FCSTD DOCUMENT  (FreeCAD 1.0R39319 (Git))
Label: VectoraCNC
License: All rights reserved
LicenseURL: https://en.wikipedia.org/wiki/All_rights_reserved
objects: Part::FeaturePython×161, Part::Feature×121, Sketcher::SketchObject×120, PartDesign::Body×96, PartDesign::Pad×71, PartDesign::FeatureBase×57, App::Part×42, PartDesign::Pocket×41, PartDesign::Hole×31, PartDesign::LinearPattern×14, PartDesign::ShapeBinder×12, PartDesign::Chamfer×5, PartDesign::PolarPattern×4, PartDesign::Revolution×2, PartDesign::Fillet×2, PartDesign::Thickness×2, PartDesign::SubtractiveHelix×1, Measure::MeasureRadius×1, App::DocumentObjectGroup×1
note: 1245 computed .brp shape members not serialized (recipe doc carries the construction recipe); baked Part::Feature solids carry a one-line shape summary decoded from their .brp

FEATURE [Sketcher::SketchObject] Sketch
  ArcFitTolerance = 1e-06
  AttachmentSupport = -> [Origin]
  FullyConstrained = true
  MakeInternals = false
  MapMode = 5
  Placement = pos=(0,0,0) rot=(1,0,0;1.5708rad)
  sketch-geometry (1):
    g0: Circle CenterX=0 CenterY=0 CenterZ=0 NormalX=0 NormalY=0 NormalZ=1 AngleXU=0 Radius=5
  constraints (2):
    c: Diameter(g0) = 10
    c: Coincident(g0,g-1)
FEATURE [PartDesign::Pad] Pad
  Direction = (0,-1,0)
  Length = 440
  Length2 = 10
  Profile = -> Sketch [Edge1]
  ReferenceAxis = -> Sketch [N_Axis]
  Refine = true
  Suppressed = false
  Type = 0
FEATURE [PartDesign::Body] Body  label="10mmx400mm"
  AllowCompound = false
  Group = -> [Sketch,Pad]
  Origin = -> Origin
  Tip = -> Pad
FEATURE [Sketcher::SketchObject] Sketch001
  ArcFitTolerance = 1e-06
  AttachmentSupport = -> [Origin004]
  FullyConstrained = true
  MakeInternals = false
  MapMode = 5
  Placement = pos=(0,0,0) rot=(1,0,0;1.5708rad)
  sketch-geometry (18):
    g0: LineSegment [constr] StartX=-10 StartY=-10 StartZ=0 EndX=10 EndY=-10 EndZ=0
    g1: LineSegment [constr] StartX=10 StartY=-10 StartZ=0 EndX=10 EndY=10 EndZ=0
    g2: LineSegment StartX=10 StartY=10 StartZ=0 EndX=3.1 EndY=10 EndZ=0
    g3: LineSegment [constr] StartX=-10 StartY=10 StartZ=0 EndX=-10 EndY=-10 EndZ=0
    g4: GeomPoint [constr] X=0 Y=0 Z=0
    g5: LineSegment StartX=-3.1 StartY=10 StartZ=0 EndX=-3.1 EndY=8 EndZ=0
    g6: LineSegment StartX=-3.1 StartY=8 StartZ=0 EndX=-5.5 EndY=8 EndZ=0
    g7: LineSegment StartX=-5.5 StartY=8 StartZ=0 EndX=-5.5 EndY=6.3 EndZ=0
    g8: LineSegment StartX=-5.5 StartY=6.3 StartZ=0 EndX=-3.1 EndY=3.9 EndZ=0
    g9: LineSegment StartX=-3.1 StartY=3.9 StartZ=0 EndX=3.1 EndY=3.9 EndZ=0
    g10: LineSegment StartX=3.1 StartY=3.9 StartZ=0 EndX=5.5 EndY=6.3 EndZ=0
    g11: LineSegment StartX=5.5 StartY=6.3 StartZ=0 EndX=5.5 EndY=8 EndZ=0
    g12: LineSegment StartX=5.5 StartY=8 StartZ=0 EndX=3.1 EndY=8 EndZ=0
    g13: LineSegment StartX=3.1 StartY=8 StartZ=0 EndX=3.1 EndY=10 EndZ=0
    g14: GeomPoint X=0 Y=3.9 Z=0
    g15: LineSegment StartX=-3.1 StartY=10 StartZ=0 EndX=-10 EndY=10 EndZ=0
    g16: LineSegment StartX=10 StartY=10 StartZ=0 EndX=0 EndY=0 EndZ=0
    g17: LineSegment StartX=0 StartY=0 StartZ=0 EndX=-10 EndY=10 EndZ=0
  constraints (47):
    c: Coincident(g0,g1)
    c: Coincident(g1,g2)
    c: Coincident(g15,g3)
    c: Coincident(g3,g0)
    c: Horizontal(g0)
    c: Vertical(g1)
    c: Vertical(g3)
    c: Symmetric(g2,g0,g4)
    c: Distance(g1,g3) = 20
    c: Distance(g0,g15) = 20
    c: Coincident(g4,g-1)
    c: Vertical(g5)
    c: Coincident(g5,g6)
    c: Horizontal(g6)
    c: Coincident(g6,g7)
    c: Vertical(g7)
    c: Coincident(g7,g8)
    c: Coincident(g8,g9)
    c: Horizontal(g9)
    c: Coincident(g9,g10)
    c: Coincident(g10,g11)
    c: Vertical(g11)
    c: Coincident(g11,g12)
    c: Horizontal(g12)
    c: Coincident(g12,g13)
    c: Vertical(g13)
    c: Angle(g9,g8) = 2.35619
    c: Angle(g10,g9) = 2.35619
    c: Equal(g7,g11)
    c: Equal(g12,g6)
    c: Horizontal(g5,g12)
    c: Symmetric(g9,g9,g14)
    c: PointOnObject(g14,g-2)
    c: Horizontal(g2)
    c: Horizontal(g15)
    c: Coincident(g5,g15)
    c: Coincident(g13,g2)
    c: Horizontal(g5,g2)
    c: Distance(g13,g13) = 2
    c: DistanceX(g6,g11) = 11
    c: DistanceX(g5,g2) = 6.2
    c: DistanceY(g9,g11) = 4.1
    c: Vertical(g5,g8)
    c: Coincident(g16,g1)
    c: Coincident(g16,g4)
    c: Coincident(g17,g4)
    c: Coincident(g17,g3)
FEATURE [PartDesign::Pad] Pad001
  Direction = (0,-1,2e-16)
  Length = 10
  Length2 = 10
  Profile = -> Sketch001
  ReferenceAxis = -> Sketch001 [N_Axis]
  Refine = true
  Suppressed = false
  Type = 0
FEATURE [PartDesign::PolarPattern] PolarPattern
  Angle = 360
  Axis = -> Sketch001 [N_Axis]
  BaseFeature = -> Pad001
  Mode = 0
  Occurrences = 4
  Offset = 120
  Originals = -> [Pad001]
  Refine = true
  Suppressed = false
  TransformMode = 0
FEATURE [Sketcher::SketchObject] Sketch002
  ArcFitTolerance = 1e-06
  AttachmentSupport = -> [PolarPattern]
  FullyConstrained = true
  MakeInternals = false
  MapMode = 5
  Placement = pos=(0,-10,0) rot=(1,0,0;1.5708rad)
  sketch-geometry (3):
    g0: GeomPoint X=0 Y=0 Z=0
    g1: GeomPoint X=0 Y=0 Z=0
    g2: Circle CenterX=0 CenterY=0 CenterZ=0 NormalX=0 NormalY=0 NormalZ=1 AngleXU=0 Radius=3.52328
  constraints (4):
    c: Coincident(g1,g0)
    c: Coincident(g0,g-1)
    c: Coincident(g2,g0)
    c: Diameter(g2) = 7.04656
FEATURE [PartDesign::Hole] Hole
  BaseFeature = -> PolarPattern
  CustomThreadClearance = 0
  Depth = 25
  DepthType = 0
  Diameter = 5
  DrillForDepth = false
  DrillPoint = 1
  DrillPointAngle = 118
  HoleCutCountersinkAngle = 90
  HoleCutCustomValues = false
  HoleCutDepth = 0
  HoleCutDiameter = 0
  HoleCutType = 0
  ModelThread = false
  Profile = -> Sketch002
  Refine = true
  Suppressed = false
  Tapered = false
  TaperedAngle = 90
  ThreadClass = 0
  ThreadDepth = 25
  ThreadDepthType = 0
  ThreadDirection = 0
  ThreadFit = 0
  ThreadSize = 0
  ThreadType = 0
  Threaded = false
  UseCustomThreadClearance = false
FEATURE [PartDesign::Body] Body001  label="2020"
  AllowCompound = false
  Group = -> [Sketch001,Pad001,PolarPattern,Sketch002,Hole]
  Origin = -> Origin004
  Tip = -> Hole
FEATURE [Sketcher::SketchObject] Sketch003
  ArcFitTolerance = 1e-06
  AttachmentSupport = -> [Origin012]
  FullyConstrained = true
  MakeInternals = false
  MapMode = 5
  sketch-geometry (1):
    g0: Circle CenterX=0 CenterY=0 CenterZ=0 NormalX=0 NormalY=0 NormalZ=1 AngleXU=0 Radius=4
  constraints (2):
    c: Diameter(g0) = 8
    c: Coincident(g0,g-1)
FEATURE [PartDesign::Pad] Pad003
  Direction = (0,0,1)
  Length = 10
  Length2 = 10
  Profile = -> Sketch003
  ReferenceAxis = -> Sketch003 [N_Axis]
  Refine = true
  Suppressed = false
  Type = 0
FEATURE [Sketcher::SketchObject] Sketch004
  ArcFitTolerance = 1e-06
  AttachmentSupport = -> [Origin012]
  ExternalGeometry = -> [Pad003]
  FullyConstrained = true
  MakeInternals = false
  MapMode = 5
  Placement = pos=(0,0,0) rot=(0.57735,0.57735,0.57735;2.0944rad)
  sketch-geometry (4):
    g0: LineSegment StartX=4 StartY=0 StartZ=0 EndX=4 EndY=1 EndZ=0
    g1: LineSegment StartX=4 StartY=1 StartZ=0 EndX=3 EndY=1 EndZ=0
    g2: LineSegment StartX=3 StartY=1 StartZ=0 EndX=3 EndY=0 EndZ=0
    g3: LineSegment StartX=3 StartY=0 StartZ=0 EndX=4 EndY=0 EndZ=0
  constraints (11):
    c: Coincident(g0,g1)
    c: Coincident(g1,g2)
    c: Coincident(g2,g3)
    c: Coincident(g3,g0)
    c: Vertical(g0)
    c: Vertical(g2)
    c: Horizontal(g1)
    c: Horizontal(g3)
    c: Distance(g0,g2) = 1
    c: Distance(g1,g3) = 1
    c: Coincident(g0,g-9)
FEATURE [PartDesign::SubtractiveHelix] SubtractiveHelix
  Angle = 0
  Axis = (0,0,1)
  Base = (0,0,0)
  BaseFeature = -> Pad003
  Growth = 0
  HasBeenEdited = true
  Height = 100
  LeftHanded = false
  Mode = 0
  Outside = false
  Pitch = 2
  Profile = -> Sketch004
  ReferenceAxis = -> Sketch004 [V_Axis]
  Refine = true
  Suppressed = false
  Tolerance = 0.1
  Turns = 50
FEATURE [PartDesign::Body] Body004  label="T8 Lead Screw"
  AllowCompound = false
  Group = -> [Sketch003,Pad003,Sketch004,SubtractiveHelix]
  Origin = -> Origin012
  Tip = -> SubtractiveHelix
FEATURE [Sketcher::SketchObject] Sketch005
  ArcFitTolerance = 1e-06
  AttachmentSupport = -> [Origin014]
  FullyConstrained = true
  MakeInternals = false
  MapMode = 5
  sketch-geometry (2):
    g0: Circle CenterX=0 CenterY=0 CenterZ=0 NormalX=0 NormalY=0 NormalZ=1 AngleXU=0 Radius=9.5
    g1: Circle CenterX=0 CenterY=0 CenterZ=0 NormalX=0 NormalY=0 NormalZ=1 AngleXU=0 Radius=5
  constraints (4):
    c: Diameter(g0) = 19
    c: Coincident(g0,g-1)
    c: Diameter(g1) = 10
    c: Coincident(g1,g0)
FEATURE [PartDesign::Pad] Pad004
  Direction = (0,0,1)
  Length = 55
  Length2 = 10
  Profile = -> Sketch005
  ReferenceAxis = -> Sketch005 [N_Axis]
  Refine = true
  Suppressed = false
  Type = 0
FEATURE [PartDesign::Body] Body005  label="LM10UU"
  AllowCompound = false
  Group = -> [Sketch005,Pad004]
  Origin = -> Origin014
  Tip = -> Pad004
FEATURE [Sketcher::SketchObject] Sketch006
  ArcFitTolerance = 1e-06
  AttachmentSupport = -> [Origin016]
  FullyConstrained = true
  MakeInternals = false
  MapMode = 5
  sketch-geometry (2):
    g0: Circle CenterX=0 CenterY=0 CenterZ=0 NormalX=0 NormalY=0 NormalZ=1 AngleXU=0 Radius=11
    g1: Circle CenterX=0 CenterY=0 CenterZ=0 NormalX=0 NormalY=0 NormalZ=1 AngleXU=0 Radius=4
  constraints (4):
    c: Diameter(g0) = 22
    c: Coincident(g0,g-1)
    c: Diameter(g1) = 8
    c: Coincident(g1,g0)
FEATURE [PartDesign::Pad] Pad005
  Direction = (0,0,1)
  Length = 7
  Length2 = 10
  Profile = -> Sketch006
  ReferenceAxis = -> Sketch006 [N_Axis]
  Refine = true
  Suppressed = false
  Type = 0
FEATURE [PartDesign::Body] Body006  label="608ZZ"
  AllowCompound = false
  Group = -> [Sketch006,Pad005]
  Origin = -> Origin016
  Tip = -> Pad005
FEATURE [PartDesign::FeatureBase] Clone005
  BaseFeature = -> Body005
  Suppressed = false
FEATURE [PartDesign::Body] Body010  label="LM10UU001"
  AllowCompound = false
  Group = -> [Clone005]
  Origin = -> Origin024
  Tip = -> Clone005
FEATURE [PartDesign::ShapeBinder] CopyClone005
  TraceSupport = false
FEATURE [Sketcher::SketchObject] Sketch007
  ArcFitTolerance = 1e-06
  AttachmentSupport = -> [CopyClone005]
  ExternalGeometry = -> [CopyClone005]
  FullyConstrained = true
  MakeInternals = false
  MapMode = 5
  Placement = pos=(0,0,0) rot=(1,0,0;3.14159rad)
  sketch-geometry (8):
    g0: ArcOfCircle CenterX=0 CenterY=0 CenterZ=0 NormalX=0 NormalY=0 NormalZ=1 AngleXU=0 Radius=16 StartAngle=0 EndAngle=3.14159
    g1: LineSegment StartX=-16 StartY=2e-15 StartZ=0 EndX=-28 EndY=2.2e-15 EndZ=0
    g2: LineSegment StartX=-28 StartY=2.2e-15 StartZ=0 EndX=-28 EndY=-13 EndZ=0
    g3: LineSegment StartX=-28 StartY=-13 StartZ=0 EndX=28 EndY=-13 EndZ=0
    g4: LineSegment StartX=28 StartY=-13 StartZ=0 EndX=28 EndY=0 EndZ=0
    g5: LineSegment StartX=28 StartY=0 StartZ=0 EndX=16 EndY=0 EndZ=0
    g6: GeomPoint X=0 Y=-13 Z=0
    g7: Circle CenterX=0 CenterY=0 CenterZ=0 NormalX=0 NormalY=0 NormalZ=1 AngleXU=0 Radius=9.6
  constraints (20):
    c: Radius(g0) = 16
    c: Coincident(g0,g-3)
    c: PointOnObject(g0,g-1)
    c: PointOnObject(g0,g-1)
    c: Perpendicular(g0,g1) = 4.71239
    c: Coincident(g1,g2)
    c: Coincident(g2,g3)
    c: Horizontal(g3)
    c: Coincident(g3,g4)
    c: PointOnObject(g4,g-1)
    c: Vertical(g4)
    c: Coincident(g4,g5)
    c: Coincident(g5,g0)
    c: Vertical(g2)
    c: Symmetric(g3,g3,g6)
    c: PointOnObject(g6,g-2)
    c: Distance(g-3,g3) = 3.5
    c: DistanceX(g3,g3) = 56
    c: Coincident(g7,g0)
    c: Distance(g7,g-3) = 0.1
FEATURE [PartDesign::Pad] Pad006
  Direction = (0,0,-1)
  Length = 10
  Length2 = 10
  Profile = -> Sketch007
  ReferenceAxis = -> Sketch007 [N_Axis]
  Refine = true
  Suppressed = false
  Type = 3
  UpToFace = -> Clone005 [Face4]
FEATURE [PartDesign::FeatureBase] Clone007
  BaseFeature = -> Body005
  Suppressed = false
FEATURE [PartDesign::Body] Body013  label="LM10UU002"
  AllowCompound = false
  Group = -> [Clone007]
  Origin = -> Origin056
  Tip = -> Clone007
FEATURE [PartDesign::FeatureBase] Clone008
  BaseFeature = -> Body005
  Suppressed = false
FEATURE [PartDesign::Body] Body014  label="LM10UU003"
  AllowCompound = false
  Group = -> [Clone008]
  Origin = -> Origin058
  Tip = -> Clone008
FEATURE [PartDesign::FeatureBase] Clone009
  BaseFeature = -> Body005
  Suppressed = false
FEATURE [PartDesign::Body] Body015  label="LM10UU004"
  AllowCompound = false
  Group = -> [Clone009]
  Origin = -> Origin060
  Tip = -> Clone009
FEATURE [Sketcher::SketchObject] Sketch008
  ArcFitTolerance = 1e-06
  AttachmentSupport = -> [Pad006]
  ExternalGeometry = -> [Pad006]
  FullyConstrained = true
  MakeInternals = false
  MapMode = 5
  Placement = pos=(0,-1.6e-15,0) rot=(1,0,0;1.5708rad)
  sketch-geometry (7):
    g0: GeomPoint X=-22 Y=47.5 Z=0
    g1: GeomPoint X=-22 Y=7.5 Z=0
    g2: GeomPoint X=22 Y=7.5 Z=0
    g3: GeomPoint X=22 Y=47.5 Z=0
    g4: GeomPoint [constr] X=22 Y=27.5 Z=0
    g5: GeomPoint [constr] X=-22 Y=27.5 Z=0
    g6: LineSegment [constr] StartX=-22 StartY=47.5 StartZ=0 EndX=-22 EndY=7.5 EndZ=0
  constraints (11):
    c: Symmetric(g-5,g-6,g5)
    c: Symmetric(g-9,g-10,g4)
    c: Vertical(g2,g3)
    c: Vertical(g3,g4)
    c: Horizontal(g0,g3)
    c: Horizontal(g1,g2)
    c: Coincident(g6,g0)
    c: Coincident(g6,g1)
    c: Symmetric(g6,g6,g5)
    c: DistanceY(g6,g6) = 40
    c: Vertical(g6)
FEATURE [PartDesign::Hole] Hole001
  BaseFeature = -> Pad006
  CustomThreadClearance = 0
  Depth = 25
  DepthType = 0
  Diameter = 1.2
  DrillForDepth = false
  DrillPoint = 1
  DrillPointAngle = 118
  HoleCutCountersinkAngle = 90
  HoleCutCustomValues = true
  HoleCutDepth = 0.1
  HoleCutDiameter = 1.3
  HoleCutType = 4
  ModelThread = false
  Profile = -> Sketch008
  Refine = true
  Suppressed = false
  Tapered = false
  TaperedAngle = 90
  ThreadClass = 0
  ThreadDepth = 25
  ThreadDepthType = 0
  ThreadDirection = 0
  ThreadFit = 0
  ThreadSize = 0
  ThreadType = 1
  Threaded = false
  UseCustomThreadClearance = false
FEATURE [PartDesign::Body] Body011  label="BearingHolder"
  AllowCompound = false
  Group = -> [CopyClone005,Sketch007,Pad006,Sketch008,Hole001]
  Origin = -> Origin028
  Tip = -> Hole001
FEATURE [PartDesign::FeatureBase] Clone006
  BaseFeature = -> Body011
  Suppressed = false
FEATURE [PartDesign::Body] Body012  label="BearingHolder002"
  AllowCompound = false
  Group = -> [Clone006]
  Origin = -> Origin054
  Tip = -> Clone006
FEATURE [PartDesign::FeatureBase] Clone010
  BaseFeature = -> Body011
  Suppressed = false
FEATURE [PartDesign::Body] Body016  label="BearingHolder003"
  AllowCompound = false
  Group = -> [Clone010]
  Origin = -> Origin062
  Tip = -> Clone010
FEATURE [PartDesign::FeatureBase] Clone011
  BaseFeature = -> Body011
  Suppressed = false
FEATURE [PartDesign::Body] Body017  label="BearingHolder004"
  AllowCompound = false
  Group = -> [Clone011]
  Origin = -> Origin064
  Tip = -> Clone011
FEATURE [PartDesign::FeatureBase] Clone012
  BaseFeature = -> Body011
  Suppressed = false
FEATURE [PartDesign::Body] Body018  label="BearingHolder001"
  AllowCompound = false
  Group = -> [Clone012]
  Origin = -> Origin066
  Tip = -> Clone012
FEATURE [App::Part] Part002  label="Bearing001"
  Group = -> [Body010,Body018]
  Origin = -> Origin026
  Placement = pos=(0,0,100) rot=(0,0,1;0rad)
FEATURE [App::Part] Part009  label="Bearing002"
  Group = -> [Body012,Body013]
  Origin = -> Origin068
FEATURE [App::Part] Part010  label="Bearing003"
  Group = -> [Body016,Body014]
  Origin = -> Origin070
  Placement = pos=(200,0,100) rot=(0,0,1;0rad)
FEATURE [App::Part] Part011  label="Bearing004"
  Group = -> [Body017,Body015]
  Origin = -> Origin072
  Placement = pos=(200,0,0) rot=(0,0,1;0rad)
FEATURE [App::Part] Part008  label="Bearings"
  Group = -> [Part002,Part009,Part010,Part011]
  Origin = -> Origin052
  Placement = pos=(12.5,40,-23) rot=(0.57735,0.57735,0.57735;2.0944rad)
FEATURE [Sketcher::SketchObject] Sketch145
  ArcFitTolerance = 1e-06
  AttachmentSupport = -> [XY_Plane957]
  FullyConstrained = true
  MakeInternals = false
  MapMode = 5
  sketch-geometry (2):
    g0: Circle CenterX=0 CenterY=0 CenterZ=0 NormalX=0 NormalY=0 NormalZ=1 AngleXU=0 Radius=9.5
    g1: Circle CenterX=0 CenterY=0 CenterZ=0 NormalX=0 NormalY=0 NormalZ=1 AngleXU=0 Radius=2.5
  constraints (4):
    c: Diameter(g0) = 19
    c: Coincident(g0,g-1)
    c: Diameter(g1) = 5
    c: Coincident(g1,g0)
FEATURE [PartDesign::Pad] Pad067
  Direction = (0,0,1)
  Length = 25
  Length2 = 10
  Profile = -> Sketch145
  ReferenceAxis = -> Sketch145 [N_Axis]
  Suppressed = false
  Type = 0
FEATURE [PartDesign::Hole] Hole015
  BaseFeature = -> Pad067
  CustomThreadClearance = 0
  Depth = 12.5
  DepthType = 0
  Diameter = 8
  DrillForDepth = false
  DrillPoint = 1
  DrillPointAngle = 118
  HoleCutCountersinkAngle = 90
  HoleCutCustomValues = false
  HoleCutDepth = 0
  HoleCutDiameter = 6.1
  HoleCutType = 0
  ModelThread = false
  Profile = -> Pad067 [Edge6]
  Suppressed = false
  Tapered = false
  TaperedAngle = 90
  ThreadClass = 0
  ThreadDepth = 12.5
  ThreadDepthType = 0
  ThreadDirection = 0
  ThreadFit = 0
  ThreadSize = 0
  ThreadType = 0
  Threaded = false
  UseCustomThreadClearance = false
FEATURE [Sketcher::SketchObject] Sketch146
  ArcFitTolerance = 1e-06
  AttachmentSupport = -> [YZ_Plane957]
  ExternalGeometry = -> [Hole015]
  FullyConstrained = true
  MakeInternals = false
  MapMode = 5
  Placement = pos=(0,0,0) rot=(0.57735,0.57735,0.57735;2.0944rad)
  sketch-geometry (4):
    g0: Circle CenterX=0 CenterY=18.75 CenterZ=0 NormalX=0 NormalY=0 NormalZ=1 AngleXU=0 Radius=1.5
    g1: Circle CenterX=0 CenterY=6.25 CenterZ=0 NormalX=0 NormalY=0 NormalZ=1 AngleXU=0 Radius=1.5
    g2: GeomPoint X=0 Y=25 Z=0
    g3: GeomPoint X=0 Y=12.5 Z=0
  constraints (6):
    c: Symmetric(g-5,g-5,g2)
    c: Symmetric(g-4,g-4,g3)
    c: Symmetric(g3,g-1,g1)
    c: Symmetric(g2,g3,g0)
    c: Equal(g0,g1)
    c: Diameter(g0) = 3
FEATURE [PartDesign::Pocket] Pocket056
  BaseFeature = -> Hole015
  Direction = (-1,0,0)
  Length = 5
  Length2 = 5
  Profile = -> Sketch146
  ReferenceAxis = -> Sketch146 [N_Axis]
  Suppressed = false
  Type = 1
FEATURE [PartDesign::Body] Body055  label="Coupling 5x8"
  AllowCompound = false
  Group = -> [Sketch145,Pad067,Hole015,Sketch146,Pocket056]
  Origin = -> Origin957
  Tip = -> Pocket056
FEATURE [Sketcher::SketchObject] Sketch150
  ArcFitTolerance = 1e-06
  AttachmentSupport = -> [YZ_Plane960]
  FullyConstrained = true
  MakeInternals = false
  MapMode = 5
  Placement = pos=(0,0,0) rot=(0.57735,0.57735,0.57735;2.0944rad)
  sketch-geometry (8):
    g0: LineSegment StartX=0 StartY=0 StartZ=0 EndX=0 EndY=15 EndZ=0
    g1: LineSegment StartX=0 StartY=15 StartZ=0 EndX=5.1 EndY=15 EndZ=0
    g2: LineSegment StartX=5.1 StartY=15 StartZ=0 EndX=5.1 EndY=13.5 EndZ=0
    g3: LineSegment StartX=5.1 StartY=13.5 StartZ=0 EndX=11 EndY=13.5 EndZ=0
    g4: LineSegment StartX=11 StartY=13.5 StartZ=0 EndX=11 EndY=10 EndZ=0
    g5: LineSegment StartX=11 StartY=10 StartZ=0 EndX=5.1 EndY=10 EndZ=0
    g6: LineSegment StartX=5.1 StartY=10 StartZ=0 EndX=5.1 EndY=0 EndZ=0
    g7: LineSegment StartX=5.1 StartY=0 StartZ=0 EndX=0 EndY=0 EndZ=0
  constraints (23):
    c: Vertical(g0)
    c: Coincident(g0,g1)
    c: Horizontal(g1)
    c: Coincident(g1,g2)
    c: Vertical(g2)
    c: Coincident(g2,g3)
    c: Horizontal(g3)
    c: Coincident(g3,g4)
    c: Vertical(g4)
    c: Coincident(g4,g5)
    c: Horizontal(g5)
    c: Coincident(g5,g6)
    c: PointOnObject(g6,g-1)
    c: Vertical(g6)
    c: Coincident(g6,g7)
    c: Coincident(g7,g0)
    c: Coincident(g0,g-1)
    c: Vertical(g5,g2)
    c: Distance(g2,g2) = 1.5
    c: Distance(g4,g4) = 3.5
    c: DistanceY(g6,g6) = 10
    c: DistanceX(g-1,g3) = 11
    c: DistanceX(g1,g1) = 5.1
FEATURE [PartDesign::Revolution] Revolution007
  Angle = 360
  Angle2 = 60
  Axis = (0,0,1)
  Base = (0,0,0)
  Placement = pos=(0,0,0) rot=(1,1,1;2.0944rad)
  Profile = -> Sketch150
  ReferenceAxis = -> Sketch150 [V_Axis]
  Refine = true
  Reversed = true
  Suppressed = false
  Type = 0
FEATURE [Sketcher::SketchObject] Sketch151
  ArcFitTolerance = 1e-06
  AttachmentSupport = -> [Revolution007]
  FullyConstrained = true
  MakeInternals = false
  MapMode = 5
  Placement = pos=(-3.3e-15,0,15) rot=(0,0,-1;1.5708rad)
  sketch-geometry (2):
    g0: Circle CenterX=0 CenterY=0 CenterZ=0 NormalX=0 NormalY=0 NormalZ=1 AngleXU=0 Radius=4
    g1: Circle CenterX=8 CenterY=0 CenterZ=0 NormalX=0 NormalY=0 NormalZ=1 AngleXU=0 Radius=1.75
  constraints (5):
    c: Coincident(g0,g-1)
    c: PointOnObject(g1,g-1)
    c: DistanceX(g-1,g1) = 8
    c: Diameter(g0) = 8
    c: Diameter(g1) = 3.5
FEATURE [PartDesign::Pocket] Pocket057
  BaseFeature = -> Revolution007
  Direction = (0,0,-1)
  Length = 5
  Length2 = 5
  Placement = pos=(0,0,0) rot=(1,1,1;2.0944rad)
  Profile = -> Sketch151
  ReferenceAxis = -> Sketch151 [N_Axis]
  Refine = true
  Suppressed = false
  Type = 1
FEATURE [PartDesign::PolarPattern] PolarPattern010
  Angle = 360
  Axis = -> Sketch151 [N_Axis]
  BaseFeature = -> Pocket057
  Mode = 0
  Occurrences = 4
  Offset = 120
  Originals = -> [Pocket057]
  Placement = pos=(0,0,0) rot=(1,1,1;2.0944rad)
  Refine = true
  Suppressed = false
  TransformMode = 0
FEATURE [PartDesign::Body] Body058  label="T8 Nut"
  AllowCompound = false
  Group = -> [Sketch150,Revolution007,Sketch151,Pocket057,PolarPattern010]
  Origin = -> Origin960
  Tip = -> PolarPattern010
FEATURE [PartDesign::FeatureBase] Clone013
  BaseFeature = -> Body058
  Suppressed = false
FEATURE [PartDesign::Body] Body059  label="T8 Nut001"
  AllowCompound = false
  Group = -> [Clone013]
  Origin = -> Origin1200
  Tip = -> Clone013
FEATURE [PartDesign::FeatureBase] Clone014
  BaseFeature = -> Body004
  Suppressed = false
FEATURE [PartDesign::LinearPattern] LinearPattern001
  BaseFeature = -> Clone014
  Direction = -> Z_Axis963
  Length = 290
  Mode = 1
  Occurrences = 30
  Offset = 10
  Refine = true
  Suppressed = false
  TransformMode = 1
FEATURE [PartDesign::Body] Body060  label="T8 Lead Screw001"
  AllowCompound = false
  Group = -> [Clone014,LinearPattern001]
  Origin = -> Origin1204
  Placement = pos=(-100,140,-23) rot=(0,1,0;1.5708rad)
  Tip = -> LinearPattern001
FEATURE [PartDesign::FeatureBase] Clone015
  BaseFeature = -> Body001
  Suppressed = false
FEATURE [PartDesign::ShapeBinder] CopyClone013
  TraceSupport = false
FEATURE [Sketcher::SketchObject] Sketch152
  ArcFitTolerance = 1e-06
  AttachmentSupport = -> [CopyClone013]
  ExternalGeometry = -> [CopyClone013]
  FullyConstrained = true
  MakeInternals = false
  MapMode = 5
  Placement = pos=(-6.7e-15,-1.1e-15,10) rot=(1,0,0;3.14159rad)
  sketch-geometry (7):
    g0: Circle CenterX=0 CenterY=0 CenterZ=0 NormalX=0 NormalY=0 NormalZ=1 AngleXU=0 Radius=5.25
    g1: LineSegment StartX=-13 StartY=28 StartZ=0 EndX=0 EndY=28 EndZ=0
    g2: LineSegment StartX=0 StartY=28 StartZ=0 EndX=4.9e-15 EndY=16 EndZ=0
    g3: ArcOfCircle CenterX=0 CenterY=0 CenterZ=0 NormalX=0 NormalY=0 NormalZ=1 AngleXU=0 Radius=16 StartAngle=4.71239 EndAngle=7.85398
    g4: LineSegment StartX=-2.9e-15 StartY=-16 StartZ=0 EndX=-2.2e-15 EndY=-28 EndZ=0
    g5: LineSegment StartX=-2.2e-15 StartY=-28 StartZ=0 EndX=-13 EndY=-28 EndZ=0
    g6: LineSegment StartX=-13 StartY=-28 StartZ=0 EndX=-13 EndY=28 EndZ=0
  constraints (18):
    c: Coincident(g0,g-4)
    c: Distance(g-4,g0) = 0.15
    c: PointOnObject(g1,g-2)
    c: Horizontal(g1)
    c: Coincident(g1,g2)
    c: Perpendicular(g2,g3) = 4.71239
    c: PointOnObject(g3,g-2)
    c: Perpendicular(g3,g4) = 4.71239
    c: Coincident(g4,g5)
    c: Horizontal(g5)
    c: Coincident(g5,g6)
    c: Coincident(g6,g1)
    c: Vertical(g6)
    c: DistanceX(g1,g1) = 13
    c: Coincident(g3,g0)
    c: Radius(g3) = 16
    c: DistanceY(g2,g2) = 12
    c: Equal(g4,g2)
FEATURE [PartDesign::Pad] Pad068
  Direction = (0,0,-1)
  Length = 60
  Length2 = 10
  Profile = -> Sketch152
  ReferenceAxis = -> Sketch152 [N_Axis]
  Refine = true
  Suppressed = false
  Type = 0
FEATURE [Sketcher::SketchObject] Sketch153
  ArcFitTolerance = 1e-06
  AttachmentSupport = -> [Pad068]
  ExternalGeometry = -> [Pad068]
  FullyConstrained = true
  MakeInternals = false
  MapMode = 5
  Placement = pos=(4.8e-15,0,0) rot=(0.57735,0.57735,0.57735;2.0944rad)
  sketch-geometry (7):
    g0: GeomPoint X=-22 Y=2.5 Z=0
    g1: GeomPoint X=-22 Y=-42.5 Z=0
    g2: GeomPoint [constr] X=22 Y=10 Z=0
    g3: GeomPoint X=22 Y=2.5 Z=0
    g4: GeomPoint X=22 Y=-42.5 Z=0
    g5: GeomPoint [constr] X=-22 Y=10 Z=0
    g6: GeomPoint [constr] X=-22 Y=-20 Z=0
  constraints (10):
    c: Symmetric(g-7,g-7,g2)
    c: Vertical(g2,g3)
    c: Vertical(g3,g4)
    c: Vertical(g0,g1)
    c: Horizontal(g0,g3)
    c: Horizontal(g1,g4)
    c: DistanceY(g4,g3) = 45
    c: Symmetric(g-13,g-13,g5)
    c: Symmetric(g-13,g-12,g6)
    c: Symmetric(g0,g1,g6)
FEATURE [PartDesign::Hole] Hole016
  BaseFeature = -> Pad068
  CustomThreadClearance = 0
  Depth = 25
  DepthType = 0
  Diameter = 1.2
  DrillForDepth = false
  DrillPoint = 1
  DrillPointAngle = 118
  HoleCutCountersinkAngle = 90
  HoleCutCustomValues = true
  HoleCutDepth = 0.1
  HoleCutDiameter = 1.3
  HoleCutType = 4
  ModelThread = false
  Profile = -> Sketch153
  Refine = true
  Suppressed = false
  Tapered = false
  TaperedAngle = 90
  ThreadClass = 0
  ThreadDepth = 25
  ThreadDepthType = 0
  ThreadDirection = 0
  ThreadFit = 0
  ThreadSize = 0
  ThreadType = 1
  Threaded = false
  UseCustomThreadClearance = false
FEATURE [PartDesign::Hole] Hole017
  BaseFeature = -> Hole016
  CustomThreadClearance = 0
  Depth = 25
  DepthType = 0
  Diameter = 4.7
  DrillForDepth = false
  DrillPoint = 1
  DrillPointAngle = 118
  HoleCutCountersinkAngle = 90
  HoleCutCustomValues = false
  HoleCutDepth = 0
  HoleCutDiameter = 0
  HoleCutType = 0
  ModelThread = false
  Profile = -> Hole016 [Face4]
  Refine = true
  Suppressed = false
  Tapered = false
  TaperedAngle = 90
  ThreadClass = 0
  ThreadDepth = 25
  ThreadDepthType = 0
  ThreadDirection = 0
  ThreadFit = 0
  ThreadSize = 0
  ThreadType = 0
  Threaded = false
  UseCustomThreadClearance = false
FEATURE [PartDesign::Body] Body062  label="T8 Nut Holder"
  AllowCompound = false
  Group = -> [CopyClone013,Sketch152,Pad068,Sketch153,Hole016,Hole017]
  Origin = -> Origin1210
  Tip = -> Hole017
FEATURE [App::Part] Part012  label="LeadScrew"
  Group = -> [Body059,Body062]
  Origin = -> Origin1202
  Placement = pos=(35.6,220.5,-10) rot=(0.57735,0.57735,-0.57735;2.0944rad)
FEATURE [PartDesign::Pad] Pad069
  BaseFeature = -> Clone015
  Direction = (0,1,-2e-16)
  Length = 290
  Length2 = 10
  Profile = -> Clone015 [Face4]
  Refine = true
  Suppressed = false
  Type = 0
FEATURE [PartDesign::Body] Body061  label="2020x300"
  AllowCompound = false
  Group = -> [Clone015,Pad069]
  Origin = -> Origin1208
  Tip = -> Pad069
FEATURE [PartDesign::FeatureBase] Clone016 .. Clone019  x4 (patterned run collapsed; names and placements below)
  BaseFeature = -> Body061
  Suppressed = false
FEATURE [Sketcher::SketchObject] Sketch038
  ArcFitTolerance = 1e-06
  AttachmentSupport = -> [XY_Plane918]
  FullyConstrained = true
  MakeInternals = false
  MapMode = 5
  sketch-geometry (5):
    g0: LineSegment StartX=-21.15 StartY=-21.15 StartZ=0 EndX=21.15 EndY=-21.15 EndZ=0
    g1: LineSegment StartX=21.15 StartY=-21.15 StartZ=0 EndX=21.15 EndY=21.15 EndZ=0
    g2: LineSegment StartX=21.15 StartY=21.15 StartZ=0 EndX=-21.15 EndY=21.15 EndZ=0
    g3: LineSegment StartX=-21.15 StartY=21.15 StartZ=0 EndX=-21.15 EndY=-21.15 EndZ=0
    g4: GeomPoint [constr] X=0 Y=0 Z=0
  constraints (12):
    c: Coincident(g0,g1)
    c: Coincident(g1,g2)
    c: Coincident(g2,g3)
    c: Coincident(g3,g0)
    c: Horizontal(g0)
    c: Horizontal(g2)
    c: Vertical(g1)
    c: Vertical(g3)
    c: Symmetric(g2,g0,g4)
    c: Distance(g1,g3) = 42.3
    c: Distance(g0,g2) = 42.3
    c: Coincident(g4,g-1)
FEATURE [PartDesign::Pad] Pad021
  Direction = (0,0,1)
  Length = 40
  Length2 = 10
  Profile = -> Sketch038
  ReferenceAxis = -> Sketch038 [N_Axis]
  Refine = true
  Suppressed = false
  Type = 0
FEATURE [Sketcher::SketchObject] Sketch039
  ArcFitTolerance = 1e-06
  AttachmentSupport = -> [Pad021]
  ExternalGeometry = -> [Pad021]
  FullyConstrained = true
  MakeInternals = false
  MapMode = 5
  Placement = pos=(0,0,40) rot=(0,0,1;0rad)
  sketch-geometry (1):
    g0: Circle CenterX=-15.5 CenterY=15.5 CenterZ=0 NormalX=0 NormalY=0 NormalZ=1 AngleXU=0 Radius=1.5
  constraints (3):
    c: Diameter(g0) = 3
    c: DistanceX(g0,g-1) = 15.5
    c: DistanceY(g-1,g0) = 15.5
FEATURE [PartDesign::Pocket] Pocket007
  BaseFeature = -> Pad021
  Direction = (0,0,-1)
  Length = 5
  Length2 = 5
  Profile = -> Sketch039
  ReferenceAxis = -> Sketch039 [N_Axis]
  Refine = true
  Suppressed = false
  Type = 1
FEATURE [PartDesign::PolarPattern] PolarPattern007
  Angle = 360
  Axis = -> Sketch039 [N_Axis]
  BaseFeature = -> Pocket007
  Mode = 0
  Occurrences = 4
  Offset = 120
  Originals = -> [Pocket007]
  Refine = true
  Suppressed = false
  TransformMode = 0
FEATURE [Sketcher::SketchObject] Sketch040
  ArcFitTolerance = 1e-06
  AttachmentSupport = -> [PolarPattern007]
  FullyConstrained = true
  MakeInternals = false
  MapMode = 5
  Placement = pos=(0,0,40) rot=(0,0,1;0rad)
  sketch-geometry (2):
    g0: Circle CenterX=0 CenterY=0 CenterZ=0 NormalX=0 NormalY=0 NormalZ=1 AngleXU=0 Radius=11
    g1: Circle CenterX=0 CenterY=0 CenterZ=0 NormalX=0 NormalY=0 NormalZ=1 AngleXU=0 Radius=2.5
  constraints (4):
    c: Diameter(g0) = 22
    c: Coincident(g0,g-1)
    c: Diameter(g1) = 5
    c: Coincident(g1,g0)
FEATURE [PartDesign::Pad] Pad022
  BaseFeature = -> PolarPattern007
  Direction = (0,0,1)
  Length = 2
  Length2 = 10
  Profile = -> Sketch040
  ReferenceAxis = -> Sketch040 [N_Axis]
  Refine = true
  Suppressed = false
  Type = 0
FEATURE [PartDesign::Pad] Pad023
  BaseFeature = -> Pad022
  Direction = (0,0,1)
  Length = 23.5
  Length2 = 10
  Profile = -> Pad022 [Face14]
  Refine = true
  Suppressed = false
  Type = 0
FEATURE [Sketcher::SketchObject] Sketch041
  ArcFitTolerance = 1e-06
  AttachmentSupport = -> [Pad023]
  ExternalGeometry = -> [Pad023]
  FullyConstrained = true
  MakeInternals = false
  MapMode = 5
  Placement = pos=(0,0,63.5) rot=(0,0,1;0rad)
  sketch-geometry (2):
    g0: LineSegment StartX=-1.78536 StartY=1.75 StartZ=0 EndX=1.78536 EndY=1.75 EndZ=0
    g1: ArcOfCircle CenterX=0 CenterY=0 CenterZ=0 NormalX=0 NormalY=0 NormalZ=1 AngleXU=0 Radius=2.5 StartAngle=0.775397 EndAngle=2.3662
  constraints (6):
    c: PointOnObject(g0,g-3)
    c: Horizontal(g0)
    c: Coincident(g1,g-1)
    c: Coincident(g1,g0)
    c: Coincident(g1,g0)
    c: DistanceY(g-1,g0) = 1.75
FEATURE [PartDesign::Pocket] Pocket008
  BaseFeature = -> Pad023
  Direction = (0,0,-1)
  Length = 12
  Length2 = 5
  Profile = -> Sketch041
  ReferenceAxis = -> Sketch041 [N_Axis]
  Refine = true
  Suppressed = false
  Type = 0
FEATURE [PartDesign::Chamfer] Chamfer
  Angle = 45
  Base = -> Pocket008 [Edge5,Edge8,Edge1,Edge2]
  BaseFeature = -> Pocket008
  ChamferType = 0
  FlipDirection = false
  Refine = true
  Size = 5
  Size2 = 1
  SupportTransform = false
  Suppressed = false
  UseAllEdges = false
FEATURE [Sketcher::SketchObject] Sketch042
  ArcFitTolerance = 1e-06
  AttachmentSupport = -> [Chamfer]
  ExternalGeometry = -> [Chamfer]
  FullyConstrained = true
  MakeInternals = false
  MapMode = 5
  Placement = pos=(0,21.15,0) rot=(0,0.707107,0.707107;3.14159rad)
  sketch-geometry (4):
    g0: LineSegment StartX=-8.1 StartY=0 StartZ=0 EndX=8.1 EndY=0 EndZ=0
    g1: LineSegment StartX=8.1 StartY=0 StartZ=0 EndX=8.1 EndY=9.4 EndZ=0
    g2: LineSegment StartX=8.1 StartY=9.4 StartZ=0 EndX=-8.1 EndY=9.4 EndZ=0
    g3: LineSegment StartX=-8.1 StartY=9.4 StartZ=0 EndX=-8.1 EndY=0 EndZ=0
  constraints (11):
    c: Coincident(g0,g1)
    c: Coincident(g1,g2)
    c: Coincident(g2,g3)
    c: Coincident(g3,g0)
    c: Horizontal(g0)
    c: Horizontal(g2)
    c: Vertical(g1)
    c: Vertical(g3)
    c: Distance(g1,g3) = 16.2
    c: Distance(g0,g2) = 9.4
    c: Symmetric(g0,g0,g-1)
FEATURE [PartDesign::Pad] Pad024
  BaseFeature = -> Chamfer
  Direction = (0,1,-2e-16)
  Length = 10
  Length2 = 10
  Profile = -> Sketch042
  ReferenceAxis = -> Sketch042 [N_Axis]
  Refine = true
  Suppressed = false
  Type = 0
FEATURE [PartDesign::FeatureBase] Clone021
  BaseFeature = -> Body055
  Suppressed = false
FEATURE [PartDesign::Body] Body068  label="Coupling 5x8001"
  AllowCompound = false
  Group = -> [Clone021]
  Origin = -> Origin1222
  Placement = pos=(-115,139.5,-23) rot=(0,1,0;1.5708rad)
  Tip = -> Clone021
FEATURE [PartDesign::Pad] Pad070
  BaseFeature = -> Clone017
  Direction = (0,1,-2e-16)
  Length = 50
  Length2 = 10
  Profile = -> Clone017 [Face1]
  Refine = true
  Suppressed = false
  Type = 0
FEATURE [PartDesign::Pad] Pad071
  BaseFeature = -> Clone018
  Direction = (0,1,-2e-16)
  Length = 50
  Length2 = 10
  Profile = -> Clone018 [Face1]
  Refine = true
  Suppressed = false
  Type = 0
FEATURE [PartDesign::Pad] Pad072
  BaseFeature = -> Clone016
  Direction = (0,-1,0)
  Length = 50
  Length2 = 10
  Profile = -> Clone016 [Face3]
  Refine = true
  Suppressed = false
  Type = 0
FEATURE [PartDesign::Pad] Pad073
  BaseFeature = -> Clone019
  Direction = (0,-1,0)
  Length = 50
  Length2 = 10
  Profile = -> Clone019 [Face3]
  Refine = true
  Suppressed = false
  Type = 0
FEATURE [Sketcher::SketchObject] Sketch154
  ArcFitTolerance = 1e-06
  AttachmentSupport = -> [Origin006]
  FullyConstrained = true
  MakeInternals = false
  MapMode = 5
  Placement = pos=(0,0,0) rot=(1,0,0;1.5708rad)
  sketch-geometry (25):
    g0: LineSegment StartX=0 StartY=0 StartZ=0 EndX=-8 EndY=0 EndZ=0
    g1: LineSegment StartX=-8 StartY=0 StartZ=0 EndX=-15 EndY=7 EndZ=0
    g2: LineSegment StartX=-15 StartY=7 StartZ=0 EndX=-8 EndY=7 EndZ=0
    g3: LineSegment StartX=-8 StartY=7 StartZ=0 EndX=-8 EndY=5.4 EndZ=0
    g4: LineSegment StartX=7 StartY=7 StartZ=0 EndX=0 EndY=0 EndZ=0
    g5: LineSegment StartX=-1.5e-15 StartY=5.4 StartZ=0 EndX=-1.5e-15 EndY=7 EndZ=0
    g6: LineSegment StartX=-1.5e-15 StartY=7 StartZ=0 EndX=7 EndY=7 EndZ=0
    g7: GeomPoint [constr] X=-4 Y=0 Z=0
    g8: GeomPoint [constr] X=-4 Y=5.4 Z=0
    g9: LineSegment StartX=-26.5 StartY=5.4 StartZ=0 EndX=-22.5 EndY=5.4 EndZ=0
    g10: LineSegment StartX=-22.5 StartY=5.4 StartZ=0 EndX=-15.5 EndY=-1.6 EndZ=0
    g11: LineSegment StartX=-15.5 StartY=-1.6 StartZ=0 EndX=-22.5 EndY=-1.6 EndZ=0
    g12: LineSegment StartX=7.5 StartY=-1.6 StartZ=0 EndX=14.5 EndY=5.4 EndZ=0
    g13: LineSegment StartX=14.5 StartY=-1.6 StartZ=0 EndX=7.5 EndY=-1.6 EndZ=0
    g14: GeomPoint [constr] X=18.5 Y=5.4 Z=0
    g15: LineSegment StartX=18.5 StartY=5.4 StartZ=0 EndX=14.5 EndY=5.4 EndZ=0
    g16: LineSegment StartX=-26.5 StartY=5.4 StartZ=0 EndX=-26.5 EndY=9.4 EndZ=0
    g17: LineSegment StartX=-26.5 StartY=9.4 StartZ=0 EndX=-8 EndY=9.4 EndZ=0
    g18: LineSegment StartX=-8 StartY=9.4 StartZ=0 EndX=-8 EndY=5.4 EndZ=0
    g19: LineSegment StartX=-1.5e-15 StartY=5.4 StartZ=0 EndX=0 EndY=9.4 EndZ=0
    g20: LineSegment StartX=0 StartY=9.4 StartZ=0 EndX=18.5 EndY=9.4 EndZ=0
    g21: LineSegment StartX=18.5 StartY=9.4 StartZ=0 EndX=18.5 EndY=5.4 EndZ=0
    g22: LineSegment StartX=14.5 StartY=-1.6 StartZ=0 EndX=14.5 EndY=-5.6 EndZ=0
    g23: LineSegment StartX=14.5 StartY=-5.6 StartZ=0 EndX=-22.5 EndY=-5.6 EndZ=0
    g24: LineSegment StartX=-22.5 StartY=-5.6 StartZ=0 EndX=-22.5 EndY=-1.6 EndZ=0
  constraints (68):
    c: Coincident(g-1,g0)
    c: PointOnObject(g0,g-1)
    c: Coincident(g0,g1)
    c: Coincident(g1,g2)
    c: Horizontal(g2)
    c: Coincident(g2,g3)
    c: Vertical(g3)
    c: Coincident(g4,g0)
    c: Horizontal(g3,g5)
    c: Equal(g4,g1)
    c: Coincident(g5,g6)
    c: Coincident(g6,g4)
    c: Vertical(g5)
    c: Horizontal(g6)
    c: Horizontal(g5,g2)
    c: Symmetric(g0,g0,g7)
    c: Symmetric(g3,g5,g8)
    c: Coincident(g9,g10)
    c: Coincident(g10,g11)
    c: Coincident(g13,g12)
    c: Horizontal(g11)
    c: Horizontal(g13)
    c: Horizontal(g9)
    c: Coincident(g15,g14)
    c: Coincident(g15,g12)
    c: Horizontal(g15)
    c: Equal(g12,g4)
    c: Equal(g4,g10)
    c: Horizontal(g12,g5)
    c: Horizontal(g5,g9)
    c: Equal(g9,g15)
    c: DistanceX(g3,g5) = 8
    c: DistanceX(g1,g4) = 22
    c: Equal(g11,g2)
    c: Equal(g2,g6)
    c: Equal(g6,g13)
    c: DistanceX(g9,g14) = 45
    c: DistanceX(g8,g14) = 22.5
    c: Parallel(g4,g12)
    c: Parallel(g1,g10)
    c: Vertical(g0,g2)
    c: Coincident(g9,g16)
    c: Vertical(g16)
    c: Coincident(g16,g17)
    c: Horizontal(g17)
    c: Coincident(g17,g18)
    c: Coincident(g18,g3)
    c: Coincident(g5,g19)
    c: PointOnObject(g19,g-2)
    c: Coincident(g19,g20)
    c: Horizontal(g20)
    c: Coincident(g20,g21)
    c: Coincident(g21,g14)
    c: Vertical(g22)
    c: Coincident(g22,g23)
    c: Horizontal(g23)
    c: Coincident(g23,g24)
    c: Vertical(g24)
    c: DistanceY(g23,g16) = 15
    c: Equal(g16,g24)
    c: Vertical(g18)
    c: Vertical(g21)
    c: Horizontal(g19,g17)
    c: Distance(g18,g18) = 4
    c: Distance(g17,g2) = 2.4
    c: Coincident(g13,g22)
    c: Coincident(g24,g11)
    c: Distance(g15,g15) = 4
FEATURE [PartDesign::Pad] Pad074
  Direction = (0,-1,0)
  Length = 300
  Length2 = 10
  Profile = -> Sketch154
  ReferenceAxis = -> Sketch154 [N_Axis]
  Refine = true
  Suppressed = false
  Type = 0
FEATURE [PartDesign::LinearPattern] LinearPattern
  BaseFeature = -> Pad074
  Direction = -> Sketch154 [H_Axis]
  Length = 135
  Mode = 1
  Occurrences = 4
  Offset = 45
  Originals = -> [Pad074]
  Refine = true
  Suppressed = false
  TransformMode = 0
FEATURE [Sketcher::SketchObject] Sketch155
  ArcFitTolerance = 1e-06
  AttachmentSupport = -> [Origin1232]
  FullyConstrained = true
  MakeInternals = false
  MapMode = 5
  Placement = pos=(0,0,0) rot=(1,0,0;1.5708rad)
  sketch-geometry (5):
    g0: LineSegment StartX=-7.5 StartY=-5 StartZ=0 EndX=7.5 EndY=-5 EndZ=0
    g1: LineSegment StartX=7.5 StartY=-5 StartZ=0 EndX=7.5 EndY=5 EndZ=0
    g2: LineSegment StartX=7.5 StartY=5 StartZ=0 EndX=-7.5 EndY=5 EndZ=0
    g3: LineSegment StartX=-7.5 StartY=5 StartZ=0 EndX=-7.5 EndY=-5 EndZ=0
    g4: GeomPoint [constr] X=0 Y=0 Z=0
  constraints (12):
    c: Coincident(g0,g1)
    c: Coincident(g1,g2)
    c: Coincident(g2,g3)
    c: Coincident(g3,g0)
    c: Horizontal(g0)
    c: Horizontal(g2)
    c: Vertical(g1)
    c: Vertical(g3)
    c: Symmetric(g2,g0,g4)
    c: Distance(g1,g3) = 15
    c: Distance(g0,g2) = 10
    c: Coincident(g4,g-1)
FEATURE [PartDesign::Pad] Pad075
  Direction = (0,-1,2e-16)
  Length = 40
  Length2 = 10
  Profile = -> Sketch155
  ReferenceAxis = -> Sketch155 [N_Axis]
  Refine = true
  Suppressed = false
  Type = 0
FEATURE [Sketcher::SketchObject] Sketch156
  ArcFitTolerance = 1e-06
  AttachmentSupport = -> [Pad075]
  ExternalGeometry = -> [Pad075]
  FullyConstrained = true
  MakeInternals = false
  MapMode = 5
  Placement = pos=(0,1.1e-15,5) rot=(0,0,1;0rad)
  sketch-geometry (2):
    g0: GeomPoint [constr] X=-7.5 Y=-20 Z=0
    g1: GeomPoint X=0 Y=-20 Z=0
  constraints (3):
    c: Symmetric(g-4,g-4,g0)
    c: PointOnObject(g1,g-2)
    c: Horizontal(g0,g1)
FEATURE [PartDesign::Hole] Hole018
  BaseFeature = -> Pad075
  CustomThreadClearance = 0
  Depth = 25
  DepthType = 0
  Diameter = 1.2
  DrillForDepth = false
  DrillPoint = 1
  DrillPointAngle = 118
  HoleCutCountersinkAngle = 90
  HoleCutCustomValues = true
  HoleCutDepth = 0.1
  HoleCutDiameter = 1.3
  HoleCutType = 4
  ModelThread = false
  Profile = -> Sketch156
  Refine = true
  Suppressed = false
  Tapered = false
  TaperedAngle = 90
  ThreadClass = 0
  ThreadDepth = 25
  ThreadDepthType = 0
  ThreadDirection = 0
  ThreadFit = 0
  ThreadSize = 0
  ThreadType = 1
  Threaded = false
  UseCustomThreadClearance = false
FEATURE [PartDesign::ShapeBinder] CopyHole018
  Placement = pos=(0,-40,8.9e-15) rot=(0,0,1;0rad)
  TraceSupport = false
FEATURE [Sketcher::SketchObject] Sketch157
  ArcFitTolerance = 1e-06
  AttachmentSupport = -> [CopyHole018]
  ExternalGeometry = -> [CopyHole018]
  FullyConstrained = true
  MakeInternals = false
  MapMode = 5
  Placement = pos=(0,-40,8.9e-15) rot=(1,0,0;1.5708rad)
  sketch-geometry (9):
    g0: LineSegment StartX=-7.5 StartY=-1 StartZ=0 EndX=-16 EndY=-1 EndZ=0
    g1: LineSegment StartX=-16 StartY=-1 StartZ=0 EndX=-16 EndY=11 EndZ=0
    g2: LineSegment StartX=-16 StartY=11 StartZ=0 EndX=16 EndY=11 EndZ=0
    g3: LineSegment StartX=16 StartY=11 StartZ=0 EndX=16 EndY=-1 EndZ=0
    g4: LineSegment StartX=16 StartY=-1 StartZ=0 EndX=7.5 EndY=-1 EndZ=0
    g5: LineSegment StartX=7.5 StartY=-1 StartZ=0 EndX=7.5 EndY=5 EndZ=0
    g6: LineSegment StartX=7.5 StartY=5 StartZ=0 EndX=-7.5 EndY=5 EndZ=0
    g7: LineSegment StartX=-7.5 StartY=5 StartZ=0 EndX=-7.5 EndY=-1 EndZ=0
    g8: GeomPoint X=-16 Y=-5 Z=0
  constraints (25):
    c: PointOnObject(g0,g-6)
    c: Horizontal(g0)
    c: Coincident(g0,g1)
    c: Vertical(g1)
    c: Coincident(g1,g2)
    c: Horizontal(g2)
    c: Coincident(g2,g3)
    c: Vertical(g3)
    c: Coincident(g3,g4)
    c: PointOnObject(g4,g-4)
    c: Horizontal(g4)
    c: Coincident(g5,g-5)
    c: Coincident(g5,g6)
    c: Coincident(g6,g-6)
    c: Coincident(g6,g7)
    c: Coincident(g7,g0)
    c: DistanceY(g1,g1) = 12
    c: Horizontal(g0,g4)
    c: Horizontal(g4,g5)
    c: DistanceY(g8,g0) = 4
    c: Horizontal(g8,g-6)
    c: DistanceX(g2,g2) = 32
    c: Equal(g0,g4)
    c: Vertical(g8,g0)
    c: Vertical(g5)
FEATURE [PartDesign::Pad] Pad076
  Direction = (0,-1,2e-16)
  Length = 58.8
  Length2 = 10
  Placement = pos=(0,-40,8.9e-15) rot=(0,0,1;0rad)
  Profile = -> Sketch157
  ReferenceAxis = -> Sketch157 [N_Axis]
  Refine = true
  Reversed = true
  Suppressed = false
  Type = 0
FEATURE [Sketcher::SketchObject] Sketch158
  ArcFitTolerance = 1e-06
  AttachmentSupport = -> [Pad076]
  ExternalGeometry = -> [Pad076]
  FullyConstrained = true
  MakeInternals = false
  MapMode = 5
  Placement = pos=(0,-40,11) rot=(0,0,1;0rad)
  sketch-geometry (5):
    g0: GeomPoint X=-12.5 Y=41.9 Z=0
    g1: GeomPoint X=12.5 Y=41.9 Z=0
    g2: GeomPoint X=12.5 Y=16.9 Z=0
    g3: GeomPoint X=-12.5 Y=16.9 Z=0
    g4: GeomPoint [constr] X=4e-16 Y=29.4 Z=0
  constraints (8):
    c: Vertical(g0,g3)
    c: Vertical(g1,g2)
    c: Horizontal(g0,g1)
    c: Horizontal(g2,g3)
    c: DistanceY(g2,g1) = 25
    c: DistanceX(g3,g2) = 25
    c: Symmetric(g-6,g-5,g4)
    c: Symmetric(g0,g2,g4)
FEATURE [PartDesign::Hole] Hole019
  BaseFeature = -> Pad076
  CustomThreadClearance = 0
  Depth = 4
  DepthType = 0
  Diameter = 1.2
  DrillForDepth = false
  DrillPoint = 1
  DrillPointAngle = 118
  HoleCutCountersinkAngle = 90
  HoleCutCustomValues = false
  HoleCutDepth = 0
  HoleCutDiameter = 0
  HoleCutType = 0
  ModelThread = false
  Placement = pos=(0,-40,8.9e-15) rot=(0,0,1;0rad)
  Profile = -> Sketch158
  Refine = true
  Suppressed = false
  Tapered = false
  TaperedAngle = 90
  ThreadClass = 0
  ThreadDepth = 4
  ThreadDepthType = 0
  ThreadDirection = 0
  ThreadFit = 0
  ThreadSize = 0
  ThreadType = 1
  Threaded = false
  UseCustomThreadClearance = false
FEATURE [PartDesign::Body] Body073  label="MGN15H block"
  AllowCompound = false
  Group = -> [CopyHole018,Sketch157,Pad076,Sketch158,Hole019]
  Origin = -> Origin1234
  Tip = -> Hole019
FEATURE [PartDesign::LinearPattern] LinearPattern002
  BaseFeature = -> Hole018
  Direction = -> Y_Axis977
  Length = 320
  Mode = 1
  Occurrences = 9
  Offset = 40
  Refine = true
  Suppressed = false
  TransformMode = 1
FEATURE [PartDesign::Pocket] Pocket
  BaseFeature = -> LinearPattern002
  Direction = (0,-1,0)
  Length = 10
  Length2 = 5
  Profile = -> LinearPattern002 [Face1]
  Refine = true
  Suppressed = false
  Type = 0
FEATURE [PartDesign::Body] Body072  label="MGN15H rail"
  AllowCompound = false
  Group = -> [Sketch155,Pad075,Sketch156,Hole018,LinearPattern002,Pocket]
  Origin = -> Origin1232
  Tip = -> Pocket
FEATURE [PartDesign::FeatureBase] Clone
  BaseFeature = -> Body072
  Suppressed = false
FEATURE [PartDesign::Body] Body074  label="MGN15H rail002"
  AllowCompound = false
  Group = -> [Clone]
  Origin = -> Origin1236
  Placement = pos=(-117,54.5,-6) rot=(0,0,1;4.71239rad)
  Tip = -> Clone
FEATURE [PartDesign::FeatureBase] Clone025
  BaseFeature = -> Body072
  Suppressed = false
FEATURE [PartDesign::Body] Body075  label="MGN15H rail001"
  AllowCompound = false
  Group = -> [Clone025]
  Origin = -> Origin1238
  Placement = pos=(-117,224.5,-6) rot=(0,0,1;4.71239rad)
  Tip = -> Clone025
FEATURE [PartDesign::FeatureBase] Clone026
  BaseFeature = -> Body073
  Suppressed = false
FEATURE [PartDesign::Body] Body076  label="MGN15H block002"
  AllowCompound = false
  Group = -> [Clone026]
  Origin = -> Origin1240
  Placement = pos=(-50,296,-8) rot=(0,0,1;0rad)
  Tip = -> Clone026
FEATURE [PartDesign::FeatureBase] Clone027
  BaseFeature = -> Body073
  Suppressed = false
FEATURE [PartDesign::Body] Body077  label="MGN15H block001"
  AllowCompound = false
  Group = -> [Clone027]
  Origin = -> Origin1242
  Placement = pos=(120,296,-8) rot=(0,0,1;0rad)
  Tip = -> Clone027
FEATURE [PartDesign::LinearPattern] LinearPattern003
  BaseFeature = -> Pad071
  Direction = -> X_Axis969
  Length = 20
  Mode = 0
  Occurrences = 2
  Offset = 20
  Refine = true
  Reversed = true
  Suppressed = false
  TransformMode = 1
FEATURE [PartDesign::Body] Body065  label="2020x30003"
  AllowCompound = false
  Group = -> [Clone018,Pad071,LinearPattern003]
  Origin = -> Origin1216
  Placement = pos=(200,300,-43) rot=(0,0,1;1.5708rad)
  Tip = -> LinearPattern003
FEATURE [PartDesign::LinearPattern] LinearPattern004
  BaseFeature = -> Pad070
  Direction = -> X_Axis968
  Length = 20
  Mode = 0
  Occurrences = 2
  Offset = 20
  Refine = true
  Suppressed = false
  TransformMode = 1
FEATURE [PartDesign::Body] Body064  label="2020x30002"
  AllowCompound = false
  Group = -> [Clone017,Pad070,LinearPattern004]
  Origin = -> Origin1214
  Placement = pos=(200,-30,-43) rot=(0,0,1;1.5708rad)
  Tip = -> LinearPattern004
FEATURE [PartDesign::FeatureBase] Clone028
  BaseFeature = -> Body001
  Suppressed = false
FEATURE [PartDesign::FeatureBase] Clone029
  BaseFeature = -> Body001
  Suppressed = false
FEATURE [PartDesign::Pad] Pad077
  BaseFeature = -> Clone029
  Direction = (0,-1,0)
  Length = 350
  Length2 = 10
  Profile = -> Clone029 [Face5]
  Refine = true
  Reversed = true
  Suppressed = false
  Type = 0
FEATURE [PartDesign::Body] Body079
  AllowCompound = false
  Group = -> [Clone029,Pad077]
  Origin = -> Origin1246
  Placement = pos=(-50,-30,-23) rot=(0,0,1;0rad)
  Tip = -> Pad077
FEATURE [PartDesign::Pad] Pad078
  BaseFeature = -> Clone028
  Direction = (0,-1,0)
  Length = 350
  Length2 = 10
  Profile = -> Clone028 [Face5]
  Refine = true
  Reversed = true
  Suppressed = false
  Type = 0
FEATURE [PartDesign::Body] Body078
  AllowCompound = false
  Group = -> [Clone028,Pad078]
  Origin = -> Origin1244
  Placement = pos=(120,-30,-23) rot=(0,0,1;0rad)
  Tip = -> Pad078
FEATURE [PartDesign::FeatureBase] Clone030
  BaseFeature = -> Body073
  Suppressed = false
FEATURE [PartDesign::Body] Body080  label="MGN15H block003"
  AllowCompound = false
  Group = -> [Clone030]
  Origin = -> Origin1248
  Placement = pos=(-50,206,-8) rot=(0,0,1;0rad)
  Tip = -> Clone030
FEATURE [PartDesign::FeatureBase] Clone031
  BaseFeature = -> Body073
  Suppressed = false
FEATURE [PartDesign::Body] Body081  label="MGN15H block004"
  AllowCompound = false
  Group = -> [Clone031]
  Origin = -> Origin1250
  Placement = pos=(120,206,-8) rot=(0,0,1;0rad)
  Tip = -> Clone031
FEATURE [Sketcher::SketchObject] Sketch159
  ArcFitTolerance = 1e-06
  AttachmentSupport = -> [Origin1252]
  FullyConstrained = true
  MakeInternals = false
  MapMode = 5
  Placement = pos=(0,0,0) rot=(0.57735,0.57735,0.57735;2.0944rad)
  sketch-geometry (8):
    g0: LineSegment StartX=-3 StartY=0.5 StartZ=0 EndX=3 EndY=0.5 EndZ=0
    g1: LineSegment StartX=3 StartY=0.5 StartZ=0 EndX=3 EndY=7.1156e-12 EndZ=0
    g2: LineSegment StartX=3 StartY=7.1156e-12 StartZ=0 EndX=4.3 EndY=7.1156e-12 EndZ=0
    g3: LineSegment StartX=4.3 StartY=7.1156e-12 StartZ=0 EndX=1.8 EndY=-2.5 EndZ=0
    g4: LineSegment StartX=1.8 StartY=-2.5 StartZ=0 EndX=-1.8 EndY=-2.5 EndZ=0
    g5: LineSegment StartX=-1.8 StartY=-2.5 StartZ=0 EndX=-4.3 EndY=0 EndZ=0
    g6: LineSegment StartX=-4.3 StartY=0 StartZ=0 EndX=-3 EndY=0 EndZ=0
    g7: LineSegment StartX=-3 StartY=0 StartZ=0 EndX=-3 EndY=0.5 EndZ=0
  constraints (22):
    c: Coincident(g0,g1)
    c: Vertical(g1)
    c: Coincident(g1,g2)
    c: Horizontal(g2)
    c: Coincident(g2,g3)
    c: Coincident(g3,g4)
    c: Coincident(g4,g5)
    c: Coincident(g5,g6)
    c: Horizontal(g6)
    c: Coincident(g6,g7)
    c: Vertical(g7)
    c: Coincident(g0,g7)
    c: Symmetric(g0,g0,g-2)
    c: Symmetric(g3,g4,g-2)
    c: Equal(g5,g3)
    c: Equal(g6,g2)
    c: Distance(g7,g7) = 0.5
    c: DistanceX(g5,g2) = 8.6
    c: Distance(g0,g0) = 6
    c: DistanceY(g4,g0) = 3
    c: Angle(g6,g5) = 2.35619
    c: PointOnObject(g6,g-1)
FEATURE [PartDesign::Pad] Pad079
  Direction = (1,0,0)
  Length = 6
  Length2 = 10
  Profile = -> Sketch159
  ReferenceAxis = -> Sketch159 [N_Axis]
  Refine = true
  Suppressed = false
  Type = 0
FEATURE [PartDesign::Body] Body082  label="1515 tnut"
  AllowCompound = false
  Group = -> [Sketch159,Pad079]
  Origin = -> Origin1252
  Tip = -> Pad079
FEATURE [PartDesign::ShapeBinder] ShapeBinder
  Support = -> [LinearPattern003]
  TraceSupport = false
FEATURE [Sketcher::SketchObject] Sketch160
  ArcFitTolerance = 1e-06
  AttachmentSupport = -> [Origin1256]
  FullyConstrained = true
  MakeInternals = false
  MapMode = 5
  Placement = pos=(0,0,0) rot=(0.57735,0.57735,0.57735;2.0944rad)
  sketch-geometry (8):
    g0: LineSegment StartX=324 StartY=12 StartZ=0 EndX=324 EndY=-33 EndZ=0
    g1: LineSegment StartX=324 StartY=-33 StartZ=0 EndX=310 EndY=-33 EndZ=0
    g2: LineSegment StartX=310 StartY=-33 StartZ=0 EndX=310 EndY=-53 EndZ=0
    g3: LineSegment StartX=310 StartY=-53 StartZ=0 EndX=370 EndY=-53 EndZ=0
    g4: LineSegment StartX=370 StartY=-53 StartZ=0 EndX=370 EndY=-31.25 EndZ=0
    g5: LineSegment StartX=370 StartY=-31.25 StartZ=0 EndX=328 EndY=-31.25 EndZ=0
    g6: LineSegment StartX=328 StartY=-31.25 StartZ=0 EndX=328 EndY=12 EndZ=0
    g7: LineSegment StartX=328 StartY=12 StartZ=0 EndX=324 EndY=12 EndZ=0
  constraints (24):
    c: Vertical(g0)
    c: Coincident(g0,g1)
    c: Horizontal(g1)
    c: Coincident(g1,g2)
    c: Vertical(g2)
    c: Coincident(g2,g3)
    c: Horizontal(g3)
    c: Coincident(g3,g4)
    c: Vertical(g4)
    c: Coincident(g4,g5)
    c: Horizontal(g5)
    c: Coincident(g5,g6)
    c: Vertical(g6)
    c: Coincident(g6,g7)
    c: Coincident(g7,g0)
    c: Horizontal(g7)
    c: DistanceY(g2,g2) = 20
    c: Distance(g1,g6) = 18
    c: DistanceX(g7,g7) = 4
    c: DistanceY(g4,g4) = 21.75
    c: DistanceY(g0,g0) = 45
    c: Distance(g-1,g1) = 33
    c: DistanceX(g-1,g1) = 310
    c: DistanceX(g3,g3) = 60
FEATURE [PartDesign::Pad] Pad080
  Direction = (1,0,0)
  Length = 42.3
  Length2 = 10
  Profile = -> Sketch160
  ReferenceAxis = -> Sketch160 [N_Axis]
  Refine = true
  Reversed = true
  Suppressed = false
  Type = 0
FEATURE [Sketcher::SketchObject] Sketch162
  ArcFitTolerance = 1e-06
  AttachmentSupport = -> [Pad080]
  ExternalGeometry = -> [Pad080]
  FullyConstrained = true
  MakeInternals = false
  MapMode = 5
  Placement = pos=(0,324,0) rot=(1,0,0;1.5708rad)
  sketch-geometry (23):
    g0: GeomPoint [constr] X=-21.15 Y=-10.1 Z=0
    g1: ArcOfCircle CenterX=-36.65 CenterY=6.65 CenterZ=0 NormalX=0 NormalY=0 NormalZ=1 AngleXU=0 Radius=2 StartAngle=1.7e-15 EndAngle=3.14159
    g2: ArcOfCircle CenterX=-36.65 CenterY=4.15 CenterZ=0 NormalX=0 NormalY=0 NormalZ=1 AngleXU=0 Radius=2 StartAngle=3.14159 EndAngle=6.28319
    g3: LineSegment StartX=-34.65 StartY=6.65 StartZ=0 EndX=-34.65 EndY=4.15 EndZ=0
    g4: LineSegment StartX=-38.65 StartY=6.65 StartZ=0 EndX=-38.65 EndY=4.15 EndZ=0
    g5: ArcOfCircle CenterX=-36.65 CenterY=-24.35 CenterZ=0 NormalX=0 NormalY=0 NormalZ=1 AngleXU=0 Radius=2 StartAngle=-2.7e-15 EndAngle=3.14159
    g6: ArcOfCircle CenterX=-36.65 CenterY=-26.85 CenterZ=0 NormalX=0 NormalY=0 NormalZ=1 AngleXU=0 Radius=2 StartAngle=3.14159 EndAngle=6.28319
    g7: LineSegment StartX=-34.65 StartY=-24.35 StartZ=0 EndX=-34.65 EndY=-26.85 EndZ=0
    g8: LineSegment StartX=-38.65 StartY=-24.35 StartZ=0 EndX=-38.65 EndY=-26.85 EndZ=0
    g9: ArcOfCircle CenterX=-5.65 CenterY=-24.35 CenterZ=0 NormalX=0 NormalY=0 NormalZ=1 AngleXU=0 Radius=2 StartAngle=6e-16 EndAngle=3.14159
    g10: ArcOfCircle CenterX=-5.65 CenterY=-26.85 CenterZ=0 NormalX=0 NormalY=0 NormalZ=1 AngleXU=0 Radius=2 StartAngle=3.14159 EndAngle=6.28319
    g11: LineSegment StartX=-3.65 StartY=-24.35 StartZ=0 EndX=-3.65 EndY=-26.85 EndZ=0
    g12: LineSegment StartX=-7.65 StartY=-24.35 StartZ=0 EndX=-7.65 EndY=-26.85 EndZ=0
    g13: ArcOfCircle CenterX=-5.65 CenterY=6.65 CenterZ=0 NormalX=0 NormalY=0 NormalZ=1 AngleXU=0 Radius=2 StartAngle=1e-16 EndAngle=3.14159
    g14: ArcOfCircle CenterX=-5.65 CenterY=4.15 CenterZ=0 NormalX=0 NormalY=0 NormalZ=1 AngleXU=0 Radius=2 StartAngle=3.14159 EndAngle=6.28319
    g15: LineSegment StartX=-3.65 StartY=6.65 StartZ=0 EndX=-3.65 EndY=4.15 EndZ=0
    g16: LineSegment StartX=-7.65 StartY=6.65 StartZ=0 EndX=-7.65 EndY=4.15 EndZ=0
    g17: LineSegment [constr] StartX=0 StartY=-33 StartZ=0 EndX=0 EndY=11.05 EndZ=0
    g18: LineSegment [constr] StartX=0 StartY=11.05 StartZ=0 EndX=-42.3 EndY=11.05 EndZ=0
    g19: LineSegment [constr] StartX=-42.3 StartY=11.05 StartZ=0 EndX=-42.3 EndY=-31.25 EndZ=0
    g20: GeomPoint [constr] X=-21.15 Y=11.05 Z=0
    g21: GeomPoint [constr] X=-42.3 Y=-10.1 Z=0
    g22: Circle CenterX=-21.15 CenterY=-10.1 CenterZ=0 NormalX=0 NormalY=0 NormalZ=1 AngleXU=0 Radius=15
  constraints (53):
    c: Tangent(g1,g3) = 1.5708
    c: Tangent(g1,g4) = -1.5708
    c: Tangent(g2,g3) = 1.5708
    c: Tangent(g2,g4) = -1.5708
    c: Equal(g1,g2)
    c: Vertical(g3)
    c: Tangent(g5,g7) = 1.5708
    c: Tangent(g5,g8) = -1.5708
    c: Tangent(g6,g7) = 1.5708
    c: Tangent(g6,g8) = -1.5708
    c: Equal(g5,g6)
    c: Vertical(g7)
    c: Tangent(g9,g11) = 1.5708
    c: Tangent(g9,g12) = -1.5708
    c: Tangent(g10,g11) = 1.5708
    c: Tangent(g10,g12) = -1.5708
    c: Equal(g9,g10)
    c: Tangent(g13,g15) = 1.5708
    c: Tangent(g13,g16) = -1.5708
    c: Tangent(g14,g15) = 1.5708
    c: Tangent(g14,g16) = -1.5708
    c: Equal(g13,g14)
    c: Vertical(g15)
    c: Equal(g2,g14)
    c: Equal(g14,g10)
    c: Equal(g10,g6)
    c: Radius(g2) = 2
    c: Vertical(g12)
    c: Equal(g12,g7)
    c: Equal(g7,g3)
    c: Equal(g3,g16)
    c: DistanceY(g16,g16) = 2.5
    c: Vertical(g14,g9)
    c: Horizontal(g5,g9)
    c: DistanceX(g2,g14) = 31
    c: Horizontal(g14,g2)
    c: Vertical(g2,g5)
    c: Coincident(g17,g18)
    c: Coincident(g18,g19)
    c: Vertical(g17)
    c: Vertical(g19)
    c: Horizontal(g18)
    c: Coincident(g17,g-5)
    c: Equal(g18,g19)
    c: Symmetric(g18,g18,g20)
    c: Symmetric(g19,g19,g21)
    c: Horizontal(g21,g0)
    c: Vertical(g0,g20)
    c: DistanceY(g6,g2) = 31
    c: Diameter(g22) = 30
    c: Coincident(g22,g0)
    c: Coincident(g19,g-10)
    c: Symmetric(g13,g6,g0)
FEATURE [PartDesign::Pocket] Pocket058
  BaseFeature = -> Pad080
  Direction = (0,1,-2e-16)
  Length = 5
  Length2 = 5
  Profile = -> Sketch162
  ReferenceAxis = -> Sketch162 [N_Axis]
  Refine = true
  Suppressed = false
  Type = 0
FEATURE [Sketcher::SketchObject] Sketch163
  ArcFitTolerance = 1e-06
  AttachmentSupport = -> [Pocket058]
  ExternalGeometry = -> [Pocket058]
  FullyConstrained = true
  MakeInternals = false
  MapMode = 5
  Placement = pos=(0,0,-53) rot=(1,0,0;3.14159rad)
  sketch-geometry (6):
    g0: LineSegment StartX=-58.3 StartY=-310 StartZ=0 EndX=-58.3 EndY=-324 EndZ=0
    g1: LineSegment StartX=-58.3 StartY=-324 StartZ=0 EndX=16 EndY=-324 EndZ=0
    g2: LineSegment StartX=16 StartY=-324 StartZ=0 EndX=16 EndY=-310 EndZ=0
    g3: LineSegment StartX=16 StartY=-310 StartZ=0 EndX=-58.3 EndY=-310 EndZ=0
    g4: LineSegment [constr] StartX=-58.3 StartY=-310 StartZ=0 EndX=-42.3 EndY=-310 EndZ=0
    g5: LineSegment [constr] StartX=0 StartY=-310 StartZ=0 EndX=16 EndY=-310 EndZ=0
  constraints (16):
    c: Coincident(g0,g1)
    c: Coincident(g1,g2)
    c: Coincident(g2,g3)
    c: Coincident(g3,g0)
    c: Vertical(g0)
    c: Vertical(g2)
    c: Horizontal(g1)
    c: Horizontal(g3)
    c: PointOnObject(g-6,g3)
    c: Coincident(g4,g0)
    c: Coincident(g4,g-6)
    c: Coincident(g5,g-5)
    c: Coincident(g5,g2)
    c: Equal(g4,g5)
    c: DistanceX(g4,g4) = 16
    c: DistanceY(g0,g0) = 14
FEATURE [PartDesign::Pad] Pad081
  BaseFeature = -> Pocket058
  Direction = (0,0,-1)
  Length = 10
  Length2 = 10
  Profile = -> Sketch163
  ReferenceAxis = -> Sketch163 [N_Axis]
  Refine = true
  Suppressed = false
  Type = 3
  UpToFace = -> Pocket058 [Face5]
FEATURE [Sketcher::SketchObject] Sketch164
  ArcFitTolerance = 1e-06
  AttachmentSupport = -> [Pad081]
  ExternalGeometry = -> [Pad081]
  FullyConstrained = true
  MakeInternals = false
  MapMode = 5
  Placement = pos=(0,324,0) rot=(0,0.707107,0.707107;3.14159rad)
  sketch-geometry (2):
    g0: GeomPoint X=-8 Y=-43 Z=0
    g1: GeomPoint X=50.3 Y=-43 Z=0
  constraints (2):
    c: Symmetric(g-5,g-6,g1)
    c: Symmetric(g-9,g-10,g0)
FEATURE [PartDesign::Hole] Hole020
  BaseFeature = -> Pad081
  CustomThreadClearance = 0
  Depth = 16
  DepthType = 0
  Diameter = 1.2
  DrillForDepth = false
  DrillPoint = 1
  DrillPointAngle = 118
  HoleCutCountersinkAngle = 90
  HoleCutCustomValues = true
  HoleCutDepth = 0.1
  HoleCutDiameter = 1.3
  HoleCutType = 4
  ModelThread = false
  Profile = -> Sketch164
  Refine = true
  Suppressed = false
  Tapered = false
  TaperedAngle = 90
  ThreadClass = 0
  ThreadDepth = 16
  ThreadDepthType = 0
  ThreadDirection = 0
  ThreadFit = 0
  ThreadSize = 0
  ThreadType = 1
  Threaded = false
  UseCustomThreadClearance = false
FEATURE [PartDesign::Chamfer] Chamfer001
  Angle = 45
  Base = -> Hole020 [Edge34,Edge29]
  BaseFeature = -> Hole020
  ChamferType = 0
  FlipDirection = false
  Refine = true
  Size = 2.5
  Size2 = 1
  SupportTransform = false
  Suppressed = false
  UseAllEdges = false
FEATURE [PartDesign::Chamfer] Chamfer002
  Angle = 45
  Base = -> Chamfer001 [Edge27]
  BaseFeature = -> Chamfer001
  ChamferType = 0
  FlipDirection = false
  Refine = true
  Size = 2.5
  Size2 = 1
  SupportTransform = false
  Suppressed = false
  UseAllEdges = false
FEATURE [PartDesign::FeatureBase] Clone032
  BaseFeature = -> Body001
  Suppressed = false
FEATURE [PartDesign::FeatureBase] Clone034
  BaseFeature = -> Body001
  Suppressed = false
FEATURE [Sketcher::SketchObject] Sketch165
  ArcFitTolerance = 1e-06
  AttachmentSupport = -> [Origin1264]
  FullyConstrained = true
  MakeInternals = false
  MapMode = 5
  Placement = pos=(0,0,0) rot=(1,0,0;1.5708rad)
  sketch-geometry (5):
    g0: LineSegment StartX=-6 StartY=-4 StartZ=0 EndX=6 EndY=-4 EndZ=0
    g1: LineSegment StartX=6 StartY=-4 StartZ=0 EndX=6 EndY=4 EndZ=0
    g2: LineSegment StartX=6 StartY=4 StartZ=0 EndX=-6 EndY=4 EndZ=0
    g3: LineSegment StartX=-6 StartY=4 StartZ=0 EndX=-6 EndY=-4 EndZ=0
    g4: GeomPoint [constr] X=0 Y=0 Z=0
  constraints (12):
    c: Coincident(g0,g1)
    c: Coincident(g1,g2)
    c: Coincident(g2,g3)
    c: Coincident(g3,g0)
    c: Horizontal(g0)
    c: Horizontal(g2)
    c: Vertical(g1)
    c: Vertical(g3)
    c: Symmetric(g2,g0,g4)
    c: Distance(g1,g3) = 12
    c: Distance(g0,g2) = 8
    c: Coincident(g4,g-1)
FEATURE [PartDesign::Pad] Pad082
  Direction = (0,-1,0)
  Length = 25
  Length2 = 10
  Profile = -> Sketch165
  ReferenceAxis = -> Sketch165 [N_Axis]
  Refine = true
  Suppressed = false
  Type = 0
FEATURE [Sketcher::SketchObject] Sketch166
  ArcFitTolerance = 1e-06
  AttachmentSupport = -> [Pad082]
  ExternalGeometry = -> [Pad082]
  FullyConstrained = true
  MakeInternals = false
  MapMode = 5
  Placement = pos=(0,9e-16,4) rot=(0,0,1;0rad)
  sketch-geometry (2):
    g0: GeomPoint [constr] X=-6 Y=-12.5 Z=0
    g1: GeomPoint X=0 Y=-12.5 Z=0
  constraints (3):
    c: Symmetric(g-4,g-4,g0)
    c: PointOnObject(g1,g-2)
    c: Horizontal(g0,g1)
FEATURE [PartDesign::Hole] Hole021
  BaseFeature = -> Pad082
  CustomThreadClearance = 0
  Depth = 25
  DepthType = 0
  Diameter = 1.2
  DrillForDepth = false
  DrillPoint = 1
  DrillPointAngle = 118
  HoleCutCountersinkAngle = 90
  HoleCutCustomValues = true
  HoleCutDepth = 0.1
  HoleCutDiameter = 1.3
  HoleCutType = 4
  ModelThread = false
  Profile = -> Sketch166
  Refine = true
  Suppressed = false
  Tapered = false
  TaperedAngle = 90
  ThreadClass = 0
  ThreadDepth = 25
  ThreadDepthType = 0
  ThreadDirection = 0
  ThreadFit = 0
  ThreadSize = 0
  ThreadType = 1
  Threaded = false
  UseCustomThreadClearance = false
FEATURE [PartDesign::LinearPattern] LinearPattern005
  BaseFeature = -> Hole021
  Direction = -> Y_Axis993
  Length = 200
  Mode = 1
  Occurrences = 9
  Offset = 25
  Refine = true
  Suppressed = false
  TransformMode = 1
FEATURE [PartDesign::Pocket] Pocket059
  BaseFeature = -> LinearPattern005
  Direction = (0,-1,0)
  Length = 10
  Length2 = 5
  Profile = -> LinearPattern005 [Face1]
  Refine = true
  Suppressed = false
  Type = 0
FEATURE [PartDesign::Body] Body087  label="MGN12H rail"
  AllowCompound = false
  Group = -> [Sketch165,Pad082,Sketch166,Hole021,LinearPattern005,Pocket059]
  Origin = -> Origin1264
  Tip = -> Pocket059
FEATURE [PartDesign::ShapeBinder] CopyHole019
  Placement = pos=(0,-25,5.6e-15) rot=(0,0,1;0rad)
  Support = -> [Pocket059]
  TraceSupport = false
FEATURE [PartDesign::Pad] Pad084
  BaseFeature = -> Clone032
  Direction = (0,-1,0)
  Length = 250
  Length2 = 10
  Profile = -> Clone032 [Face5]
  Refine = true
  Reversed = true
  Suppressed = false
  Type = 0
FEATURE [PartDesign::LinearPattern] LinearPattern006
  BaseFeature = -> Pad084
  Direction = -> X_Axis990
  Length = 20
  Mode = 1
  Occurrences = 2
  Offset = 20
  Refine = true
  Suppressed = false
  TransformMode = 1
FEATURE [PartDesign::Pad] Pad085
  BaseFeature = -> Clone034
  Direction = (0,1,-2e-16)
  Length = 350
  Length2 = 10
  Profile = -> Clone034 [Face4]
  Refine = true
  Reversed = true
  Suppressed = false
  Type = 0
FEATURE [PartDesign::LinearPattern] LinearPattern007
  BaseFeature = -> Pad085
  Direction = -> Z_Axis992
  Length = 60
  Mode = 1
  Occurrences = 4
  Offset = 20
  Refine = true
  Suppressed = false
  TransformMode = 1
FEATURE [PartDesign::Body] Body086  label="2080x350"
  AllowCompound = false
  Group = -> [Clone034,Pad085,LinearPattern007]
  Origin = -> Origin1262
  Placement = pos=(210,260,147) rot=(0,0,1;4.71239rad)
  Tip = -> LinearPattern007
FEATURE [Sketcher::SketchObject] Sketch167
  ArcFitTolerance = 1e-06
  AttachmentSupport = -> [Origin1266]
  ExternalGeometry = -> [CopyHole019]
  FullyConstrained = true
  MakeInternals = false
  MapMode = 5
  Placement = pos=(0,0,0) rot=(1,0,0;1.5708rad)
  sketch-geometry (8):
    g0: LineSegment StartX=-13.5 StartY=9 StartZ=0 EndX=-13.5 EndY=-1 EndZ=0
    g1: LineSegment StartX=-13.5 StartY=-1 StartZ=0 EndX=-6 EndY=-1 EndZ=0
    g2: LineSegment StartX=-6 StartY=-1 StartZ=0 EndX=-6 EndY=4 EndZ=0
    g3: LineSegment StartX=-6 StartY=4 StartZ=0 EndX=6 EndY=4 EndZ=0
    g4: LineSegment StartX=6 StartY=4 StartZ=0 EndX=6 EndY=-1 EndZ=0
    g5: LineSegment StartX=6 StartY=-1 StartZ=0 EndX=13.5 EndY=-1 EndZ=0
    g6: LineSegment StartX=13.5 StartY=-1 StartZ=0 EndX=13.5 EndY=9 EndZ=0
    g7: LineSegment StartX=13.5 StartY=9 StartZ=0 EndX=-13.5 EndY=9 EndZ=0
  constraints (22):
    c: Coincident(g0,g1)
    c: PointOnObject(g1,g-6)
    c: Horizontal(g1)
    c: Coincident(g1,g2)
    c: Coincident(g2,g-6)
    c: Coincident(g2,g3)
    c: Coincident(g3,g-5)
    c: Coincident(g3,g4)
    c: Vertical(g4)
    c: Coincident(g4,g5)
    c: Horizontal(g5)
    c: Coincident(g5,g6)
    c: Vertical(g6)
    c: Coincident(g6,g7)
    c: Coincident(g7,g0)
    c: Horizontal(g7)
    c: Vertical(g0)
    c: Equal(g1,g5)
    c: Equal(g4,g2)
    c: DistanceY(g-6,g0) = 13
    c: DistanceX(g7,g7) = 27
    c: DistanceY(g-6,g0) = 3
FEATURE [PartDesign::Pad] Pad086
  Direction = (0,-1,2e-16)
  Length = 45.4
  Length2 = 10
  Profile = -> Sketch167
  ReferenceAxis = -> Sketch167 [N_Axis]
  Refine = true
  Suppressed = false
  Type = 0
FEATURE [Sketcher::SketchObject] Sketch168
  ArcFitTolerance = 1e-06
  AttachmentSupport = -> [Pad086]
  ExternalGeometry = -> [Pad086]
  FullyConstrained = true
  MakeInternals = false
  MapMode = 5
  Placement = pos=(0,2e-15,9) rot=(0,0,1;0rad)
  sketch-geometry (10):
    g0: GeomPoint [constr] X=-1.88037e-11 Y=-22.7 Z=0
    g1: LineSegment [constr] StartX=-10 StartY=-32.7 StartZ=0 EndX=10 EndY=-32.7 EndZ=0
    g2: LineSegment [constr] StartX=10 StartY=-32.7 StartZ=0 EndX=10 EndY=-12.7 EndZ=0
    g3: LineSegment [constr] StartX=10 StartY=-12.7 StartZ=0 EndX=-10 EndY=-12.7 EndZ=0
    g4: LineSegment [constr] StartX=-10 StartY=-12.7 StartZ=0 EndX=-10 EndY=-32.7 EndZ=0
    g5: GeomPoint [constr] X=-1.88037e-11 Y=-22.7 Z=0
    g6: GeomPoint X=-10 Y=-12.7 Z=0
    g7: GeomPoint X=10 Y=-12.7 Z=0
    g8: GeomPoint X=10 Y=-32.7 Z=0
    g9: GeomPoint X=-10 Y=-32.7 Z=0
  constraints (17):
    c: Symmetric(g-5,g-6,g0)
    c: Coincident(g1,g2)
    c: Coincident(g2,g3)
    c: Coincident(g3,g4)
    c: Coincident(g4,g1)
    c: Horizontal(g1)
    c: Horizontal(g3)
    c: Vertical(g2)
    c: Vertical(g4)
    c: Symmetric(g3,g1,g5)
    c: Coincident(g5,g0)
    c: Equal(g3,g4)
    c: DistanceX(g3,g3) = 20
    c: Coincident(g6,g3)
    c: Coincident(g7,g2)
    c: Coincident(g8,g1)
    c: Coincident(g9,g1)
FEATURE [PartDesign::Hole] Hole022
  BaseFeature = -> Pad086
  CustomThreadClearance = 0
  Depth = 4
  DepthType = 0
  Diameter = 1.2
  DrillForDepth = false
  DrillPoint = 1
  DrillPointAngle = 118
  HoleCutCountersinkAngle = 90
  HoleCutCustomValues = false
  HoleCutDepth = 0
  HoleCutDiameter = 0
  HoleCutType = 0
  ModelThread = false
  Profile = -> Sketch168
  Refine = true
  Suppressed = false
  Tapered = false
  TaperedAngle = 90
  ThreadClass = 0
  ThreadDepth = 4
  ThreadDepthType = 0
  ThreadDirection = 0
  ThreadFit = 0
  ThreadSize = 0
  ThreadType = 1
  Threaded = false
  UseCustomThreadClearance = false
FEATURE [PartDesign::Body] Body088  label="MGN12H block"
  AllowCompound = false
  Group = -> [CopyHole019,Sketch167,Pad086,Sketch168,Hole022]
  Origin = -> Origin1266
  Tip = -> Hole022
FEATURE [PartDesign::FeatureBase] Clone036
  BaseFeature = -> Body072
  Suppressed = false
FEATURE [PartDesign::Body] Body090  label="MGN15H rail003"
  AllowCompound = false
  Group = -> [Clone036]
  Origin = -> Origin1272
  Placement = pos=(-100,245.5,207) rot=(0.58,0.58,-0.58;2.0944rad)
  Tip = -> Clone036
FEATURE [PartDesign::FeatureBase] Clone037
  BaseFeature = -> Body072
  Suppressed = false
FEATURE [PartDesign::Body] Body091  label="MGN15H rail004"
  AllowCompound = false
  Group = -> [Clone037]
  Origin = -> Origin1274
  Placement = pos=(-100,245.5,147) rot=(0.58,0.58,-0.58;2.0944rad)
  Tip = -> Clone037
FEATURE [PartDesign::FeatureBase] Clone040
  BaseFeature = -> Body001
  Suppressed = false
FEATURE [PartDesign::Pad] Pad087
  BaseFeature = -> Clone040
  Direction = (0,1,-2e-16)
  Length = 150
  Length2 = 10
  Profile = -> Clone040 [Face4]
  Refine = true
  Reversed = true
  Suppressed = false
  Type = 0
FEATURE [PartDesign::LinearPattern] LinearPattern008
  BaseFeature = -> Pad087
  Direction = -> X_Axis1002
  Length = 60
  Mode = 1
  Occurrences = 4
  Offset = 20
  Suppressed = false
  TransformMode = 1
FEATURE [Sketcher::SketchObject] Sketch169
  ArcFitTolerance = 1e-06
  AttachmentSupport = -> [Origin1345]
  FullyConstrained = true
  MakeInternals = false
  MapMode = 5
  Placement = pos=(0,0,0) rot=(1,0,0;1.5708rad)
  sketch-geometry (15):
    g0: LineSegment StartX=0 StartY=0 StartZ=0 EndX=0 EndY=53 EndZ=0
    g1: LineSegment StartX=0 StartY=53 StartZ=0 EndX=17.5 EndY=53 EndZ=0
    g2: LineSegment StartX=17.5 StartY=53 StartZ=0 EndX=31.5 EndY=67 EndZ=0
    g3: LineSegment StartX=31.5 StartY=67 StartZ=0 EndX=58.5 EndY=67 EndZ=0
    g4: LineSegment StartX=58.5 StartY=67 StartZ=0 EndX=72.5 EndY=53 EndZ=0
    g5: LineSegment StartX=72.5 StartY=53 StartZ=0 EndX=90 EndY=53 EndZ=0
    g6: LineSegment StartX=90 StartY=53 StartZ=0 EndX=90 EndY=35.5 EndZ=0
    g7: LineSegment StartX=90 StartY=0 StartZ=0 EndX=0 EndY=0 EndZ=0
    g8: LineSegment [constr] StartX=17.5 StartY=53 StartZ=0 EndX=31.5 EndY=53 EndZ=0
    g9: LineSegment [constr] StartX=72.5 StartY=53 StartZ=0 EndX=58.5 EndY=53 EndZ=0
    g10: ArcOfCircle CenterX=45 CenterY=34 CenterZ=0 NormalX=0 NormalY=0 NormalZ=1 AngleXU=0 Radius=26 StartAngle=0.0577244 EndAngle=6.22546
    g11: GeomPoint X=45 Y=67 Z=0
    g12: LineSegment StartX=70.9567 StartY=35.5 StartZ=0 EndX=90 EndY=35.5 EndZ=0
    g13: LineSegment StartX=90 StartY=32.5 StartZ=0 EndX=70.9567 EndY=32.5 EndZ=0
    g14: LineSegment StartX=90 StartY=32.5 StartZ=0 EndX=90 EndY=0 EndZ=0
  constraints (43):
    c: Coincident(g-1,g0)
    c: PointOnObject(g0,g-2)
    c: Coincident(g0,g1)
    c: Horizontal(g1)
    c: Coincident(g1,g2)
    c: Coincident(g2,g3)
    c: Horizontal(g3)
    c: Coincident(g3,g4)
    c: Coincident(g4,g5)
    c: Horizontal(g5)
    c: Coincident(g5,g6)
    c: PointOnObject(g14,g-1)
    c: Coincident(g14,g7)
    c: Coincident(g7,g0)
    c: Equal(g2,g4)
    c: Equal(g1,g5)
    c: DistanceY(g0,g0) = 53
    c: DistanceY(g-1,g2) = 67
    c: DistanceX(g3,g3) = 27
    c: DistanceX(g1,g4) = 55
    c: Coincident(g8,g1)
    c: Horizontal(g8)
    c: Coincident(g9,g4)
    c: Horizontal(g9)
    c: Equal(g9,g8)
    c: Vertical(g8,g2)
    c: Vertical(g3,g9)
    c: DistanceX(g7,g7) = 90
    c: Symmetric(g3,g3,g11)
    c: Vertical(g11,g10)
    c: Horizontal(g12)
    c: Horizontal(g13)
    c: Diameter(g10) = 52
    c: Coincident(g12,g10)
    c: Coincident(g13,g10)
    c: Vertical(g6)
    c: Vertical(g14)
    c: Coincident(g12,g6)
    c: Coincident(g13,g14)
    c: Vertical(g6,g13)
    c: DistanceY(g13,g6) = 3
    c: Vertical(g10,g10)
    c: Distance(g10,g3) = 7
FEATURE [PartDesign::Pad] Pad088
  Direction = (0,-1,2e-16)
  Length = 40
  Length2 = 10
  Profile = -> Sketch169
  ReferenceAxis = -> Sketch169 [N_Axis]
  Suppressed = false
  Type = 0
FEATURE [Sketcher::SketchObject] Sketch170
  ArcFitTolerance = 1e-06
  AttachmentSupport = -> [Pad088]
  ExternalGeometry = -> [Pad088]
  FullyConstrained = true
  MakeInternals = false
  MapMode = 5
  Placement = pos=(0,1.17e-14,53) rot=(0,0,1;0rad)
  sketch-geometry (8):
    g0: GeomPoint X=10 Y=-10 Z=0
    g1: GeomPoint X=10 Y=-30 Z=0
    g2: GeomPoint X=80 Y=-10 Z=0
    g3: GeomPoint X=80 Y=-30 Z=0
    g4: GeomPoint [constr] X=0 Y=-20 Z=0
    g5: GeomPoint [constr] X=10 Y=-20 Z=0
    g6: LineSegment [constr] StartX=10 StartY=-20 StartZ=0 EndX=17.5 EndY=-20 EndZ=0
    g7: LineSegment [constr] StartX=72.5 StartY=-20 StartZ=0 EndX=80 EndY=-20 EndZ=0
  constraints (15):
    c: Vertical(g2,g3)
    c: Vertical(g0,g1)
    c: DistanceY(g1,g0) = 20
    c: Horizontal(g0,g2)
    c: Horizontal(g1,g3)
    c: DistanceX(g0,g2) = 70
    c: Symmetric(g-7,g-7,g4)
    c: Symmetric(g0,g1,g5)
    c: Horizontal(g5,g4)
    c: Coincident(g6,g5)
    c: Symmetric(g-8,g-8,g6)
    c: Symmetric(g-3,g-3,g7)
    c: Horizontal(g7)
    c: Vertical(g7,g2)
    c: Equal(g7,g6)
FEATURE [PartDesign::Hole] Hole023
  BaseFeature = -> Pad088
  CustomThreadClearance = 0
  Depth = 240.618
  DepthType = 1
  Diameter = 1.2
  DrillForDepth = false
  DrillPoint = 1
  DrillPointAngle = 118
  HoleCutCountersinkAngle = 90
  HoleCutCustomValues = false
  HoleCutDepth = 0
  HoleCutDiameter = 0
  HoleCutType = 0
  ModelThread = false
  Profile = -> Sketch170
  Suppressed = false
  Tapered = false
  TaperedAngle = 90
  ThreadClass = 0
  ThreadDepth = 240.618
  ThreadDepthType = 0
  ThreadDirection = 0
  ThreadFit = 0
  ThreadSize = 0
  ThreadType = 1
  Threaded = false
  UseCustomThreadClearance = false
FEATURE [PartDesign::Body] Body095  label="Spindle clamp"
  AllowCompound = false
  Group = -> [Sketch169,Pad088,Sketch170,Hole023]
  Origin = -> Origin1345
  Placement = pos=(-15,0,0) rot=(0,0,1;0rad)
  Tip = -> Hole023
FEATURE [Sketcher::SketchObject] Sketch171
  ArcFitTolerance = 1e-06
  AttachmentSupport = -> [Origin1349]
  FullyConstrained = true
  MakeInternals = false
  MapMode = 5
  sketch-geometry (14):
    g0: LineSegment StartX=0 StartY=199 StartZ=0 EndX=28 EndY=199 EndZ=0
    g1: LineSegment StartX=28 StartY=199 StartZ=0 EndX=28 EndY=174 EndZ=0
    g2: LineSegment StartX=28 StartY=174 StartZ=0 EndX=13 EndY=174 EndZ=0
    g3: LineSegment StartX=13 StartY=174 StartZ=0 EndX=13 EndY=166 EndZ=0
    g4: LineSegment StartX=13 StartY=166 StartZ=0 EndX=26 EndY=166 EndZ=0
    g5: LineSegment StartX=26 StartY=166 StartZ=0 EndX=26 EndY=46 EndZ=0
    g6: LineSegment StartX=26 StartY=46 StartZ=0 EndX=13 EndY=46 EndZ=0
    g7: LineSegment StartX=13 StartY=46 StartZ=0 EndX=13 EndY=42 EndZ=0
    g8: LineSegment StartX=13 StartY=42 StartZ=0 EndX=8 EndY=42 EndZ=0
    g9: LineSegment StartX=8 StartY=42 StartZ=0 EndX=8 EndY=14 EndZ=0
    g10: LineSegment StartX=8 StartY=14 StartZ=0 EndX=9.5 EndY=14 EndZ=0
    g11: LineSegment StartX=9.5 StartY=14 StartZ=0 EndX=9.5 EndY=0 EndZ=0
    g12: LineSegment StartX=9.5 StartY=0 StartZ=0 EndX=0 EndY=0 EndZ=0
    g13: LineSegment StartX=0 StartY=0 StartZ=0 EndX=0 EndY=199 EndZ=0
  constraints (41):
    c: PointOnObject(g0,g-2)
    c: Horizontal(g0)
    c: Coincident(g0,g1)
    c: Vertical(g1)
    c: Coincident(g1,g2)
    c: Horizontal(g2)
    c: Coincident(g2,g3)
    c: Vertical(g3)
    c: Coincident(g3,g4)
    c: Horizontal(g4)
    c: Coincident(g4,g5)
    c: Vertical(g5)
    c: Coincident(g5,g6)
    c: Horizontal(g6)
    c: Coincident(g6,g7)
    c: Vertical(g7)
    c: Coincident(g7,g8)
    c: Horizontal(g8)
    c: Coincident(g8,g9)
    c: Vertical(g9)
    c: Coincident(g9,g10)
    c: Horizontal(g10)
    c: Coincident(g10,g11)
    c: Vertical(g11)
    c: Coincident(g11,g12)
    c: Horizontal(g12)
    c: Coincident(g12,g13)
    c: Coincident(g13,g0)
    c: DistanceY(g5,g5) = 120
    c: Distance(g0,g4) = 33
    c: DistanceY(g11,g0) = 199
    c: DistanceY(g11,g7) = 42
    c: DistanceY(g1,g1) = 25
    c: DistanceY(g9,g9) = 28
    c: DistanceX(g-1,g7) = 13
    c: DistanceX(g-1,g5) = 26
    c: DistanceX(g12,g12) = 9.5
    c: DistanceX(g-1,g9) = 8
    c: Coincident(g12,g-1)
    c: DistanceX(g0,g0) = 28
    c: Vertical(g7,g3)
FEATURE [PartDesign::Revolution] Revolution
  Angle = 360
  Angle2 = 0
  Axis = (0,1,0)
  Base = (0,0,0)
  Profile = -> Sketch171
  ReferenceAxis = -> Sketch171 [V_Axis]
  Refine = true
  Reversed = true
  Suppressed = false
  Type = 0
FEATURE [Sketcher::SketchObject] Sketch172
  ArcFitTolerance = 1e-06
  AttachmentSupport = -> [Revolution]
  ExternalGeometry = -> [Revolution]
  FullyConstrained = true
  MakeInternals = false
  MapMode = 5
  Placement = pos=(0,0,0) rot=(1,0,0;1.5708rad)
  sketch-geometry (8):
    g0: LineSegment StartX=0 StartY=9.5 StartZ=0 EndX=-8.22724 EndY=4.75 EndZ=0
    g1: LineSegment StartX=-8.22724 StartY=4.75 StartZ=0 EndX=-8.22724 EndY=-4.75 EndZ=0
    g2: LineSegment StartX=-8.22724 StartY=-4.75 StartZ=0 EndX=0 EndY=-9.5 EndZ=0
    g3: LineSegment StartX=0 StartY=-9.5 StartZ=0 EndX=8.22724 EndY=-4.75 EndZ=0
    g4: LineSegment StartX=8.22724 StartY=-4.75 StartZ=0 EndX=8.22724 EndY=4.75 EndZ=0
    g5: LineSegment StartX=8.22724 StartY=4.75 StartZ=0 EndX=0 EndY=9.5 EndZ=0
    g6: Circle [constr] CenterX=0 CenterY=0 CenterZ=0 NormalX=0 NormalY=0 NormalZ=1 AngleXU=0 Radius=9.5
    g7: Circle CenterX=0 CenterY=0 CenterZ=0 NormalX=0 NormalY=0 NormalZ=1 AngleXU=0 Radius=11.5
  constraints (18):
    c: Coincident(g0,g1)
    c: Coincident(g1,g2)
    c: Coincident(g2,g3)
    c: Coincident(g3,g4)
    c: Coincident(g4,g5)
    c: Coincident(g5,g0)
    c: Equal(g0, g1-g5) x5
    c: PointOnObject(g0,g6)
    c: PointOnObject(g1,g6)
    c: PointOnObject(g2,g6)
    c: PointOnObject(g3,g6)
    c: PointOnObject(g4,g6)
    c: PointOnObject(g5,g6)
    c: Coincident(g6,g-3)
    c: PointOnObject(g5,g-3)
    c: PointOnObject(g0,g-2)
    c: Coincident(g7,g6)
    c: Distance(g6,g7) = 2
FEATURE [PartDesign::Pocket] Pocket060
  BaseFeature = -> Revolution
  Direction = (0,1,-2e-16)
  Length = 7
  Length2 = 5
  Profile = -> Sketch172
  ReferenceAxis = -> Sketch172 [N_Axis]
  Refine = true
  Suppressed = false
  Type = 0
FEATURE [PartDesign::Body] Body096  label="Spindle"
  AllowCompound = false
  Group = -> [Sketch171,Revolution,Sketch172,Pocket060]
  Origin = -> Origin1349
  Placement = pos=(30,-126.5,34) rot=(0,0,1;0rad)
  Tip = -> Pocket060
FEATURE [App::Part] Part018  label="SpindleAssembly"
  Group = -> [Body095,Body096]
  Origin = -> Origin1347
  Placement = pos=(0,9.4,21) rot=(0,0,1;0rad)
FEATURE [PartDesign::FeatureBase] Clone041
  BaseFeature = -> Body072
  Suppressed = false
FEATURE [PartDesign::FeatureBase] Clone043
  BaseFeature = -> Body073
  Suppressed = false
FEATURE [PartDesign::Body] Body099  label="MGN15H block008"
  AllowCompound = false
  Group = -> [Clone043]
  Origin = -> Origin1355
  Tip = -> Clone043
FEATURE [PartDesign::FeatureBase] Clone044
  BaseFeature = -> Body073
  Suppressed = false
FEATURE [PartDesign::Body] Body100  label="MGN15H block007"
  AllowCompound = false
  Group = -> [Clone044]
  Origin = -> Origin1357
  Placement = pos=(60,0,0) rot=(0,0,1;0rad)
  Tip = -> Clone044
FEATURE [PartDesign::Pocket] Pocket061
  BaseFeature = -> Clone041
  Direction = (0,1,0)
  Length = 170
  Length2 = 5
  Profile = -> Clone041 [Face3]
  Refine = true
  Suppressed = false
  Type = 0
FEATURE [Sketcher::SketchObject] Sketch173
  ArcFitTolerance = 1e-06
  AttachmentSupport = -> [Origin1363]
  FullyConstrained = true
  MakeInternals = false
  MapMode = 5
  sketch-geometry (4):
    g0: LineSegment StartX=0 StartY=0 StartZ=0 EndX=100 EndY=0 EndZ=0
    g1: LineSegment StartX=100 StartY=0 StartZ=0 EndX=100 EndY=50 EndZ=0
    g2: LineSegment StartX=100 StartY=50 StartZ=0 EndX=0 EndY=50 EndZ=0
    g3: LineSegment StartX=0 StartY=50 StartZ=0 EndX=0 EndY=0 EndZ=0
  constraints (11):
    c: Coincident(g0,g1)
    c: Coincident(g1,g2)
    c: Coincident(g2,g3)
    c: Coincident(g3,g0)
    c: Horizontal(g0)
    c: Horizontal(g2)
    c: Vertical(g1)
    c: Vertical(g3)
    c: Distance(g1,g3) = 100
    c: Distance(g0,g2) = 50
    c: Coincident(g0,g-1)
FEATURE [PartDesign::Pad] Pad089
  Direction = (0,0,1)
  Length = 10
  Length2 = 10
  Profile = -> Sketch173
  ReferenceAxis = -> Sketch173 [N_Axis]
  Refine = true
  Suppressed = false
  Type = 0
FEATURE [Sketcher::SketchObject] Sketch174
  ArcFitTolerance = 1e-06
  AttachmentSupport = -> [Pad089]
  ExternalGeometry = -> [Pad089]
  FullyConstrained = true
  MakeInternals = false
  MapMode = 5
  Placement = pos=(0,0,10) rot=(0,0,1;0rad)
  sketch-geometry (20):
    g0: LineSegment [constr] StartX=4 StartY=37.5 StartZ=0 EndX=4 EndY=12.5 EndZ=0
    g1: LineSegment [constr] StartX=4 StartY=12.5 StartZ=0 EndX=36 EndY=12.5 EndZ=0
    g2: LineSegment [constr] StartX=36 StartY=12.5 StartZ=0 EndX=36 EndY=37.5 EndZ=0
    g3: LineSegment [constr] StartX=36 StartY=37.5 StartZ=0 EndX=4 EndY=37.5 EndZ=0
    g4: LineSegment [constr] StartX=64 StartY=37.5 StartZ=0 EndX=64 EndY=12.5 EndZ=0
    g5: LineSegment [constr] StartX=64 StartY=12.5 StartZ=0 EndX=96 EndY=12.5 EndZ=0
    g6: LineSegment [constr] StartX=96 StartY=12.5 StartZ=0 EndX=96 EndY=37.5 EndZ=0
    g7: LineSegment [constr] StartX=96 StartY=37.5 StartZ=0 EndX=64 EndY=37.5 EndZ=0
    g8: GeomPoint [constr] X=0 Y=25 Z=0
    g9: GeomPoint [constr] X=4 Y=25 Z=0
    g10: GeomPoint X=7.5 Y=37.5 Z=0
    g11: GeomPoint X=32.5 Y=37.5 Z=0
    g12: GeomPoint X=32.5 Y=12.5 Z=0
    g13: GeomPoint X=7.5 Y=12.5 Z=0
    g14: GeomPoint X=67.5 Y=12.5 Z=0
    g15: GeomPoint X=67.5 Y=37.5 Z=0
    g16: GeomPoint X=92.5 Y=37.5 Z=0
    g17: GeomPoint X=92.5 Y=12.5 Z=0
    g18: GeomPoint [constr] X=20 Y=37.5 Z=0
    g19: GeomPoint [constr] X=80 Y=37.5 Z=0
  constraints (42):
    c: Coincident(g0,g1)
    c: Coincident(g1,g2)
    c: Coincident(g2,g3)
    c: Coincident(g3,g0)
    c: Vertical(g0)
    c: Vertical(g2)
    c: Horizontal(g1)
    c: Horizontal(g3)
    c: Coincident(g4,g5)
    c: Coincident(g5,g6)
    c: Coincident(g6,g7)
    c: Coincident(g7,g4)
    c: Vertical(g4)
    c: Vertical(g6)
    c: Horizontal(g5)
    c: Horizontal(g7)
    c: Distance(g-6,g0) = 4
    c: Distance(g-4,g6) = 4
    c: Equal(g7,g3)
    c: DistanceX(g3,g3) = 32
    c: DistanceY(g2,g2) = 25
    c: Equal(g2,g4)
    c: Horizontal(g3,g4)
    c: Symmetric(g-6,g-6,g8)
    c: Symmetric(g0,g0,g9)
    c: Horizontal(g8,g9)
    c: PointOnObject(g10,g3)
    c: PointOnObject(g12,g1)
    c: PointOnObject(g13,g1)
    c: PointOnObject(g14,g5)
    c: PointOnObject(g15,g7)
    c: PointOnObject(g17,g5)
    c: Vertical(g14,g15)
    c: Vertical(g16,g17)
    c: Vertical(g10,g13)
    c: Vertical(g11,g12)
    c: DistanceX(g10,g11) = 25
    c: DistanceX(g15,g16) = 25
    c: Symmetric(g3,g3,g18)
    c: Symmetric(g7,g7,g19)
    c: Symmetric(g15,g16,g19)
    c: Symmetric(g10,g11,g18)
FEATURE [PartDesign::Hole] Hole024
  BaseFeature = -> Pad089
  CustomThreadClearance = 0
  Depth = 25
  DepthType = 0
  Diameter = 1.2
  DrillForDepth = false
  DrillPoint = 1
  DrillPointAngle = 118
  HoleCutCountersinkAngle = 90
  HoleCutCustomValues = true
  HoleCutDepth = 3.35
  HoleCutDiameter = 1.3
  HoleCutType = 6
  ModelThread = false
  Profile = -> Sketch174
  Refine = true
  Suppressed = false
  Tapered = false
  TaperedAngle = 90
  ThreadClass = 0
  ThreadDepth = 25
  ThreadDepthType = 0
  ThreadDirection = 0
  ThreadFit = 0
  ThreadSize = 0
  ThreadType = 1
  Threaded = false
  UseCustomThreadClearance = false
FEATURE [Sketcher::SketchObject] Sketch175
  ArcFitTolerance = 1e-06
  AttachmentSupport = -> [Hole024]
  ExternalGeometry = -> [Hole024]
  FullyConstrained = true
  MakeInternals = false
  MapMode = 5
  Placement = pos=(0,0,10) rot=(0,0,1;0rad)
  sketch-geometry (12):
    g0: GeomPoint X=15 Y=35 Z=0
    g1: GeomPoint X=15 Y=15 Z=0
    g2: GeomPoint X=85 Y=35 Z=0
    g3: GeomPoint X=85 Y=15 Z=0
    g4: GeomPoint [constr] X=85 Y=25 Z=0
    g5: GeomPoint [constr] X=15 Y=25 Z=0
    g6: GeomPoint [constr] X=50 Y=50 Z=0
    g7: GeomPoint [constr] X=50 Y=25 Z=0
    g8: Circle [constr] CenterX=15 CenterY=35 CenterZ=0 NormalX=0 NormalY=0 NormalZ=1 AngleXU=0 Radius=3
    g9: Circle [constr] CenterX=15 CenterY=15 CenterZ=0 NormalX=0 NormalY=0 NormalZ=1 AngleXU=0 Radius=3
    g10: Circle [constr] CenterX=85 CenterY=35 CenterZ=0 NormalX=0 NormalY=0 NormalZ=1 AngleXU=0 Radius=3
    g11: GeomPoint [constr] X=0 Y=25 Z=0
  constraints (19):
    c: Vertical(g0,g1)
    c: Vertical(g2,g3)
    c: Horizontal(g0,g2)
    c: Horizontal(g1,g3)
    c: Symmetric(g0,g1,g5)
    c: Symmetric(g2,g3,g4)
    c: DistanceY(g3,g2) = 20
    c: DistanceX(g0,g2) = 70
    c: Symmetric(g-6,g-6,g6)
    c: Vertical(g6,g7)
    c: Symmetric(g4,g5,g7)
    c: Diameter(g8) = 6
    c: Coincident(g8,g0)
    c: Diameter(g9) = 6
    c: Coincident(g9,g1)
    c: Diameter(g10) = 6
    c: Coincident(g10,g2)
    c: Symmetric(g-4,g-4,g11)
    c: Horizontal(g5,g11)
FEATURE [PartDesign::Hole] Hole025
  BaseFeature = -> Hole024
  CustomThreadClearance = 0
  Depth = 25
  DepthType = 0
  Diameter = 0.768
  DrillForDepth = false
  DrillPoint = 1
  DrillPointAngle = 118
  HoleCutCountersinkAngle = 90
  HoleCutCustomValues = false
  HoleCutDepth = 0
  HoleCutDiameter = 0
  HoleCutType = 0
  ModelThread = true
  Profile = -> Sketch175
  Refine = true
  Suppressed = false
  Tapered = false
  TaperedAngle = 90
  ThreadClass = 0
  ThreadDepth = 25
  ThreadDepthType = 0
  ThreadDirection = 0
  ThreadFit = 0
  ThreadSize = 0
  ThreadType = 1
  Threaded = true
  UseCustomThreadClearance = false
FEATURE [PartDesign::FeatureBase] Clone046
  BaseFeature = -> Body004
  Suppressed = false
FEATURE [PartDesign::FeatureBase] Clone047
  BaseFeature = -> Body058
  Suppressed = false
FEATURE [Sketcher::SketchObject] Sketch176
  ArcFitTolerance = 1e-06
  AttachmentSupport = -> [Clone047]
  ExternalGeometry = -> [Clone047]
  FullyConstrained = false
  MakeInternals = false
  MapMode = 5
  Placement = pos=(-6.7e-15,-1.1e-15,10) rot=(1,0,0;3.14159rad)
  sketch-geometry (4):
    g0: LineSegment StartX=-10.8407 StartY=-8 StartZ=0 EndX=-10.8407 EndY=-19.04 EndZ=0
    g1: LineSegment StartX=-10.8407 StartY=-19.04 StartZ=0 EndX=10.0082 EndY=-19.04 EndZ=0
    g2: LineSegment StartX=10.0082 StartY=-19.04 StartZ=0 EndX=10.0082 EndY=-8 EndZ=0
    g3: LineSegment StartX=10.0082 StartY=-8 StartZ=0 EndX=-10.8407 EndY=-8 EndZ=0
  constraints (9):
    c: Coincident(g0,g1)
    c: Coincident(g1,g2)
    c: Coincident(g2,g3)
    c: Coincident(g3,g0)
    c: Vertical(g0)
    c: Vertical(g2)
    c: Horizontal(g1)
    c: Horizontal(g3)
    c: PointOnObject(g-3,g3)
FEATURE [PartDesign::Pocket] Pocket062
  BaseFeature = -> Clone047
  Direction = (0,0,1)
  Length = 5
  Length2 = 5
  Profile = -> Sketch176
  ReferenceAxis = -> Sketch176 [N_Axis]
  Refine = true
  Suppressed = false
  Type = 1
FEATURE [PartDesign::Body] Body104  label="T8 Nut002"
  AllowCompound = false
  Group = -> [Clone047,Sketch176,Pocket062]
  Origin = -> Origin1367
  Placement = pos=(30.052,4.5,5.76041) rot=(1,0,0;4.71239rad)
  Tip = -> Pocket062
FEATURE [Sketcher::SketchObject] Sketch177
  ArcFitTolerance = 1e-06
  AttachmentSupport = -> [Pocket061]
  FullyConstrained = true
  MakeInternals = false
  MapMode = 5
  Placement = pos=(0,130,0) rot=(1,0,0;1.5708rad)
FEATURE [PartDesign::Pocket] Pocket063
  BaseFeature = -> Pocket061
  Direction = (0,1,0)
  Length = 30
  Length2 = 5
  Profile = -> Pocket061 [Face3]
  Refine = true
  Suppressed = false
  Type = 0
FEATURE [PartDesign::Body] Body097  label="MGN15H rail005"
  AllowCompound = false
  Group = -> [Clone041,Pocket061,Sketch177,Pocket063]
  Origin = -> Origin1351
  Placement = pos=(-101,209.5,-53) rot=(1,0,0;1.5708rad)
  Tip = -> Pocket063
FEATURE [PartDesign::FeatureBase] Clone045
  BaseFeature = -> Body097
  Suppressed = false
FEATURE [PartDesign::Body] Body101  label="MGN15H rail006"
  AllowCompound = false
  Group = -> [Clone045]
  Origin = -> Origin1359
  Placement = pos=(-41,209.5,-53) rot=(1,0,0;1.5708rad)
  Tip = -> Clone045
FEATURE [PartDesign::FeatureBase] Clone049
  BaseFeature = -> Body055
  Suppressed = false
FEATURE [PartDesign::Body] Body106  label="Coupling 5x8002"
  AllowCompound = false
  Group = -> [Clone049]
  Origin = -> Origin1371
  Placement = pos=(-71,203.75,284) rot=(0,1,0;3.14159rad)
  Tip = -> Clone049
FEATURE [PartDesign::LinearPattern] LinearPattern009
  BaseFeature = -> Clone046
  Direction = -> Z_Axis1013
  Length = 140
  Mode = 1
  Occurrences = 15
  Offset = 10
  Refine = true
  Suppressed = false
  TransformMode = 1
FEATURE [PartDesign::Body] Body103  label="T8 Lead Screw002"
  AllowCompound = false
  Group = -> [Clone046,LinearPattern009]
  Origin = -> Origin1365
  Placement = pos=(-71,203.75,267) rot=(0,1,0;3.14159rad)
  Tip = -> LinearPattern009
FEATURE [Sketcher::SketchObject] Sketch178
  ArcFitTolerance = 1e-06
  AttachmentSupport = -> [Origin1373]
  FullyConstrained = true
  MakeInternals = false
  MapMode = 5
  sketch-geometry (8):
    g0: LineSegment StartX=-80 StartY=40 StartZ=0 EndX=-80 EndY=0 EndZ=0
    g1: LineSegment StartX=-80 StartY=0 StartZ=0 EndX=-60 EndY=0 EndZ=0
    g2: LineSegment StartX=-60 StartY=0 StartZ=0 EndX=-60 EndY=20 EndZ=0
    g3: LineSegment StartX=-60 StartY=20 StartZ=0 EndX=-20 EndY=20 EndZ=0
    g4: LineSegment StartX=-20 StartY=20 StartZ=0 EndX=-20 EndY=0 EndZ=0
    g5: LineSegment StartX=-20 StartY=0 StartZ=0 EndX=0 EndY=0 EndZ=0
    g6: LineSegment StartX=0 StartY=0 StartZ=0 EndX=0 EndY=40 EndZ=0
    g7: LineSegment StartX=0 StartY=40 StartZ=0 EndX=-80 EndY=40 EndZ=0
  constraints (23):
    c: Vertical(g0)
    c: Coincident(g0,g1)
    c: Horizontal(g1)
    c: Coincident(g1,g2)
    c: Vertical(g2)
    c: Coincident(g2,g3)
    c: Horizontal(g3)
    c: Coincident(g3,g4)
    c: Vertical(g4)
    c: Coincident(g4,g5)
    c: Coincident(g5,g6)
    c: Vertical(g6)
    c: Coincident(g6,g7)
    c: Coincident(g7,g0)
    c: Horizontal(g7)
    c: Horizontal(g5)
    c: DistanceX(g3,g3) = 40
    c: DistanceX(g7,g7) = 80
    c: DistanceY(g0,g0) = 40
    c: Horizontal(g2,g4)
    c: Equal(g1,g5)
    c: DistanceY(g4,g4) = 20
    c: Coincident(g5,g-1)
FEATURE [PartDesign::Pad] Pad090
  Direction = (0,0,1)
  Length = 15
  Length2 = 10
  Profile = -> Sketch178
  ReferenceAxis = -> Sketch178 [N_Axis]
  Refine = true
  Suppressed = false
  Type = 0
FEATURE [Sketcher::SketchObject] Sketch179
  ArcFitTolerance = 1e-06
  AttachmentSupport = -> [Pad090]
  ExternalGeometry = -> [Pad090]
  FullyConstrained = true
  MakeInternals = false
  MapMode = 5
  Placement = pos=(0,0,15) rot=(0,0,1;0rad)
  sketch-geometry (4):
    g0: GeomPoint X=-70 Y=30 Z=0
    g1: GeomPoint [constr] X=-50 Y=30 Z=0
    g2: GeomPoint [constr] X=-30 Y=30 Z=0
    g3: GeomPoint X=-10 Y=30 Z=0
  constraints (8):
    c: Horizontal(g0,g1)
    c: Horizontal(g1,g2)
    c: Horizontal(g2,g3)
    c: DistanceX(g0,g1) = 20
    c: DistanceX(g1,g2) = 20
    c: DistanceX(g2,g3) = 20
    c: Distance(g3,g-9) = 10
    c: Distance(g3,g-10) = 10
FEATURE [PartDesign::Hole] Hole026
  BaseFeature = -> Pad090
  CustomThreadClearance = 0
  Depth = 25
  DepthType = 0
  Diameter = 1.2
  DrillForDepth = false
  DrillPoint = 1
  DrillPointAngle = 118
  HoleCutCountersinkAngle = 90
  HoleCutCustomValues = true
  HoleCutDepth = 0.1
  HoleCutDiameter = 1.3
  HoleCutType = 4
  ModelThread = false
  Profile = -> Sketch179
  Refine = true
  Suppressed = false
  Tapered = false
  TaperedAngle = 90
  ThreadClass = 0
  ThreadDepth = 25
  ThreadDepthType = 0
  ThreadDirection = 0
  ThreadFit = 0
  ThreadSize = 0
  ThreadType = 1
  Threaded = false
  UseCustomThreadClearance = false
FEATURE [PartDesign::Pad] Pad091
  BaseFeature = -> Hole026
  Direction = (0,0,1)
  Length = 28
  Length2 = 10
  Profile = -> Hole026 [Face5]
  Refine = true
  Suppressed = false
  Type = 0
FEATURE [Sketcher::SketchObject] Sketch180
  ArcFitTolerance = 1e-06
  AttachmentSupport = -> [Pad091]
  ExternalGeometry = -> [Pad091]
  FullyConstrained = false
  MakeInternals = false
  MapMode = 5
  Placement = pos=(0,0,0) rot=(1,0,0;3.14159rad)
  sketch-geometry (15):
    g0: LineSegment [constr] StartX=-55.4941 StartY=6.2 StartZ=0 EndX=-55.4941 EndY=-24.8 EndZ=0
    g1: LineSegment [constr] StartX=-55.4941 StartY=-24.8 StartZ=0 EndX=-24.4941 EndY=-24.8 EndZ=0
    g2: LineSegment [constr] StartX=-24.4941 StartY=-24.8 StartZ=0 EndX=-24.4941 EndY=6.2 EndZ=0
    g3: LineSegment [constr] StartX=-24.4941 StartY=6.2 StartZ=0 EndX=-55.4941 EndY=6.2 EndZ=0
    g4: LineSegment [constr] StartX=-61.1441 StartY=11.85 StartZ=0 EndX=-61.1441 EndY=-30.45 EndZ=0
    g5: LineSegment [constr] StartX=-61.1441 StartY=-30.45 StartZ=0 EndX=-18.8441 EndY=-30.45 EndZ=0
    g6: LineSegment [constr] StartX=-18.8441 StartY=-30.45 StartZ=0 EndX=-18.8441 EndY=11.85 EndZ=0
    g7: LineSegment [constr] StartX=-18.8441 StartY=11.85 StartZ=0 EndX=-61.1441 EndY=11.85 EndZ=0
    g8: LineSegment [constr] StartX=-55.4941 StartY=6.2 StartZ=0 EndX=-55.4941 EndY=11.85 EndZ=0
    g9: LineSegment [constr] StartX=-55.4941 StartY=6.2 StartZ=0 EndX=-61.1441 EndY=6.2 EndZ=0
    g10: LineSegment [constr] StartX=-24.4941 StartY=6.2 StartZ=0 EndX=-18.8441 EndY=6.2 EndZ=0
    g11: LineSegment StartX=0 StartY=0 StartZ=0 EndX=0 EndY=11.5 EndZ=0
    g12: LineSegment StartX=0 StartY=11.5 StartZ=0 EndX=-80 EndY=11.5 EndZ=0
    g13: LineSegment StartX=-80 StartY=11.5 StartZ=0 EndX=-80 EndY=0 EndZ=0
    g14: LineSegment StartX=-80 StartY=0 StartZ=0 EndX=0 EndY=0 EndZ=0
  constraints (42):
    c: Coincident(g0,g1)
    c: Coincident(g1,g2)
    c: Coincident(g2,g3)
    c: Coincident(g3,g0)
    c: Vertical(g0)
    c: Vertical(g2)
    c: Horizontal(g1)
    c: Horizontal(g3)
    c: Equal(g0,g3)
    c: Coincident(g4,g5)
    c: Coincident(g5,g6)
    c: Coincident(g6,g7)
    c: Coincident(g7,g4)
    c: Vertical(g4)
    c: Vertical(g6)
    c: Horizontal(g5)
    c: Horizontal(g7)
    c: Equal(g7,g4)
    c: DistanceX(g7,g7) = 42.3
    c: DistanceX(g3,g3) = 31
    c: Coincident(g8,g0)
    c: PointOnObject(g8,g7)
    c: Vertical(g8)
    c: Coincident(g9,g0)
    c: PointOnObject(g9,g4)
    c: Horizontal(g9)
    c: Coincident(g10,g2)
    c: PointOnObject(g10,g6)
    c: Horizontal(g10)
    c: Equal(g10,g8)
    c: Equal(g8,g9)
    c: DistanceY(g5,g-1) = 30.45
    c: Coincident(g11,g12)
    c: Coincident(g12,g13)
    c: Coincident(g13,g14)
    c: Coincident(g14,g11)
    c: Vertical(g11)
    c: Vertical(g13)
    c: Horizontal(g12)
    c: Coincident(g11,g-1)
    c: DistanceY(g13,g13) = 11.5
    c: Coincident(g13,g-3)
FEATURE [PartDesign::Pad] Pad092
  BaseFeature = -> Pad091
  Direction = (0,0,-1)
  Length = 10
  Length2 = 10
  Profile = -> Sketch180
  ReferenceAxis = -> Sketch180 [N_Axis]
  Refine = true
  Suppressed = false
  Type = 3
  UpToFace = -> Pad091 [Face7]
FEATURE [Sketcher::SketchObject] Sketch181
  ArcFitTolerance = 1e-06
  AttachmentSupport = -> [Pad092]
  ExternalGeometry = -> [Pad092]
  FullyConstrained = true
  MakeInternals = false
  MapMode = 5
  Placement = pos=(0,0,0) rot=(1,0,0;3.14159rad)
  sketch-geometry (4):
    g0: LineSegment StartX=-80 StartY=11.5 StartZ=0 EndX=-80 EndY=0 EndZ=0
    g1: LineSegment StartX=-80 StartY=0 StartZ=0 EndX=0 EndY=0 EndZ=0
    g2: LineSegment StartX=0 StartY=0 StartZ=0 EndX=0 EndY=11.5 EndZ=0
    g3: LineSegment StartX=0 StartY=11.5 StartZ=0 EndX=-80 EndY=11.5 EndZ=0
  constraints (10):
    c: Coincident(g0,g1)
    c: Coincident(g1,g2)
    c: Coincident(g2,g3)
    c: Coincident(g3,g0)
    c: Vertical(g0)
    c: Vertical(g2)
    c: Horizontal(g1)
    c: Horizontal(g3)
    c: Coincident(g0,g-6)
    c: Coincident(g1,g-1)
FEATURE [PartDesign::Pocket] Pocket064
  BaseFeature = -> Pad092
  Direction = (0,0,1)
  Length = 32
  Length2 = 5
  Profile = -> Sketch181
  ReferenceAxis = -> Sketch181 [N_Axis]
  Refine = true
  Suppressed = false
  Type = 0
FEATURE [Sketcher::SketchObject] Sketch182
  ArcFitTolerance = 1e-06
  AttachmentSupport = -> [Pocket064]
  ExternalGeometry = -> [Pocket064]
  FullyConstrained = true
  MakeInternals = false
  MapMode = 5
  Placement = pos=(0,0,0) rot=(1,0,0;3.14159rad)
  sketch-geometry (13):
    g0: Circle CenterX=-40 CenterY=-9.25 CenterZ=0 NormalX=0 NormalY=0 NormalZ=1 AngleXU=0 Radius=11
    g1: GeomPoint X=-60 Y=-10 Z=0
    g2: GeomPoint X=-20 Y=-9.25 Z=0
    g3: GeomPoint X=-60 Y=-9.25 Z=0
    g4: LineSegment [constr] StartX=-55.5 StartY=-24.75 StartZ=0 EndX=-24.5 EndY=-24.75 EndZ=0
    g5: LineSegment [constr] StartX=-24.5 StartY=-24.75 StartZ=0 EndX=-24.5 EndY=6.25 EndZ=0
    g6: LineSegment [constr] StartX=-24.5 StartY=6.25 StartZ=0 EndX=-55.5 EndY=6.25 EndZ=0
    g7: LineSegment [constr] StartX=-55.5 StartY=6.25 StartZ=0 EndX=-55.5 EndY=-24.75 EndZ=0
    g8: GeomPoint [constr] X=-40 Y=-9.25 Z=0
    g9: Circle CenterX=-55.5 CenterY=6.25 CenterZ=0 NormalX=0 NormalY=0 NormalZ=1 AngleXU=0 Radius=1.5
    g10: Circle CenterX=-24.5 CenterY=6.25 CenterZ=0 NormalX=0 NormalY=0 NormalZ=1 AngleXU=0 Radius=1.5
    g11: Circle CenterX=-24.5 CenterY=-24.75 CenterZ=0 NormalX=0 NormalY=0 NormalZ=1 AngleXU=0 Radius=1.5
    g12: Circle CenterX=-55.5 CenterY=-24.75 CenterZ=0 NormalX=0 NormalY=0 NormalZ=1 AngleXU=0 Radius=1.5
  constraints (27):
    c: Diameter(g0) = 22
    c: Symmetric(g-3,g-3,g1)
    c: PointOnObject(g2,g-4)
    c: PointOnObject(g3,g-3)
    c: Horizontal(g3,g2)
    c: Symmetric(g3,g2,g0)
    c: DistanceY(g2,g-4) = 9.25
    c: Coincident(g4,g5)
    c: Coincident(g5,g6)
    c: Coincident(g6,g7)
    c: Coincident(g7,g4)
    c: Horizontal(g4)
    c: Horizontal(g6)
    c: Vertical(g5)
    c: Vertical(g7)
    c: Symmetric(g6,g4,g8)
    c: Distance(g5,g7) = 31
    c: Distance(g4,g6) = 31
    c: Coincident(g8,g0)
    c: Coincident(g9,g6)
    c: Coincident(g10,g5)
    c: Coincident(g11,g4)
    c: Coincident(g12,g4)
    c: Equal(g10,g9)
    c: Equal(g9,g12)
    c: Equal(g12,g11)
    c: Diameter(g11) = 3
FEATURE [PartDesign::Pocket] Pocket065
  BaseFeature = -> Pocket064
  Direction = (0,0,1)
  Length = 5
  Length2 = 5
  Profile = -> Sketch182
  ReferenceAxis = -> Sketch182 [N_Axis]
  Refine = true
  Suppressed = false
  Type = 1
FEATURE [Sketcher::SketchObject] Sketch183
  ArcFitTolerance = 1e-06
  AttachmentSupport = -> [Pocket065]
  ExternalGeometry = -> [Pocket065]
  FullyConstrained = true
  MakeInternals = false
  MapMode = 5
  Placement = pos=(0,0,0) rot=(1,0,0;3.14159rad)
  sketch-geometry (4):
    g0: GeomPoint X=-55.5 Y=-24.75 Z=0
    g1: GeomPoint X=-24.5 Y=-24.75 Z=0
    g2: GeomPoint X=-55.5 Y=6.25 Z=0
    g3: GeomPoint X=-24.5 Y=6.25 Z=0
  constraints (4):
    c: Coincident(g0,g-14)
    c: Coincident(g1,g-13)
    c: Coincident(g2,g-17)
    c: Coincident(g3,g-18)
FEATURE [PartDesign::Hole] Hole027
  BaseFeature = -> Pocket065
  CustomThreadClearance = 0
  Depth = 210.906
  DepthType = 1
  Diameter = 1.2
  DrillForDepth = false
  DrillPoint = 1
  DrillPointAngle = 118
  HoleCutCountersinkAngle = 90
  HoleCutCustomValues = true
  HoleCutDepth = 0.1
  HoleCutDiameter = 1.3
  HoleCutType = 4
  ModelThread = false
  Profile = -> Sketch183
  Refine = true
  Suppressed = false
  Tapered = false
  TaperedAngle = 90
  ThreadClass = 0
  ThreadDepth = 210.906
  ThreadDepthType = 0
  ThreadDirection = 0
  ThreadFit = 0
  ThreadSize = 0
  ThreadType = 1
  Threaded = false
  UseCustomThreadClearance = false
FEATURE [Sketcher::SketchObject] Sketch184
  ArcFitTolerance = 1e-06
  AttachmentSupport = -> [Hole025]
  ExternalGeometry = -> [Hole025]
  FullyConstrained = true
  MakeInternals = false
  MapMode = 5
  Placement = pos=(0,50,0) rot=(0,0.707107,0.707107;3.14159rad)
  sketch-geometry (2):
    g0: Circle CenterX=-50 CenterY=2.75 CenterZ=0 NormalX=0 NormalY=0 NormalZ=1 AngleXU=0 Radius=1.5
    g1: GeomPoint X=-50 Y=10 Z=0
  constraints (4):
    c: Symmetric(g-6,g-6,g1)
    c: Vertical(g1,g0)
    c: Distance(g0,g-5) = 2.75
    c: Diameter(g0) = 3
FEATURE [PartDesign::Hole] Hole028
  BaseFeature = -> Hole025
  CustomThreadClearance = 0
  Depth = 12
  DepthType = 0
  Diameter = 0.768
  DrillForDepth = false
  DrillPoint = 1
  DrillPointAngle = 118
  HoleCutCountersinkAngle = 90
  HoleCutCustomValues = false
  HoleCutDepth = 0
  HoleCutDiameter = 0
  HoleCutType = 0
  ModelThread = true
  Profile = -> Sketch184
  Refine = true
  Suppressed = false
  Tapered = false
  TaperedAngle = 90
  ThreadClass = 0
  ThreadDepth = 12
  ThreadDepthType = 0
  ThreadDirection = 0
  ThreadFit = 0
  ThreadSize = 0
  ThreadType = 1
  Threaded = true
  UseCustomThreadClearance = false
FEATURE [PartDesign::FeatureBase] Clone050
  BaseFeature = -> Body055
  Suppressed = false
FEATURE [PartDesign::Body] Body108  label="Coupling 5x8003"
  AllowCompound = false
  Group = -> [Clone050]
  Origin = -> Origin1375
  Placement = pos=(-146,224.5,177.5) rot=(0,1,0;1.5708rad)
  Tip = -> Clone050
FEATURE [Sketcher::SketchObject] Sketch185
  ArcFitTolerance = 1e-06
  AttachmentSupport = -> [LinearPattern006]
  ExternalGeometry = -> [LinearPattern006]
  FullyConstrained = true
  MakeInternals = false
  MapMode = 5
  Placement = pos=(-2.5e-15,0,-10) rot=(1,0,0;3.14159rad)
  sketch-geometry (4):
    g0: Circle CenterX=35.5 CenterY=-200 CenterZ=0 NormalX=0 NormalY=0 NormalZ=1 AngleXU=0 Radius=12
    g1: LineSegment [constr] StartX=30 StartY=-200 StartZ=0 EndX=35.5 EndY=-200 EndZ=0
    g2: LineSegment [constr] StartX=35.5 StartY=-200 StartZ=0 EndX=47.5 EndY=-200 EndZ=0
    g3: Circle [constr] CenterX=35.5 CenterY=-200 CenterZ=0 NormalX=0 NormalY=0 NormalZ=1 AngleXU=0 Radius=2.5
  constraints (11):
    c: Diameter(g0) = 24
    c: PointOnObject(g1,g-3)
    c: Coincident(g1,g0)
    c: Horizontal(g1)
    c: Coincident(g1,g2)
    c: PointOnObject(g2,g0)
    c: Horizontal(g2)
    c: DistanceY(g-3,g0) = 40
    c: DistanceX(g1,g1) = 5.5
    c: Diameter(g3) = 5
    c: Coincident(g0,g3)
FEATURE [PartDesign::Pocket] Pocket066
  BaseFeature = -> LinearPattern006
  Direction = (0,0,1)
  Length = 9.6
  Length2 = 5
  Profile = -> Sketch185
  ReferenceAxis = -> Sketch185 [N_Axis]
  Refine = true
  Suppressed = false
  Type = 1
FEATURE [Sketcher::SketchObject] Sketch186
  ArcFitTolerance = 1e-06
  AttachmentSupport = -> [LinearPattern008]
  FullyConstrained = false
  MakeInternals = false
  MapMode = 5
  Placement = pos=(-10,0,0) rot=(0.57735,-0.57735,-0.57735;2.0944rad)
  sketch-geometry (2):
    g0: Circle CenterX=80 CenterY=0 CenterZ=0 NormalX=0 NormalY=0 NormalZ=1 AngleXU=0 Radius=5.5
    g1: GeomPoint X=40 Y=-5.43466 Z=0
  constraints (4):
    c: PointOnObject(g0,g-1)
    c: Diameter(g0) = 11
    c: DistanceX(g-1,g1) = 40
    c: DistanceX(g1,g0) = 40
FEATURE [PartDesign::Pocket] Pocket067
  BaseFeature = -> LinearPattern008
  Direction = (1,0,0)
  Length = 5
  Length2 = 5
  Profile = -> Sketch186
  ReferenceAxis = -> Sketch186 [N_Axis]
  Refine = true
  Suppressed = false
  Type = 1
FEATURE [PartDesign::FeatureBase] Clone052
  BaseFeature = -> Body058
  Suppressed = false
FEATURE [PartDesign::Body] Body110  label="T8 Nut003"
  AllowCompound = false
  Group = -> [Clone052]
  Origin = -> Origin1379
  Placement = pos=(-41,224.5,177) rot=(0,1,0;1.5708rad)
  Tip = -> Clone052
FEATURE [Sketcher::SketchObject] Sketch187
  ArcFitTolerance = 1e-06
  AttachmentSupport = -> [Pocket067]
  ExternalGeometry = -> [Pocket067]
  FullyConstrained = true
  MakeInternals = false
  MapMode = 5
  Placement = pos=(70,0,-1.75e-14) rot=(0.57735,0.57735,0.57735;2.0944rad)
  sketch-geometry (9):
    g0: LineSegment [constr] StartX=-72 StartY=1.78e-14 StartZ=0 EndX=-80 EndY=8 EndZ=0
    g1: LineSegment [constr] StartX=-80 StartY=8 StartZ=0 EndX=-88 EndY=1.78e-14 EndZ=0
    g2: LineSegment [constr] StartX=-88 StartY=1.78e-14 StartZ=0 EndX=-80 EndY=-8 EndZ=0
    g3: LineSegment [constr] StartX=-80 StartY=-8 StartZ=0 EndX=-72 EndY=1.78e-14 EndZ=0
    g4: GeomPoint [constr] X=-80 Y=1.68e-14 Z=0
    g5: GeomPoint X=-80 Y=8 Z=0
    g6: GeomPoint X=-88 Y=1.78e-14 Z=0
    g7: GeomPoint X=-72 Y=1.78e-14 Z=0
    g8: GeomPoint X=-80 Y=-8 Z=0
  constraints (16):
    c: Coincident(g0,g1)
    c: Coincident(g1,g2)
    c: Coincident(g2,g3)
    c: Coincident(g3,g0)
    c: Symmetric(g2,g0,g4)
    c: Coincident(g4,g-8)
    c: Equal(g3,g1)
    c: Equal(g1,g0)
    c: Equal(g0,g2)
    c: Perpendicular(g1,g2)
    c: Vertical(g0,g2)
    c: DistanceX(g1,g0) = 16
    c: Coincident(g5,g0)
    c: Coincident(g6,g1)
    c: Coincident(g7,g0)
    c: Coincident(g8,g2)
FEATURE [PartDesign::Hole] Hole029
  BaseFeature = -> Pocket067
  CustomThreadClearance = 0
  Depth = 25
  DepthType = 0
  Diameter = 0.75
  DrillForDepth = false
  DrillPoint = 1
  DrillPointAngle = 118
  HoleCutCountersinkAngle = 90
  HoleCutCustomValues = false
  HoleCutDepth = 0
  HoleCutDiameter = 0
  HoleCutType = 0
  ModelThread = false
  Profile = -> Sketch187
  Refine = true
  Suppressed = false
  Tapered = false
  TaperedAngle = 90
  ThreadClass = 0
  ThreadDepth = 25
  ThreadDepthType = 0
  ThreadDirection = 0
  ThreadFit = 0
  ThreadSize = 0
  ThreadType = 1
  Threaded = true
  UseCustomThreadClearance = false
FEATURE [PartDesign::FeatureBase] Clone053
  BaseFeature = -> Body004
  Suppressed = false
FEATURE [PartDesign::LinearPattern] LinearPattern010
  BaseFeature = -> Clone053
  Direction = -> Z_Axis1021
  Length = 340
  Mode = 1
  Occurrences = 35
  Offset = 10
  Refine = true
  Suppressed = false
  TransformMode = 1
FEATURE [PartDesign::Body] Body111  label="T8 Lead Screw003"
  AllowCompound = false
  Group = -> [Clone053,LinearPattern010]
  Origin = -> Origin1381
  Placement = pos=(-132.5,224.5,177) rot=(0,1,0;1.5708rad)
  Tip = -> LinearPattern010
FEATURE [Sketcher::SketchObject] Sketch189
  ArcFitTolerance = 1e-06
  AttachmentSupport = -> [Origin1383]
  FullyConstrained = true
  MakeInternals = false
  MapMode = 5
  Placement = pos=(0,0,0) rot=(1,0,0;1.5708rad)
  sketch-geometry (4):
    g0: LineSegment StartX=0 StartY=0 StartZ=0 EndX=20 EndY=0 EndZ=0
    g1: LineSegment StartX=20 StartY=0 StartZ=0 EndX=20 EndY=24 EndZ=0
    g2: LineSegment StartX=20 StartY=24 StartZ=0 EndX=0 EndY=24 EndZ=0
    g3: LineSegment StartX=0 StartY=24 StartZ=0 EndX=0 EndY=0 EndZ=0
  constraints (11):
    c: Coincident(g0,g1)
    c: Coincident(g1,g2)
    c: Coincident(g2,g3)
    c: Coincident(g3,g0)
    c: Horizontal(g0)
    c: Horizontal(g2)
    c: Vertical(g1)
    c: Vertical(g3)
    c: Distance(g1,g3) = 20
    c: Distance(g0,g2) = 24
    c: Coincident(g0,g-1)
FEATURE [PartDesign::Pad] Pad095
  Direction = (0,-1,0)
  Length = 16.5
  Length2 = 10
  Profile = -> Sketch189
  ReferenceAxis = -> Sketch189 [N_Axis]
  Refine = true
  Suppressed = false
  Type = 0
FEATURE [Sketcher::SketchObject] Sketch190
  ArcFitTolerance = 1e-06
  AttachmentSupport = -> [Pad095]
  ExternalGeometry = -> [Pad095]
  FullyConstrained = true
  MakeInternals = false
  MapMode = 5
  Placement = pos=(0,0,0) rot=(0.57735,-0.57735,-0.57735;2.0944rad)
  sketch-geometry (3):
    g0: Circle CenterX=5.55 CenterY=12 CenterZ=0 NormalX=0 NormalY=0 NormalZ=1 AngleXU=0 Radius=5
    g1: GeomPoint X=-2.7e-15 Y=12 Z=0
    g2: GeomPoint [constr] X=-4.45 Y=12 Z=0
  constraints (6):
    c: Diameter(g0) = 10
    c: Symmetric(g-5,g-5,g1)
    c: Horizontal(g0,g1)
    c: Distance(g2,g-2) = 4.45
    c: DistanceX(g2,g0) = 10
    c: Horizontal(g1,g2)
FEATURE [PartDesign::Pocket] Pocket069
  BaseFeature = -> Pad095
  Direction = (1,0,0)
  Length = 5
  Length2 = 5
  Profile = -> Sketch190
  ReferenceAxis = -> Sketch190 [N_Axis]
  Refine = true
  Suppressed = false
  Type = 1
FEATURE [PartDesign::Fillet] Fillet
  Base = -> Pocket069 [Edge14,Edge4]
  BaseFeature = -> Pocket069
  Radius = 10
  Refine = true
  SupportTransform = false
  Suppressed = false
  UseAllEdges = false
FEATURE [Sketcher::SketchObject] Sketch191
  ArcFitTolerance = 1e-06
  AttachmentSupport = -> [Fillet]
  ExternalGeometry = -> [Fillet]
  FullyConstrained = true
  MakeInternals = false
  MapMode = 5
  Placement = pos=(0,2.7e-15,0) rot=(0,0.707107,0.707107;3.14159rad)
  sketch-geometry (5):
    g0: GeomPoint X=-10 Y=20 Z=0
    g1: GeomPoint X=-10 Y=4 Z=0
    g2: GeomPoint [constr] X=-10 Y=24 Z=0
    g3: LineSegment [constr] StartX=-10 StartY=20 StartZ=0 EndX=-10 EndY=24 EndZ=0
    g4: LineSegment [constr] StartX=-10 StartY=4 StartZ=0 EndX=-10 EndY=0 EndZ=0
  constraints (9):
    c: Symmetric(g-5,g-5,g2)
    c: Vertical(g0,g1)
    c: Vertical(g1,g2)
    c: Coincident(g3,g0)
    c: Coincident(g3,g2)
    c: Coincident(g4,g1)
    c: Symmetric(g-3,g-3,g4)
    c: Equal(g4,g3)
    c: DistanceY(g3,g3) = 4
FEATURE [PartDesign::Hole] Hole030
  BaseFeature = -> Fillet
  CustomThreadClearance = 0
  Depth = 25
  DepthType = 0
  Diameter = 1.2
  DrillForDepth = false
  DrillPoint = 1
  DrillPointAngle = 118
  HoleCutCountersinkAngle = 90
  HoleCutCustomValues = false
  HoleCutDepth = 0
  HoleCutDiameter = 0
  HoleCutType = 0
  ModelThread = false
  Profile = -> Sketch191
  Refine = true
  Suppressed = false
  Tapered = false
  TaperedAngle = 90
  ThreadClass = 0
  ThreadDepth = 25
  ThreadDepthType = 0
  ThreadDirection = 0
  ThreadFit = 0
  ThreadSize = 0
  ThreadType = 1
  Threaded = false
  UseCustomThreadClearance = false
FEATURE [Sketcher::SketchObject] Sketch192
  ArcFitTolerance = 1e-06
  AttachmentSupport = -> [Hole030]
  ExternalGeometry = -> [Hole030]
  FullyConstrained = true
  MakeInternals = false
  MapMode = 5
  Placement = pos=(0,-16.5,0) rot=(1,0,0;1.5708rad)
  sketch-geometry (2):
    g0: Circle CenterX=10 CenterY=4 CenterZ=0 NormalX=0 NormalY=0 NormalZ=1 AngleXU=0 Radius=3.1
    g1: Circle CenterX=10 CenterY=20 CenterZ=0 NormalX=0 NormalY=0 NormalZ=1 AngleXU=0 Radius=3.1
  constraints (6):
    c: Horizontal(g0,g-4)
    c: Horizontal(g1,g-3)
    c: Vertical(g1,g0)
    c: DistanceX(g0,g-4) = 1.7
    c: Equal(g0,g1)
    c: Diameter(g1) = 6.2
FEATURE [PartDesign::Pocket] Pocket070
  BaseFeature = -> Hole030
  Direction = (0,1,0)
  Length = 8
  Length2 = 5
  Profile = -> Sketch192
  ReferenceAxis = -> Sketch192 [N_Axis]
  Refine = true
  Suppressed = false
  Type = 0
FEATURE [PartDesign::Body] Body112  label="LeadScrewHolder"
  AllowCompound = false
  Group = -> [Sketch189,Pad095,Sketch190,Pocket069,Fillet,Sketch191,Hole030,Sketch192,Pocket070]
  Origin = -> Origin1383
  Placement = pos=(210,230,165) rot=(0,0,1;0rad)
  Tip = -> Pocket070
FEATURE [PartDesign::Fillet] Fillet001
  Base = -> Chamfer002 [Edge34,Edge3]
  BaseFeature = -> Chamfer002
  Radius = 5
  Refine = true
  SupportTransform = false
  Suppressed = false
  UseAllEdges = false
FEATURE [Sketcher::SketchObject] Sketch193
  ArcFitTolerance = 1e-06
  AttachmentSupport = -> [Origin1385]
  FullyConstrained = true
  MakeInternals = false
  MapMode = 5
  Placement = pos=(0,0,0) rot=(1,0,0;1.5708rad)
  sketch-geometry (4):
    g0: LineSegment StartX=0 StartY=0 StartZ=0 EndX=20 EndY=0 EndZ=0
    g1: LineSegment StartX=20 StartY=0 StartZ=0 EndX=20 EndY=42 EndZ=0
    g2: LineSegment StartX=20 StartY=42 StartZ=0 EndX=0 EndY=42 EndZ=0
    g3: LineSegment StartX=0 StartY=42 StartZ=0 EndX=0 EndY=0 EndZ=0
  constraints (11):
    c: Coincident(g0,g1)
    c: Coincident(g1,g2)
    c: Coincident(g2,g3)
    c: Coincident(g3,g0)
    c: Horizontal(g0)
    c: Horizontal(g2)
    c: Vertical(g1)
    c: Vertical(g3)
    c: Distance(g1,g3) = 20
    c: Distance(g0,g2) = 42
    c: Coincident(g0,g-1)
FEATURE [PartDesign::Pad] Pad096
  Direction = (0,-1,0)
  Length = 26.5
  Length2 = 10
  Profile = -> Sketch193
  ReferenceAxis = -> Sketch193 [N_Axis]
  Refine = true
  Suppressed = false
  Type = 0
FEATURE [Sketcher::SketchObject] Sketch194
  ArcFitTolerance = 1e-06
  AttachmentSupport = -> [Pad096]
  ExternalGeometry = -> [Pad096]
  FullyConstrained = true
  MakeInternals = false
  MapMode = 5
  Placement = pos=(0,0,0) rot=(0.57735,-0.57735,-0.57735;2.0944rad)
  sketch-geometry (5):
    g0: LineSegment [constr] StartX=26.5 StartY=42 StartZ=0 EndX=-15.5 EndY=42 EndZ=0
    g1: LineSegment [constr] StartX=-15.5 StartY=42 StartZ=0 EndX=-15.5 EndY=0 EndZ=0
    g2: LineSegment [constr] StartX=-15.5 StartY=0 StartZ=0 EndX=26.5 EndY=0 EndZ=0
    g3: LineSegment [constr] StartX=26.5 StartY=0 StartZ=0 EndX=26.5 EndY=42 EndZ=0
    g4: Circle CenterX=5.5 CenterY=21 CenterZ=0 NormalX=0 NormalY=0 NormalZ=1 AngleXU=0 Radius=13
  constraints (13):
    c: Coincident(g0,g1)
    c: Coincident(g1,g2)
    c: Coincident(g2,g3)
    c: Coincident(g3,g0)
    c: Horizontal(g0)
    c: Horizontal(g2)
    c: Vertical(g1)
    c: Vertical(g3)
    c: Coincident(g0,g-6)
    c: PointOnObject(g1,g-1)
    c: Equal(g1,g2)
    c: Diameter(g4) = 26
    c: Symmetric(g0,g2,g4)
FEATURE [PartDesign::Pocket] Pocket071
  BaseFeature = -> Pad096
  Direction = (1,0,0)
  Length = 5
  Length2 = 5
  Profile = -> Sketch194 [Edge1]
  ReferenceAxis = -> Sketch194 [N_Axis]
  Refine = true
  Suppressed = false
  Type = 1
FEATURE [Sketcher::SketchObject] Sketch195
  ArcFitTolerance = 1e-06
  AttachmentSupport = -> [Pocket071]
  ExternalGeometry = -> [Pocket071]
  FullyConstrained = true
  MakeInternals = false
  MapMode = 5
  Placement = pos=(0,0,0) rot=(0.57735,-0.57735,-0.57735;2.0944rad)
  sketch-geometry (4):
    g0: LineSegment StartX=5.5 StartY=34 StartZ=0 EndX=-8e-15 EndY=34 EndZ=0
    g1: LineSegment StartX=-8e-15 StartY=34 StartZ=0 EndX=-8e-15 EndY=8 EndZ=0
    g2: LineSegment StartX=-8e-15 StartY=8 StartZ=0 EndX=5.5 EndY=8 EndZ=0
    g3: LineSegment StartX=5.5 StartY=8 StartZ=0 EndX=5.5 EndY=34 EndZ=0
  constraints (12):
    c: PointOnObject(g0,g-7)
    c: PointOnObject(g0,g-6)
    c: Horizontal(g0)
    c: Coincident(g0,g1)
    c: Coincident(g1,g2)
    c: PointOnObject(g2,g-8)
    c: Coincident(g2,g3)
    c: Coincident(g3,g0)
    c: Vertical(g1)
    c: Horizontal(g2)
    c: Vertical(g3)
    c: PointOnObject(g-8,g3)
FEATURE [PartDesign::Pocket] Pocket072
  BaseFeature = -> Pocket071
  Direction = (1,0,0)
  Length = 5
  Length2 = 5
  Profile = -> Sketch195
  ReferenceAxis = -> Sketch195 [N_Axis]
  Refine = true
  Suppressed = false
  Type = 1
FEATURE [Sketcher::SketchObject] Sketch196
  ArcFitTolerance = 1e-06
  AttachmentSupport = -> [Pocket072]
  ExternalGeometry = -> [Pocket072]
  FullyConstrained = true
  MakeInternals = false
  MapMode = 5
  Placement = pos=(0,-26.5,0) rot=(1,0,0;1.5708rad)
  sketch-geometry (2):
    g0: GeomPoint X=10 Y=38 Z=0
    g1: GeomPoint X=10 Y=4 Z=0
  constraints (2):
    c: Symmetric(g-5,g-6,g0)
    c: Symmetric(g-8,g-10,g1)
FEATURE [PartDesign::Hole] Hole031
  BaseFeature = -> Pocket072
  CustomThreadClearance = 0
  Depth = 31
  DepthType = 0
  Diameter = 1.2
  DrillForDepth = false
  DrillPoint = 1
  DrillPointAngle = 118
  HoleCutCountersinkAngle = 90
  HoleCutCustomValues = true
  HoleCutDepth = 0.1
  HoleCutDiameter = 1.3
  HoleCutType = 4
  ModelThread = false
  Profile = -> Sketch196
  Refine = true
  Suppressed = false
  Tapered = false
  TaperedAngle = 90
  ThreadClass = 0
  ThreadDepth = 31
  ThreadDepthType = 0
  ThreadDirection = 0
  ThreadFit = 0
  ThreadSize = 0
  ThreadType = 1
  Threaded = false
  UseCustomThreadClearance = false
FEATURE [Sketcher::SketchObject] Sketch197
  ArcFitTolerance = 1e-06
  AttachmentSupport = -> [Hole031]
  ExternalGeometry = -> [Hole031]
  FullyConstrained = true
  MakeInternals = false
  MapMode = 5
  Placement = pos=(0,0,0) rot=(0.57735,-0.57735,-0.57735;2.0944rad)
  sketch-geometry (4):
    g0: Circle CenterX=21 CenterY=36.5 CenterZ=0 NormalX=0 NormalY=0 NormalZ=1 AngleXU=0 Radius=2.35
    g1: Circle CenterX=21 CenterY=5.5 CenterZ=0 NormalX=0 NormalY=0 NormalZ=1 AngleXU=0 Radius=2.35
    g2: GeomPoint X=21 Y=21 Z=0
    g3: GeomPoint X=26.5 Y=21 Z=0
  constraints (8):
    c: Vertical(g1,g0)
    c: DistanceY(g1,g0) = 31
    c: Diameter(g0) = 4.7
    c: Equal(g0,g1)
    c: Symmetric(g0,g1,g2)
    c: Symmetric(g-10,g-10,g3)
    c: Horizontal(g2,g3)
    c: DistanceX(g-5,g0) = 15.5
FEATURE [PartDesign::Pocket] Pocket073
  BaseFeature = -> Hole031
  Direction = (1,0,0)
  Length = 6
  Length2 = 5
  Profile = -> Sketch197
  ReferenceAxis = -> Sketch197 [N_Axis]
  Refine = true
  Suppressed = false
  Type = 0
FEATURE [PartDesign::Body] Body113  label="MotorSupport"
  AllowCompound = false
  Group = -> [Sketch193,Pad096,Sketch194,Pocket071,Sketch195,Pocket072,Sketch196,Hole031,Sketch197,Pocket073]
  Origin = -> Origin1385
  Placement = pos=(-160,230,156) rot=(0,0,1;0rad)
  Tip = -> Pocket073
FEATURE [Sketcher::SketchObject] Sketch198
  ArcFitTolerance = 1e-06
  AttachmentSupport = -> [Pocket066]
  ExternalGeometry = -> [Pocket066]
  FullyConstrained = true
  MakeInternals = false
  MapMode = 5
  Placement = pos=(1.94e-14,0,10) rot=(0,0,1;0rad)
  sketch-geometry (1):
    g0: GeomPoint X=0 Y=230 Z=0
  constraints (2):
    c: PointOnObject(g0,g-2)
    c: Distance(g0,g-5) = 10
FEATURE [PartDesign::Hole] Hole032
  BaseFeature = -> Pocket066
  CustomThreadClearance = 0
  Depth = 25
  DepthType = 0
  Diameter = 1.2
  DrillForDepth = false
  DrillPoint = 1
  DrillPointAngle = 118
  HoleCutCountersinkAngle = 90
  HoleCutCustomValues = true
  HoleCutDepth = 0.1
  HoleCutDiameter = 1.3
  HoleCutType = 4
  ModelThread = false
  Profile = -> Sketch198
  Refine = true
  Suppressed = false
  Tapered = false
  TaperedAngle = 90
  ThreadClass = 0
  ThreadDepth = 25
  ThreadDepthType = 0
  ThreadDirection = 0
  ThreadFit = 0
  ThreadSize = 0
  ThreadType = 1
  Threaded = false
  UseCustomThreadClearance = false
FEATURE [PartDesign::LinearPattern] LinearPattern011
  BaseFeature = -> Hole032
  Direction = -> Sketch198 [V_Axis]
  Length = 60
  Mode = 1
  Occurrences = 4
  Offset = 20
  Originals = -> [Hole032]
  Refine = true
  Reversed = true
  Suppressed = false
  TransformMode = 0
FEATURE [PartDesign::Body] Body084  label="2040x250"
  AllowCompound = false
  Group = -> [Clone032,Pad084,LinearPattern006,Sketch185,Pocket066,Sketch198,Hole032,LinearPattern011]
  Origin = -> Origin1258
  Placement = pos=(-150,260,-23) rot=(-0.58,0.58,0.58;4.18879rad)
  Tip = -> LinearPattern011
FEATURE [PartDesign::FeatureBase] Clone035
  BaseFeature = -> Body084
  Suppressed = false
FEATURE [Sketcher::SketchObject] Sketch188
  ArcFitTolerance = 1e-06
  AttachmentSupport = -> [Clone035]
  ExternalGeometry = -> [Clone035]
  FullyConstrained = true
  MakeInternals = false
  MapMode = 5
  Placement = pos=(-2.5e-15,0,-10) rot=(1,0,0;3.14159rad)
  sketch-geometry (4):
    g0: LineSegment StartX=30 StartY=-189.335 StartZ=0 EndX=23.1 EndY=-189.335 EndZ=0
    g1: LineSegment StartX=23.1 StartY=-189.335 StartZ=0 EndX=23.1 EndY=-210.665 EndZ=0
    g2: LineSegment StartX=23.1 StartY=-210.665 StartZ=0 EndX=30 EndY=-210.665 EndZ=0
    g3: LineSegment StartX=30 StartY=-210.665 StartZ=0 EndX=30 EndY=-189.335 EndZ=0
  constraints (10):
    c: Coincident(g0,g1)
    c: Coincident(g1,g2)
    c: Coincident(g2,g3)
    c: Coincident(g3,g0)
    c: Horizontal(g0)
    c: Horizontal(g2)
    c: Vertical(g1)
    c: Coincident(g0,g-3)
    c: Coincident(g-4,g2)
    c: PointOnObject(g1,g-5)
FEATURE [PartDesign::Pad] Pad093
  BaseFeature = -> Clone035
  Direction = (0,0,-1)
  Length = 10
  Length2 = 10
  Profile = -> Sketch188
  ReferenceAxis = -> Sketch188 [N_Axis]
  Refine = true
  Suppressed = false
  Type = 3
  UpToFace = -> Clone035 [Face11]
FEATURE [PartDesign::Pocket] Pocket068
  BaseFeature = -> Pad093
  Direction = (0,-1,0)
  Length = 5
  Length2 = 5
  Profile = -> Pad093 [Face107]
  Refine = true
  Suppressed = false
  Type = 1
FEATURE [PartDesign::Pad] Pad094
  BaseFeature = -> Pocket068
  Direction = (0,1,0)
  Length = 125
  Length2 = 10
  Profile = -> Pocket068 [Face7]
  Refine = true
  Reversed = true
  Suppressed = false
  Type = 0
FEATURE [Sketcher::SketchObject] Sketch199
  ArcFitTolerance = 1e-06
  AttachmentSupport = -> [Pad094]
  ExternalGeometry = -> [Pad094]
  FullyConstrained = true
  MakeInternals = false
  MapMode = 5
  Placement = pos=(-1.86e-14,0,-10) rot=(1,0,0;3.14159rad)
  sketch-geometry (1):
    g0: GeomPoint X=0 Y=-230 Z=0
  constraints (2):
    c: PointOnObject(g0,g-2)
    c: Distance(g0,g-3) = 10
FEATURE [PartDesign::Hole] Hole033
  BaseFeature = -> Pad094
  CustomThreadClearance = 0
  Depth = 25
  DepthType = 0
  Diameter = 1.2
  DrillForDepth = false
  DrillPoint = 1
  DrillPointAngle = 118
  HoleCutCountersinkAngle = 90
  HoleCutCustomValues = true
  HoleCutDepth = 0.1
  HoleCutDiameter = 1.3
  HoleCutType = 4
  ModelThread = false
  Profile = -> Sketch199
  Refine = true
  Suppressed = false
  Tapered = false
  TaperedAngle = 90
  ThreadClass = 0
  ThreadDepth = 25
  ThreadDepthType = 0
  ThreadDirection = 0
  ThreadFit = 0
  ThreadSize = 0
  ThreadType = 1
  Threaded = false
  UseCustomThreadClearance = false
FEATURE [PartDesign::LinearPattern] LinearPattern012
  BaseFeature = -> Hole033
  Direction = -> Sketch199 [V_Axis]
  Length = 60
  Mode = 1
  Occurrences = 4
  Offset = 20
  Originals = -> [Hole033]
  Refine = true
  Suppressed = false
  TransformMode = 0
FEATURE [PartDesign::Body] Body089  label="2040x25001"
  AllowCompound = false
  Group = -> [Clone035,Sketch188,Pad093,Pocket068,Pad094,Sketch199,Hole033,LinearPattern012]
  Origin = -> Origin1268
  Placement = pos=(220,260,-23) rot=(-0.58,0.58,0.58;4.18879rad)
  Tip = -> LinearPattern012
FEATURE [Sketcher::SketchObject] Sketch200
  ArcFitTolerance = 1e-06
  AttachmentSupport = -> [Pad072]
  ExternalGeometry = -> [Pad072]
  FullyConstrained = true
  MakeInternals = false
  MapMode = 5
  Placement = pos=(-2.6e-15,0,-10) rot=(1,0,0;3.14159rad)
  sketch-geometry (2):
    g0: GeomPoint X=0 Y=-240 Z=0
    g1: GeomPoint X=0 Y=-220 Z=0
  constraints (4):
    c: PointOnObject(g0,g-2)
    c: PointOnObject(g1,g-2)
    c: DistanceY(g0,g1) = 20
    c: DistanceY(g-6,g0) = 50
FEATURE [PartDesign::Hole] Hole034
  BaseFeature = -> Pad072
  CustomThreadClearance = 0
  Depth = 25
  DepthType = 0
  Diameter = 1.2
  DrillForDepth = false
  DrillPoint = 1
  DrillPointAngle = 118
  HoleCutCountersinkAngle = 90
  HoleCutCustomValues = true
  HoleCutDepth = 0.1
  HoleCutDiameter = 1.3
  HoleCutType = 4
  ModelThread = false
  Profile = -> Sketch200
  Refine = true
  Suppressed = false
  Tapered = false
  TaperedAngle = 90
  ThreadClass = 0
  ThreadDepth = 25
  ThreadDepthType = 0
  ThreadDirection = 0
  ThreadFit = 0
  ThreadSize = 0
  ThreadType = 1
  Threaded = false
  UseCustomThreadClearance = false
FEATURE [Sketcher::SketchObject] Sketch201
  ArcFitTolerance = 1e-06
  AttachmentSupport = -> [Hole034]
  ExternalGeometry = -> [Hole034]
  FullyConstrained = true
  MakeInternals = false
  MapMode = 5
  Placement = pos=(10,0,0) rot=(0.57735,0.57735,0.57735;2.0944rad)
  sketch-geometry (4):
    g0: GeomPoint X=280 Y=0 Z=0
    g1: GeomPoint X=260 Y=0 Z=0
    g2: GeomPoint X=-50 Y=0 Z=0
    g3: GeomPoint X=-30 Y=0 Z=0
  constraints (8):
    c: PointOnObject(g0,g-1)
    c: PointOnObject(g1,g-1)
    c: PointOnObject(g2,g-1)
    c: PointOnObject(g3,g-1)
    c: DistanceX(g2,g3) = 20
    c: Distance(g2,g-4) = 10
    c: DistanceX(g1,g0) = 20
    c: Distance(g0,g-6) = 10
FEATURE [PartDesign::Hole] Hole035
  BaseFeature = -> Hole034
  CustomThreadClearance = 0
  Depth = 25
  DepthType = 0
  Diameter = 1.2
  DrillForDepth = false
  DrillPoint = 1
  DrillPointAngle = 118
  HoleCutCountersinkAngle = 90
  HoleCutCustomValues = true
  HoleCutDepth = 0.1
  HoleCutDiameter = 1.3
  HoleCutType = 4
  ModelThread = false
  Profile = -> Sketch201
  Refine = true
  Suppressed = false
  Tapered = false
  TaperedAngle = 90
  ThreadClass = 0
  ThreadDepth = 25
  ThreadDepthType = 0
  ThreadDirection = 0
  ThreadFit = 0
  ThreadSize = 0
  ThreadType = 1
  Threaded = false
  UseCustomThreadClearance = false
FEATURE [PartDesign::Body] Body063  label="2020x30001"
  AllowCompound = false
  Group = -> [Clone016,Pad072,Sketch200,Hole034,Sketch201,Hole035]
  Origin = -> Origin1212
  Placement = pos=(220,20,-43) rot=(0,0,1;0rad)
  Tip = -> Hole035
FEATURE [Sketcher::SketchObject] Sketch202
  ArcFitTolerance = 1e-06
  AttachmentSupport = -> [Pad073]
  ExternalGeometry = -> [Pad073]
  FullyConstrained = true
  MakeInternals = false
  MapMode = 5
  Placement = pos=(-10,0,0) rot=(0.57735,-0.57735,-0.57735;2.0944rad)
  sketch-geometry (4):
    g0: GeomPoint X=-280 Y=0 Z=0
    g1: GeomPoint X=-260 Y=0 Z=0
    g2: GeomPoint X=50 Y=0 Z=0
    g3: GeomPoint X=30 Y=0 Z=0
  constraints (8):
    c: PointOnObject(g0,g-1)
    c: PointOnObject(g1,g-1)
    c: PointOnObject(g2,g-1)
    c: PointOnObject(g3,g-1)
    c: DistanceX(g3,g2) = 20
    c: DistanceX(g2,g-4) = 10
    c: DistanceX(g-6,g0) = 10
    c: Distance(g0,g1) = 20
FEATURE [PartDesign::Hole] Hole036
  BaseFeature = -> Pad073
  CustomThreadClearance = 0
  Depth = 25
  DepthType = 0
  Diameter = 1.2
  DrillForDepth = false
  DrillPoint = 1
  DrillPointAngle = 118
  HoleCutCountersinkAngle = 90
  HoleCutCustomValues = true
  HoleCutDepth = 0.1
  HoleCutDiameter = 1.3
  HoleCutType = 4
  ModelThread = false
  Profile = -> Sketch202
  Refine = true
  Suppressed = false
  Tapered = false
  TaperedAngle = 90
  ThreadClass = 0
  ThreadDepth = 25
  ThreadDepthType = 0
  ThreadDirection = 0
  ThreadFit = 0
  ThreadSize = 0
  ThreadType = 1
  Threaded = false
  UseCustomThreadClearance = false
FEATURE [Sketcher::SketchObject] Sketch203
  ArcFitTolerance = 1e-06
  AttachmentSupport = -> [Hole036]
  ExternalGeometry = -> [Hole036]
  FullyConstrained = true
  MakeInternals = false
  MapMode = 5
  Placement = pos=(-2.6e-15,0,-10) rot=(1,0,0;3.14159rad)
  sketch-geometry (2):
    g0: GeomPoint X=0 Y=-220 Z=0
    g1: GeomPoint X=0 Y=-240 Z=0
  constraints (4):
    c: PointOnObject(g0,g-2)
    c: PointOnObject(g1,g-2)
    c: DistanceY(g1,g0) = 20
    c: Distance(g1,g-6) = 50
FEATURE [PartDesign::Hole] Hole037
  BaseFeature = -> Hole036
  CustomThreadClearance = 0
  Depth = 25
  DepthType = 0
  Diameter = 1.2
  DrillForDepth = false
  DrillPoint = 1
  DrillPointAngle = 118
  HoleCutCountersinkAngle = 90
  HoleCutCustomValues = true
  HoleCutDepth = 0.1
  HoleCutDiameter = 1.3
  HoleCutType = 4
  ModelThread = false
  Profile = -> Sketch203
  Refine = true
  Suppressed = false
  Tapered = false
  TaperedAngle = 90
  ThreadClass = 0
  ThreadDepth = 25
  ThreadDepthType = 0
  ThreadDirection = 0
  ThreadFit = 0
  ThreadSize = 0
  ThreadType = 1
  Threaded = false
  UseCustomThreadClearance = false
FEATURE [PartDesign::Body] Body066  label="2020x30004"
  AllowCompound = false
  Group = -> [Clone019,Pad073,Sketch202,Hole036,Sketch203,Hole037]
  Origin = -> Origin1218
  Placement = pos=(-150,20,-43) rot=(0,0,1;0rad)
  Tip = -> Hole037
FEATURE [Sketcher::SketchObject] Sketch204
  ArcFitTolerance = 1e-06
  AttachmentSupport = -> [Origin1387]
  FullyConstrained = true
  MakeInternals = false
  MapMode = 5
  Placement = pos=(0,0,0) rot=(1,0,0;1.5708rad)
  sketch-geometry (6):
    g0: LineSegment StartX=0 StartY=0 StartZ=0 EndX=0 EndY=20 EndZ=0
    g1: LineSegment [constr] StartX=0 StartY=20 StartZ=0 EndX=20 EndY=0 EndZ=0
    g2: LineSegment StartX=20 StartY=0 StartZ=0 EndX=0 EndY=0 EndZ=0
    g3: LineSegment StartX=0 StartY=20 StartZ=0 EndX=4 EndY=20 EndZ=0
    g4: LineSegment StartX=4 StartY=20 StartZ=0 EndX=20 EndY=4 EndZ=0
    g5: LineSegment StartX=20 StartY=4 StartZ=0 EndX=20 EndY=0 EndZ=0
  constraints (16):
    c: Coincident(g-1,g0)
    c: PointOnObject(g0,g-2)
    c: Coincident(g0,g1)
    c: PointOnObject(g1,g-1)
    c: Coincident(g1,g2)
    c: Coincident(g2,g0)
    c: Equal(g2,g0)
    c: DistanceX(g2,g2) = 20
    c: Coincident(g0,g3)
    c: Horizontal(g3)
    c: Coincident(g3,g4)
    c: Coincident(g4,g5)
    c: Coincident(g5,g1)
    c: Vertical(g5)
    c: DistanceY(g5,g5) = 4
    c: Equal(g3,g5)
FEATURE [PartDesign::Pad] Pad097
  Direction = (0,-1,0)
  Length = 40
  Length2 = 10
  Profile = -> Sketch204
  ReferenceAxis = -> Sketch204 [N_Axis]
  Refine = true
  Suppressed = false
  Type = 0
FEATURE [PartDesign::Thickness] Thickness
  Base = -> Pad097 [Face2,Face3,Face4]
  BaseFeature = -> Pad097
  Intersection = false
  Join = 0
  Mode = 0
  Refine = true
  Reversed = true
  SupportTransform = false
  Suppressed = false
  Value = 3
FEATURE [Sketcher::SketchObject] Sketch205
  ArcFitTolerance = 1e-06
  AttachmentSupport = -> [Thickness]
  ExternalGeometry = -> [Thickness]
  FullyConstrained = true
  MakeInternals = false
  MapMode = 5
  Placement = pos=(0,7e-16,3) rot=(0,0,1;0rad)
  sketch-geometry (15):
    g0: GeomPoint X=11.5 Y=-10 Z=0
    g1: GeomPoint X=11.5 Y=-30 Z=0
    g2: GeomPoint [constr] X=20 Y=-20 Z=0
    g3: GeomPoint [constr] X=11.5 Y=-20 Z=0
    g4: ArcOfCircle CenterX=10 CenterY=-10 CenterZ=0 NormalX=0 NormalY=0 NormalZ=1 AngleXU=0 Radius=3 StartAngle=1.5708 EndAngle=4.71239
    g5: ArcOfCircle CenterX=13 CenterY=-10 CenterZ=0 NormalX=0 NormalY=0 NormalZ=1 AngleXU=0 Radius=3 StartAngle=4.71239 EndAngle=7.85398
    g6: LineSegment StartX=10 StartY=-7 StartZ=0 EndX=13 EndY=-7 EndZ=0
    g7: LineSegment StartX=10 StartY=-13 StartZ=0 EndX=13 EndY=-13 EndZ=0
    g8: ArcOfCircle CenterX=10 CenterY=-30 CenterZ=0 NormalX=0 NormalY=0 NormalZ=1 AngleXU=0 Radius=3 StartAngle=1.5708 EndAngle=4.71239
    g9: ArcOfCircle CenterX=13 CenterY=-30 CenterZ=0 NormalX=0 NormalY=0 NormalZ=1 AngleXU=0 Radius=3 StartAngle=4.71239 EndAngle=7.85398
    g10: LineSegment StartX=10 StartY=-27 StartZ=0 EndX=13 EndY=-27 EndZ=0
    g11: LineSegment StartX=10 StartY=-33 StartZ=0 EndX=13 EndY=-33 EndZ=0
    g12: GeomPoint X=7 Y=-30 Z=0
    g13: GeomPoint X=16 Y=-30 Z=0
    g14: GeomPoint X=11.5 Y=-3 Z=0
  constraints (29):
    c: DistanceY(g1,g0) = 20
    c: Symmetric(g-3,g-3,g2)
    c: Vertical(g0,g1)
    c: Horizontal(g2,g3)
    c: Symmetric(g0,g1,g3)
    c: Tangent(g4,g6) = 1.5708
    c: Tangent(g4,g7) = -1.5708
    c: Tangent(g5,g6) = 1.5708
    c: Tangent(g5,g7) = -1.5708
    c: Equal(g4,g5)
    c: Radius(g4) = 3
    c: Horizontal(g6)
    c: Tangent(g8,g10) = 1.5708
    c: Tangent(g8,g11) = -1.5708
    c: Tangent(g9,g10) = 1.5708
    c: Tangent(g9,g11) = -1.5708
    c: Equal(g8,g9)
    c: Horizontal(g10)
    c: Equal(g10,g7)
    c: Equal(g8,g4)
    c: Symmetric(g4,g5,g0)
    c: Symmetric(g8,g9,g1)
    c: PointOnObject(g12,g8)
    c: PointOnObject(g13,g9)
    c: Horizontal(g13,g12)
    c: Horizontal(g12,g8)
    c: DistanceX(g12,g13) = 9
    c: Symmetric(g-6,g-6,g14)
    c: Vertical(g14,g0)
FEATURE [PartDesign::Pocket] Pocket074
  BaseFeature = -> Thickness
  Direction = (0,0,-1)
  Length = 5
  Length2 = 5
  Profile = -> Sketch205
  ReferenceAxis = -> Sketch205 [N_Axis]
  Refine = true
  Suppressed = false
  Type = 0
FEATURE [PartDesign::PolarPattern] PolarPattern011
  Angle = 90
  Axis = -> Y_Axis1024
  BaseFeature = -> Pocket074
  Mode = 1
  Occurrences = 2
  Offset = 90
  Originals = -> [Pocket074]
  Refine = true
  Reversed = true
  Suppressed = false
  TransformMode = 0
FEATURE [PartDesign::Pocket] Pocket075
  BaseFeature = -> PolarPattern011
  Direction = (1,0,0)
  Length = 5
  Length2 = 5
  Profile = -> PolarPattern011 [Face29,Face28]
  Refine = true
  Suppressed = false
  Type = 0
FEATURE [Sketcher::SketchObject] Sketch206
  ArcFitTolerance = 1e-06
  AttachmentSupport = -> [Pocket075]
  ExternalGeometry = -> [Pocket075]
  FullyConstrained = true
  MakeInternals = false
  MapMode = 5
  Placement = pos=(3,0,0) rot=(0.57735,0.57735,0.57735;2.0944rad)
  sketch-geometry (6):
    g0: LineSegment StartX=-21.5 StartY=20 StartZ=0 EndX=-21.5 EndY=3 EndZ=0
    g1: LineSegment StartX=-21.5 StartY=3 StartZ=0 EndX=-18.5 EndY=3 EndZ=0
    g2: LineSegment StartX=-18.5 StartY=3 StartZ=0 EndX=-18.5 EndY=20 EndZ=0
    g3: LineSegment StartX=-18.5 StartY=20 StartZ=0 EndX=-21.5 EndY=20 EndZ=0
    g4: GeomPoint X=-20 Y=20 Z=0
    g5: GeomPoint X=-20 Y=20 Z=0
  constraints (13):
    c: Coincident(g0,g1)
    c: Coincident(g1,g2)
    c: Coincident(g2,g3)
    c: Coincident(g3,g0)
    c: Vertical(g0)
    c: Vertical(g2)
    c: Horizontal(g1)
    c: Horizontal(g3)
    c: PointOnObject(g1,g-6)
    c: DistanceX(g3,g3) = 3
    c: Symmetric(g3,g3,g4)
    c: Symmetric(g-3,g-3,g5)
    c: Coincident(g5,g4)
FEATURE [PartDesign::Pad] Pad098
  BaseFeature = -> Pocket075
  Direction = (1,0,0)
  Length = 1
  Length2 = 10
  Profile = -> Sketch206
  ReferenceAxis = -> Sketch206 [N_Axis]
  Refine = true
  Suppressed = false
  Type = 0
FEATURE [PartDesign::Pad] Pad099
  BaseFeature = -> Pad098
  Direction = (0,1,0)
  Length = 10
  Length2 = 10
  Profile = -> Pad098 [Face24]
  Refine = true
  Suppressed = false
  Type = 3
  UpToFace = -> Pad098 [Face29]
FEATURE [Sketcher::SketchObject] Sketch207
  ArcFitTolerance = 1e-06
  AttachmentSupport = -> [Pad099]
  ExternalGeometry = -> [Pad099]
  FullyConstrained = true
  MakeInternals = false
  MapMode = 5
  Placement = pos=(-5.8e-15,0,20) rot=(0,0,1;0rad)
  sketch-geometry (4):
    g0: LineSegment StartX=20 StartY=-21.5 StartZ=0 EndX=3 EndY=-21.5 EndZ=0
    g1: LineSegment StartX=3 StartY=-21.5 StartZ=0 EndX=3 EndY=-37 EndZ=0
    g2: LineSegment StartX=3 StartY=-37 StartZ=0 EndX=20 EndY=-37 EndZ=0
    g3: LineSegment StartX=20 StartY=-37 StartZ=0 EndX=20 EndY=-21.5 EndZ=0
  constraints (12):
    c: Coincident(g0,g1)
    c: Coincident(g1,g2)
    c: Coincident(g2,g3)
    c: Coincident(g3,g0)
    c: Horizontal(g0)
    c: Horizontal(g2)
    c: Vertical(g1)
    c: Vertical(g3)
    c: PointOnObject(g0,g-19)
    c: DistanceY(g0,g-20) = 3
    c: Equal(g3,g-5)
    c: Vertical(g0,g-16)
FEATURE [PartDesign::Pocket] Pocket076
  BaseFeature = -> Pad099
  Direction = (0,0,-1)
  Length = 5
  Length2 = 5
  Profile = -> Sketch207
  ReferenceAxis = -> Sketch207 [N_Axis]
  Refine = true
  Suppressed = false
  Type = 3
  UpToFace = -> Pad099 [Face25]
FEATURE [Sketcher::SketchObject] Sketch208
  ArcFitTolerance = 1e-06
  AttachmentSupport = -> [Pocket076]
  ExternalGeometry = -> [Pocket076]
  FullyConstrained = true
  MakeInternals = false
  MapMode = 5
  Placement = pos=(0,0,0) rot=(0.57735,-0.57735,-0.57735;2.0944rad)
  sketch-geometry (24):
    g0: LineSegment StartX=7.5 StartY=18.5 StartZ=0 EndX=7.5 EndY=16.5 EndZ=0
    g1: LineSegment StartX=7.5 StartY=16.5 StartZ=0 EndX=12.5 EndY=16.5 EndZ=0
    g2: LineSegment StartX=12.5 StartY=16.5 StartZ=0 EndX=12.5 EndY=18.5 EndZ=0
    g3: LineSegment StartX=12.5 StartY=18.5 StartZ=0 EndX=7.5 EndY=18.5 EndZ=0
    g4: LineSegment StartX=27.5 StartY=18.5 StartZ=0 EndX=27.5 EndY=16.5 EndZ=0
    g5: LineSegment StartX=27.5 StartY=16.5 StartZ=0 EndX=32.5 EndY=16.5 EndZ=0
    g6: LineSegment StartX=32.5 StartY=16.5 StartZ=0 EndX=32.5 EndY=18.5 EndZ=0
    g7: LineSegment StartX=32.5 StartY=18.5 StartZ=0 EndX=27.5 EndY=18.5 EndZ=0
    g8: LineSegment StartX=27.5 StartY=3.5 StartZ=0 EndX=27.5 EndY=1.5 EndZ=0
    g9: LineSegment StartX=27.5 StartY=1.5 StartZ=0 EndX=32.5 EndY=1.5 EndZ=0
    g10: LineSegment StartX=32.5 StartY=1.5 StartZ=0 EndX=32.5 EndY=3.5 EndZ=0
    g11: LineSegment StartX=32.5 StartY=3.5 StartZ=0 EndX=27.5 EndY=3.5 EndZ=0
    g12: LineSegment StartX=7.5 StartY=3.5 StartZ=0 EndX=7.5 EndY=1.5 EndZ=0
    g13: LineSegment StartX=7.5 StartY=1.5 StartZ=0 EndX=12.5 EndY=1.5 EndZ=0
    g14: LineSegment StartX=12.5 StartY=1.5 StartZ=0 EndX=12.5 EndY=3.5 EndZ=0
    g15: LineSegment StartX=12.5 StartY=3.5 StartZ=0 EndX=7.5 EndY=3.5 EndZ=0
    g16: GeomPoint X=10 Y=3.5 Z=0
    g17: GeomPoint X=30 Y=3.5 Z=0
    g18: GeomPoint X=30 Y=16.5 Z=0
    g19: GeomPoint X=27.5 Y=17.5 Z=0
    g20: GeomPoint X=12.5 Y=17.5 Z=0
    g21: GeomPoint X=10 Y=16.5 Z=0
    g22: LineSegment [constr] StartX=10 StartY=18.5 StartZ=0 EndX=10 EndY=20 EndZ=0
    g23: LineSegment [constr] StartX=10 StartY=1.5 StartZ=0 EndX=10 EndY=2.2e-15 EndZ=0
  constraints (60):
    c: Coincident(g0,g1)
    c: Coincident(g1,g2)
    c: Coincident(g2,g3)
    c: Coincident(g3,g0)
    c: Vertical(g0)
    c: Vertical(g2)
    c: Horizontal(g1)
    c: Horizontal(g3)
    c: Coincident(g4,g5)
    c: Coincident(g5,g6)
    c: Coincident(g6,g7)
    c: Coincident(g7,g4)
    c: Vertical(g4)
    c: Vertical(g6)
    c: Horizontal(g5)
    c: Horizontal(g7)
    c: Coincident(g8,g9)
    c: Coincident(g9,g10)
    c: Coincident(g10,g11)
    c: Coincident(g11,g8)
    c: Vertical(g8)
    c: Vertical(g10)
    c: Horizontal(g9)
    c: Horizontal(g11)
    c: Coincident(g12,g13)
    c: Coincident(g13,g14)
    c: Coincident(g14,g15)
    c: Coincident(g15,g12)
    c: Vertical(g12)
    c: Vertical(g14)
    c: Horizontal(g13)
    c: Horizontal(g15)
    c: Symmetric(g15,g15,g16)
    c: Symmetric(g11,g11,g17)
    c: Symmetric(g5,g5,g18)
    c: Symmetric(g4,g4,g19)
    c: Symmetric(g2,g2,g20)
    c: Symmetric(g1,g1,g21)
    c: Vertical(g21,g-15)
    c: Vertical(g-15,g16)
    c: Vertical(g17,g18)
    c: Vertical(g18,g-11)
    c: Equal(g11,g5)
    c: Equal(g5,g1)
    c: Equal(g1,g15)
    c: Equal(g14,g2)
    c: Equal(g2,g4)
    c: Equal(g4,g8)
    c: Horizontal(g11,g14)
    c: Horizontal(g3,g4)
    c: DistanceY(g0,g0) = 2
    c: Symmetric(g3,g3,g22)
    c: PointOnObject(g22,g-8)
    c: Vertical(g22)
    c: Symmetric(g13,g13,g23)
    c: PointOnObject(g23,g-5)
    c: Vertical(g23)
    c: Equal(g23,g22)
    c: DistanceY(g23,g23) = 1.5
    c: DistanceX(g3,g3) = 5
FEATURE [PartDesign::Pad] Pad100
  BaseFeature = -> Pocket076
  Direction = (-1,0,0)
  Length = 1.25
  Length2 = 10
  Profile = -> Sketch208
  ReferenceAxis = -> Sketch208 [N_Axis]
  Refine = true
  Suppressed = false
  Type = 0
FEATURE [Sketcher::SketchObject] Sketch209
  ArcFitTolerance = 1e-06
  AttachmentSupport = -> [Pad100]
  ExternalGeometry = -> [Pad100]
  FullyConstrained = true
  MakeInternals = false
  MapMode = 5
  Placement = pos=(0,0,0) rot=(1,0,0;3.14159rad)
  sketch-geometry (35):
    g0: LineSegment [constr] StartX=1.5 StartY=12.5 StartZ=0 EndX=1.5 EndY=7.5 EndZ=0
    g1: LineSegment [constr] StartX=1.5 StartY=7.5 StartZ=0 EndX=3.5 EndY=7.5 EndZ=0
    g2: LineSegment [constr] StartX=3.5 StartY=7.5 StartZ=0 EndX=3.5 EndY=12.5 EndZ=0
    g3: LineSegment [constr] StartX=3.5 StartY=12.5 StartZ=0 EndX=1.5 EndY=12.5 EndZ=0
    g4: LineSegment [constr] StartX=16.5 StartY=12.5 StartZ=0 EndX=16.5 EndY=7.5 EndZ=0
    g5: LineSegment [constr] StartX=16.5 StartY=7.5 StartZ=0 EndX=18.5 EndY=7.5 EndZ=0
    g6: LineSegment [constr] StartX=18.5 StartY=7.5 StartZ=0 EndX=18.5 EndY=12.5 EndZ=0
    g7: LineSegment [constr] StartX=18.5 StartY=12.5 StartZ=0 EndX=16.5 EndY=12.5 EndZ=0
    g8: LineSegment [constr] StartX=16.5 StartY=32.5 StartZ=0 EndX=16.5 EndY=27.5 EndZ=0
    g9: LineSegment [constr] StartX=16.5 StartY=27.5 StartZ=0 EndX=18.5 EndY=27.5 EndZ=0
    g10: LineSegment [constr] StartX=18.5 StartY=27.5 StartZ=0 EndX=18.5 EndY=32.5 EndZ=0
    g11: LineSegment [constr] StartX=18.5 StartY=32.5 StartZ=0 EndX=16.5 EndY=32.5 EndZ=0
    g12: LineSegment [constr] StartX=1.5 StartY=32.5 StartZ=0 EndX=1.5 EndY=27.5 EndZ=0
    g13: LineSegment [constr] StartX=1.5 StartY=27.5 StartZ=0 EndX=3.5 EndY=27.5 EndZ=0
    g14: LineSegment [constr] StartX=3.5 StartY=27.5 StartZ=0 EndX=3.5 EndY=32.5 EndZ=0
    g15: LineSegment [constr] StartX=3.5 StartY=32.5 StartZ=0 EndX=1.5 EndY=32.5 EndZ=0
    g16: LineSegment StartX=7.5 StartY=38 StartZ=0 EndX=7.5 EndY=35 EndZ=0
    g17: LineSegment StartX=7.5 StartY=35 StartZ=0 EndX=12.5 EndY=35 EndZ=0
    g18: LineSegment StartX=12.5 StartY=35 StartZ=0 EndX=12.5 EndY=38 EndZ=0
    g19: LineSegment StartX=12.5 StartY=38 StartZ=0 EndX=7.5 EndY=38 EndZ=0
    g20: LineSegment StartX=7.5 StartY=21.5 StartZ=0 EndX=7.5 EndY=18.5 EndZ=0
    g21: LineSegment StartX=7.5 StartY=18.5 StartZ=0 EndX=12.5 EndY=18.5 EndZ=0
    g22: LineSegment StartX=12.5 StartY=18.5 StartZ=0 EndX=12.5 EndY=21.5 EndZ=0
    g23: LineSegment StartX=12.5 StartY=21.5 StartZ=0 EndX=7.5 EndY=21.5 EndZ=0
    g24: LineSegment StartX=7.5 StartY=5 StartZ=0 EndX=7.5 EndY=2 EndZ=0
    g25: LineSegment StartX=7.5 StartY=2 StartZ=0 EndX=12.5 EndY=2 EndZ=0
    g26: LineSegment StartX=12.5 StartY=2 StartZ=0 EndX=12.5 EndY=5 EndZ=0
    g27: LineSegment StartX=12.5 StartY=5 StartZ=0 EndX=7.5 EndY=5 EndZ=0
    g28: GeomPoint X=10 Y=0 Z=0
    g29: GeomPoint X=10 Y=2 Z=0
    g30: GeomPoint X=12.5 Y=20 Z=0
    g31: GeomPoint X=10 Y=20 Z=0
    g32: GeomPoint X=12.5 Y=36.5 Z=0
    g33: GeomPoint X=10 Y=40 Z=0
    g34: GeomPoint X=10 Y=36.5 Z=0
  constraints (91):
    c: Coincident(g0,g1)
    c: Coincident(g1,g2)
    c: Coincident(g2,g3)
    c: Coincident(g3,g0)
    c: Vertical(g0)
    c: Vertical(g2)
    c: Horizontal(g1)
    c: Horizontal(g3)
    c: Coincident(g4,g5)
    c: Coincident(g5,g6)
    c: Coincident(g6,g7)
    c: Coincident(g7,g4)
    c: Vertical(g4)
    c: Vertical(g6)
    c: Horizontal(g5)
    c: Horizontal(g7)
    c: Coincident(g8,g9)
    c: Coincident(g9,g10)
    c: Coincident(g10,g11)
    c: Coincident(g11,g8)
    c: Vertical(g8)
    c: Vertical(g10)
    c: Horizontal(g9)
    c: Horizontal(g11)
    c: Coincident(g12,g13)
    c: Coincident(g13,g14)
    c: Coincident(g14,g15)
    c: Coincident(g15,g12)
    c: Vertical(g12)
    c: Vertical(g14)
    c: Horizontal(g13)
    c: Horizontal(g15)
    c: Equal(g15,g11)
    c: Equal(g11,g7)
    c: Equal(g7,g3)
    c: Equal(g2,g4)
    c: Equal(g4,g8)
    c: Equal(g8,g14)
    c: Vertical(g12,g0)
    c: Vertical(g4,g8)
    c: Horizontal(g3,g4)
    c: Horizontal(g9,g13)
    c: Horizontal(g-5,g12)
    c: Equal(g-5,g12)
    c: Horizontal(g-9,g0)
    c: Distance(g-9,g0) = 1.5
    c: DistanceX(g1,g1) = 2
    c: Distance(g-12,g6) = 1.5
    c: Coincident(g16,g17)
    c: Coincident(g17,g18)
    c: Coincident(g18,g19)
    c: Coincident(g19,g16)
    c: Vertical(g16)
    c: Vertical(g18)
    c: Horizontal(g17)
    c: Horizontal(g19)
    c: Coincident(g20,g21)
    c: Coincident(g21,g22)
    c: Coincident(g22,g23)
    c: Coincident(g23,g20)
    c: Vertical(g20)
    c: Vertical(g22)
    c: Horizontal(g21)
    c: Horizontal(g23)
    c: Coincident(g24,g25)
    c: Coincident(g25,g26)
    c: Coincident(g26,g27)
    c: Coincident(g27,g24)
    c: Vertical(g24)
    c: Vertical(g26)
    c: Horizontal(g25)
    c: Horizontal(g27)
    c: Vertical(g20,g16)
    c: Vertical(g16,g24)
    c: Equal(g24,g20)
    c: Equal(g20,g16)
    c: Equal(g19,g23)
    c: Equal(g23,g27)
    c: Symmetric(g-13,g-13,g28)
    c: Symmetric(g25,g25,g29)
    c: Vertical(g28,g29)
    c: Distance(g-13,g25) = 2
    c: Distance(g-20,g27) = 2
    c: Symmetric(g22,g22,g30)
    c: Symmetric(g-14,g-14,g33)
    c: Horizontal(g32,g34)
    c: Symmetric(g18,g17,g32)
    c: Symmetric(g33,g-19,g34)
    c: Symmetric(g-19,g-23,g31)
    c: Horizontal(g30,g31)
    c: Equal(g14,g17)
FEATURE [PartDesign::Pad] Pad101
  BaseFeature = -> Pad100
  Direction = (0,0,-1)
  Length = 1.25
  Length2 = 10
  Profile = -> Sketch209
  ReferenceAxis = -> Sketch209 [N_Axis]
  Refine = true
  Suppressed = false
  Type = 0
FEATURE [PartDesign::Body] Body114  label="2040 corner bracket"
  AllowCompound = false
  Group = -> [Sketch204,Pad097,Thickness,Sketch205,Pocket074,PolarPattern011,Pocket075,Sketch206,Pad098,Pad099,Sketch207,Pocket076,Sketch208,Pad100,Sketch209,Pad101]
  Origin = -> Origin1387
  Placement = pos=(1000,0,0) rot=(0,0,1;0rad)
  Tip = -> Pad101
FEATURE [PartDesign::FeatureBase] Clone054
  BaseFeature = -> Body114
  Suppressed = false
FEATURE [PartDesign::Body] Body115  label="2040 corner"
  AllowCompound = false
  Group = -> [Clone054]
  Origin = -> Origin1389
  Placement = pos=(-40,0,-33) rot=(0,0,1;0rad)
  Tip = -> Clone054
FEATURE [PartDesign::FeatureBase] Clone055
  BaseFeature = -> Body114
  Suppressed = false
FEATURE [PartDesign::Body] Body116  label="2040 corner001"
  AllowCompound = false
  Group = -> [Clone055]
  Origin = -> Origin1391
  Placement = pos=(130,0,-33) rot=(0,0,1;0rad)
  Tip = -> Clone055
FEATURE [PartDesign::FeatureBase] Clone056
  BaseFeature = -> Body114
  Suppressed = false
FEATURE [PartDesign::Body] Body117  label="2040 corner003"
  AllowCompound = false
  Group = -> [Clone056]
  Origin = -> Origin1393
  Placement = pos=(-40,310,-33) rot=(0,0,1;0rad)
  Tip = -> Clone056
FEATURE [PartDesign::FeatureBase] Clone057
  BaseFeature = -> Body114
  Suppressed = false
FEATURE [PartDesign::Body] Body118  label="2040 corner004"
  AllowCompound = false
  Group = -> [Clone057]
  Origin = -> Origin1395
  Placement = pos=(130,310,-33) rot=(0,0,1;0rad)
  Tip = -> Clone057
FEATURE [PartDesign::FeatureBase] Clone058
  BaseFeature = -> Body114
  Suppressed = false
FEATURE [PartDesign::Body] Body119  label="2040 corner002"
  AllowCompound = false
  Group = -> [Clone058]
  Origin = -> Origin1397
  Placement = pos=(-60,0,-33) rot=(0,1,0;4.71239rad)
  Tip = -> Clone058
FEATURE [PartDesign::FeatureBase] Clone059
  BaseFeature = -> Body114
  Suppressed = false
FEATURE [PartDesign::Body] Body120  label="2040 corner005"
  AllowCompound = false
  Group = -> [Clone059]
  Origin = -> Origin1399
  Placement = pos=(-60,310,-33) rot=(0,1,0;4.71239rad)
  Tip = -> Clone059
FEATURE [PartDesign::FeatureBase] Clone060
  BaseFeature = -> Body114
  Suppressed = false
FEATURE [PartDesign::Body] Body121  label="2040 corner006"
  AllowCompound = false
  Group = -> [Clone060]
  Origin = -> Origin1401
  Placement = pos=(110,0,-33) rot=(0,1,0;4.71239rad)
  Tip = -> Clone060
FEATURE [PartDesign::FeatureBase] Clone061
  BaseFeature = -> Body114
  Suppressed = false
FEATURE [PartDesign::Body] Body122  label="2040 corner007"
  AllowCompound = false
  Group = -> [Clone061]
  Origin = -> Origin1403
  Placement = pos=(110,310,-33) rot=(0,1,0;4.71239rad)
  Tip = -> Clone061
FEATURE [Sketcher::SketchObject] Sketch210
  ArcFitTolerance = 1e-06
  AttachmentSupport = -> [LinearPattern]
  ExternalGeometry = -> [LinearPattern]
  FullyConstrained = true
  MakeInternals = false
  MapMode = 5
  Placement = pos=(0,-1.2e-15,-5.6) rot=(1,0,0;3.14159rad)
  sketch-geometry (41):
    g0: LineSegment [constr] StartX=6 StartY=222.5 StartZ=0 EndX=31 EndY=222.5 EndZ=0
    g1: LineSegment [constr] StartX=31 StartY=222.5 StartZ=0 EndX=31 EndY=247.5 EndZ=0
    g2: LineSegment [constr] StartX=31 StartY=247.5 StartZ=0 EndX=6 EndY=247.5 EndZ=0
    g3: LineSegment [constr] StartX=6 StartY=247.5 StartZ=0 EndX=6 EndY=222.5 EndZ=0
    g4: GeomPoint [constr] X=18.5 Y=235 Z=0
    g5: LineSegment [constr] StartX=96 StartY=222.5 StartZ=0 EndX=121 EndY=222.5 EndZ=0
    g6: LineSegment [constr] StartX=121 StartY=222.5 StartZ=0 EndX=121 EndY=247.5 EndZ=0
    g7: LineSegment [constr] StartX=121 StartY=247.5 StartZ=0 EndX=96 EndY=247.5 EndZ=0
    g8: LineSegment [constr] StartX=96 StartY=247.5 StartZ=0 EndX=96 EndY=222.5 EndZ=0
    g9: GeomPoint [constr] X=108.5 Y=235 Z=0
    g10: LineSegment [constr] StartX=96 StartY=52.5 StartZ=0 EndX=121 EndY=52.5 EndZ=0
    g11: LineSegment [constr] StartX=121 StartY=52.5 StartZ=0 EndX=121 EndY=77.5 EndZ=0
    g12: LineSegment [constr] StartX=121 StartY=77.5 StartZ=0 EndX=96 EndY=77.5 EndZ=0
    g13: LineSegment [constr] StartX=96 StartY=77.5 StartZ=0 EndX=96 EndY=52.5 EndZ=0
    g14: GeomPoint [constr] X=108.5 Y=65 Z=0
    g15: LineSegment [constr] StartX=6 StartY=52.5 StartZ=0 EndX=31 EndY=52.5 EndZ=0
    g16: LineSegment [constr] StartX=31 StartY=52.5 StartZ=0 EndX=31 EndY=77.5 EndZ=0
    g17: LineSegment [constr] StartX=31 StartY=77.5 StartZ=0 EndX=6 EndY=77.5 EndZ=0
    g18: LineSegment [constr] StartX=6 StartY=77.5 StartZ=0 EndX=6 EndY=52.5 EndZ=0
    g19: GeomPoint [constr] X=18.5 Y=65 Z=0
    g20: GeomPoint [constr] X=14.5 Y=150 Z=0
    g21: LineSegment [constr] StartX=14.5 StartY=150 StartZ=0 EndX=6 EndY=77.5 EndZ=0
    g22: LineSegment [constr] StartX=14.5 StartY=150 StartZ=0 EndX=6 EndY=222.5 EndZ=0
    g23: GeomPoint [constr] X=18.5 Y=300 Z=0
    g24: GeomPoint [constr] X=108.5 Y=300 Z=0
    g25: GeomPoint X=6 Y=247.5 Z=0
    g26: GeomPoint X=31 Y=247.5 Z=0
    g27: GeomPoint X=31 Y=222.5 Z=0
    g28: GeomPoint X=6 Y=222.5 Z=0
    g29: GeomPoint X=6 Y=77.5 Z=0
    g30: GeomPoint X=6 Y=52.5 Z=0
    g31: GeomPoint X=31 Y=52.5 Z=0
    g32: GeomPoint X=31 Y=77.5 Z=0
    g33: GeomPoint X=96 Y=77.5 Z=0
    g34: GeomPoint X=96 Y=52.5 Z=0
    g35: GeomPoint X=121 Y=52.5 Z=0
    g36: GeomPoint X=121 Y=77.5 Z=0
    g37: GeomPoint X=121 Y=247.5 Z=0
    g38: GeomPoint X=121 Y=222.5 Z=0
    g39: GeomPoint X=96 Y=222.5 Z=0
    g40: GeomPoint X=96 Y=247.5 Z=0
  constraints (75):
    c: Coincident(g0,g1)
    c: Coincident(g1,g2)
    c: Coincident(g2,g3)
    c: Coincident(g3,g0)
    c: Horizontal(g0)
    c: Horizontal(g2)
    c: Vertical(g1)
    c: Vertical(g3)
    c: Symmetric(g2,g0,g4)
    c: Distance(g1,g3) = 25
    c: Distance(g0,g2) = 25
    c: Coincident(g5,g6)
    c: Coincident(g6,g7)
    c: Coincident(g7,g8)
    c: Coincident(g8,g5)
    c: Horizontal(g5)
    c: Horizontal(g7)
    c: Vertical(g6)
    c: Vertical(g8)
    c: Symmetric(g7,g5,g9)
    c: Distance(g6,g8) = 25
    c: Distance(g5,g7) = 25
    c: Coincident(g10,g11)
    c: Coincident(g11,g12)
    c: Coincident(g12,g13)
    c: Coincident(g13,g10)
    c: Horizontal(g10)
    c: Horizontal(g12)
    c: Vertical(g11)
    c: Vertical(g13)
    c: Symmetric(g12,g10,g14)
    c: Distance(g11,g13) = 25
    c: Distance(g10,g12) = 25
    c: Coincident(g15,g16)
    c: Coincident(g16,g17)
    c: Coincident(g17,g18)
    c: Coincident(g18,g15)
    c: Horizontal(g15)
    c: Horizontal(g17)
    c: Vertical(g16)
    c: Vertical(g18)
    c: Symmetric(g17,g15,g19)
    c: Distance(g16,g18) = 25
    c: Distance(g15,g17) = 25
    c: Horizontal(g12,g16)
    c: Vertical(g16,g0)
    c: Horizontal(g0,g5)
    c: Vertical(g5,g12)
    c: Distance(g15,g0) = 170
    c: Symmetric(g-3,g-3,g20)
    c: Coincident(g21,g20)
    c: Coincident(g21,g17)
    c: Coincident(g22,g20)
    c: Coincident(g22,g0)
    c: Equal(g22,g21)
    c: Symmetric(g-6,g-6,g23)
    c: Symmetric(g-10,g-10,g24)
    c: Vertical(g23,g4)
    c: Vertical(g9,g24)
    c: Coincident(g25,g2)
    c: Coincident(g26,g1)
    c: Coincident(g27,g0)
    c: Coincident(g28,g0)
    c: Coincident(g29,g17)
    c: Coincident(g30,g15)
    c: Coincident(g31,g15)
    c: Coincident(g32,g16)
    c: Coincident(g33,g12)
    c: Coincident(g34,g10)
    c: Coincident(g35,g10)
    c: Coincident(g36,g11)
    c: Coincident(g37,g6)
    c: Coincident(g38,g5)
    c: Coincident(g39,g5)
    c: Coincident(g40,g7)
FEATURE [PartDesign::Hole] Hole038
  BaseFeature = -> LinearPattern
  CustomThreadClearance = 0
  Depth = 25
  DepthType = 0
  Diameter = 1.2
  DrillForDepth = false
  DrillPoint = 1
  DrillPointAngle = 118
  HoleCutCountersinkAngle = 90
  HoleCutCustomValues = true
  HoleCutDepth = 3.55
  HoleCutDiameter = 1.3
  HoleCutType = 6
  ModelThread = false
  Profile = -> Sketch210
  Refine = true
  Suppressed = false
  Tapered = false
  TaperedAngle = 90
  ThreadClass = 0
  ThreadDepth = 25
  ThreadDepthType = 0
  ThreadDirection = 0
  ThreadFit = 0
  ThreadSize = 0
  ThreadType = 1
  Threaded = false
  UseCustomThreadClearance = false
FEATURE [PartDesign::Body] Body002  label="15180"
  AllowCompound = false
  Group = -> [Sketch154,Pad074,LinearPattern,Sketch210,Hole038]
  Origin = -> Origin006
  Placement = pos=(185,176.9,12.6) rot=(-0.71,-0.71,0;3.14159rad)
  Tip = -> Hole038
FEATURE [Sketcher::SketchObject] Sketch211
  ArcFitTolerance = 1e-06
  AttachmentSupport = -> [Origin1405]
  FullyConstrained = true
  MakeInternals = false
  MapMode = 5
  Placement = pos=(0,0,0) rot=(1,0,0;1.5708rad)
  sketch-geometry (5):
    g0: LineSegment StartX=0 StartY=0 StartZ=0 EndX=0 EndY=20 EndZ=0
    g1: LineSegment StartX=0 StartY=20 StartZ=0 EndX=4 EndY=20 EndZ=0
    g2: LineSegment StartX=4 StartY=20 StartZ=0 EndX=20 EndY=4 EndZ=0
    g3: LineSegment StartX=20 StartY=4 StartZ=0 EndX=20 EndY=0 EndZ=0
    g4: LineSegment StartX=20 StartY=0 StartZ=0 EndX=0 EndY=0 EndZ=0
  constraints (14):
    c: Coincident(g-1,g0)
    c: PointOnObject(g0,g-2)
    c: Coincident(g0,g1)
    c: Horizontal(g1)
    c: Coincident(g1,g2)
    c: Coincident(g2,g3)
    c: Vertical(g3)
    c: Coincident(g3,g4)
    c: Coincident(g4,g0)
    c: Horizontal(g4)
    c: Equal(g3,g1)
    c: Equal(g0,g4)
    c: DistanceY(g0,g0) = 20
    c: DistanceX(g1,g1) = 4
FEATURE [PartDesign::Pad] Pad102
  Direction = (0,-1,2e-16)
  Length = 20
  Length2 = 10
  Profile = -> Sketch211
  ReferenceAxis = -> Sketch211 [N_Axis]
  Refine = true
  Suppressed = false
  Type = 0
FEATURE [PartDesign::Thickness] Thickness001
  Base = -> Pad102 [Face2,Face3,Face4]
  BaseFeature = -> Pad102
  Intersection = false
  Join = 0
  Mode = 0
  Refine = true
  Reversed = true
  SupportTransform = false
  Suppressed = false
  Value = 3
FEATURE [Sketcher::SketchObject] Sketch212
  ArcFitTolerance = 1e-06
  AttachmentSupport = -> [Thickness001]
  ExternalGeometry = -> [Thickness001]
  FullyConstrained = true
  MakeInternals = false
  MapMode = 5
  Placement = pos=(3,0,0) rot=(0.57735,0.57735,0.57735;2.0944rad)
  sketch-geometry (7):
    g0: ArcOfCircle CenterX=-10 CenterY=13 CenterZ=0 NormalX=0 NormalY=0 NormalZ=1 AngleXU=0 Radius=3 StartAngle=3e-16 EndAngle=3.14159
    g1: ArcOfCircle CenterX=-10 CenterY=10 CenterZ=0 NormalX=0 NormalY=0 NormalZ=1 AngleXU=0 Radius=3 StartAngle=3.14159 EndAngle=6.28319
    g2: LineSegment StartX=-7 StartY=13 StartZ=0 EndX=-7 EndY=10 EndZ=0
    g3: LineSegment StartX=-13 StartY=13 StartZ=0 EndX=-13 EndY=10 EndZ=0
    g4: GeomPoint X=-10 Y=20 Z=0
    g5: GeomPoint X=-3 Y=11.5 Z=0
    g6: GeomPoint X=-7 Y=11.5 Z=0
  constraints (13):
    c: Tangent(g0,g2) = 1.5708
    c: Tangent(g0,g3) = -1.5708
    c: Tangent(g1,g2) = 1.5708
    c: Tangent(g1,g3) = -1.5708
    c: Equal(g0,g1)
    c: Vertical(g2)
    c: Symmetric(g-3,g-3,g4)
    c: Vertical(g0,g4)
    c: Distance(g2,g3) = 6
    c: DistanceY(g1,g0) = 3
    c: Symmetric(g-4,g-4,g5)
    c: Symmetric(g2,g2,g6)
    c: Horizontal(g6,g5)
FEATURE [PartDesign::Pocket] Pocket077
  BaseFeature = -> Thickness001
  Direction = (-1,0,0)
  Length = 5
  Length2 = 5
  Profile = -> Sketch212
  ReferenceAxis = -> Sketch212 [N_Axis]
  Refine = true
  Suppressed = false
  Type = 0
FEATURE [Sketcher::SketchObject] Sketch213
  ArcFitTolerance = 1e-06
  AttachmentSupport = -> [Pocket077]
  ExternalGeometry = -> [Pocket077]
  FullyConstrained = true
  MakeInternals = false
  MapMode = 5
  Placement = pos=(0,7e-16,3) rot=(0,0,1;0rad)
  sketch-geometry (7):
    g0: ArcOfCircle CenterX=10 CenterY=-10 CenterZ=0 NormalX=0 NormalY=0 NormalZ=1 AngleXU=0 Radius=3 StartAngle=1.5708 EndAngle=4.71239
    g1: ArcOfCircle CenterX=13 CenterY=-10 CenterZ=0 NormalX=0 NormalY=0 NormalZ=1 AngleXU=0 Radius=3 StartAngle=4.71239 EndAngle=7.85398
    g2: LineSegment StartX=10 StartY=-7 StartZ=0 EndX=13 EndY=-7 EndZ=0
    g3: LineSegment StartX=10 StartY=-13 StartZ=0 EndX=13 EndY=-13 EndZ=0
    g4: GeomPoint X=11.5 Y=-13 Z=0
    g5: GeomPoint X=20 Y=-10 Z=0
    g6: GeomPoint X=11.5 Y=-17 Z=0
  constraints (13):
    c: Tangent(g0,g2) = 1.5708
    c: Tangent(g0,g3) = -1.5708
    c: Tangent(g1,g2) = 1.5708
    c: Tangent(g1,g3) = -1.5708
    c: Equal(g0,g1)
    c: Horizontal(g2)
    c: DistanceX(g2,g2) = 3
    c: Radius(g1) = 3
    c: Symmetric(g3,g3,g4)
    c: Symmetric(g-3,g-3,g5)
    c: Horizontal(g5,g1)
    c: Symmetric(g-4,g-4,g6)
    c: Vertical(g6,g4)
FEATURE [PartDesign::Pocket] Pocket078
  BaseFeature = -> Pocket077
  Direction = (0,0,-1)
  Length = 5
  Length2 = 5
  Profile = -> Sketch213
  ReferenceAxis = -> Sketch213 [N_Axis]
  Refine = true
  Suppressed = false
  Type = 0
FEATURE [PartDesign::Body] Body123  label="2020 corner bracket"
  AllowCompound = false
  Group = -> [Sketch211,Pad102,Thickness001,Sketch212,Pocket077,Sketch213,Pocket078]
  Origin = -> Origin1405
  Tip = -> Pocket078
FEATURE [PartDesign::FeatureBase] Clone062
  BaseFeature = -> Body123
  Suppressed = false
FEATURE [PartDesign::Body] Body124  label="2020 corner"
  AllowCompound = false
  Group = -> [Clone062]
  Origin = -> Origin1407
  Placement = pos=(230,230,-33) rot=(0,0,1;4.71239rad)
  Tip = -> Clone062
FEATURE [PartDesign::FeatureBase] Clone063
  BaseFeature = -> Body123
  Suppressed = false
FEATURE [PartDesign::Body] Body125  label="2020 corner001"
  AllowCompound = false
  Group = -> [Clone063]
  Origin = -> Origin1409
  Placement = pos=(-140,230,-33) rot=(0,0,1;4.71239rad)
  Tip = -> Clone063
FEATURE [PartDesign::FeatureBase] Clone064
  BaseFeature = -> Body123
  Suppressed = false
FEATURE [PartDesign::Body] Body126  label="2020 corner002"
  AllowCompound = false
  Group = -> [Clone064]
  Origin = -> Origin1411
  Placement = pos=(210,270,-33) rot=(0,0,1;1.5708rad)
  Tip = -> Clone064
FEATURE [PartDesign::FeatureBase] Clone065
  BaseFeature = -> Body123
  Suppressed = false
FEATURE [PartDesign::Body] Body127  label="2020 corner003"
  AllowCompound = false
  Group = -> [Clone065]
  Origin = -> Origin1413
  Placement = pos=(-160,270,-33) rot=(0,0,1;1.5708rad)
  Tip = -> Clone065
FEATURE [Sketcher::SketchObject] Sketch214
  ArcFitTolerance = 1e-06
  AttachmentSupport = -> [Hole029]
  ExternalGeometry = -> [Hole029]
  FullyConstrained = true
  MakeInternals = false
  MapMode = 5
  Placement = pos=(0,2.3e-15,10) rot=(0,0,1;0rad)
  sketch-geometry (23):
    g0: LineSegment [constr] StartX=20 StartY=-62.5 StartZ=0 EndX=40 EndY=-62.5 EndZ=0
    g1: LineSegment [constr] StartX=40 StartY=-62.5 StartZ=0 EndX=40 EndY=-37.5 EndZ=0
    g2: LineSegment [constr] StartX=40 StartY=-37.5 StartZ=0 EndX=20 EndY=-37.5 EndZ=0
    g3: LineSegment [constr] StartX=20 StartY=-37.5 StartZ=0 EndX=20 EndY=-62.5 EndZ=0
    g4: GeomPoint [constr] X=30 Y=-50 Z=0
    g5: LineSegment [constr] StartX=20 StartY=-122.5 StartZ=0 EndX=40 EndY=-122.5 EndZ=0
    g6: LineSegment [constr] StartX=40 StartY=-122.5 StartZ=0 EndX=40 EndY=-97.5 EndZ=0
    g7: LineSegment [constr] StartX=40 StartY=-97.5 StartZ=0 EndX=20 EndY=-97.5 EndZ=0
    g8: LineSegment [constr] StartX=20 StartY=-97.5 StartZ=0 EndX=20 EndY=-122.5 EndZ=0
    g9: GeomPoint [constr] X=30 Y=-110 Z=0
    g10: GeomPoint [constr] X=36.9 Y=-75 Z=0
    g11: GeomPoint [constr] X=36.9 Y=-80 Z=0
    g12: GeomPoint [constr] X=30 Y=-80 Z=0
    g13: GeomPoint [constr] X=23.1 Y=-75 Z=0
    g14: GeomPoint [constr] X=30 Y=-75 Z=0
    g15: GeomPoint X=20 Y=-37.5 Z=0
    g16: GeomPoint X=40 Y=-37.5 Z=0
    g17: GeomPoint X=40 Y=-62.5 Z=0
    g18: GeomPoint X=20 Y=-62.5 Z=0
    g19: GeomPoint X=20 Y=-97.5 Z=0
    g20: GeomPoint X=20 Y=-122.5 Z=0
    g21: GeomPoint X=40 Y=-122.5 Z=0
    g22: GeomPoint X=40 Y=-97.5 Z=0
  constraints (39):
    c: Coincident(g0,g1)
    c: Coincident(g1,g2)
    c: Coincident(g2,g3)
    c: Coincident(g3,g0)
    c: Horizontal(g0)
    c: Horizontal(g2)
    c: Vertical(g1)
    c: Vertical(g3)
    c: Symmetric(g2,g0,g4)
    c: Distance(g1,g3) = 20
    c: Distance(g0,g2) = 25
    c: Coincident(g5,g6)
    c: Coincident(g6,g7)
    c: Coincident(g7,g8)
    c: Coincident(g8,g5)
    c: Horizontal(g5)
    c: Horizontal(g7)
    c: Vertical(g6)
    c: Vertical(g8)
    c: Symmetric(g7,g5,g9)
    c: Distance(g6,g8) = 20
    c: Distance(g5,g7) = 25
    c: DistanceY(g9,g4) = 60
    c: Symmetric(g-14,g-14,g10)
    c: Symmetric(g-6,g-10,g11)
    c: Symmetric(g4,g9,g12)
    c: Horizontal(g11,g12)
    c: Vertical(g12,g4)
    c: Symmetric(g-12,g-12,g13)
    c: Symmetric(g13,g10,g14)
    c: Vertical(g12,g14)
    c: Coincident(g15,g2)
    c: Coincident(g16,g1)
    c: Coincident(g17,g0)
    c: Coincident(g18,g0)
    c: Coincident(g19,g7)
    c: Coincident(g20,g5)
    c: Coincident(g21,g5)
    c: Coincident(g22,g6)
FEATURE [PartDesign::Hole] Hole039
  BaseFeature = -> Hole029
  CustomThreadClearance = 0
  Depth = 25
  DepthType = 0
  Diameter = 1.2
  DrillForDepth = false
  DrillPoint = 1
  DrillPointAngle = 118
  HoleCutCountersinkAngle = 90
  HoleCutCustomValues = true
  HoleCutDepth = 0.1
  HoleCutDiameter = 1.3
  HoleCutType = 4
  ModelThread = false
  Profile = -> Sketch214
  Refine = true
  Suppressed = false
  Tapered = false
  TaperedAngle = 90
  ThreadClass = 0
  ThreadDepth = 25
  ThreadDepthType = 0
  ThreadDirection = 0
  ThreadFit = 0
  ThreadSize = 0
  ThreadType = 1
  Threaded = false
  UseCustomThreadClearance = false
FEATURE [PartDesign::Body] Body094  label="Linear RailSupport"
  AllowCompound = false
  Group = -> [Clone040,Pad087,LinearPattern008,Sketch186,Pocket067,Sketch187,Hole029,Sketch214,Hole039]
  Origin = -> Origin1280
  Placement = pos=(-101,224.5,257) rot=(1,0,0;1.5708rad)
  Tip = -> Hole039
FEATURE [Part::FeaturePython] Screw  label="M3x16-Screw"  # WARN: FeaturePython — macro-defined, semantics opaque (R4)
  Diameter = 4
  Invert = false
  LeftHanded = false
  Length = 6
  LengthCustom = 16
  MatchOuter = false
  OffsetAngle = 0
  Thread = false
  Type = 75
FEATURE [Part::FeaturePython] Screw001  label="M3x16-Screw016"  # WARN: FeaturePython — macro-defined, semantics opaque (R4)
  Diameter = 4
  Invert = false
  LeftHanded = false
  Length = 6
  LengthCustom = 16
  MatchOuter = false
  OffsetAngle = 0
  Placement = pos=(20,0,0) rot=(0,0,1;0rad)
  Thread = false
  Type = 75
FEATURE [Part::FeaturePython] Screw002  label="M3x16-Screw017"  # WARN: FeaturePython — macro-defined, semantics opaque (R4)
  Diameter = 4
  Invert = false
  LeftHanded = false
  Length = 6
  LengthCustom = 16
  MatchOuter = false
  OffsetAngle = 0
  Placement = pos=(0,-25,0) rot=(0,0,1;0rad)
  Thread = false
  Type = 75
FEATURE [Part::FeaturePython] Screw003  label="M3x16-Screw018"  # WARN: FeaturePython — macro-defined, semantics opaque (R4)
  Diameter = 4
  Invert = false
  LeftHanded = false
  Length = 6
  LengthCustom = 16
  MatchOuter = false
  OffsetAngle = 0
  Placement = pos=(0,-60,0) rot=(0,0,1;0rad)
  Thread = false
  Type = 75
FEATURE [Part::FeaturePython] Screw004  label="M3x16-Screw019"  # WARN: FeaturePython — macro-defined, semantics opaque (R4)
  Diameter = 4
  Invert = false
  LeftHanded = false
  Length = 6
  LengthCustom = 16
  MatchOuter = false
  OffsetAngle = 0
  Placement = pos=(0,-85,0) rot=(0,0,1;0rad)
  Thread = false
  Type = 75
FEATURE [Part::FeaturePython] Screw005  label="M3x16-Screw020"  # WARN: FeaturePython — macro-defined, semantics opaque (R4)
  Diameter = 4
  Invert = false
  LeftHanded = false
  Length = 6
  LengthCustom = 16
  MatchOuter = false
  OffsetAngle = 0
  Placement = pos=(20,-25,0) rot=(0,0,1;0rad)
  Thread = false
  Type = 75
FEATURE [Part::FeaturePython] Screw006  label="M3x16-Screw021"  # WARN: FeaturePython — macro-defined, semantics opaque (R4)
  Diameter = 4
  Invert = false
  LeftHanded = false
  Length = 6
  LengthCustom = 16
  MatchOuter = false
  OffsetAngle = 0
  Placement = pos=(20,-60,0) rot=(0,0,1;0rad)
  Thread = false
  Type = 75
FEATURE [Part::FeaturePython] Screw007  label="M3x16-Screw022"  # WARN: FeaturePython — macro-defined, semantics opaque (R4)
  Diameter = 4
  Invert = false
  LeftHanded = false
  Length = 6
  LengthCustom = 16
  MatchOuter = false
  OffsetAngle = 0
  Placement = pos=(20,-85,0) rot=(0,0,1;0rad)
  Thread = false
  Type = 75
FEATURE [Part::FeaturePython] Screw008  label="M3x10-Screw"  # WARN: FeaturePython — macro-defined, semantics opaque (R4)
  Diameter = 4
  Invert = false
  LeftHanded = false
  Length = 3
  LengthCustom = 10
  MatchOuter = false
  OffsetAngle = 0
  Thread = false
  Type = 75
FEATURE [Part::FeaturePython] Screw009  label="M3x10-Screw118"  # WARN: FeaturePython — macro-defined, semantics opaque (R4)
  Diameter = 4
  Invert = false
  LeftHanded = false
  Length = 3
  LengthCustom = 10
  MatchOuter = false
  OffsetAngle = 0
  Placement = pos=(-40,0,0) rot=(0,0,1;0rad)
  Thread = false
  Type = 75
FEATURE [Part::FeaturePython] Screw010  label="M3x10-Screw119"  # WARN: FeaturePython — macro-defined, semantics opaque (R4)
  Diameter = 4
  Invert = false
  LeftHanded = false
  Length = 3
  LengthCustom = 10
  MatchOuter = false
  OffsetAngle = 0
  Placement = pos=(-80,0,0) rot=(0,0,1;0rad)
  Thread = false
  Type = 75
FEATURE [Part::FeaturePython] Screw011  label="M3x10-Screw120"  # WARN: FeaturePython — macro-defined, semantics opaque (R4)
  Diameter = 4
  Invert = false
  LeftHanded = false
  Length = 3
  LengthCustom = 10
  MatchOuter = false
  OffsetAngle = 0
  Placement = pos=(-120,0,0) rot=(0,0,1;0rad)
  Thread = false
  Type = 75
FEATURE [Part::FeaturePython] Screw012  label="M3x10-Screw121"  # WARN: FeaturePython — macro-defined, semantics opaque (R4)
  Diameter = 4
  Invert = false
  LeftHanded = false
  Length = 3
  LengthCustom = 10
  MatchOuter = false
  OffsetAngle = 0
  Placement = pos=(-160,0,0) rot=(0,0,1;0rad)
  Thread = false
  Type = 75
FEATURE [Part::FeaturePython] Screw013  label="M3x10-Screw122"  # WARN: FeaturePython — macro-defined, semantics opaque (R4)
  Diameter = 4
  Invert = false
  LeftHanded = false
  Length = 3
  LengthCustom = 10
  MatchOuter = false
  OffsetAngle = 0
  Placement = pos=(-200,0,0) rot=(0,0,1;0rad)
  Thread = false
  Type = 75
FEATURE [Part::FeaturePython] Screw014  label="M3x10-Screw123"  # WARN: FeaturePython — macro-defined, semantics opaque (R4)
  Diameter = 4
  Invert = false
  LeftHanded = false
  Length = 3
  LengthCustom = 10
  MatchOuter = false
  OffsetAngle = 0
  Placement = pos=(-240,0,0) rot=(0,0,1;0rad)
  Thread = false
  Type = 75
FEATURE [Part::FeaturePython] Screw015  label="M3x10-Screw124"  # WARN: FeaturePython — macro-defined, semantics opaque (R4)
  Diameter = 4
  Invert = false
  LeftHanded = false
  Length = 3
  LengthCustom = 10
  MatchOuter = false
  OffsetAngle = 0
  Placement = pos=(-280,0,0) rot=(0,0,1;0rad)
  Thread = false
  Type = 75
FEATURE [Part::FeaturePython] Screw016  label="M3x10-Screw125"  # WARN: FeaturePython — macro-defined, semantics opaque (R4)
  Diameter = 4
  Invert = false
  LeftHanded = false
  Length = 3
  LengthCustom = 10
  MatchOuter = false
  OffsetAngle = 0
  Placement = pos=(-320,0,0) rot=(0,0,1;0rad)
  Thread = false
  Type = 75
FEATURE [Part::FeaturePython] Screw017  label="M3x10-Screw126"  # WARN: FeaturePython — macro-defined, semantics opaque (R4)
  Diameter = 4
  Invert = false
  LeftHanded = false
  Length = 3
  LengthCustom = 10
  MatchOuter = false
  OffsetAngle = 0
  Placement = pos=(0,170,0) rot=(0,0,1;0rad)
  Thread = false
  Type = 75
FEATURE [Part::FeaturePython] Screw018  label="M3x10-Screw127"  # WARN: FeaturePython — macro-defined, semantics opaque (R4)
  Diameter = 4
  Invert = false
  LeftHanded = false
  Length = 3
  LengthCustom = 10
  MatchOuter = false
  OffsetAngle = 0
  Placement = pos=(-40,170,0) rot=(0,0,1;0rad)
  Thread = false
  Type = 75
FEATURE [Part::FeaturePython] Screw019  label="M3x10-Screw128"  # WARN: FeaturePython — macro-defined, semantics opaque (R4)
  Diameter = 4
  Invert = false
  LeftHanded = false
  Length = 3
  LengthCustom = 10
  MatchOuter = false
  OffsetAngle = 0
  Placement = pos=(-80,170,0) rot=(0,0,1;0rad)
  Thread = false
  Type = 75
FEATURE [Part::FeaturePython] Screw020  label="M3x10-Screw129"  # WARN: FeaturePython — macro-defined, semantics opaque (R4)
  Diameter = 4
  Invert = false
  LeftHanded = false
  Length = 3
  LengthCustom = 10
  MatchOuter = false
  OffsetAngle = 0
  Placement = pos=(-120,170,0) rot=(0,0,1;0rad)
  Thread = false
  Type = 75
FEATURE [Part::FeaturePython] Screw021  label="M3x10-Screw130"  # WARN: FeaturePython — macro-defined, semantics opaque (R4)
  Diameter = 4
  Invert = false
  LeftHanded = false
  Length = 3
  LengthCustom = 10
  MatchOuter = false
  OffsetAngle = 0
  Placement = pos=(-160,170,0) rot=(0,0,1;0rad)
  Thread = false
  Type = 75
FEATURE [Part::FeaturePython] Screw022  label="M3x10-Screw131"  # WARN: FeaturePython — macro-defined, semantics opaque (R4)
  Diameter = 4
  Invert = false
  LeftHanded = false
  Length = 3
  LengthCustom = 10
  MatchOuter = false
  OffsetAngle = 0
  Placement = pos=(-200,170,0) rot=(0,0,1;0rad)
  Thread = false
  Type = 75
FEATURE [Part::FeaturePython] Screw023  label="M3x10-Screw132"  # WARN: FeaturePython — macro-defined, semantics opaque (R4)
  Diameter = 4
  Invert = false
  LeftHanded = false
  Length = 3
  LengthCustom = 10
  MatchOuter = false
  OffsetAngle = 0
  Placement = pos=(-240,170,0) rot=(0,0,1;0rad)
  Thread = false
  Type = 75
FEATURE [Part::FeaturePython] Screw024  label="M3x10-Screw133"  # WARN: FeaturePython — macro-defined, semantics opaque (R4)
  Diameter = 4
  Invert = false
  LeftHanded = false
  Length = 3
  LengthCustom = 10
  MatchOuter = false
  OffsetAngle = 0
  Placement = pos=(-280,170,0) rot=(0,0,1;0rad)
  Thread = false
  Type = 75
FEATURE [Part::FeaturePython] Screw025  label="M3x10-Screw134"  # WARN: FeaturePython — macro-defined, semantics opaque (R4)
  Diameter = 4
  Invert = false
  LeftHanded = false
  Length = 3
  LengthCustom = 10
  MatchOuter = false
  OffsetAngle = 0
  Placement = pos=(-320,170,0) rot=(0,0,1;0rad)
  Thread = false
  Type = 75
FEATURE [Part::FeaturePython] Screw026  label="M3x10-Screw100"  # WARN: FeaturePython — macro-defined, semantics opaque (R4)
  Diameter = 4
  Invert = false
  LeftHanded = false
  Length = 3
  LengthCustom = 10
  MatchOuter = false
  OffsetAngle = 0
  Thread = false
  Type = 75
FEATURE [Part::FeaturePython] Screw027  label="M3x10-Screw135"  # WARN: FeaturePython — macro-defined, semantics opaque (R4)
  Diameter = 4
  Invert = false
  LeftHanded = false
  Length = 3
  LengthCustom = 10
  MatchOuter = false
  OffsetAngle = 0
  Placement = pos=(40,0,0) rot=(0,0,1;0rad)
  Thread = false
  Type = 75
FEATURE [Part::FeaturePython] Screw028  label="M3x10-Screw136"  # WARN: FeaturePython — macro-defined, semantics opaque (R4)
  Diameter = 4
  Invert = false
  LeftHanded = false
  Length = 3
  LengthCustom = 10
  MatchOuter = false
  OffsetAngle = 0
  Placement = pos=(80,0,0) rot=(0,0,1;0rad)
  Thread = false
  Type = 75
FEATURE [Part::FeaturePython] Screw029  label="M3x10-Screw137"  # WARN: FeaturePython — macro-defined, semantics opaque (R4)
  Diameter = 4
  Invert = false
  LeftHanded = false
  Length = 3
  LengthCustom = 10
  MatchOuter = false
  OffsetAngle = 0
  Placement = pos=(120,0,0) rot=(0,0,1;0rad)
  Thread = false
  Type = 75
FEATURE [Part::FeaturePython] Screw030  label="M3x10-Screw138"  # WARN: FeaturePython — macro-defined, semantics opaque (R4)
  Diameter = 4
  Invert = false
  LeftHanded = false
  Length = 3
  LengthCustom = 10
  MatchOuter = false
  OffsetAngle = 0
  Placement = pos=(160,0,0) rot=(0,0,1;0rad)
  Thread = false
  Type = 75
FEATURE [Part::FeaturePython] Screw031  label="M3x10-Screw139"  # WARN: FeaturePython — macro-defined, semantics opaque (R4)
  Diameter = 4
  Invert = false
  LeftHanded = false
  Length = 3
  LengthCustom = 10
  MatchOuter = false
  OffsetAngle = 0
  Placement = pos=(200,0,0) rot=(0,0,1;0rad)
  Thread = false
  Type = 75
FEATURE [Part::FeaturePython] Screw032  label="M3x10-Screw140"  # WARN: FeaturePython — macro-defined, semantics opaque (R4)
  Diameter = 4
  Invert = false
  LeftHanded = false
  Length = 3
  LengthCustom = 10
  MatchOuter = false
  OffsetAngle = 0
  Placement = pos=(240,0,0) rot=(0,0,1;0rad)
  Thread = false
  Type = 75
FEATURE [Part::FeaturePython] Screw033  label="M3x10-Screw141"  # WARN: FeaturePython — macro-defined, semantics opaque (R4)
  Diameter = 4
  Invert = false
  LeftHanded = false
  Length = 3
  LengthCustom = 10
  MatchOuter = false
  OffsetAngle = 0
  Placement = pos=(280,0,0) rot=(0,0,1;0rad)
  Thread = false
  Type = 75
FEATURE [Part::FeaturePython] Screw034  label="M3x10-Screw142"  # WARN: FeaturePython — macro-defined, semantics opaque (R4)
  Diameter = 4
  Invert = false
  LeftHanded = false
  Length = 3
  LengthCustom = 10
  MatchOuter = false
  OffsetAngle = 0
  Placement = pos=(320,0,0) rot=(0,0,1;0rad)
  Thread = false
  Type = 75
FEATURE [Part::FeaturePython] Screw035  label="M3x10-Screw143"  # WARN: FeaturePython — macro-defined, semantics opaque (R4)
  Diameter = 4
  Invert = false
  LeftHanded = false
  Length = 3
  LengthCustom = 10
  MatchOuter = false
  OffsetAngle = 0
  Placement = pos=(0,-60,0) rot=(0,0,1;0rad)
  Thread = false
  Type = 75
FEATURE [Part::FeaturePython] Screw036  label="M3x10-Screw144"  # WARN: FeaturePython — macro-defined, semantics opaque (R4)
  Diameter = 4
  Invert = false
  LeftHanded = false
  Length = 3
  LengthCustom = 10
  MatchOuter = false
  OffsetAngle = 0
  Placement = pos=(40,-60,0) rot=(0,0,1;0rad)
  Thread = false
  Type = 75
FEATURE [Part::FeaturePython] Screw037  label="M3x10-Screw145"  # WARN: FeaturePython — macro-defined, semantics opaque (R4)
  Diameter = 4
  Invert = false
  LeftHanded = false
  Length = 3
  LengthCustom = 10
  MatchOuter = false
  OffsetAngle = 0
  Placement = pos=(80,-60,0) rot=(0,0,1;0rad)
  Thread = false
  Type = 75
FEATURE [Part::FeaturePython] Screw038  label="M3x10-Screw146"  # WARN: FeaturePython — macro-defined, semantics opaque (R4)
  Diameter = 4
  Invert = false
  LeftHanded = false
  Length = 3
  LengthCustom = 10
  MatchOuter = false
  OffsetAngle = 0
  Placement = pos=(120,-60,0) rot=(0,0,1;0rad)
  Thread = false
  Type = 75
FEATURE [Part::FeaturePython] Screw039  label="M3x10-Screw147"  # WARN: FeaturePython — macro-defined, semantics opaque (R4)
  Diameter = 4
  Invert = false
  LeftHanded = false
  Length = 3
  LengthCustom = 10
  MatchOuter = false
  OffsetAngle = 0
  Placement = pos=(160,-60,0) rot=(0,0,1;0rad)
  Thread = false
  Type = 75
FEATURE [Part::FeaturePython] Screw040  label="M3x10-Screw148"  # WARN: FeaturePython — macro-defined, semantics opaque (R4)
  Diameter = 4
  Invert = false
  LeftHanded = false
  Length = 3
  LengthCustom = 10
  MatchOuter = false
  OffsetAngle = 0
  Placement = pos=(200,-60,0) rot=(0,0,1;0rad)
  Thread = false
  Type = 75
FEATURE [Part::FeaturePython] Screw041  label="M3x10-Screw149"  # WARN: FeaturePython — macro-defined, semantics opaque (R4)
  Diameter = 4
  Invert = false
  LeftHanded = false
  Length = 3
  LengthCustom = 10
  MatchOuter = false
  OffsetAngle = 0
  Placement = pos=(240,-60,0) rot=(0,0,1;0rad)
  Thread = false
  Type = 75
FEATURE [Part::FeaturePython] Screw042  label="M3x10-Screw150"  # WARN: FeaturePython — macro-defined, semantics opaque (R4)
  Diameter = 4
  Invert = false
  LeftHanded = false
  Length = 3
  LengthCustom = 10
  MatchOuter = false
  OffsetAngle = 0
  Placement = pos=(280,-60,0) rot=(0,0,1;0rad)
  Thread = false
  Type = 75
FEATURE [Part::FeaturePython] Screw043  label="M3x10-Screw151"  # WARN: FeaturePython — macro-defined, semantics opaque (R4)
  Diameter = 4
  Invert = false
  LeftHanded = false
  Length = 3
  LengthCustom = 10
  MatchOuter = false
  OffsetAngle = 0
  Placement = pos=(320,-60,0) rot=(0,0,1;0rad)
  Thread = false
  Type = 75
FEATURE [PartDesign::ShapeBinder] CopyHole020
  Placement = pos=(0,-40,8.9e-15) rot=(0,0,1;0rad)
  TraceSupport = false
FEATURE [Sketcher::SketchObject] Sketch215
  ArcFitTolerance = 1e-06
  AttachmentSupport = -> [CopyHole020]
  ExternalGeometry = -> [CopyHole020]
  FullyConstrained = true
  MakeInternals = false
  MapMode = 5
  Placement = pos=(0,-40,8.9e-15) rot=(1,0,0;1.5708rad)
  sketch-geometry (9):
    g0: LineSegment StartX=-7.5 StartY=-1 StartZ=0 EndX=-16 EndY=-1 EndZ=0
    g1: LineSegment StartX=-16 StartY=-1 StartZ=0 EndX=-16 EndY=11 EndZ=0
    g2: LineSegment StartX=-16 StartY=11 StartZ=0 EndX=16 EndY=11 EndZ=0
    g3: LineSegment StartX=16 StartY=11 StartZ=0 EndX=16 EndY=-1 EndZ=0
    g4: LineSegment StartX=16 StartY=-1 StartZ=0 EndX=7.5 EndY=-1 EndZ=0
    g5: LineSegment StartX=7.5 StartY=-1 StartZ=0 EndX=7.5 EndY=5 EndZ=0
    g6: LineSegment StartX=7.5 StartY=5 StartZ=0 EndX=-7.5 EndY=5 EndZ=0
    g7: LineSegment StartX=-7.5 StartY=5 StartZ=0 EndX=-7.5 EndY=-1 EndZ=0
    g8: GeomPoint X=-16 Y=-5 Z=0
  constraints (25):
    c: PointOnObject(g0,g-6)
    c: Horizontal(g0)
    c: Coincident(g0,g1)
    c: Vertical(g1)
    c: Coincident(g1,g2)
    c: Horizontal(g2)
    c: Coincident(g2,g3)
    c: Vertical(g3)
    c: Coincident(g3,g4)
    c: PointOnObject(g4,g-4)
    c: Horizontal(g4)
    c: Coincident(g5,g-5)
    c: Coincident(g5,g6)
    c: Coincident(g6,g-6)
    c: Coincident(g6,g7)
    c: Coincident(g7,g0)
    c: DistanceY(g1,g1) = 12
    c: Horizontal(g0,g4)
    c: Horizontal(g4,g5)
    c: DistanceY(g8,g0) = 4
    c: Horizontal(g8,g-6)
    c: DistanceX(g2,g2) = 32
    c: Equal(g0,g4)
    c: Vertical(g8,g0)
    c: Vertical(g5)
FEATURE [PartDesign::Pad] Pad103
  Direction = (0,-1,0)
  Length = 42.1
  Length2 = 10
  Placement = pos=(0,-40,8.9e-15) rot=(0,0,1;0rad)
  Profile = -> Sketch215
  ReferenceAxis = -> Sketch215 [N_Axis]
  Refine = true
  Reversed = true
  Suppressed = false
  Type = 0
FEATURE [Sketcher::SketchObject] Sketch216
  ArcFitTolerance = 1e-06
  AttachmentSupport = -> [Pad103]
  ExternalGeometry = -> [Pad103]
  FullyConstrained = true
  MakeInternals = false
  MapMode = 5
  Placement = pos=(0,-40,11) rot=(0,0,1;0rad)
  sketch-geometry (5):
    g0: GeomPoint X=-12.5 Y=31.05 Z=0
    g1: GeomPoint X=12.5 Y=31.05 Z=0
    g2: GeomPoint X=12.5 Y=11.05 Z=0
    g3: GeomPoint X=-12.5 Y=11.05 Z=0
    g4: GeomPoint [constr] X=-2e-16 Y=21.05 Z=0
  constraints (8):
    c: Vertical(g0,g3)
    c: Vertical(g1,g2)
    c: Horizontal(g0,g1)
    c: Horizontal(g2,g3)
    c: DistanceY(g2,g1) = 20
    c: DistanceX(g3,g2) = 25
    c: Symmetric(g-6,g-5,g4)
    c: Symmetric(g0,g2,g4)
FEATURE [PartDesign::Hole] Hole040
  BaseFeature = -> Pad103
  CustomThreadClearance = 0
  Depth = 4
  DepthType = 0
  Diameter = 1.2
  DrillForDepth = false
  DrillPoint = 1
  DrillPointAngle = 118
  HoleCutCountersinkAngle = 90
  HoleCutCustomValues = false
  HoleCutDepth = 0
  HoleCutDiameter = 0
  HoleCutType = 0
  ModelThread = false
  Placement = pos=(0,-40,8.9e-15) rot=(0,0,1;0rad)
  Profile = -> Sketch216
  Refine = true
  Suppressed = false
  Tapered = false
  TaperedAngle = 90
  ThreadClass = 0
  ThreadDepth = 4
  ThreadDepthType = 0
  ThreadDirection = 0
  ThreadFit = 0
  ThreadSize = 0
  ThreadType = 1
  Threaded = false
  UseCustomThreadClearance = false
FEATURE [PartDesign::Body] Body128  label="MGN15C block"
  AllowCompound = false
  Group = -> [CopyHole020,Sketch215,Pad103,Sketch216,Hole040]
  Origin = -> Origin1417
  Tip = -> Hole040
FEATURE [PartDesign::FeatureBase] Clone066
  BaseFeature = -> Body128
  Suppressed = false
FEATURE [PartDesign::Body] Body129  label="MGN15C block001"
  AllowCompound = false
  Group = -> [Clone066]
  Origin = -> Origin1419
  Placement = pos=(-52,246,207) rot=(0.58,0.58,-0.58;2.0944rad)
  Tip = -> Clone066
FEATURE [PartDesign::FeatureBase] Clone067
  BaseFeature = -> Body128
  Suppressed = false
FEATURE [PartDesign::Body] Body130  label="MGN15C block002"
  AllowCompound = false
  Group = -> [Clone067]
  Origin = -> Origin1421
  Placement = pos=(-52,246,147) rot=(0.58,0.58,-0.58;2.0944rad)
  Tip = -> Clone067
FEATURE [App::Part] Part021  label="Screws001"
  Group = -> [Screw008,Screw009,Screw010,Screw011,Screw012,Screw013,Screw014,Screw015,Screw016,Screw017,Screw018,Screw019,Screw020,Screw021,Screw022,Screw023,Screw024,Screw025]
  Origin = -> Origin1423
  Placement = pos=(183,54.5,-4.5) rot=(0,0,1;0rad)
FEATURE [Part::FeaturePython] Screw044  label="M3x10-Screw176"  # WARN: FeaturePython — macro-defined, semantics opaque (R4)
  Diameter = 4
  Invert = false
  LeftHanded = false
  Length = 3
  LengthCustom = 10
  MatchOuter = false
  OffsetAngle = 0
  Placement = pos=(-20,27.5,12) rot=(0,0,1;0rad)
  Thread = false
  Type = 75
FEATURE [Part::FeaturePython] Screw045  label="M3x10-Screw184"  # WARN: FeaturePython — macro-defined, semantics opaque (R4)
  Diameter = 4
  Invert = false
  LeftHanded = false
  Length = 3
  LengthCustom = 10
  MatchOuter = false
  OffsetAngle = 0
  Placement = pos=(-20,-12.5,12) rot=(0,0,1;0rad)
  Thread = false
  Type = 75
FEATURE [Part::FeaturePython] Screw046  label="M3x10-Screw185"  # WARN: FeaturePython — macro-defined, semantics opaque (R4)
  Diameter = 4
  Invert = false
  LeftHanded = false
  Length = 3
  LengthCustom = 10
  MatchOuter = false
  OffsetAngle = 0
  Placement = pos=(-20,-52.5,12) rot=(0,0,1;0rad)
  Thread = false
  Type = 75
FEATURE [Part::FeaturePython] Screw047  label="M3x10-Screw186"  # WARN: FeaturePython — macro-defined, semantics opaque (R4)
  Diameter = 4
  Invert = false
  LeftHanded = false
  Length = 3
  LengthCustom = 10
  MatchOuter = false
  OffsetAngle = 0
  Placement = pos=(-20,-92.5,12) rot=(0,0,1;0rad)
  Thread = false
  Type = 75
FEATURE [Part::FeaturePython] Screw048  label="M3x10-Screw187"  # WARN: FeaturePython — macro-defined, semantics opaque (R4)
  Diameter = 4
  Invert = false
  LeftHanded = false
  Length = 3
  LengthCustom = 10
  MatchOuter = false
  OffsetAngle = 0
  Placement = pos=(40,27.5,12) rot=(0,0,1;0rad)
  Thread = false
  Type = 75
FEATURE [Part::FeaturePython] Screw049  label="M3x10-Screw188"  # WARN: FeaturePython — macro-defined, semantics opaque (R4)
  Diameter = 4
  Invert = false
  LeftHanded = false
  Length = 3
  LengthCustom = 10
  MatchOuter = false
  OffsetAngle = 0
  Placement = pos=(40,-12.5,12) rot=(0,0,1;0rad)
  Thread = false
  Type = 75
FEATURE [Part::FeaturePython] Screw050  label="M3x10-Screw189"  # WARN: FeaturePython — macro-defined, semantics opaque (R4)
  Diameter = 4
  Invert = false
  LeftHanded = false
  Length = 3
  LengthCustom = 10
  MatchOuter = false
  OffsetAngle = 0
  Placement = pos=(40,-52.5,12) rot=(0,0,1;0rad)
  Thread = false
  Type = 75
FEATURE [Part::FeaturePython] Screw051  label="M3x10-Screw190"  # WARN: FeaturePython — macro-defined, semantics opaque (R4)
  Diameter = 4
  Invert = false
  LeftHanded = false
  Length = 3
  LengthCustom = 10
  MatchOuter = false
  OffsetAngle = 0
  Placement = pos=(40,-92.5,12) rot=(0,0,1;0rad)
  Thread = false
  Type = 75
FEATURE [PartDesign::Hole] Hole041
  BaseFeature = -> Pad024
  CustomThreadClearance = 0
  Depth = 3
  DepthType = 0
  Diameter = 6
  DrillForDepth = false
  DrillPoint = 1
  DrillPointAngle = 118
  HoleCutCountersinkAngle = 90
  HoleCutCustomValues = false
  HoleCutDepth = 0
  HoleCutDiameter = 0
  HoleCutType = 0
  ModelThread = false
  Profile = -> Pad024 [Face24]
  Refine = true
  Suppressed = false
  Tapered = false
  TaperedAngle = 90
  ThreadClass = 0
  ThreadDepth = 3
  ThreadDepthType = 0
  ThreadDirection = 0
  ThreadFit = 0
  ThreadSize = 0
  ThreadType = 0
  Threaded = false
  UseCustomThreadClearance = false
FEATURE [PartDesign::Body] Body021  label="17HS4401"
  AllowCompound = false
  Group = -> [Sketch038,Pad021,Sketch039,Pocket007,PolarPattern007,Sketch040,Pad022,Pad023,Sketch041,Pocket008,Chamfer,Sketch042,Pad024,Hole041]
  Origin = -> Origin918
  Placement = pos=(54,44,1.2e-14) rot=(0,1,0;4.71239rad)
  Tip = -> Hole041
FEATURE [App::Part] Part  label="Storage"
  Group = -> [Body,Body001,Body004,Body005,Body006,Body011,Body058,Body055,Body061,Body021,Body073,Body072,Body082,Body087,Body088,Body114,Body123,Body128]
  Origin = -> Origin002
  Placement = pos=(0,0,73) rot=(0,0,1;0rad)
FEATURE [PartDesign::FeatureBase] Clone020
  BaseFeature = -> Body021
  Placement = pos=(54,44,1.2e-14) rot=(0,1,0;4.71239rad)
  Suppressed = false
FEATURE [PartDesign::Body] Body067  label="17HS4401002"
  AllowCompound = false
  Group = -> [Clone020]
  Origin = -> Origin1220
  Placement = pos=(-110,183.5,-23) rot=(0,0,1;3.14159rad)
  Tip = -> Clone020
FEATURE [App::Part] Part015  label="Motor"
  Group = -> [Body067,Body068,Body060]
  Origin = -> Origin1254
  Placement = pos=(-51,0,15) rot=(0,0,1;0rad)
FEATURE [App::Part] Part014  label="Linear"
  Group = -> [Body074,Body075,Part015,Part021]
  Origin = -> Origin1224
  Placement = pos=(-104.5,158,-2) rot=(0,0,1;4.71239rad)
FEATURE [PartDesign::ShapeBinder] ShapeBinder001
  Placement = pos=(54,44,1.2e-14) rot=(0,-1,0;1.5708rad)
  Support = -> [Clone020]
  TraceSupport = false
FEATURE [PartDesign::FeatureBase] Clone048
  BaseFeature = -> Body021
  Placement = pos=(54,44,1.2e-14) rot=(0,1,0;4.71239rad)
  Suppressed = false
FEATURE [PartDesign::Body] Body105  label="17HS4401003"
  AllowCompound = false
  Group = -> [Clone048]
  Origin = -> Origin1369
  Placement = pos=(-71,159.75,286) rot=(0,1,0;4.71239rad)
  Tip = -> Clone048
FEATURE [PartDesign::FeatureBase] Clone051
  BaseFeature = -> Body021
  Placement = pos=(54,44,1.2e-14) rot=(0,1,0;4.71239rad)
  Suppressed = false
FEATURE [PartDesign::Body] Body109  label="17HS4401004"
  AllowCompound = false
  Group = -> [Clone051]
  Origin = -> Origin1377
  Placement = pos=(-146,180.5,177) rot=(0,1,0;3.14159rad)
  Tip = -> Clone051
FEATURE [Part::FeaturePython] Screw052  label="M3x38-Screw"  # WARN: FeaturePython — macro-defined, semantics opaque (R4)
  Diameter = 4
  Invert = false
  LeftHanded = false
  Length = 10
  LengthCustom = 38
  MatchOuter = false
  OffsetAngle = 0
  Placement = pos=(-77,-14.5,4) rot=(0,1,0;-1.5708rad)
  Thread = false
  Type = 75
FEATURE [Part::FeaturePython] Screw053  label="M3x38-Screw008"  # WARN: FeaturePython — macro-defined, semantics opaque (R4)
  Diameter = 4
  Invert = false
  LeftHanded = false
  Length = 10
  LengthCustom = 38
  MatchOuter = false
  OffsetAngle = 0
  Placement = pos=(-77,-14.5,35) rot=(0,1,0;4.71239rad)
  Thread = false
  Type = 75
FEATURE [Part::FeaturePython] Screw054  label="M3x38-Screw009"  # WARN: FeaturePython — macro-defined, semantics opaque (R4)
  Diameter = 4
  Invert = false
  LeftHanded = false
  Length = 10
  LengthCustom = 38
  MatchOuter = false
  OffsetAngle = 0
  Placement = pos=(-77,-45.5,35) rot=(0,1,0;4.71239rad)
  Thread = false
  Type = 75
FEATURE [Part::FeaturePython] Screw055  label="M3x38-Screw010"  # WARN: FeaturePython — macro-defined, semantics opaque (R4)
  Diameter = 4
  Invert = false
  LeftHanded = false
  Length = 10
  LengthCustom = 38
  MatchOuter = false
  OffsetAngle = 0
  Placement = pos=(-77,-45.5,4) rot=(0,1,0;4.71239rad)
  Thread = false
  Type = 75
FEATURE [Part::FeaturePython] Screw056  label="M3x28-Screw"  # WARN: FeaturePython — macro-defined, semantics opaque (R4)
  Diameter = 4
  Invert = false
  LeftHanded = false
  Length = 10
  LengthCustom = 28
  MatchOuter = false
  OffsetAngle = 0
  Placement = pos=(-30,-47,37) rot=(0,0,1;0rad)
  Thread = false
  Type = 75
FEATURE [Part::FeaturePython] Screw057  label="M3x28-Screw001"  # WARN: FeaturePython — macro-defined, semantics opaque (R4)
  Diameter = 4
  Invert = false
  LeftHanded = false
  Length = 10
  LengthCustom = 28
  MatchOuter = false
  OffsetAngle = 0
  Placement = pos=(-30,-13,37) rot=(0,0,1;0rad)
  Thread = false
  Type = 75
FEATURE [Part::FeaturePython] Screw058  label="M3x12-Screw"  # WARN: FeaturePython — macro-defined, semantics opaque (R4)
  Diameter = 4
  Invert = false
  LeftHanded = false
  Length = 4
  LengthCustom = 12
  MatchOuter = false
  OffsetAngle = 0
  Placement = pos=(340,-38,23) rot=(0,0,1;0rad)
  Thread = false
  Type = 75
FEATURE [Part::FeaturePython] Screw059  label="M3x12-Screw001"  # WARN: FeaturePython — macro-defined, semantics opaque (R4)
  Diameter = 4
  Invert = false
  LeftHanded = false
  Length = 4
  LengthCustom = 12
  MatchOuter = false
  OffsetAngle = 0
  Placement = pos=(340,-22,23) rot=(0,0,1;0rad)
  Thread = false
  Type = 75
FEATURE [Part::FeaturePython] Screw060  label="M6x25-Screw"  # WARN: FeaturePython — macro-defined, semantics opaque (R4)
  Diameter = 7
  Invert = false
  LeftHanded = false
  Length = 6
  LengthCustom = 25
  MatchOuter = false
  OffsetAngle = 0
  Placement = pos=(-34,-40,-16) rot=(0,1,0;4.71239rad)
  Thread = false
  Type = 75
FEATURE [Part::FeaturePython] Screw061  label="M6x25-Screw022"  # WARN: FeaturePython — macro-defined, semantics opaque (R4)
  Diameter = 7
  Invert = false
  LeftHanded = false
  Length = 6
  LengthCustom = 25
  MatchOuter = false
  OffsetAngle = 0
  Placement = pos=(-34,-60,-16) rot=(0,1,0;4.71239rad)
  Thread = false
  Type = 75
FEATURE [Part::FeaturePython] Screw062  label="M6x25-Screw032"  # WARN: FeaturePython — macro-defined, semantics opaque (R4)
  Diameter = 7
  Invert = false
  LeftHanded = false
  Length = 6
  LengthCustom = 25
  MatchOuter = false
  OffsetAngle = 0
  Placement = pos=(344,0,-16) rot=(0,-1,0;4.71239rad)
  Thread = false
  Type = 75
FEATURE [Part::FeaturePython] Screw063  label="M6x25-Screw030"  # WARN: FeaturePython — macro-defined, semantics opaque (R4)
  Diameter = 7
  Invert = false
  LeftHanded = false
  Length = 6
  LengthCustom = 25
  MatchOuter = false
  OffsetAngle = 0
  Placement = pos=(344,-40,-16) rot=(0,-1,0;4.71239rad)
  Thread = false
  Type = 75
FEATURE [Part::FeaturePython] Screw064  label="M6x25-Screw029"  # WARN: FeaturePython — macro-defined, semantics opaque (R4)
  Diameter = 7
  Invert = false
  LeftHanded = false
  Length = 6
  LengthCustom = 25
  MatchOuter = false
  OffsetAngle = 0
  Placement = pos=(344,-60,-16) rot=(0,-1,0;4.71239rad)
  Thread = false
  Type = 75
FEATURE [Part::FeaturePython] Screw065  label="M6x25-Screw014"  # WARN: FeaturePython — macro-defined, semantics opaque (R4)
  Diameter = 7
  Invert = false
  LeftHanded = false
  Length = 6
  LengthCustom = 25
  MatchOuter = false
  OffsetAngle = 0
  Placement = pos=(-34,0,-16) rot=(0,1,0;-1.5708rad)
  Thread = false
  Type = 75
FEATURE [Part::FeaturePython] Screw066  label="M6x25-Screw031"  # WARN: FeaturePython — macro-defined, semantics opaque (R4)
  Diameter = 7
  Invert = false
  LeftHanded = false
  Length = 6
  LengthCustom = 25
  MatchOuter = false
  OffsetAngle = 0
  Placement = pos=(344,-20,-16) rot=(0,-1,0;4.71239rad)
  Thread = false
  Type = 75
FEATURE [Part::FeaturePython] Screw067  label="M6x25-Screw021"  # WARN: FeaturePython — macro-defined, semantics opaque (R4)
  Diameter = 7
  Invert = false
  LeftHanded = false
  Length = 6
  LengthCustom = 25
  MatchOuter = false
  OffsetAngle = 0
  Placement = pos=(-34,-20,-16) rot=(0,1,0;4.71239rad)
  Thread = false
  Type = 75
FEATURE [App::Part] Part022  label="Screws002"
  Group = -> [Screw026,Screw027,Screw028,Screw029,Screw030,Screw031,Screw032,Screw033,Screw034,Screw035,Screw036,Screw037,Screw038,Screw039,Screw040,Screw041,Screw042,Screw043,Screw067,Screw066,Screw065,Screw062,Screw061,Screw060,Screw059,Screw057,Screw056,Screw055,Screw054,Screw052,Screw058,Screw064,Screw063,Screw053]
  Origin = -> Origin1425
  Placement = pos=(-120,244,207) rot=(1,0,0;1.5708rad)
FEATURE [Part::FeaturePython] Screw068  label="M5x8-Screw"  # WARN: FeaturePython — macro-defined, semantics opaque (R4)
  Diameter = 3
  Invert = false
  LeftHanded = false
  Length = 0
  LengthCustom = 8
  MatchOuter = false
  OffsetAngle = 0
  Placement = pos=(-37,280,-23) rot=(0,1,0;1.5708rad)
  Thread = false
  Type = 85
FEATURE [Part::FeaturePython] Screw069  label="M5x8-Screw144"  # WARN: FeaturePython — macro-defined, semantics opaque (R4)
  Diameter = 3
  Invert = false
  LeftHanded = false
  Length = 0
  LengthCustom = 8
  MatchOuter = false
  OffsetAngle = 0
  Placement = pos=(-150,281,-30) rot=(0,0,1;0rad)
  Thread = false
  Type = 85
FEATURE [Part::FeaturePython] Screw070  label="M5x8-Screw143"  # WARN: FeaturePython — macro-defined, semantics opaque (R4)
  Diameter = 3
  Invert = false
  LeftHanded = false
  Length = 0
  LengthCustom = 8
  MatchOuter = false
  OffsetAngle = 0
  Placement = pos=(220,281,-30) rot=(0,0,1;0rad)
  Thread = false
  Type = 85
FEATURE [Part::FeaturePython] Screw071  label="M5x8-Screw132"  # WARN: FeaturePython — macro-defined, semantics opaque (R4)
  Diameter = 3
  Invert = false
  LeftHanded = false
  Length = 0
  LengthCustom = 8
  MatchOuter = false
  OffsetAngle = 0
  Placement = pos=(97.5,280,-30) rot=(0,0,1;0rad)
  Thread = false
  Type = 85
FEATURE [Part::FeaturePython] Screw072  label="M5x8-Screw131"  # WARN: FeaturePython — macro-defined, semantics opaque (R4)
  Diameter = 3
  Invert = false
  LeftHanded = false
  Length = 0
  LengthCustom = 8
  MatchOuter = false
  OffsetAngle = 0
  Placement = pos=(98.5,-10,-30) rot=(0,0,1;0rad)
  Thread = false
  Type = 85
FEATURE [Part::FeaturePython] Screw073  label="M5x8-Screw135"  # WARN: FeaturePython — macro-defined, semantics opaque (R4)
  Diameter = 3
  Invert = false
  LeftHanded = false
  Length = 0
  LengthCustom = 8
  MatchOuter = false
  OffsetAngle = 0
  Placement = pos=(-28.5,-10,-30) rot=(0,0,1;0rad)
  Thread = false
  Type = 85
FEATURE [Part::FeaturePython] Screw074  label="M5x8-Screw127"  # WARN: FeaturePython — macro-defined, semantics opaque (R4)
  Diameter = 3
  Invert = false
  LeftHanded = false
  Length = 0
  LengthCustom = 8
  MatchOuter = false
  OffsetAngle = 0
  Placement = pos=(142,-10,-30) rot=(0,0,1;0rad)
  Thread = false
  Type = 85
FEATURE [Part::FeaturePython] Screw075  label="M5x8-Screw128"  # WARN: FeaturePython — macro-defined, semantics opaque (R4)
  Diameter = 3
  Invert = false
  LeftHanded = false
  Length = 0
  LengthCustom = 8
  MatchOuter = false
  OffsetAngle = 0
  Placement = pos=(142,280,-30) rot=(0,0,1;0rad)
  Thread = false
  Type = 85
FEATURE [Part::FeaturePython] Screw076  label="M5x8-Screw149"  # WARN: FeaturePython — macro-defined, semantics opaque (R4)
  Diameter = 3
  Invert = false
  LeftHanded = false
  Length = 0
  LengthCustom = 8
  MatchOuter = false
  OffsetAngle = 0
  Placement = pos=(133,300,-23) rot=(0,1,0;1.5708rad)
  Thread = false
  Type = 85
FEATURE [Part::FeaturePython] Screw077  label="M5x8-Screw129"  # WARN: FeaturePython — macro-defined, semantics opaque (R4)
  Diameter = 3
  Invert = false
  LeftHanded = false
  Length = 0
  LengthCustom = 8
  MatchOuter = false
  OffsetAngle = 0
  Placement = pos=(142,300,-30) rot=(0,0,1;0rad)
  Thread = false
  Type = 85
FEATURE [Part::FeaturePython] Screw078  label="M5x8-Screw141"  # WARN: FeaturePython — macro-defined, semantics opaque (R4)
  Diameter = 3
  Invert = false
  LeftHanded = false
  Length = 0
  LengthCustom = 8
  MatchOuter = false
  OffsetAngle = 0
  Placement = pos=(-73,300,-30) rot=(0,0,1;0rad)
  Thread = false
  Type = 85
FEATURE [Part::FeaturePython] Screw079  label="M5x8-Screw130"  # WARN: FeaturePython — macro-defined, semantics opaque (R4)
  Diameter = 3
  Invert = false
  LeftHanded = false
  Length = 0
  LengthCustom = 8
  MatchOuter = false
  OffsetAngle = 0
  Placement = pos=(98,-30,-30) rot=(0,0,1;0rad)
  Thread = false
  Type = 85
FEATURE [Part::FeaturePython] Screw081  label="M5x8-Screw142"  # WARN: FeaturePython — macro-defined, semantics opaque (R4)
  Diameter = 3
  Invert = false
  LeftHanded = false
  Length = 0
  LengthCustom = 8
  MatchOuter = false
  OffsetAngle = 0
  Placement = pos=(220,218,-30) rot=(0,0,1;0rad)
  Thread = false
  Type = 85
FEATURE [Part::FeaturePython] Screw082  label="M5x8-Screw139"  # WARN: FeaturePython — macro-defined, semantics opaque (R4)
  Diameter = 3
  Invert = false
  LeftHanded = false
  Length = 0
  LengthCustom = 8
  MatchOuter = false
  OffsetAngle = 0
  Placement = pos=(-29,300,-30) rot=(0,0,1;0rad)
  Thread = false
  Type = 85
FEATURE [Part::FeaturePython] Screw084  label="M5x8-Screw137"  # WARN: FeaturePython — macro-defined, semantics opaque (R4)
  Diameter = 3
  Invert = false
  LeftHanded = false
  Length = 0
  LengthCustom = 8
  MatchOuter = false
  OffsetAngle = 0
  Placement = pos=(-71,-10,-30) rot=(0,0,1;0rad)
  Thread = false
  Type = 85
FEATURE [Part::FeaturePython] Screw085  label="M5x8-Screw154"  # WARN: FeaturePython — macro-defined, semantics opaque (R4)
  Diameter = 3
  Invert = false
  LeftHanded = false
  Length = 0
  LengthCustom = 8
  MatchOuter = false
  OffsetAngle = 0
  Placement = pos=(-63,-30,-23) rot=(0.707107,0,-0.707107;3.14159rad)
  Thread = false
  Type = 85
FEATURE [Part::FeaturePython] Screw086  label="M5x8-Screw148"  # WARN: FeaturePython — macro-defined, semantics opaque (R4)
  Diameter = 3
  Invert = false
  LeftHanded = false
  Length = 0
  LengthCustom = 8
  MatchOuter = false
  OffsetAngle = 0
  Placement = pos=(133,-10,-22) rot=(0,1,0;1.5708rad)
  Thread = false
  Type = 85
FEATURE [Part::FeaturePython] Screw087  label="M5x8-Screw136"  # WARN: FeaturePython — macro-defined, semantics opaque (R4)
  Diameter = 3
  Invert = false
  LeftHanded = false
  Length = 0
  LengthCustom = 8
  MatchOuter = false
  OffsetAngle = 0
  Placement = pos=(-72,-30,-30) rot=(0,0,1;0rad)
  Thread = false
  Type = 85
FEATURE [Part::FeaturePython] Screw088  label="M5x8-Screw145"  # WARN: FeaturePython — macro-defined, semantics opaque (R4)
  Diameter = 3
  Invert = false
  LeftHanded = false
  Length = 0
  LengthCustom = 8
  MatchOuter = false
  OffsetAngle = 0
  Placement = pos=(-150,219,-30) rot=(0,0,1;0rad)
  Thread = false
  Type = 85
FEATURE [Part::FeaturePython] Screw089  label="M5x8-Screw140"  # WARN: FeaturePython — macro-defined, semantics opaque (R4)
  Diameter = 3
  Invert = false
  LeftHanded = false
  Length = 0
  LengthCustom = 8
  MatchOuter = false
  OffsetAngle = 0
  Placement = pos=(-72,280,-30) rot=(0,0,1;0rad)
  Thread = false
  Type = 85
FEATURE [Part::FeaturePython] Screw090  label="M5x8-Screw158"  # WARN: FeaturePython — macro-defined, semantics opaque (R4)
  Diameter = 3
  Invert = false
  LeftHanded = false
  Length = 0
  LengthCustom = 8
  MatchOuter = false
  OffsetAngle = 0
  Placement = pos=(142,-30,-30) rot=(0,0,1;0rad)
  Thread = false
  Type = 85
FEATURE [Part::FeaturePython] Screw091  label="M5x8-Screw156"  # WARN: FeaturePython — macro-defined, semantics opaque (R4)
  Diameter = 3
  Invert = false
  LeftHanded = false
  Length = 0
  LengthCustom = 8
  MatchOuter = false
  OffsetAngle = 0
  Placement = pos=(107,-30,-23) rot=(0,1,0;4.71239rad)
  Thread = false
  Type = 85
FEATURE [Part::FeaturePython] Screw092  label="M5x8-Screw153"  # WARN: FeaturePython — macro-defined, semantics opaque (R4)
  Diameter = 3
  Invert = false
  LeftHanded = false
  Length = 0
  LengthCustom = 8
  MatchOuter = false
  OffsetAngle = 0
  Placement = pos=(-37,300,-23) rot=(0,1,0;1.5708rad)
  Thread = false
  Type = 85
FEATURE [Part::FeaturePython] Screw093  label="M5x8-Screw138"  # WARN: FeaturePython — macro-defined, semantics opaque (R4)
  Diameter = 3
  Invert = false
  LeftHanded = false
  Length = 0
  LengthCustom = 8
  MatchOuter = false
  OffsetAngle = 0
  Placement = pos=(-29,280,-30) rot=(0,0,1;0rad)
  Thread = false
  Type = 85
FEATURE [Part::FeaturePython] Screw094  label="M5x8-Screw155"  # WARN: FeaturePython — macro-defined, semantics opaque (R4)
  Diameter = 3
  Invert = false
  LeftHanded = false
  Length = 0
  LengthCustom = 8
  MatchOuter = false
  OffsetAngle = 0
  Placement = pos=(-63,-10,-23) rot=(0,1,0;4.71239rad)
  Thread = false
  Type = 85
FEATURE [Part::FeaturePython] Screw095  label="M5x8-Screw133"  # WARN: FeaturePython — macro-defined, semantics opaque (R4)
  Diameter = 3
  Invert = false
  LeftHanded = false
  Length = 0
  LengthCustom = 8
  MatchOuter = false
  OffsetAngle = 0
  Placement = pos=(97.5,300,-30) rot=(0,0,1;0rad)
  Thread = false
  Type = 85
FEATURE [Part::FeaturePython] Screw096  label="M5x8-Screw152"  # WARN: FeaturePython — macro-defined, semantics opaque (R4)
  Diameter = 3
  Invert = false
  LeftHanded = false
  Length = 0
  LengthCustom = 8
  MatchOuter = false
  OffsetAngle = 0
  Placement = pos=(133,280,-23) rot=(0,1,0;1.5708rad)
  Thread = false
  Type = 85
FEATURE [Part::FeaturePython] Screw097  label="M5x8-Screw151"  # WARN: FeaturePython — macro-defined, semantics opaque (R4)
  Diameter = 3
  Invert = false
  LeftHanded = false
  Length = 0
  LengthCustom = 8
  MatchOuter = false
  OffsetAngle = 0
  Placement = pos=(-37,-10,-21) rot=(0,1,0;1.5708rad)
  Thread = false
  Type = 85
FEATURE [Part::FeaturePython] Screw098  label="M5x8-Screw150"  # WARN: FeaturePython — macro-defined, semantics opaque (R4)
  Diameter = 3
  Invert = false
  LeftHanded = false
  Length = 0
  LengthCustom = 8
  MatchOuter = false
  OffsetAngle = 0
  Placement = pos=(-37,-30,-21) rot=(0,1,0;1.5708rad)
  Thread = false
  Type = 85
FEATURE [Part::FeaturePython] Screw099  label="M5x8-Screw134"  # WARN: FeaturePython — macro-defined, semantics opaque (R4)
  Diameter = 3
  Invert = false
  LeftHanded = false
  Length = 0
  LengthCustom = 8
  MatchOuter = false
  OffsetAngle = 0
  Placement = pos=(-28,-30,-30) rot=(0,0,1;0rad)
  Thread = false
  Type = 85
FEATURE [Part::FeaturePython] Screw100  label="M6x25-Screw090"  # WARN: FeaturePython — macro-defined, semantics opaque (R4)
  Diameter = 7
  Invert = false
  LeftHanded = false
  Length = 6
  LengthCustom = 25
  MatchOuter = false
  OffsetAngle = 0
  Placement = pos=(-150,260,-47) rot=(0,-1,0;3.14159rad)
  Thread = false
  Type = 75
FEATURE [Part::FeaturePython] Screw101  label="M6x25-Screw080"  # WARN: FeaturePython — macro-defined, semantics opaque (R4)
  Diameter = 7
  Invert = false
  LeftHanded = false
  Length = 6
  LengthCustom = 25
  MatchOuter = false
  OffsetAngle = 0
  Placement = pos=(224,-10,-43) rot=(0,1,0;1.5708rad)
  Thread = false
  Type = 75
FEATURE [Part::FeaturePython] Screw102  label="M6x25-Screw081"  # WARN: FeaturePython — macro-defined, semantics opaque (R4)
  Diameter = 7
  Invert = false
  LeftHanded = false
  Length = 6
  LengthCustom = 25
  MatchOuter = false
  OffsetAngle = 0
  Placement = pos=(224,280,-43) rot=(0,1,0;1.5708rad)
  Thread = false
  Type = 75
FEATURE [Part::FeaturePython] Screw103  label="M6x25-Screw085"  # WARN: FeaturePython — macro-defined, semantics opaque (R4)
  Diameter = 7
  Invert = false
  LeftHanded = false
  Length = 6
  LengthCustom = 25
  MatchOuter = false
  OffsetAngle = 0
  Placement = pos=(-154,-30,-43) rot=(-0.707107,0,0.707107;3.14159rad)
  Thread = false
  Type = 75
FEATURE [Part::FeaturePython] Screw104  label="M6x25-Screw083"  # WARN: FeaturePython — macro-defined, semantics opaque (R4)
  Diameter = 7
  Invert = false
  LeftHanded = false
  Length = 6
  LengthCustom = 25
  MatchOuter = false
  OffsetAngle = 0
  Placement = pos=(220,240,-47) rot=(0,1,0;3.14159rad)
  Thread = false
  Type = 75
FEATURE [Part::FeaturePython] Screw105  label="M6x25-Screw082"  # WARN: FeaturePython — macro-defined, semantics opaque (R4)
  Diameter = 7
  Invert = false
  LeftHanded = false
  Length = 6
  LengthCustom = 25
  MatchOuter = false
  OffsetAngle = 0
  Placement = pos=(224,300,-43) rot=(0,1,0;1.5708rad)
  Thread = false
  Type = 75
FEATURE [Part::FeaturePython] Screw106  label="M6x25-Screw086"  # WARN: FeaturePython — macro-defined, semantics opaque (R4)
  Diameter = 7
  Invert = false
  LeftHanded = false
  Length = 6
  LengthCustom = 25
  MatchOuter = false
  OffsetAngle = 0
  Placement = pos=(-154,-10,-43) rot=(0.707107,0,-0.707107;3.14159rad)
  Thread = false
  Type = 75
FEATURE [Part::FeaturePython] Screw107  label="M6x25-Screw084"  # WARN: FeaturePython — macro-defined, semantics opaque (R4)
  Diameter = 7
  Invert = false
  LeftHanded = false
  Length = 6
  LengthCustom = 25
  MatchOuter = false
  OffsetAngle = 0
  Placement = pos=(220,260,-47) rot=(0,1,0;3.14159rad)
  Thread = false
  Type = 75
FEATURE [Part::FeaturePython] Screw108  label="M6x25-Screw088"  # WARN: FeaturePython — macro-defined, semantics opaque (R4)
  Diameter = 7
  Invert = false
  LeftHanded = false
  Length = 6
  LengthCustom = 25
  MatchOuter = false
  OffsetAngle = 0
  Placement = pos=(-155,300,-43) rot=(0,1,0;4.71239rad)
  Thread = false
  Type = 75
FEATURE [Part::FeaturePython] Screw109  label="M6x25-Screw087"  # WARN: FeaturePython — macro-defined, semantics opaque (R4)
  Diameter = 7
  Invert = false
  LeftHanded = false
  Length = 6
  LengthCustom = 25
  MatchOuter = false
  OffsetAngle = 0
  Placement = pos=(-154,280,-43) rot=(0.707107,0,-0.707107;3.14159rad)
  Thread = false
  Type = 75
FEATURE [Part::FeaturePython] Screw110  label="M6x25-Screw089"  # WARN: FeaturePython — macro-defined, semantics opaque (R4)
  Diameter = 7
  Invert = false
  LeftHanded = false
  Length = 6
  LengthCustom = 25
  MatchOuter = false
  OffsetAngle = 0
  Placement = pos=(-150,240,-47) rot=(0,1,0;3.14159rad)
  Thread = false
  Type = 75
FEATURE [Part::FeaturePython] Screw111  label="M6x25-Screw078"  # WARN: FeaturePython — macro-defined, semantics opaque (R4)
  Diameter = 7
  Invert = false
  LeftHanded = false
  Length = 6
  LengthCustom = 25
  MatchOuter = false
  OffsetAngle = 0
  Placement = pos=(224,-30,-43) rot=(0,1,0;1.5708rad)
  Thread = false
  Type = 75
FEATURE [Part::FeaturePython] Screw083  label="M5x8-Screw147"  # WARN: FeaturePython — macro-defined, semantics opaque (R4)
  Diameter = 3
  Invert = false
  LeftHanded = false
  Length = 0
  LengthCustom = 8
  MatchOuter = false
  OffsetAngle = 0
  Placement = pos=(133,-30,-21) rot=(0,1,0;1.5708rad)
  Thread = false
  Type = 85
FEATURE [Part::FeaturePython] Screw080  label="M5x8-Screw157"  # WARN: FeaturePython — macro-defined, semantics opaque (R4)
  Diameter = 3
  Invert = false
  LeftHanded = false
  Length = 0
  LengthCustom = 8
  MatchOuter = false
  OffsetAngle = 0
  Placement = pos=(107,-10,-23) rot=(0,1,0;4.71239rad)
  Thread = false
  Type = 85
FEATURE [Part::FeaturePython] Screw112  label="M5x8-Screw183"  # WARN: FeaturePython — macro-defined, semantics opaque (R4)
  Diameter = 3
  Invert = false
  LeftHanded = false
  Length = 0
  LengthCustom = 8
  MatchOuter = false
  OffsetAngle = 0
  Placement = pos=(-63,300,-23) rot=(0,1,0;4.71239rad)
  Thread = false
  Type = 85
FEATURE [Part::FeaturePython] Screw113  label="M5x8-Screw184"  # WARN: FeaturePython — macro-defined, semantics opaque (R4)
  Diameter = 3
  Invert = false
  LeftHanded = false
  Length = 0
  LengthCustom = 8
  MatchOuter = false
  OffsetAngle = 0
  Placement = pos=(107,280,-23) rot=(0,1,0;4.71239rad)
  Thread = false
  Type = 85
FEATURE [Part::FeaturePython] Screw114  label="M5x8-Screw181"  # WARN: FeaturePython — macro-defined, semantics opaque (R4)
  Diameter = 3
  Invert = false
  LeftHanded = false
  Length = 0
  LengthCustom = 8
  MatchOuter = false
  OffsetAngle = 0
  Placement = pos=(-63,280,-23) rot=(0,1,0;4.71239rad)
  Thread = false
  Type = 85
FEATURE [Part::FeaturePython] Screw115  label="M5x8-Screw185"  # WARN: FeaturePython — macro-defined, semantics opaque (R4)
  Diameter = 3
  Invert = false
  LeftHanded = false
  Length = 0
  LengthCustom = 8
  MatchOuter = false
  OffsetAngle = 0
  Placement = pos=(107,300,-23) rot=(0,1,0;4.71239rad)
  Thread = false
  Type = 85
FEATURE [Part::FeaturePython] Screw116  label="M5x8-Screw194"  # WARN: FeaturePython — macro-defined, semantics opaque (R4)
  Diameter = 3
  Invert = false
  LeftHanded = false
  Length = 0
  LengthCustom = 8
  MatchOuter = false
  OffsetAngle = 0
  Placement = pos=(-150,273,-21) rot=(1,0,0;4.71239rad)
  Thread = false
  Type = 85
FEATURE [Part::FeaturePython] Screw117  label="M5x8-Screw200"  # WARN: FeaturePython — macro-defined, semantics opaque (R4)
  Diameter = 3
  Invert = false
  LeftHanded = false
  Length = 0
  LengthCustom = 8
  MatchOuter = false
  OffsetAngle = 0
  Placement = pos=(220,227,-21) rot=(0,-0.707107,0.707107;3.14159rad)
  Thread = false
  Type = 85
FEATURE [Part::FeaturePython] Screw118  label="M5x8-Screw198"  # WARN: FeaturePython — macro-defined, semantics opaque (R4)
  Diameter = 3
  Invert = false
  LeftHanded = false
  Length = 0
  LengthCustom = 8
  MatchOuter = false
  OffsetAngle = 0
  Placement = pos=(-150,227,-21) rot=(0,-0.707107,0.707107;3.14159rad)
  Thread = false
  Type = 85
FEATURE [Part::FeaturePython] Screw119  label="M5x8-Screw199"  # WARN: FeaturePython — macro-defined, semantics opaque (R4)
  Diameter = 3
  Invert = false
  LeftHanded = false
  Length = 0
  LengthCustom = 8
  MatchOuter = false
  OffsetAngle = 0
  Placement = pos=(220,273,-21) rot=(1,0,0;4.71239rad)
  Thread = false
  Type = 85
FEATURE [Part::FeaturePython] Screw120  label="M5x12-Screw"  # WARN: FeaturePython — macro-defined, semantics opaque (R4)
  Diameter = 6
  Invert = false
  LeftHanded = false
  Length = 2
  LengthCustom = 12
  MatchOuter = false
  OffsetAngle = 0
  Placement = pos=(64.25,319,-43) rot=(1,0,0;-1.5708rad)
  Thread = false
  Type = 75
FEATURE [Part::FeaturePython] Screw121  label="M5x12-Screw001"  # WARN: FeaturePython — macro-defined, semantics opaque (R4)
  Diameter = 6
  Invert = false
  LeftHanded = false
  Length = 2
  LengthCustom = 12
  MatchOuter = false
  OffsetAngle = 0
  Placement = pos=(6,319,-43) rot=(1,0,0;-1.5708rad)
  Thread = false
  Type = 75
FEATURE [Part::FeaturePython] Screw122  label="M3x8-Screw"  # WARN: FeaturePython — macro-defined, semantics opaque (R4)
  Diameter = 4
  Invert = false
  LeftHanded = false
  Length = 2
  LengthCustom = 8
  MatchOuter = false
  OffsetAngle = 0
  Placement = pos=(50.5,324,-25) rot=(1,0,0;1.5708rad)
  Thread = false
  Type = 75
FEATURE [Part::FeaturePython] Screw123  label="M3x8-Screw014"  # WARN: FeaturePython — macro-defined, semantics opaque (R4)
  Diameter = 4
  Invert = false
  LeftHanded = false
  Length = 2
  LengthCustom = 8
  MatchOuter = false
  OffsetAngle = 0
  Placement = pos=(19.5,324,6) rot=(1,0,0;1.5708rad)
  Thread = false
  Type = 75
FEATURE [Part::FeaturePython] Screw124  label="M3x8-Screw015"  # WARN: FeaturePython — macro-defined, semantics opaque (R4)
  Diameter = 4
  Invert = false
  LeftHanded = false
  Length = 2
  LengthCustom = 8
  MatchOuter = false
  OffsetAngle = 0
  Placement = pos=(50.5,324,6) rot=(1,0,0;1.5708rad)
  Thread = false
  Type = 75
FEATURE [Part::FeaturePython] Screw125  label="M3x8-Screw016"  # WARN: FeaturePython — macro-defined, semantics opaque (R4)
  Diameter = 4
  Invert = false
  LeftHanded = false
  Length = 2
  LengthCustom = 8
  MatchOuter = false
  OffsetAngle = 0
  Placement = pos=(19.5,324,-25) rot=(1,0,0;1.5708rad)
  Thread = false
  Type = 75
FEATURE [App::Part] Part023  label="Screws003"
  Group = -> [Screw099,Screw068,Screw069,Screw070,Screw071,Screw072,Screw073,Screw074,Screw075,Screw076,Screw077,Screw078,Screw079,Screw080,Screw081,Screw082,Screw083,Screw084,Screw085,Screw086,Screw087,Screw088,Screw089,Screw090,Screw091,Screw092,Screw093,Screw094,Screw095,Screw096,Screw097,Screw101,Screw102,Screw103,Screw104,Screw105,Screw106,Screw107,Screw108,Screw109,Screw110,Screw111,Screw100,Screw098,+14 more]
  Origin = -> Origin1427
FEATURE [Part::FeaturePython] Screw126  label="M3x14-Screw"  # WARN: FeaturePython — macro-defined, semantics opaque (R4)
  Diameter = 3
  Invert = false
  LeftHanded = false
  Length = 7
  LengthCustom = 14
  MatchOuter = false
  OffsetAngle = 0
  Placement = pos=(-7.5,-40.5,32) rot=(0,0,1;0rad)
  Thread = false
  Type = 51
FEATURE [Part::FeaturePython] Screw127  label="M3x14-Screw021"  # WARN: FeaturePython — macro-defined, semantics opaque (R4)
  Diameter = 3
  Invert = false
  LeftHanded = false
  Length = 7
  LengthCustom = 14
  MatchOuter = false
  OffsetAngle = 0
  Placement = pos=(52.5,-40.5,32) rot=(0,0,1;0rad)
  Thread = false
  Type = 51
FEATURE [Part::FeaturePython] Screw128  label="M3x14-Screw019"  # WARN: FeaturePython — macro-defined, semantics opaque (R4)
  Diameter = 3
  Invert = false
  LeftHanded = false
  Length = 7
  LengthCustom = 14
  MatchOuter = false
  OffsetAngle = 0
  Placement = pos=(-32.5,-40.5,32) rot=(0,0,1;0rad)
  Thread = false
  Type = 51
FEATURE [Part::FeaturePython] Screw129  label="M3x14-Screw022"  # WARN: FeaturePython — macro-defined, semantics opaque (R4)
  Diameter = 3
  Invert = false
  LeftHanded = false
  Length = 7
  LengthCustom = 14
  MatchOuter = false
  OffsetAngle = 0
  Placement = pos=(-32.5,-15.5,32) rot=(0,0,1;0rad)
  Thread = false
  Type = 51
FEATURE [Part::FeaturePython] Screw130  label="M3x14-Screw017"  # WARN: FeaturePython — macro-defined, semantics opaque (R4)
  Diameter = 3
  Invert = false
  LeftHanded = false
  Length = 7
  LengthCustom = 14
  MatchOuter = false
  OffsetAngle = 0
  Placement = pos=(27.5,-15.5,32) rot=(0,0,1;0rad)
  Thread = false
  Type = 51
FEATURE [Part::FeaturePython] Screw131  label="M3x14-Screw016"  # WARN: FeaturePython — macro-defined, semantics opaque (R4)
  Diameter = 3
  Invert = false
  LeftHanded = false
  Length = 7
  LengthCustom = 14
  MatchOuter = false
  OffsetAngle = 0
  Placement = pos=(-7.5,-15.5,32) rot=(0,0,1;0rad)
  Thread = false
  Type = 51
FEATURE [Part::FeaturePython] Screw132  label="M3x14-Screw020"  # WARN: FeaturePython — macro-defined, semantics opaque (R4)
  Diameter = 3
  Invert = false
  LeftHanded = false
  Length = 7
  LengthCustom = 14
  MatchOuter = false
  OffsetAngle = 0
  Placement = pos=(27.5,-40.5,32) rot=(0,0,1;0rad)
  Thread = false
  Type = 51
FEATURE [Part::FeaturePython] Screw133  label="M3x14-Screw018"  # WARN: FeaturePython — macro-defined, semantics opaque (R4)
  Diameter = 3
  Invert = false
  LeftHanded = false
  Length = 7
  LengthCustom = 14
  MatchOuter = false
  OffsetAngle = 0
  Placement = pos=(52.5,-15.5,32) rot=(0,0,1;0rad)
  Thread = false
  Type = 51
FEATURE [Part::FeaturePython] Screw134  label="M6x60-Screw"  # WARN: FeaturePython — macro-defined, semantics opaque (R4)
  Diameter = 7
  Invert = false
  LeftHanded = false
  Length = 13
  LengthCustom = 60
  MatchOuter = false
  OffsetAngle = 0
  Placement = pos=(-25,-38.25,85) rot=(0,0,1;0rad)
  Thread = false
  Type = 75
FEATURE [Part::FeaturePython] Screw135  label="M6x60-Screw013"  # WARN: FeaturePython — macro-defined, semantics opaque (R4)
  Diameter = 7
  Invert = false
  LeftHanded = false
  Length = 13
  LengthCustom = 60
  MatchOuter = false
  OffsetAngle = 0
  Placement = pos=(45,-18.25,85) rot=(0,0,1;0rad)
  Thread = false
  Type = 75
FEATURE [Part::FeaturePython] Screw136  label="M6x60-Screw014"  # WARN: FeaturePython — macro-defined, semantics opaque (R4)
  Diameter = 7
  Invert = false
  LeftHanded = false
  Length = 13
  LengthCustom = 60
  MatchOuter = false
  OffsetAngle = 0
  Placement = pos=(45,-38.25,85) rot=(0,0,1;0rad)
  Thread = false
  Type = 75
FEATURE [Part::FeaturePython] Screw137  label="M6x60-Screw012"  # WARN: FeaturePython — macro-defined, semantics opaque (R4)
  Diameter = 7
  Invert = false
  LeftHanded = false
  Length = 13
  LengthCustom = 60
  MatchOuter = false
  OffsetAngle = 0
  Placement = pos=(-25,-18.25,85) rot=(0,0,1;0rad)
  Thread = false
  Type = 75
FEATURE [App::Part] Part020  label="Screws"
  Group = -> [Screw,Screw001,Screw002,Screw003,Screw004,Screw005,Screw006,Screw007,Screw044,Screw045,Screw046,Screw047,Screw048,Screw049,Screw050,Screw051,Screw137,Screw136,Screw135,Screw134,Screw132,Screw131,Screw130,Screw128,Screw127,Screw126,Screw129,Screw133]
  Origin = -> Origin1415
  Placement = pos=(-81,220.5,219.5) rot=(1,0,0;1.5708rad)
FEATURE [Part::FeaturePython] Screw138  label="M3x18-Screw"  # WARN: FeaturePython — macro-defined, semantics opaque (R4)
  Diameter = 3
  Invert = false
  LeftHanded = false
  Length = 7
  LengthCustom = 18
  MatchOuter = false
  OffsetAngle = 0
  Placement = pos=(25,25,0) rot=(0,0,1;0rad)
  Thread = false
  Type = 51
FEATURE [Part::FeaturePython] Screw139  label="M3x18-Screw029"  # WARN: FeaturePython — macro-defined, semantics opaque (R4)
  Diameter = 3
  Invert = false
  LeftHanded = false
  Length = 7
  LengthCustom = 18
  MatchOuter = false
  OffsetAngle = 0
  Placement = pos=(0,115,0) rot=(0,0,1;0rad)
  Thread = false
  Type = 51
FEATURE [Part::FeaturePython] Screw140  label="M3x18-Screw020"  # WARN: FeaturePython — macro-defined, semantics opaque (R4)
  Diameter = 3
  Invert = false
  LeftHanded = false
  Length = 7
  LengthCustom = 18
  MatchOuter = false
  OffsetAngle = 0
  Placement = pos=(170,25,0) rot=(0,0,1;0rad)
  Thread = false
  Type = 51
FEATURE [Part::FeaturePython] Screw141  label="M3x18-Screw021"  # WARN: FeaturePython — macro-defined, semantics opaque (R4)
  Diameter = 3
  Invert = false
  LeftHanded = false
  Length = 7
  LengthCustom = 18
  MatchOuter = false
  OffsetAngle = 0
  Placement = pos=(195,25,0) rot=(0,0,1;0rad)
  Thread = false
  Type = 51
FEATURE [Part::FeaturePython] Screw142  label="M3x18-Screw023"  # WARN: FeaturePython — macro-defined, semantics opaque (R4)
  Diameter = 3
  Invert = false
  LeftHanded = false
  Length = 7
  LengthCustom = 18
  MatchOuter = false
  OffsetAngle = 0
  Placement = pos=(195,90,0) rot=(0,0,1;0rad)
  Thread = false
  Type = 51
FEATURE [Part::FeaturePython] Screw143  label="M3x18-Screw027"  # WARN: FeaturePython — macro-defined, semantics opaque (R4)
  Diameter = 3
  Invert = false
  LeftHanded = false
  Length = 7
  LengthCustom = 18
  MatchOuter = false
  OffsetAngle = 0
  Placement = pos=(25,90,0) rot=(0,0,1;0rad)
  Thread = false
  Type = 51
FEATURE [Part::FeaturePython] Screw144  label="M3x18-Screw028"  # WARN: FeaturePython — macro-defined, semantics opaque (R4)
  Diameter = 3
  Invert = false
  LeftHanded = false
  Length = 7
  LengthCustom = 18
  MatchOuter = false
  OffsetAngle = 0
  Placement = pos=(25,115,0) rot=(0,0,1;0rad)
  Thread = false
  Type = 51
FEATURE [Part::FeaturePython] Screw145  label="M3x18-Screw030"  # WARN: FeaturePython — macro-defined, semantics opaque (R4)
  Diameter = 3
  Invert = false
  LeftHanded = false
  Length = 7
  LengthCustom = 18
  MatchOuter = false
  OffsetAngle = 0
  Thread = false
  Type = 51
FEATURE [Part::FeaturePython] Screw146  label="M3x18-Screw025"  # WARN: FeaturePython — macro-defined, semantics opaque (R4)
  Diameter = 3
  Invert = false
  LeftHanded = false
  Length = 7
  LengthCustom = 18
  MatchOuter = false
  OffsetAngle = 0
  Placement = pos=(195,115,0) rot=(0,0,1;0rad)
  Thread = false
  Type = 51
FEATURE [Part::FeaturePython] Screw147  label="M3x18-Screw017"  # WARN: FeaturePython — macro-defined, semantics opaque (R4)
  Diameter = 3
  Invert = false
  LeftHanded = false
  Length = 7
  LengthCustom = 18
  MatchOuter = false
  OffsetAngle = 0
  Placement = pos=(0,25,0) rot=(0,0,1;0rad)
  Thread = false
  Type = 51
FEATURE [Part::FeaturePython] Screw148  label="M3x18-Screw016"  # WARN: FeaturePython — macro-defined, semantics opaque (R4)
  Diameter = 3
  Invert = false
  LeftHanded = false
  Length = 7
  LengthCustom = 18
  MatchOuter = false
  OffsetAngle = 0
  Placement = pos=(25,0,0) rot=(0,0,1;0rad)
  Thread = false
  Type = 51
FEATURE [Part::FeaturePython] Screw149  label="M3x18-Screw024"  # WARN: FeaturePython — macro-defined, semantics opaque (R4)
  Diameter = 3
  Invert = false
  LeftHanded = false
  Length = 7
  LengthCustom = 18
  MatchOuter = false
  OffsetAngle = 0
  Placement = pos=(170,115,0) rot=(0,0,1;0rad)
  Thread = false
  Type = 51
FEATURE [Part::FeaturePython] Screw150  label="M3x18-Screw019"  # WARN: FeaturePython — macro-defined, semantics opaque (R4)
  Diameter = 3
  Invert = false
  LeftHanded = false
  Length = 7
  LengthCustom = 18
  MatchOuter = false
  OffsetAngle = 0
  Placement = pos=(195,0,0) rot=(0,0,1;0rad)
  Thread = false
  Type = 51
FEATURE [Part::FeaturePython] Screw151  label="M3x18-Screw018"  # WARN: FeaturePython — macro-defined, semantics opaque (R4)
  Diameter = 3
  Invert = false
  LeftHanded = false
  Length = 7
  LengthCustom = 18
  MatchOuter = false
  OffsetAngle = 0
  Placement = pos=(170,0,0) rot=(0,0,1;0rad)
  Thread = false
  Type = 51
FEATURE [Part::FeaturePython] Screw152  label="M3x18-Screw022"  # WARN: FeaturePython — macro-defined, semantics opaque (R4)
  Diameter = 3
  Invert = false
  LeftHanded = false
  Length = 7
  LengthCustom = 18
  MatchOuter = false
  OffsetAngle = 0
  Placement = pos=(170,90,0) rot=(0,0,1;0rad)
  Thread = false
  Type = 51
FEATURE [Part::FeaturePython] Screw153  label="M3x18-Screw026"  # WARN: FeaturePython — macro-defined, semantics opaque (R4)
  Diameter = 3
  Invert = false
  LeftHanded = false
  Length = 7
  LengthCustom = 18
  MatchOuter = false
  OffsetAngle = 0
  Placement = pos=(0,90,0) rot=(0,0,1;0rad)
  Thread = false
  Type = 51
FEATURE [App::Part] Part024  label="Screws004"
  Group = -> [Screw138,Screw139,Screw140,Screw141,Screw142,Screw143,Screw144,Screw145,Screw146,Screw147,Screw148,Screw149,Screw150,Screw151,Screw152,Screw153]
  Origin = -> Origin1429
  Placement = pos=(-62.5,183,18.25) rot=(0,0,1;0rad)
FEATURE [App::Part] Part007  label="Bed"
  Group = -> [Body002,Body076,Body077,Body081,Body080,Part012,Part024]
  Origin = -> Origin050
  Placement = pos=(0,-112.35,0) rot=(0,0,1;0rad)
FEATURE [App::Part] Part001  label="yAxis"
  Group = -> [Part007,Part008,Part014]
  Origin = -> Origin008
  Placement = pos=(0,-5,0) rot=(0,0,1;0rad)
FEATURE [Part::Feature] Part__Feature  label="Main board"
  shape: bbox 109.7 x 84.3 x 1.6 mm, 10 faces (baked)
FEATURE [Part::Feature] Part__Feature001  label="Main CPU"
  Placement = pos=(-4.44489,1.05831,0) rot=(0,0,1;0rad)
  shape: bbox 13.8 x 13.4 x 1.4 mm, 10 faces (baked)
FEATURE [Part::Feature] Part__Feature002  label="10 pin male socket v2"
  Placement = pos=(73.3778,17.059,1.70938) rot=(0.57735,0.57735,0.57735;2.0944rad)
  shape: bbox 9 x 20.25 x 12.5 mm, 122 faces (baked)
FEATURE [Part::Feature] Part__Feature003  label="JST XH 2 v3"
  Placement = pos=(-43.4664,38.7533,1.66076) rot=(0,0.707107,0.707107;3.14159rad)
  shape: bbox 7.4 x 5.75 x 10.45 mm, 58 faces (baked)
FEATURE [Part::Feature] Part__Feature004  label="JST XH 4 v3"
  Placement = pos=(-32.8365,38.7526,1.63184) rot=(0,0.707107,0.707107;3.14159rad)
  shape: bbox 12.4 x 5.75 x 10.45 mm, 100 faces (baked)
FEATURE [Part::Feature] Part__Feature005  label="JST XH 3 v3"
  Placement = pos=(40.776,7.8268,1.72291) rot=(0.57735,-0.57735,-0.57735;2.0944rad)
  shape: bbox 5.75 x 9.9 x 10.45 mm, 82 faces (baked)
FEATURE [Part::Feature] Part__Feature006  label="Power FeT 2 v4"
  Placement = pos=(-40.5703,-1.88106,1.56884) rot=(0.57735,0.57735,0.57735;2.0944rad)
  shape: bbox 9.028 x 6.35 x 2.021 mm, 53 faces (baked)
FEATURE [Part::Feature] Part__Feature007  label="Power FeT 1 v4"
  Placement = pos=(-35.6044,-13.3607,1.8559) rot=(0.57735,0.57735,0.57735;2.0944rad)
  shape: bbox 11.77 x 9.62 x 2.4 mm, 39 faces (baked)
FEATURE [Part::Feature] Part__Feature008  label="Reset button v2"
  Placement = pos=(50.92,-28.4044,1.6793) rot=(0.57735,-0.57735,-0.57735;2.0944rad)
  shape: bbox 6.02 x 9.25 x 2.95 mm, 36 faces (baked)
FEATURE [Part::Feature] Part__Feature009  label="USB socket v6"
  Placement = pos=(-17.3181,15.7375,6.28896) rot=(0.57735,0.57735,0.57735;2.0944rad)
  shape: bbox 14.88 x 16.52 x 14.24 mm, 143 faces (baked)
FEATURE [Part::Feature] Part__Feature010  label="2 pole terminal block v7 v7"
  Placement = pos=(-49.282,-14.9262,6.944) rot=(0.57735,0.57735,0.57735;2.0944rad)
  shape: bbox 9 x 10.8 x 17.25 mm, 32 faces (baked)
FEATURE [Part::Feature] Part__Feature011  label="2 pole terminal block v7 v001"
  Placement = pos=(-49.282,-14.9262,6.944) rot=(0.57735,0.57735,0.57735;2.0944rad)
  shape: bbox 3 x 3 x 7.027 mm, 7 faces (baked)
FEATURE [Part::Feature] Part__Feature012  label="2 pole terminal block v7 v002"
  Placement = pos=(-49.282,-14.9262,6.944) rot=(0.57735,0.57735,0.57735;2.0944rad)
  shape: bbox 3 x 3 x 7.027 mm, 7 faces (baked)
FEATURE [App::Part] _2_pole_terminal_block_v7_v7  label="2 pole terminal block v7 v003"
  Group = -> [Part__Feature010,Part__Feature011,Part__Feature012]
  Origin = -> Origin1433
FEATURE [Part::Feature] Part__Feature013  label="Pin header jumper v5"
  Placement = pos=(-17.0486,-13.5341,4.24885) rot=(0,0,1;1.5708rad)
  shape: bbox 2.5 x 5 x 6 mm, 33 faces (baked)
FEATURE [Part::Feature] Part__Feature014  label="Pin header jumper v001"
  Placement = pos=(-17.0486,-13.5341,4.24885) rot=(0,0,1;1.5708rad)
  shape: bbox 1.5 x 4 x 2.462 mm, 22 faces (baked)
FEATURE [App::Part] Pin_header_jumper_v5  label="Pin header jumper v002"
  Group = -> [Part__Feature013,Part__Feature014]
  Origin = -> Origin1435
FEATURE [Part::Feature] Part__Feature015  label="3 PIN HEADER v2"
  Placement = pos=(-17.1072,-16.2086,1.07754) rot=(0.57735,0.57735,0.57735;2.0944rad)
  shape: bbox 2.5 x 7.47 x 11 mm, 92 faces (baked)
FEATURE [Part::Feature] Part__Feature016  label="3 PIN HEADER blk v1"
  Placement = pos=(0.582043,-25.5353,1.65998) rot=(1,0,0;1.5708rad)
  shape: bbox 7.47 x 2.5 x 11 mm, 92 faces (baked)
FEATURE [Part::Feature] Part__Feature017  label="Micro SD card slot v3"
  Placement = pos=(-0.396823,-12.6983,1.65343) rot=(0,0,1;0rad)
  shape: bbox 15.06 x 15.36 x 1.606 mm, 78 faces (baked)
FEATURE [Part::Feature] Part__Feature018  label="blk power terminal v3"
  Placement = pos=(1.55908,-13.6551,1.56926) rot=(0,0,1;0rad)
  shape: bbox 7.981 x 10.42 x 8.5 mm, 34 faces (baked)
FEATURE [Part::Feature] Part__Feature019  label="blk power terminal v001"
  Placement = pos=(1.55908,-13.6551,1.56926) rot=(0,0,1;0rad)
  shape: bbox 3.327 x 3.327 x 2.918 mm, 20 faces (baked)
FEATURE [Part::Feature] Part__Feature020  label="blk power terminal v002"
  Placement = pos=(1.55908,-13.6551,1.56926) rot=(0,0,1;0rad)
  shape: bbox 3.327 x 3.327 x 2.918 mm, 22 faces (baked)
FEATURE [App::Part] blk_power_terminal_v3  label="blk power terminal v003"
  Group = -> [Part__Feature018,Part__Feature019,Part__Feature020]
  Origin = -> Origin1437
FEATURE [Part::Feature] Part__Feature021  label="PCB fuse 10 amp V2 v3"
  Placement = pos=(-35.0273,-33.5784,1.62837) rot=(0,0,1;1.5708rad)
  shape: bbox 5 x 15 x 9 mm, 42 faces (baked)
FEATURE [Part::Feature] Part__Feature022  label="PCB fuse 10 amp V2 v001"
  Placement = pos=(-35.0273,-33.5784,1.62837) rot=(0,0,1;1.5708rad)
  shape: bbox 2.35 x 4.5 x 5 mm, 18 faces (baked)
FEATURE [Part::Feature] Part__Feature023  label="PCB fuse 10 amp V2 v002"
  Placement = pos=(-35.0273,-33.5784,1.62837) rot=(0,0,1;1.5708rad)
  shape: bbox 2.35 x 4.5 x 5 mm, 18 faces (baked)
FEATURE [Part::Feature] Part__Feature024  label="PCB fuse 10 amp V2 v003"
  Placement = pos=(-35.0273,-33.5784,1.62837) rot=(0,0,1;1.5708rad)
  shape: bbox 4.5 x 11.7 x 8.149 mm, 38 faces (baked)
FEATURE [App::Part] PCB_fuse_10_amp_V2_v3  label="PCB fuse 10 amp V2 v004"
  Group = -> [Part__Feature021,Part__Feature022,Part__Feature023,Part__Feature024]
  Origin = -> Origin1439
FEATURE [Part::Feature] Part__Feature025  label="PCB fuse 20 amp V2 v1"
  Placement = pos=(-40.2272,-33.6302,1.57038) rot=(0,0,1;1.5708rad)
  shape: bbox 5 x 15 x 9 mm, 42 faces (baked)
FEATURE [Part::Feature] Part__Feature026  label="PCB fuse 20 amp V2 v001"
  Placement = pos=(-40.2272,-33.6302,1.57038) rot=(0,0,1;1.5708rad)
  shape: bbox 2.35 x 4.5 x 5 mm, 18 faces (baked)
FEATURE [Part::Feature] Part__Feature027  label="PCB fuse 20 amp V2 v002"
  Placement = pos=(-40.2272,-33.6302,1.57038) rot=(0,0,1;1.5708rad)
  shape: bbox 2.35 x 4.5 x 5 mm, 18 faces (baked)
FEATURE [Part::Feature] Part__Feature028  label="PCB fuse 20 amp V2 v003"
  Placement = pos=(-40.2272,-33.6302,1.57038) rot=(0,0,1;1.5708rad)
  shape: bbox 4.5 x 11.7 x 8.149 mm, 38 faces (baked)
FEATURE [App::Part] PCB_fuse_20_amp_V2_v1  label="PCB fuse 20 amp V2 v004"
  Group = -> [Part__Feature025,Part__Feature026,Part__Feature027,Part__Feature028]
  Origin = -> Origin1441
FEATURE [Part::Feature] Part__Feature029  label="2 PIN HEADER blk v2"
  Placement = pos=(21.842,-13.3691,1.66319) rot=(1,0,0;1.5708rad)
  shape: bbox 4.93 x 2.5 x 11 mm, 62 faces (baked)
FEATURE [Part::Feature] Part__Feature030  label="4 PIN HEADER v2"
  Placement = pos=(14.3917,-23.0047,1.6041) rot=(-1,0,0;1.5708rad)
  shape: bbox 10.06 x 2.5 x 11 mm, 122 faces (baked)
FEATURE [Part::Feature] Part__Feature031  label="stepper socket v7"
  Placement = pos=(-52.1915,20.2005,1.64594) rot=(0,0,1;0rad)
  shape: bbox 20.58 x 2.8 x 8 mm, 38 faces (baked)
FEATURE [Part::Feature] Part__Feature032  label="stepper socket v001"
  Placement = pos=(-52.1915,20.2005,1.64594) rot=(0,0,1;0rad)
  shape: bbox 20.58 x 2.8 x 8 mm, 38 faces (baked)
FEATURE [Part::Feature] Part__Feature033  label="stepper socket v002"
  Placement = pos=(-52.1915,20.2005,1.64594) rot=(0,0,1;0rad)
  shape: bbox 2.8 x 5.21 x 8 mm, 14 faces (baked)
FEATURE [App::Part] stepper_socket_v7  label="stepper socket v003"
  Group = -> [Part__Feature031,Part__Feature032,Part__Feature033]
  Origin = -> Origin1443
FEATURE [Part::Feature] Part__Feature034  label="2 PIN HEADER v2"
  Placement = pos=(-39.5031,30.5124,1.66609) rot=(1,0,0;1.57065rad)
  shape: bbox 4.93 x 2.5 x 11 mm, 62 faces (baked)
FEATURE [Part::Feature] Part__Feature035  label="Elco100_35 v3"
  Placement = pos=(-46.1892,27.9603,2.24794) rot=(0.57735,-0.57735,-0.57735;2.0944rad)
  shape: bbox 7 x 6.819 x 6.95 mm, 28 faces (baked)
FEATURE [Part::Feature] Part__Feature036  label="2 PIN HEADER v001"
  Placement = pos=(-39.5031,27.9724,1.66646) rot=(1,0,0;1.57065rad)
  shape: bbox 4.93 x 2.5 x 11 mm, 62 faces (baked)
FEATURE [Part::Feature] Part__Feature037  label="2 PIN HEADER v002"
  Placement = pos=(-39.5031,25.4324,1.66682) rot=(1,0,0;1.57065rad)
  shape: bbox 4.93 x 2.5 x 11 mm, 62 faces (baked)
FEATURE [Part::Feature] Part__Feature038  label="2 PIN HEADER v003"
  Placement = pos=(-39.5031,22.8924,1.66718) rot=(1,0,0;1.57065rad)
  shape: bbox 4.93 x 2.5 x 11 mm, 62 faces (baked)
FEATURE [Part::Feature] Part__Feature039  label="4 PIN HEADER v001"
  Placement = pos=(-34.3918,26.7138,1.6041) rot=(-0.57735,-0.57735,0.57735;2.0944rad)
  shape: bbox 2.5 x 10.06 x 11 mm, 122 faces (baked)
FEATURE [App::Part] driver_comp
  Group = -> [stepper_socket_v7,Part__Feature034,Part__Feature035,Part__Feature036,Part__Feature037,Part__Feature038,Part__Feature039]
  Origin = -> Origin1445
FEATURE [Part::Feature] Part__Feature040  label="6 PIN HEADER v2 (1)"
  Placement = pos=(-32.7809,15.2693,1.6041) rot=(-1,0,0;1.5708rad)
  shape: bbox 15.14 x 2.5 x 11 mm, 182 faces (baked)
FEATURE [Part::Feature] Part__Feature041  label="JST XH 5 v3"
  Placement = pos=(13.9317,-30.752,1.63184) rot=(1,0,0;1.5708rad)
  shape: bbox 14.94 x 5.75 x 10.45 mm, 118 faces (baked)
FEATURE [Part::Feature] Part__Feature042  label="wifi_socket"
  Placement = pos=(11.3905,-49.722,1.64594) rot=(0,0,1;0rad)
  shape: bbox 10.29 x 5.6 x 8 mm, 38 faces (baked)
FEATURE [Part::Feature] Part__Feature043  label="Inductance"
  Placement = pos=(-17.2891,-2.35743,2.24794) rot=(2e-05,0.707107,0.707107;3.14155rad)
  shape: bbox 9.209 x 12.05 x 5.4 mm, 14 faces (baked)
FEATURE [Part::Feature] Part__Feature044  label="10 pin male socket v001"
  Placement = pos=(73.3778,37.8672,1.70938) rot=(0.57735,0.57735,0.57735;2.0944rad)
  shape: bbox 9 x 20.25 x 12.5 mm, 122 faces (baked)
FEATURE [Part::Feature] Part__Feature045  label="JST XH 2 v001"
  Placement = pos=(40.1557,-24.4368,1.66076) rot=(0,0.707107,0.707107;3.14159rad)
  shape: bbox 7.4 x 5.75 x 10.45 mm, 58 faces (baked)
FEATURE [Part::Feature] Part__Feature046  label="JST XH 2 v002"
  Placement = pos=(43.1904,-38.3795,1.66076) rot=(0,0.707107,0.707107;3.14159rad)
  shape: bbox 7.4 x 5.75 x 10.45 mm, 58 faces (baked)
FEATURE [Part::Feature] Part__Feature047  label="Power FeT 2 v001"
  Placement = pos=(-40.567,5.74518,1.56884) rot=(0.57735,0.57735,0.57735;2.0944rad)
  shape: bbox 9.028 x 6.35 x 2.021 mm, 53 faces (baked)
FEATURE [Part::Feature] Part__Feature048  label="JST XH 3 v001"
  Placement = pos=(33.535,7.8268,1.72291) rot=(0.57735,-0.57735,-0.57735;2.0944rad)
  shape: bbox 5.75 x 9.9 x 10.45 mm, 82 faces (baked)
FEATURE [Part::Feature] Part__Feature049  label="2 pole terminal block v7 v004"
  Placement = pos=(-49.2786,-27.5085,6.90822) rot=(0.57735,0.57735,0.57735;2.0944rad)
  shape: bbox 9 x 10.8 x 17.25 mm, 32 faces (baked)
FEATURE [Part::Feature] Part__Feature050  label="2 pole terminal block v7 v005"
  Placement = pos=(-49.2786,-27.5085,6.90822) rot=(0.57735,0.57735,0.57735;2.0944rad)
  shape: bbox 3 x 3 x 7.027 mm, 7 faces (baked)
FEATURE [Part::Feature] Part__Feature051  label="2 pole terminal block v7 v006"
  Placement = pos=(-49.2786,-27.5085,6.90822) rot=(0.57735,0.57735,0.57735;2.0944rad)
  shape: bbox 3 x 3 x 7.027 mm, 7 faces (baked)
FEATURE [App::Part] _2_pole_terminal_block_v7_v001  label="2 pole terminal block v7 v007"
  Group = -> [Part__Feature049,Part__Feature050,Part__Feature051]
  Origin = -> Origin1447
FEATURE [Part::Feature] Part__Feature052  label="JST XH 3 v002"
  Placement = pos=(33.535,-2.8042,1.72291) rot=(0.57735,-0.57735,-0.57735;2.0944rad)
  shape: bbox 5.75 x 9.9 x 10.45 mm, 82 faces (baked)
FEATURE [Part::Feature] Part__Feature053  label="JST XH 3 v003"
  Placement = pos=(40.776,-2.8042,1.72291) rot=(0.57735,-0.57735,-0.57735;2.0944rad)
  shape: bbox 5.75 x 9.9 x 10.45 mm, 82 faces (baked)
FEATURE [Part::Feature] Part__Feature054  label="JST XH 3 v004"
  Placement = pos=(33.535,-13.4352,1.72291) rot=(0.57735,-0.57735,-0.57735;2.0944rad)
  shape: bbox 5.75 x 9.9 x 10.45 mm, 82 faces (baked)
FEATURE [Part::Feature] Part__Feature055  label="JST XH 3 v005"
  Placement = pos=(40.776,-13.4352,1.72291) rot=(0.57735,-0.57735,-0.57735;2.0944rad)
  shape: bbox 5.75 x 9.9 x 10.45 mm, 82 faces (baked)
FEATURE [Part::Feature] Part__Feature056  label="3 PIN HEADER blk v001"
  Placement = pos=(0.582043,-23.0414,1.65998) rot=(1,0,0;1.5708rad)
  shape: bbox 7.47 x 2.5 x 11 mm, 92 faces (baked)
FEATURE [Part::Feature] Part__Feature057  label="JST XH 2 v003"
  Placement = pos=(-51.5263,14.452,1.66076) rot=(0.577366,-0.577343,-0.577343;2.09437rad)
  shape: bbox 5.75 x 7.4 x 10.45 mm, 58 faces (baked)
FEATURE [Part::Feature] Part__Feature058  label="blk power terminal v004"
  Placement = pos=(1.55908,-24.1015,1.56926) rot=(0,0,1;0rad)
  shape: bbox 7.981 x 10.42 x 8.5 mm, 34 faces (baked)
FEATURE [Part::Feature] Part__Feature059  label="blk power terminal v005"
  Placement = pos=(1.55908,-24.1015,1.56926) rot=(0,0,1;0rad)
  shape: bbox 3.327 x 3.327 x 2.918 mm, 20 faces (baked)
FEATURE [Part::Feature] Part__Feature060  label="blk power terminal v006"
  Placement = pos=(1.55908,-24.1015,1.56926) rot=(0,0,1;0rad)
  shape: bbox 3.327 x 3.327 x 2.918 mm, 22 faces (baked)
FEATURE [App::Part] blk_power_terminal_v001  label="blk power terminal v007"
  Group = -> [Part__Feature058,Part__Feature059,Part__Feature060]
  Origin = -> Origin1449
FEATURE [Part::Feature] Part__Feature061  label="Pin header jumper v003"
  Placement = pos=(27.1514,-16.0341,4.24885) rot=(0,0,-1;1.5708rad)
  shape: bbox 2.5 x 5 x 6 mm, 33 faces (baked)
FEATURE [Part::Feature] Part__Feature062  label="Pin header jumper v004"
  Placement = pos=(27.1514,-16.0341,4.24885) rot=(0,0,-1;1.5708rad)
  shape: bbox 1.5 x 4 x 2.462 mm, 22 faces (baked)
FEATURE [App::Part] Pin_header_jumper_v001  label="Pin header jumper v005"
  Group = -> [Part__Feature061,Part__Feature062]
  Origin = -> Origin1451
FEATURE [Part::Feature] Part__Feature063  label="3 PIN HEADER v001"
  Placement = pos=(27.21,-13.3596,1.07754) rot=(0.57735,-0.57735,-0.57735;2.0944rad)
  shape: bbox 2.5 x 7.47 x 11 mm, 92 faces (baked)
FEATURE [Part::Feature] Part__Feature064  label="2 PIN HEADER blk v001"
  Placement = pos=(21.842,-15.8691,1.66319) rot=(1,0,0;1.5708rad)
  shape: bbox 4.93 x 2.5 x 11 mm, 62 faces (baked)
FEATURE [Part::Feature] Part__Feature065  label="JST XH 3 v006"
  Placement = pos=(31.0455,-24.4247,1.72291) rot=(0,0.707107,0.707107;3.14159rad)
  shape: bbox 9.9 x 5.75 x 10.45 mm, 82 faces (baked)
FEATURE [Part::Feature] Part__Feature066  label="JST XH 3 v007"
  Placement = pos=(22.7955,-22.521,1.72291) rot=(0.57735,-0.57735,-0.57735;2.0944rad)
  shape: bbox 5.75 x 9.9 x 10.45 mm, 82 faces (baked)
FEATURE [Part::Feature] Part__Feature067  label="JST XH 2 v004"
  Placement = pos=(-44.1705,14.4524,1.66076) rot=(0.577335,0.577358,0.577358;2.09442rad)
  shape: bbox 5.75 x 7.4 x 10.45 mm, 58 faces (baked)
FEATURE [Part::Feature] Part__Feature068  label="2 PIN HEADER blk v002"
  Placement = pos=(-27.8621,-21.1761,1.66319) rot=(1,0,0;1.5708rad)
  shape: bbox 4.93 x 2.5 x 11 mm, 62 faces (baked)
FEATURE [Part::Feature] Part__Feature069  label="2 PIN HEADER blk v003"
  Placement = pos=(-27.8621,-23.6761,1.66319) rot=(1,0,0;1.5708rad)
  shape: bbox 4.93 x 2.5 x 11 mm, 62 faces (baked)
FEATURE [Part::Feature] Part__Feature070  label="JST XH 2 v005"
  Placement = pos=(35.1904,-38.3795,1.66076) rot=(0,0.707107,0.707107;3.14159rad)
  shape: bbox 7.4 x 5.75 x 10.45 mm, 58 faces (baked)
FEATURE [Part::Feature] Part__Feature071  label="JST XH 2 v006"
  Placement = pos=(27.1904,-38.3795,1.66076) rot=(0,0.707107,0.707107;3.14159rad)
  shape: bbox 7.4 x 5.75 x 10.45 mm, 58 faces (baked)
FEATURE [Part::Feature] Part__Feature072  label="stepper socket v004"
  Placement = pos=(-52.1915,20.2005,1.64594) rot=(0,0,1;0rad)
  shape: bbox 20.58 x 2.8 x 8 mm, 38 faces (baked)
FEATURE [Part::Feature] Part__Feature073  label="stepper socket v005"
  Placement = pos=(-52.1915,20.2005,1.64594) rot=(0,0,1;0rad)
  shape: bbox 20.58 x 2.8 x 8 mm, 38 faces (baked)
FEATURE [Part::Feature] Part__Feature074  label="stepper socket v006"
  Placement = pos=(-52.1915,20.2005,1.64594) rot=(0,0,1;0rad)
  shape: bbox 2.8 x 5.21 x 8 mm, 14 faces (baked)
FEATURE [App::Part] stepper_socket_v001  label="stepper socket v007"
  Group = -> [Part__Feature072,Part__Feature073,Part__Feature074]
  Origin = -> Origin1453
FEATURE [Part::Feature] Part__Feature075  label="2 PIN HEADER v004"
  Placement = pos=(-39.5031,30.5124,1.66609) rot=(1,0,0;1.57065rad)
  shape: bbox 4.93 x 2.5 x 11 mm, 62 faces (baked)
FEATURE [Part::Feature] Part__Feature076  label="Elco100_35 v001"
  Placement = pos=(-46.2359,28.0538,2.24794) rot=(0.57735,-0.57735,-0.57735;2.0944rad)
  shape: bbox 7 x 6.819 x 6.95 mm, 28 faces (baked)
FEATURE [Part::Feature] Part__Feature077  label="2 PIN HEADER v005"
  Placement = pos=(-39.5031,27.9724,1.66646) rot=(1,0,0;1.57065rad)
  shape: bbox 4.93 x 2.5 x 11 mm, 62 faces (baked)
FEATURE [Part::Feature] Part__Feature078  label="2 PIN HEADER v006"
  Placement = pos=(-39.5031,25.4324,1.66682) rot=(1,0,0;1.57065rad)
  shape: bbox 4.93 x 2.5 x 11 mm, 62 faces (baked)
FEATURE [Part::Feature] Part__Feature079  label="2 PIN HEADER v007"
  Placement = pos=(-39.5031,22.8924,1.66718) rot=(1,0,0;1.57065rad)
  shape: bbox 4.93 x 2.5 x 11 mm, 62 faces (baked)
FEATURE [Part::Feature] Part__Feature080  label="4 PIN HEADER v002"
  Placement = pos=(-34.3918,26.7138,1.6041) rot=(-0.57735,-0.57735,0.57735;2.0944rad)
  shape: bbox 2.5 x 10.06 x 11 mm, 122 faces (baked)
FEATURE [App::Part] driver_comp001
  Group = -> [stepper_socket_v001,Part__Feature075,Part__Feature076,Part__Feature077,Part__Feature078,Part__Feature079,Part__Feature080]
  Origin = -> Origin1455
  Placement = pos=(21.65,0,0) rot=(0,0,1;0rad)
FEATURE [Part::Feature] Part__Feature081  label="stepper socket v008"
  Placement = pos=(-52.1915,20.2005,1.64594) rot=(0,0,1;0rad)
  shape: bbox 20.58 x 2.8 x 8 mm, 38 faces (baked)
FEATURE [Part::Feature] Part__Feature082  label="stepper socket v009"
  Placement = pos=(-52.1915,20.2005,1.64594) rot=(0,0,1;0rad)
  shape: bbox 20.58 x 2.8 x 8 mm, 38 faces (baked)
FEATURE [Part::Feature] Part__Feature083  label="stepper socket v010"
  Placement = pos=(-52.1915,20.2005,1.64594) rot=(0,0,1;0rad)
  shape: bbox 2.8 x 5.21 x 8 mm, 14 faces (baked)
FEATURE [App::Part] stepper_socket_v002  label="stepper socket v011"
  Group = -> [Part__Feature081,Part__Feature082,Part__Feature083]
  Origin = -> Origin1457
FEATURE [Part::Feature] Part__Feature084  label="2 PIN HEADER v008"
  Placement = pos=(-39.5031,30.5124,1.66609) rot=(1,0,0;1.57065rad)
  shape: bbox 4.93 x 2.5 x 11 mm, 62 faces (baked)
FEATURE [Part::Feature] Part__Feature085  label="Elco100_35 v002"
  Placement = pos=(-46.2359,27.9603,2.24794) rot=(0.57735,-0.57735,-0.57735;2.0944rad)
  shape: bbox 7 x 6.819 x 6.95 mm, 28 faces (baked)
FEATURE [Part::Feature] Part__Feature086  label="2 PIN HEADER v009"
  Placement = pos=(-39.5031,27.9724,1.66646) rot=(1,0,0;1.57065rad)
  shape: bbox 4.93 x 2.5 x 11 mm, 62 faces (baked)
FEATURE [Part::Feature] Part__Feature087  label="2 PIN HEADER v010"
  Placement = pos=(-39.5031,25.4324,1.66682) rot=(1,0,0;1.57065rad)
  shape: bbox 4.93 x 2.5 x 11 mm, 62 faces (baked)
FEATURE [Part::Feature] Part__Feature088  label="2 PIN HEADER v011"
  Placement = pos=(-39.5031,22.8924,1.66718) rot=(1,0,0;1.57065rad)
  shape: bbox 4.93 x 2.5 x 11 mm, 62 faces (baked)
FEATURE [Part::Feature] Part__Feature089  label="4 PIN HEADER v003"
  Placement = pos=(-34.3918,26.7138,1.6041) rot=(-0.57735,-0.57735,0.57735;2.0944rad)
  shape: bbox 2.5 x 10.06 x 11 mm, 122 faces (baked)
FEATURE [App::Part] driver_comp002
  Group = -> [stepper_socket_v002,Part__Feature084,Part__Feature085,Part__Feature086,Part__Feature087,Part__Feature088,Part__Feature089]
  Origin = -> Origin1459
  Placement = pos=(43.3,0,0) rot=(0,0,1;0rad)
FEATURE [Part::Feature] Part__Feature090  label="stepper socket v012"
  Placement = pos=(-52.1915,20.2005,1.64594) rot=(0,0,1;0rad)
  shape: bbox 20.58 x 2.8 x 8 mm, 38 faces (baked)
FEATURE [Part::Feature] Part__Feature091  label="stepper socket v013"
  Placement = pos=(-52.1915,20.2005,1.64594) rot=(0,0,1;0rad)
  shape: bbox 20.58 x 2.8 x 8 mm, 38 faces (baked)
FEATURE [Part::Feature] Part__Feature092  label="stepper socket v014"
  Placement = pos=(-52.1915,20.2005,1.64594) rot=(0,0,1;0rad)
  shape: bbox 2.8 x 5.21 x 8 mm, 14 faces (baked)
FEATURE [App::Part] stepper_socket_v003  label="stepper socket v015"
  Group = -> [Part__Feature090,Part__Feature091,Part__Feature092]
  Origin = -> Origin1461
FEATURE [Part::Feature] Part__Feature093  label="2 PIN HEADER v012"
  Placement = pos=(-39.5031,30.5124,1.66609) rot=(1,0,0;1.57065rad)
  shape: bbox 4.93 x 2.5 x 11 mm, 62 faces (baked)
FEATURE [Part::Feature] Part__Feature094  label="Elco100_35 v003"
  Placement = pos=(-46.2587,27.9717,2.24794) rot=(0.57735,-0.57735,-0.57735;2.0944rad)
  shape: bbox 7 x 6.819 x 6.95 mm, 28 faces (baked)
FEATURE [Part::Feature] Part__Feature095  label="2 PIN HEADER v013"
  Placement = pos=(-39.5031,27.9724,1.66646) rot=(1,0,0;1.57065rad)
  shape: bbox 4.93 x 2.5 x 11 mm, 62 faces (baked)
FEATURE [Part::Feature] Part__Feature096  label="2 PIN HEADER v014"
  Placement = pos=(-39.5031,25.4324,1.66682) rot=(1,0,0;1.57065rad)
  shape: bbox 4.93 x 2.5 x 11 mm, 62 faces (baked)
FEATURE [Part::Feature] Part__Feature097  label="2 PIN HEADER v015"
  Placement = pos=(-39.5031,22.8924,1.66718) rot=(1,0,0;1.57065rad)
  shape: bbox 4.93 x 2.5 x 11 mm, 62 faces (baked)
FEATURE [Part::Feature] Part__Feature098  label="4 PIN HEADER v004"
  Placement = pos=(-34.3918,26.7138,1.6041) rot=(-0.57735,-0.57735,0.57735;2.0944rad)
  shape: bbox 2.5 x 10.06 x 11 mm, 122 faces (baked)
FEATURE [App::Part] driver_comp003
  Group = -> [stepper_socket_v003,Part__Feature093,Part__Feature094,Part__Feature095,Part__Feature096,Part__Feature097,Part__Feature098]
  Origin = -> Origin1463
  Placement = pos=(64.95,0,0) rot=(0,0,1;0rad)
FEATURE [Part::Feature] Part__Feature099  label="stepper socket v016"
  Placement = pos=(-52.1915,20.2005,1.64594) rot=(0,0,1;0rad)
  shape: bbox 20.58 x 2.8 x 8 mm, 38 faces (baked)
FEATURE [Part::Feature] Part__Feature100  label="stepper socket v017"
  Placement = pos=(-52.1915,20.2005,1.64594) rot=(0,0,1;0rad)
  shape: bbox 20.58 x 2.8 x 8 mm, 38 faces (baked)
FEATURE [Part::Feature] Part__Feature101  label="stepper socket v018"
  Placement = pos=(-52.1915,20.2005,1.64594) rot=(0,0,1;0rad)
  shape: bbox 2.8 x 5.21 x 8 mm, 14 faces (baked)
FEATURE [App::Part] stepper_socket_v004  label="stepper socket v019"
  Group = -> [Part__Feature099,Part__Feature100,Part__Feature101]
  Origin = -> Origin1465
FEATURE [Part::Feature] Part__Feature102  label="2 PIN HEADER v016"
  Placement = pos=(-39.5031,30.5124,1.66609) rot=(1,0,0;1.57065rad)
  shape: bbox 4.93 x 2.5 x 11 mm, 62 faces (baked)
FEATURE [Part::Feature] Part__Feature103  label="Elco100_35 v004"
  Placement = pos=(-46.1701,27.9069,2.24794) rot=(0.57735,-0.57735,-0.57735;2.0944rad)
  shape: bbox 7 x 6.819 x 6.95 mm, 28 faces (baked)
FEATURE [Part::Feature] Part__Feature104  label="2 PIN HEADER v017"
  Placement = pos=(-39.5031,27.9724,1.66646) rot=(1,0,0;1.57065rad)
  shape: bbox 4.93 x 2.5 x 11 mm, 62 faces (baked)
FEATURE [Part::Feature] Part__Feature105  label="2 PIN HEADER v018"
  Placement = pos=(-39.5031,25.4324,1.66682) rot=(1,0,0;1.57065rad)
  shape: bbox 4.93 x 2.5 x 11 mm, 62 faces (baked)
FEATURE [Part::Feature] Part__Feature106  label="2 PIN HEADER v019"
  Placement = pos=(-39.5031,22.8924,1.66718) rot=(1,0,0;1.57065rad)
  shape: bbox 4.93 x 2.5 x 11 mm, 62 faces (baked)
FEATURE [Part::Feature] Part__Feature107  label="4 PIN HEADER v005"
  Placement = pos=(-34.3918,26.7138,1.6041) rot=(-0.57735,-0.57735,0.57735;2.0944rad)
  shape: bbox 2.5 x 10.06 x 11 mm, 122 faces (baked)
FEATURE [App::Part] driver_comp004
  Group = -> [stepper_socket_v004,Part__Feature102,Part__Feature103,Part__Feature104,Part__Feature105,Part__Feature106,Part__Feature107]
  Origin = -> Origin1467
  Placement = pos=(86.6,0,0) rot=(0,0,1;0rad)
FEATURE [Part::Feature] Part__Feature108  label="JST XH 4 v001"
  Placement = pos=(-19.6165,38.7526,1.63184) rot=(0,0.707107,0.707107;3.14159rad)
  shape: bbox 12.4 x 5.75 x 10.45 mm, 100 faces (baked)
FEATURE [Part::Feature] Part__Feature109  label="JST XH 4 v002"
  Placement = pos=(-6.39645,38.7526,1.63184) rot=(0,0.707107,0.707107;3.14159rad)
  shape: bbox 12.4 x 5.75 x 10.45 mm, 100 faces (baked)
FEATURE [Part::Feature] Part__Feature110  label="JST XH 4 v003"
  Placement = pos=(6.82355,38.7526,1.63184) rot=(0,0.707107,0.707107;3.14159rad)
  shape: bbox 12.4 x 5.75 x 10.45 mm, 100 faces (baked)
FEATURE [Part::Feature] Part__Feature111  label="JST XH 4 v004"
  Placement = pos=(20.0435,38.7526,1.63184) rot=(0,0.707107,0.707107;3.14159rad)
  shape: bbox 12.4 x 5.75 x 10.45 mm, 100 faces (baked)
FEATURE [Part::Feature] Part__Feature112  label="JST XH 4 v005"
  Placement = pos=(33.2635,38.7526,1.63184) rot=(0,0.707107,0.707107;3.14159rad)
  shape: bbox 12.4 x 5.75 x 10.45 mm, 100 faces (baked)
FEATURE [Part::Feature] Part__Feature113  label="JST XH 2 v007"
  Placement = pos=(43.8336,38.7533,1.66076) rot=(0,0.707107,0.707107;3.14159rad)
  shape: bbox 7.4 x 5.75 x 10.45 mm, 58 faces (baked)
FEATURE [Part::Feature] Part__Feature114  label="6 PIN HEADER v2 (1)001"
  Placement = pos=(-16.5809,15.2693,1.6041) rot=(-1,0,0;1.5708rad)
  shape: bbox 15.14 x 2.5 x 11 mm, 182 faces (baked)
FEATURE [Part::Feature] Part__Feature115  label="6 PIN HEADER v2 (1)002"
  Placement = pos=(-0.380937,15.2693,1.6041) rot=(-1,0,0;1.5708rad)
  shape: bbox 15.14 x 2.5 x 11 mm, 182 faces (baked)
FEATURE [Part::Feature] Part__Feature116  label="6 PIN HEADER v2 (1)003"
  Placement = pos=(15.8191,15.2693,1.6041) rot=(-1,0,0;1.5708rad)
  shape: bbox 15.14 x 2.5 x 11 mm, 182 faces (baked)
FEATURE [Part::Feature] Part__Feature117  label="6 PIN HEADER v2 (1)004"
  Placement = pos=(32.0191,15.2693,1.6041) rot=(-1,0,0;1.5708rad)
  shape: bbox 15.14 x 2.5 x 11 mm, 182 faces (baked)
FEATURE [Part::Feature] Part__Feature118  label="4 PIN HEADER v006"
  Placement = pos=(14.3917,-23.0047,1.6041) rot=(-1,0,0;1.5708rad)
  shape: bbox 10.06 x 2.5 x 11 mm, 122 faces (baked)
FEATURE [Part::Feature] Part__Feature119  label="5 PIN HEADER v2"
  Placement = pos=(-10.8843,-0.656456,1.6041) rot=(-0.57735,-0.57735,0.57735;2.0944rad)
  shape: bbox 2.5 x 12.58 x 11 mm, 152 faces (baked)
FEATURE [App::Part] BTT_SKR_V1_4_v13  label="BTT_SKR_V1.4 v13"
  Group = -> [Part__Feature,Part__Feature001,Part__Feature002,Part__Feature003,Part__Feature004,Part__Feature005,Part__Feature006,Part__Feature007,Part__Feature008,Part__Feature009,_2_pole_terminal_block_v7_v7,Pin_header_jumper_v5,Part__Feature015,Part__Feature016,Part__Feature017,blk_power_terminal_v3,PCB_fuse_10_amp_V2_v3,PCB_fuse_20_amp_V2_v1,Part__Feature029,Part__Feature030,driver_comp,Part__Feature040,+42 more]
  Origin = -> Origin1469
  Placement = pos=(182,282,156) rot=(0.57735,-0.57735,-0.57735;4.18879rad)
FEATURE [Sketcher::SketchObject] Sketch217
  ArcFitTolerance = 1e-06
  AttachmentSupport = -> [Origin1473]
  FullyConstrained = true
  MakeInternals = false
  MapMode = 5
  Placement = pos=(0,0,0) rot=(1,0,0;1.5708rad)
  sketch-geometry (4):
    g0: LineSegment StartX=0 StartY=0 StartZ=0 EndX=139.7 EndY=0 EndZ=0
    g1: LineSegment StartX=139.7 StartY=0 StartZ=0 EndX=139.7 EndY=67.2 EndZ=0
    g2: LineSegment StartX=139.7 StartY=67.2 StartZ=0 EndX=0 EndY=67.2 EndZ=0
    g3: LineSegment StartX=0 StartY=67.2 StartZ=0 EndX=0 EndY=0 EndZ=0
  constraints (11):
    c: Coincident(g0,g1)
    c: Coincident(g1,g2)
    c: Coincident(g2,g3)
    c: Coincident(g3,g0)
    c: Horizontal(g0)
    c: Horizontal(g2)
    c: Vertical(g1)
    c: Vertical(g3)
    c: Distance(g1,g3) = 139.7
    c: Distance(g0,g2) = 67.2
    c: Coincident(g0,g-1)
FEATURE [PartDesign::Pad] Pad104
  Direction = (0,-1,0)
  Length = 50.8
  Length2 = 10
  Profile = -> Sketch217
  ReferenceAxis = -> Sketch217 [N_Axis]
  Refine = true
  Suppressed = false
  Type = 0
FEATURE [Sketcher::SketchObject] Sketch218
  ArcFitTolerance = 1e-06
  AttachmentSupport = -> [Pad104]
  ExternalGeometry = -> [Pad104]
  FullyConstrained = true
  MakeInternals = false
  MapMode = 5
  Placement = pos=(0,1.48e-14,67.2) rot=(0,0,1;0rad)
  sketch-geometry (4):
    g0: LineSegment StartX=139.7 StartY=-50.8 StartZ=0 EndX=139.7 EndY=-16.8 EndZ=0
    g1: LineSegment StartX=139.7 StartY=-16.8 StartZ=0 EndX=125.7 EndY=-16.8 EndZ=0
    g2: LineSegment StartX=125.7 StartY=-16.8 StartZ=0 EndX=125.7 EndY=-50.8 EndZ=0
    g3: LineSegment StartX=125.7 StartY=-50.8 StartZ=0 EndX=139.7 EndY=-50.8 EndZ=0
  constraints (11):
    c: Coincident(g0,g1)
    c: Coincident(g1,g2)
    c: Coincident(g2,g3)
    c: Coincident(g3,g0)
    c: Vertical(g0)
    c: Vertical(g2)
    c: Horizontal(g1)
    c: Horizontal(g3)
    c: Distance(g0,g2) = 14
    c: Distance(g1,g3) = 34
    c: Coincident(g0,g-6)
FEATURE [PartDesign::Pocket] Pocket079
  BaseFeature = -> Pad104
  Direction = (0,0,-1)
  Length = 5
  Length2 = 5
  Offset = -2
  Profile = -> Sketch218
  ReferenceAxis = -> Sketch218 [N_Axis]
  Refine = true
  Suppressed = false
  Type = 3
  UpToFace = -> Pad104 [Face1]
FEATURE [PartDesign::Body] Body131  label="Spindle PSU"
  AllowCompound = false
  Group = -> [Sketch217,Pad104,Sketch218,Pocket079]
  Origin = -> Origin1473
  Placement = pos=(28,275,109) rot=(-0.707107,0,-0.707107;3.14159rad)
  Tip = -> Pocket079
FEATURE [Sketcher::SketchObject] Sketch219
  ArcFitTolerance = 1e-06
  AttachmentSupport = -> [Origin1475]
  FullyConstrained = true
  MakeInternals = false
  MapMode = 5
  Placement = pos=(0,0,0) rot=(1,0,0;1.5708rad)
  sketch-geometry (12):
    g0: LineSegment StartX=0 StartY=0 StartZ=0 EndX=43 EndY=0 EndZ=0
    g1: LineSegment StartX=43 StartY=0 StartZ=0 EndX=43 EndY=22 EndZ=0
    g2: LineSegment StartX=43 StartY=22 StartZ=0 EndX=0 EndY=22 EndZ=0
    g3: LineSegment StartX=0 StartY=22 StartZ=0 EndX=0 EndY=0 EndZ=0
    g4: Circle CenterX=3 CenterY=19 CenterZ=0 NormalX=0 NormalY=0 NormalZ=1 AngleXU=0 Radius=1.5
    g5: Circle CenterX=3 CenterY=3 CenterZ=0 NormalX=0 NormalY=0 NormalZ=1 AngleXU=0 Radius=1.5
    g6: GeomPoint X=0 Y=11 Z=0
    g7: GeomPoint X=3 Y=11 Z=0
    g8: LineSegment [constr] StartX=3 StartY=19 StartZ=0 EndX=3 EndY=22 EndZ=0
    g9: LineSegment [constr] StartX=3 StartY=22 StartZ=0 EndX=3 EndY=19 EndZ=0
    g10: LineSegment [constr] StartX=0 StartY=19 StartZ=0 EndX=3 EndY=19 EndZ=0
    g11: LineSegment [constr] StartX=3 StartY=0 StartZ=0 EndX=3 EndY=3 EndZ=0
  constraints (31):
    c: Coincident(g0,g1)
    c: Coincident(g1,g2)
    c: Coincident(g2,g3)
    c: Coincident(g3,g0)
    c: Horizontal(g0)
    c: Horizontal(g2)
    c: Vertical(g1)
    c: Vertical(g3)
    c: Distance(g1,g3) = 43
    c: Distance(g0,g2) = 22
    c: Coincident(g0,g-1)
    c: Equal(g5,g4)
    c: Diameter(g4) = 3
    c: Vertical(g5,g4)
    c: DistanceY(g5,g4) = 16
    c: Symmetric(g3,g3,g6)
    c: Vertical(g5,g7)
    c: Horizontal(g7,g6)
    c: Coincident(g8,g4)
    c: PointOnObject(g8,g2)
    c: Vertical(g8)
    c: Coincident(g8,g9)
    c: Coincident(g9,g8)
    c: PointOnObject(g10,g3)
    c: Coincident(g10,g4)
    c: Horizontal(g10)
    c: Equal(g10,g8)
    c: PointOnObject(g11,g0)
    c: Coincident(g11,g5)
    c: Vertical(g11)
    c: Equal(g11,g8)
FEATURE [PartDesign::Pad] Pad105
  Direction = (0,-1,0)
  Length = 1.6
  Length2 = 10
  Profile = -> Sketch219
  ReferenceAxis = -> Sketch219 [N_Axis]
  Refine = true
  Suppressed = false
  Type = 0
FEATURE [Sketcher::SketchObject] Sketch220
  ArcFitTolerance = 1e-06
  AttachmentSupport = -> [Pad105]
  ExternalGeometry = -> [Pad105]
  FullyConstrained = true
  MakeInternals = false
  MapMode = 5
  Placement = pos=(0,-1.6,0) rot=(1,0,0;1.5708rad)
  sketch-geometry (13):
    g0: LineSegment StartX=0 StartY=16.08 StartZ=0 EndX=0 EndY=5.92 EndZ=0
    g1: LineSegment StartX=0 StartY=5.92 StartZ=0 EndX=6 EndY=5.92 EndZ=0
    g2: LineSegment StartX=6 StartY=5.92 StartZ=0 EndX=6 EndY=16.08 EndZ=0
    g3: LineSegment StartX=6 StartY=16.08 StartZ=0 EndX=0 EndY=16.08 EndZ=0
    g4: GeomPoint X=0 Y=11 Z=0
    g5: LineSegment StartX=43 StartY=22 StartZ=0 EndX=37 EndY=22 EndZ=0
    g6: LineSegment StartX=37 StartY=22 StartZ=0 EndX=37 EndY=11.84 EndZ=0
    g7: LineSegment StartX=37 StartY=11.84 StartZ=0 EndX=43 EndY=11.84 EndZ=0
    g8: LineSegment StartX=43 StartY=11.84 StartZ=0 EndX=43 EndY=22 EndZ=0
    g9: LineSegment StartX=43 StartY=4e-16 StartZ=0 EndX=43 EndY=10.16 EndZ=0
    g10: LineSegment StartX=43 StartY=10.16 StartZ=0 EndX=37 EndY=10.16 EndZ=0
    g11: LineSegment StartX=37 StartY=10.16 StartZ=0 EndX=37 EndY=0 EndZ=0
    g12: LineSegment StartX=37 StartY=4e-16 StartZ=0 EndX=43 EndY=4e-16 EndZ=0
  constraints (34):
    c: Coincident(g0,g1)
    c: Coincident(g1,g2)
    c: Coincident(g2,g3)
    c: Coincident(g3,g0)
    c: Vertical(g0)
    c: Vertical(g2)
    c: Horizontal(g1)
    c: Horizontal(g3)
    c: Distance(g0,g2) = 6
    c: Distance(g1,g3) = 10.16
    c: Symmetric(g0,g0,g4)
    c: Symmetric(g-6,g-6,g4)
    c: Coincident(g5,g6)
    c: Coincident(g6,g7)
    c: Coincident(g7,g8)
    c: Coincident(g8,g5)
    c: Horizontal(g5)
    c: Horizontal(g7)
    c: Vertical(g6)
    c: Vertical(g8)
    c: Coincident(g5,g-5)
    c: Coincident(g9,g10)
    c: Coincident(g10,g11)
    c: Coincident(g11,g12)
    c: Coincident(g12,g9)
    c: Vertical(g9)
    c: Vertical(g11)
    c: Horizontal(g10)
    c: Horizontal(g12)
    c: Coincident(g9,g-4)
    c: Equal(g11,g6)
    c: Equal(g6,g2)
    c: Equal(g10,g7)
    c: Equal(g7,g3)
FEATURE [PartDesign::Pad] Pad106
  BaseFeature = -> Pad105
  Direction = (0,-1,0)
  Length = 10
  Length2 = 10
  Profile = -> Sketch220
  ReferenceAxis = -> Sketch220 [N_Axis]
  Refine = true
  Suppressed = false
  Type = 0
FEATURE [Part::Feature] Part__Feature120  label="LRS-150-24"
  Placement = pos=(-155,275,214) rot=(0,0,1;0rad)
  shape: bbox 160 x 30.53 x 97 mm, 2550 faces (baked)
FEATURE [PartDesign::ShapeBinder] CopyPocket079
  TraceSupport = false
FEATURE [Sketcher::SketchObject] Sketch221
  ArcFitTolerance = 1e-06
  AttachmentSupport = -> [CopyPocket079]
  FullyConstrained = true
  MakeInternals = false
  MapMode = 5
  Placement = pos=(0,-16.8,0) rot=(1,0,0;1.5708rad)
FEATURE [PartDesign::Body] Body132  label="PWM to Mach3"
  AllowCompound = false
  Group = -> [Sketch219,Pad105,Sketch220,Pad106,CopyPocket079,Sketch221]
  Origin = -> Origin1475
  Placement = pos=(131,282,210) rot=(0.707107,0,-0.707107;3.14159rad)
  Tip = -> Pad106
FEATURE [Part::FeaturePython] Screw154  label="M3x8-Screw019"  # WARN: FeaturePython — macro-defined, semantics opaque (R4)
  Diameter = 4
  Invert = false
  LeftHanded = false
  Length = 2
  LengthCustom = 8
  MatchOuter = false
  OffsetAngle = 0
  Placement = pos=(3,276,208) rot=(1,0,0;4.71239rad)
  Thread = false
  Type = 75
FEATURE [Part::FeaturePython] Screw155  label="M3x8-Screw020"  # WARN: FeaturePython — macro-defined, semantics opaque (R4)
  Diameter = 4
  Invert = false
  LeftHanded = false
  Length = 2
  LengthCustom = 8
  MatchOuter = false
  OffsetAngle = 0
  Placement = pos=(-151,276,123) rot=(1,0,0;4.71239rad)
  Thread = false
  Type = 75
FEATURE [Sketcher::SketchObject] Sketch222
  ArcFitTolerance = 1e-06
  AttachmentSupport = -> [Origin1479]
  FullyConstrained = true
  MakeInternals = false
  MapMode = 5
  Placement = pos=(0,0,0) rot=(1,0,0;1.5708rad)
  sketch-geometry (6):
    g0: LineSegment StartX=0 StartY=0 StartZ=0 EndX=0 EndY=115 EndZ=0
    g1: LineSegment StartX=0 StartY=115 StartZ=0 EndX=120 EndY=115 EndZ=0
    g2: LineSegment StartX=120 StartY=115 StartZ=0 EndX=120 EndY=75 EndZ=0
    g3: LineSegment StartX=120 StartY=75 StartZ=0 EndX=20 EndY=75 EndZ=0
    g4: LineSegment StartX=20 StartY=75 StartZ=0 EndX=20 EndY=0 EndZ=0
    g5: LineSegment StartX=20 StartY=0 StartZ=0 EndX=0 EndY=0 EndZ=0
  constraints (17):
    c: Coincident(g-1,g0)
    c: PointOnObject(g0,g-2)
    c: Coincident(g0,g1)
    c: Horizontal(g1)
    c: Coincident(g1,g2)
    c: Vertical(g2)
    c: Coincident(g2,g3)
    c: Horizontal(g3)
    c: Coincident(g3,g4)
    c: Vertical(g4)
    c: Coincident(g4,g5)
    c: Coincident(g5,g0)
    c: Horizontal(g5)
    c: DistanceX(g5,g5) = 20
    c: DistanceY(g2,g2) = 40
    c: DistanceX(g1,g1) = 120
    c: DistanceY(g0,g0) = 115
FEATURE [PartDesign::Pad] Pad107
  Direction = (0,-1,2e-16)
  Length = 2
  Length2 = 10
  Profile = -> Sketch222
  ReferenceAxis = -> Sketch222 [N_Axis]
  Refine = true
  Suppressed = false
  Type = 0
FEATURE [Sketcher::SketchObject] Sketch223
  ArcFitTolerance = 1e-06
  AttachmentSupport = -> [Pad107]
  ExternalGeometry = -> [Pad107]
  FullyConstrained = true
  MakeInternals = false
  MapMode = 5
  Placement = pos=(0,-2,0) rot=(1,0,0;1.5708rad)
  sketch-geometry (5):
    g0: Circle CenterX=6 CenterY=109 CenterZ=0 NormalX=0 NormalY=0 NormalZ=1 AngleXU=0 Radius=3
    g1: Circle CenterX=6 CenterY=7.15 CenterZ=0 NormalX=0 NormalY=0 NormalZ=1 AngleXU=0 Radius=3
    g2: Circle CenterX=98 CenterY=109 CenterZ=0 NormalX=0 NormalY=0 NormalZ=1 AngleXU=0 Radius=3
    g3: Circle CenterX=82.1 CenterY=109 CenterZ=0 NormalX=0 NormalY=0 NormalZ=1 AngleXU=0 Radius=3
    g4: Circle CenterX=114 CenterY=109 CenterZ=0 NormalX=0 NormalY=0 NormalZ=1 AngleXU=0 Radius=3
  constraints (15):
    c: Equal(g2,g4)
    c: Equal(g4,g3)
    c: Equal(g3,g0)
    c: Equal(g0,g1)
    c: Diameter(g0) = 6
    c: Horizontal(g3,g0)
    c: Horizontal(g2,g4)
    c: Horizontal(g4,g3)
    c: Vertical(g1,g0)
    c: Distance(g0,g1) = 101.85
    c: DistanceX(g0,g3) = 76.1
    c: Distance(g0,g-4) = 6
    c: DistanceX(g-1,g0) = 6
    c: DistanceX(g2,g4) = 16
    c: Distance(g4,g-5) = 6
FEATURE [PartDesign::Pad] Pad108
  BaseFeature = -> Pad107
  Direction = (0,-1,2e-16)
  Length = 5
  Length2 = 10
  Profile = -> Sketch223
  ReferenceAxis = -> Sketch223 [N_Axis]
  Refine = true
  Suppressed = false
  Type = 0
FEATURE [PartDesign::Hole] Hole042
  BaseFeature = -> Pad108
  CustomThreadClearance = 0
  Depth = 336.037
  DepthType = 1
  Diameter = 4.7
  DrillForDepth = false
  DrillPoint = 1
  DrillPointAngle = 118
  HoleCutCountersinkAngle = 90
  HoleCutCustomValues = false
  HoleCutDepth = 0
  HoleCutDiameter = 0
  HoleCutType = 0
  ModelThread = false
  Profile = -> Pad108 [Face15,Face16,Face17,Face18,Face14]
  Refine = true
  Suppressed = false
  Tapered = false
  TaperedAngle = 90
  ThreadClass = 0
  ThreadDepth = 336.037
  ThreadDepthType = 0
  ThreadDirection = 0
  ThreadFit = 0
  ThreadSize = 0
  ThreadType = 0
  Threaded = false
  UseCustomThreadClearance = false
FEATURE [PartDesign::Body] Body133  label="PCB Support"
  AllowCompound = false
  Group = -> [Sketch222,Pad107,Sketch223,Pad108,Hole042]
  Origin = -> Origin1479
  Placement = pos=(226,275,98) rot=(0,0,1;3.14159rad)
  Tip = -> Hole042
FEATURE [Part::FeaturePython] Screw156  label="M3x12-Screw008"  # WARN: FeaturePython — macro-defined, semantics opaque (R4)
  Diameter = 4
  Invert = false
  LeftHanded = false
  Length = 4
  LengthCustom = 12
  MatchOuter = false
  OffsetAngle = 0
  Placement = pos=(220,284,207) rot=(1,0,0;-1.5708rad)
  Thread = false
  Type = 75
FEATURE [Part::FeaturePython] Screw157  label="M3x12-Screw014"  # WARN: FeaturePython — macro-defined, semantics opaque (R4)
  Diameter = 4
  Invert = false
  LeftHanded = false
  Length = 4
  LengthCustom = 12
  MatchOuter = false
  OffsetAngle = 0
  Placement = pos=(112,284,207) rot=(1,0,0;4.71239rad)
  Thread = false
  Type = 75
FEATURE [Part::FeaturePython] Screw158  label="M3x12-Screw012"  # WARN: FeaturePython — macro-defined, semantics opaque (R4)
  Diameter = 4
  Invert = false
  LeftHanded = false
  Length = 4
  LengthCustom = 12
  MatchOuter = false
  OffsetAngle = 0
  Placement = pos=(144,284,207) rot=(1,0,0;4.71239rad)
  Thread = false
  Type = 75
FEATURE [Part::FeaturePython] Screw159  label="M3x12-Screw013"  # WARN: FeaturePython — macro-defined, semantics opaque (R4)
  Diameter = 4
  Invert = false
  LeftHanded = false
  Length = 4
  LengthCustom = 12
  MatchOuter = false
  OffsetAngle = 0
  Placement = pos=(128,284,207) rot=(1,0,0;4.71239rad)
  Thread = false
  Type = 75
FEATURE [Part::FeaturePython] Screw160  label="M3x12-Screw011"  # WARN: FeaturePython — macro-defined, semantics opaque (R4)
  Diameter = 4
  Invert = false
  LeftHanded = false
  Length = 4
  LengthCustom = 12
  MatchOuter = false
  OffsetAngle = 0
  Placement = pos=(220,284,105) rot=(1,0,0;4.71239rad)
  Thread = false
  Type = 75
FEATURE [App::Part] Part026  label="Screws005"
  Group = -> [Screw154,Screw155,Screw160,Screw158,Screw156,Screw159,Screw157]
  Origin = -> Origin1477
FEATURE [PartDesign::ShapeBinder] CopyLinearPattern011
  TraceSupport = false
FEATURE [Sketcher::SketchObject] Sketch224
  ArcFitTolerance = 1e-06
  AttachmentSupport = -> [CopyLinearPattern011]
  ExternalGeometry = -> [CopyLinearPattern011]
  FullyConstrained = true
  MakeInternals = false
  MapMode = 5
  Placement = pos=(0,240,0) rot=(0,0.707107,0.707107;3.14159rad)
  sketch-geometry (10):
    g0: LineSegment StartX=10 StartY=3.1 StartZ=0 EndX=10 EndY=-3.1 EndZ=0
    g1: LineSegment StartX=10 StartY=3.1 StartZ=0 EndX=8 EndY=3.1 EndZ=0
    g2: LineSegment StartX=8 StartY=3.1 StartZ=0 EndX=8 EndY=5.5 EndZ=0
    g3: LineSegment StartX=8 StartY=5.5 StartZ=0 EndX=6.3 EndY=5.5 EndZ=0
    g4: LineSegment StartX=6.3 StartY=5.5 StartZ=0 EndX=3.9 EndY=3.1 EndZ=0
    g5: LineSegment StartX=3.9 StartY=3.1 StartZ=0 EndX=3.9 EndY=-3.1 EndZ=0
    g6: LineSegment StartX=3.9 StartY=-3.1 StartZ=0 EndX=6.3 EndY=-5.5 EndZ=0
    g7: LineSegment StartX=6.3 StartY=-5.5 StartZ=0 EndX=8 EndY=-5.5 EndZ=0
    g8: LineSegment StartX=8 StartY=-5.5 StartZ=0 EndX=8 EndY=-3.1 EndZ=0
    g9: LineSegment StartX=8 StartY=-3.1 StartZ=0 EndX=10 EndY=-3.1 EndZ=0
  constraints (21):
    c: Coincident(g0,g-3)
    c: Coincident(g0,g-11)
    c: Coincident(g0,g1)
    c: Coincident(g1,g-4)
    c: Coincident(g1,g2)
    c: Coincident(g2,g-5)
    c: Coincident(g2,g3)
    c: Coincident(g3,g-6)
    c: Coincident(g3,g4)
    c: Coincident(g4,g-7)
    c: Coincident(g4,g5)
    c: Coincident(g5,g-8)
    c: Coincident(g5,g6)
    c: Coincident(g6,g-9)
    c: Coincident(g6,g7)
    c: Horizontal(g7)
    c: Coincident(g7,g8)
    c: Coincident(g8,g-11)
    c: Vertical(g8)
    c: Coincident(g8,g9)
    c: Coincident(g9,g0)
FEATURE [PartDesign::Body] Body135  label="Body"
  AllowCompound = false
  Origin = -> Origin1481
FEATURE [App::Part] Part025  label="Electronics"
  Group = -> [Body131,Body132,BTT_SKR_V1_4_v13,Part__Feature120,Part026,Body133,Body135]
  Origin = -> Origin1431
FEATURE [PartDesign::Pad] Pad109
  Direction = (0,1,-2e-16)
  Length = 10
  Length2 = 10
  Profile = -> Sketch224
  ReferenceAxis = -> Sketch224 [N_Axis]
  Refine = true
  Suppressed = false
  Type = 0
FEATURE [Sketcher::SketchObject] Sketch225
  ArcFitTolerance = 1e-06
  AttachmentSupport = -> [Pad109]
  ExternalGeometry = -> [Pad109]
  FullyConstrained = true
  MakeInternals = false
  MapMode = 5
  Placement = pos=(0,240,0) rot=(1,0,0;1.5708rad)
  sketch-geometry (14):
    g0: LineSegment StartX=-8 StartY=5.1 StartZ=0 EndX=-8 EndY=5.5 EndZ=0
    g1: LineSegment StartX=-8 StartY=5.5 StartZ=0 EndX=-6.3 EndY=5.5 EndZ=0
    g2: LineSegment StartX=-6.3 StartY=5.5 StartZ=0 EndX=-3.9 EndY=3.1 EndZ=0
    g3: LineSegment StartX=-3.9 StartY=3.1 StartZ=0 EndX=-3.9 EndY=-3.1 EndZ=0
    g4: LineSegment StartX=-3.9 StartY=-3.1 StartZ=0 EndX=-6.3 EndY=-5.5 EndZ=0
    g5: LineSegment StartX=-6.3 StartY=-5.5 StartZ=0 EndX=-8 EndY=-5.5 EndZ=0
    g6: LineSegment StartX=-8 StartY=-5.5 StartZ=0 EndX=-8 EndY=-5.1 EndZ=0
    g7: LineSegment StartX=-8 StartY=-5.1 StartZ=0 EndX=-6.46569 EndY=-5.1 EndZ=0
    g8: LineSegment StartX=-6.46569 StartY=-5.1 StartZ=0 EndX=-4.3 EndY=-2.93431 EndZ=0
    g9: LineSegment StartX=-4.3 StartY=-2.93431 StartZ=0 EndX=-4.3 EndY=2.93431 EndZ=0
    g10: LineSegment StartX=-4.3 StartY=2.93431 StartZ=0 EndX=-6.46569 EndY=5.1 EndZ=0
    g11: LineSegment StartX=-6.46569 StartY=5.1 StartZ=0 EndX=-8 EndY=5.1 EndZ=0
    g12: LineSegment [constr] StartX=-5.38284 StartY=4.01716 StartZ=0 EndX=-5.1 EndY=4.3 EndZ=0
    g13: LineSegment [constr] StartX=-4.3 StartY=1e-15 StartZ=0 EndX=-3.9 EndY=1e-16 EndZ=0
  constraints (35):
    c: PointOnObject(g0,g-3)
    c: Coincident(g0,g-4)
    c: Coincident(g0,g1)
    c: Coincident(g1,g-5)
    c: Coincident(g1,g2)
    c: Coincident(g2,g-6)
    c: Coincident(g2,g3)
    c: Coincident(g3,g-7)
    c: Coincident(g3,g4)
    c: Coincident(g4,g-8)
    c: Coincident(g4,g5)
    c: Coincident(g5,g-9)
    c: Coincident(g5,g6)
    c: PointOnObject(g6,g-9)
    c: Coincident(g6,g7)
    c: Horizontal(g7)
    c: Coincident(g7,g8)
    c: Coincident(g8,g9)
    c: Vertical(g9)
    c: Coincident(g9,g10)
    c: Coincident(g10,g11)
    c: Coincident(g11,g0)
    c: Horizontal(g11)
    c: Equal(g11,g7)
    c: Equal(g8,g10)
    c: Angle(g8,g7) = 2.35619
    c: Equal(g6,g0)
    c: Distance(g0,g0) = 0.4
    c: PointOnObject(g12,g10)
    c: Symmetric(g2,g2,g12)
    c: Perpendicular(g2,g12)
    c: Symmetric(g9,g9,g13)
    c: Symmetric(g3,g3,g13)
    c: Equal(g13,g12)
    c: Equal(g12,g0)
FEATURE [PartDesign::Pocket] Pocket080
  BaseFeature = -> Pad109
  Direction = (0,1,-2e-16)
  Length = 5
  Length2 = 5
  Profile = -> Sketch225
  ReferenceAxis = -> Sketch225 [N_Axis]
  Refine = true
  Suppressed = false
  Type = 1
FEATURE [Sketcher::SketchObject] Sketch226
  ArcFitTolerance = 1e-06
  AttachmentSupport = -> [Pocket080]
  ExternalGeometry = -> [Pocket080]
  FullyConstrained = true
  MakeInternals = false
  MapMode = 5
  Placement = pos=(-10,0,0) rot=(0.57735,-0.57735,-0.57735;2.0944rad)
  sketch-geometry (2):
    g0: GeomPoint X=-245 Y=0 Z=0
    g1: Circle CenterX=-245 CenterY=0 CenterZ=0 NormalX=0 NormalY=0 NormalZ=1 AngleXU=0 Radius=2.125
  constraints (3):
    c: Symmetric(g-3,g-4,g0)
    c: Diameter(g1) = 4.25
    c: Coincident(g1,g0)
FEATURE [PartDesign::Pocket] Pocket081
  BaseFeature = -> Pocket080
  Direction = (1,0,0)
  Length = 10
  Length2 = 5
  Profile = -> Sketch226
  ReferenceAxis = -> Sketch226 [N_Axis]
  Refine = true
  Suppressed = false
  TaperAngle = -5
  Type = 0
FEATURE [PartDesign::Pad] Pad110
  BaseFeature = -> Pocket081
  Direction = (0,-1,0)
  Length = 5
  Length2 = 10
  Profile = -> Pocket081 [Face3]
  Refine = true
  Suppressed = false
  Type = 0
FEATURE [PartDesign::Pad] Pad111
  BaseFeature = -> Pad110
  Direction = (0,1,0)
  Length = 5
  Length2 = 10
  Profile = -> Pad110 [Face1]
  Refine = true
  Suppressed = false
  Type = 0
FEATURE [PartDesign::LinearPattern] LinearPattern013
  BaseFeature = -> Pad111
  Direction = -> Y_Axis1071
  Length = 60
  Mode = 1
  Occurrences = 4
  Offset = 20
  Refine = true
  Suppressed = false
  TransformMode = 1
FEATURE [Sketcher::SketchObject] Sketch227
  ArcFitTolerance = 1e-06
  AttachmentSupport = -> [LinearPattern013]
  ExternalGeometry = -> [LinearPattern013]
  FullyConstrained = true
  MakeInternals = false
  MapMode = 5
  Placement = pos=(0,235,0) rot=(1,0,0;1.5708rad)
  sketch-geometry (5):
    g0: LineSegment StartX=-10 StartY=7.5 StartZ=0 EndX=-10 EndY=-7.5 EndZ=0
    g1: LineSegment StartX=-10 StartY=-7.5 StartZ=0 EndX=-4.3 EndY=-7.5 EndZ=0
    g2: LineSegment StartX=-4.3 StartY=-7.5 StartZ=0 EndX=-4.3 EndY=7.5 EndZ=0
    g3: LineSegment StartX=-4.3 StartY=7.5 StartZ=0 EndX=-10 EndY=7.5 EndZ=0
    g4: GeomPoint X=-10 Y=0 Z=0
  constraints (13):
    c: Coincident(g0,g1)
    c: Coincident(g1,g2)
    c: Coincident(g2,g3)
    c: Coincident(g3,g0)
    c: Vertical(g0)
    c: Vertical(g2)
    c: Horizontal(g1)
    c: Horizontal(g3)
    c: DistanceY(g0,g0) = 15
    c: PointOnObject(g-3,g2)
    c: Symmetric(g0,g0,g4)
    c: PointOnObject(g4,g-1)
    c: PointOnObject(g-4,g0)
FEATURE [PartDesign::Pad] Pad112
  BaseFeature = -> LinearPattern013
  Direction = (0,-1,2e-16)
  Length = 5
  Length2 = 10
  Profile = -> Sketch227
  ReferenceAxis = -> Sketch227 [N_Axis]
  Refine = true
  Suppressed = false
  Type = 0
FEATURE [PartDesign::Body] Body134  label="DrillMarker1"
  AllowCompound = false
  Group = -> [CopyLinearPattern011,Sketch224,Pad109,Sketch225,Pocket080,Sketch226,Pocket081,Pad110,Pad111,LinearPattern013,Sketch227,Pad112]
  Origin = -> Origin1480
  Placement = pos=(-150,265,468) rot=(1,0,0;4.71239rad)
  Tip = -> Pad112
FEATURE [Measure::MeasureRadius] Radius  label="Radius: 1.63 mm"
  Element = -> Body134 [Pocket081.Edge27]
  Radius = 1.62631
FEATURE [App::DocumentObjectGroup] Measurements
  Group = -> [Radius]
FEATURE [Sketcher::SketchObject] Sketch228
  ArcFitTolerance = 1e-06
  AttachmentSupport = -> [YZ_Plane1073]
  FullyConstrained = true
  MakeInternals = false
  MapMode = 5
  Placement = pos=(0,0,0) rot=(0.57735,0.57735,0.57735;2.0944rad)
  sketch-geometry (12):
    g0: LineSegment StartX=-7.75 StartY=11.45 StartZ=0 EndX=-7.75 EndY=15.45 EndZ=0
    g1: LineSegment StartX=-7.75 StartY=15.45 StartZ=0 EndX=22.25 EndY=15.45 EndZ=0
    g2: LineSegment StartX=22.25 StartY=15.45 StartZ=0 EndX=22.25 EndY=11.45 EndZ=0
    g3: LineSegment StartX=22.25 StartY=11.45 StartZ=0 EndX=11.25 EndY=11.45 EndZ=0
    g4: LineSegment StartX=11.25 StartY=11.45 StartZ=0 EndX=11.25 EndY=7.15 EndZ=0
    g5: LineSegment StartX=11.25 StartY=7.15 StartZ=0 EndX=14.5 EndY=7.15 EndZ=0
    g6: LineSegment StartX=14.5 StartY=7.15 StartZ=0 EndX=14.5 EndY=0 EndZ=0
    g7: LineSegment StartX=14.5 StartY=0 StartZ=0 EndX=0 EndY=0 EndZ=0
    g8: LineSegment StartX=0 StartY=0 StartZ=0 EndX=0 EndY=7.15 EndZ=0
    g9: LineSegment StartX=0 StartY=7.15 StartZ=0 EndX=3.25 EndY=7.15 EndZ=0
    g10: LineSegment StartX=3.25 StartY=7.15 StartZ=0 EndX=3.25 EndY=11.45 EndZ=0
    g11: LineSegment StartX=3.25 StartY=11.45 StartZ=0 EndX=-7.75 EndY=11.45 EndZ=0
  constraints (35):
    c: Coincident(g0,g1)
    c: Horizontal(g1)
    c: Coincident(g1,g2)
    c: Vertical(g2)
    c: Coincident(g2,g3)
    c: Horizontal(g3)
    c: Coincident(g3,g4)
    c: Vertical(g4)
    c: Coincident(g4,g5)
    c: Horizontal(g5)
    c: Coincident(g5,g6)
    c: Vertical(g6)
    c: Coincident(g6,g7)
    c: Horizontal(g7)
    c: Coincident(g7,g8)
    c: Vertical(g8)
    c: Coincident(g8,g9)
    c: Coincident(g9,g10)
    c: Vertical(g10)
    c: Coincident(g10,g11)
    c: Coincident(g11,g0)
    c: Horizontal(g11)
    c: Horizontal(g9)
    c: Vertical(g0)
    c: Equal(g0,g2)
    c: Equal(g3,g11)
    c: Equal(g10,g4)
    c: Equal(g5,g9)
    c: DistanceX(g10,g3) = 8
    c: Distance(g8,g8) = 7.15
    c: DistanceY(g10,g10) = 4.3
    c: Distance(g0,g0) = 4
    c: Coincident(g-1,g7)
    c: DistanceX(g7,g7) = 14.5
    c: DistanceX(g1,g1) = 30
FEATURE [PartDesign::Pad] Pad113
  Direction = (1,0,0)
  Length = 85
  Length2 = 10
  Placement = pos=(0,0,0) rot=(1,1,1;2.0944rad)
  Profile = -> Sketch228
  ReferenceAxis = -> Sketch228 [N_Axis]
  Refine = true
  Suppressed = false
  Type = 0
FEATURE [Sketcher::SketchObject] Sketch229
  ArcFitTolerance = 1e-06
  AttachmentSupport = -> [Pad113]
  ExternalGeometry = -> [Pad113]
  FullyConstrained = false
  MakeInternals = false
  MapMode = 5
  Placement = pos=(0,3.4e-15,15.45) rot=(0,0,-1;1.5708rad)
  sketch-geometry (13):
    g0: GeomPoint X=-19.75 Y=77.5 Z=0
    g1: GeomPoint X=5.25 Y=77.5 Z=0
    g2: GeomPoint X=-19.75 Y=52.5 Z=0
    g3: GeomPoint X=5.25 Y=52.5 Z=0
    g4: GeomPoint [constr] X=-7.25 Y=85 Z=0
    g5: GeomPoint [constr] X=-7.25 Y=77.5 Z=0
    g6: Circle [constr] CenterX=-19.75 CenterY=52.5 CenterZ=0 NormalX=0 NormalY=0 NormalZ=1 AngleXU=0 Radius=2.76539
    g7: GeomPoint [constr] X=-19.8387 Y=247.482 Z=0
    g8: GeomPoint [constr] X=-21.1928 Y=299.991 Z=0
    g9: Circle CenterX=-19.75 CenterY=77.5 CenterZ=0 NormalX=0 NormalY=0 NormalZ=1 AngleXU=0 Radius=1.5
    g10: Circle CenterX=-19.75 CenterY=52.5 CenterZ=0 NormalX=0 NormalY=0 NormalZ=1 AngleXU=0 Radius=1.5
    g11: Circle CenterX=5.25 CenterY=52.5 CenterZ=0 NormalX=0 NormalY=0 NormalZ=1 AngleXU=0 Radius=1.5
    g12: Circle CenterX=5.25 CenterY=77.5 CenterZ=0 NormalX=0 NormalY=0 NormalZ=1 AngleXU=0 Radius=1.5
  constraints (19):
    c: Vertical(g1,g3)
    c: Vertical(g0,g2)
    c: Horizontal(g0,g1)
    c: Horizontal(g2,g3)
    c: DistanceY(g3,g1) = 25
    c: DistanceX(g0,g1) = 25
    c: Symmetric(g-3,g-3,g4)
    c: Vertical(g4,g5)
    c: Symmetric(g0,g1,g5)
    c: Coincident(g6,g2)
    c: DistanceY(g-1,g2) = 52.5
    c: Coincident(g9,g0)
    c: Coincident(g10,g2)
    c: Coincident(g11,g3)
    c: Coincident(g12,g1)
    c: Equal(g12,g9)
    c: Equal(g9,g10)
    c: Equal(g10,g11)
    c: Diameter(g9) = 3
FEATURE [PartDesign::Pocket] Pocket082
  BaseFeature = -> Pad113
  Direction = (0,0,-1)
  Length = 5
  Length2 = 5
  Placement = pos=(0,0,0) rot=(1,1,1;2.0944rad)
  Profile = -> Sketch229
  ReferenceAxis = -> Sketch229 [N_Axis]
  Refine = true
  Suppressed = false
  Type = 1
FEATURE [Sketcher::SketchObject] Sketch230
  ArcFitTolerance = 1e-06
  AttachmentSupport = -> [Pocket082]
  ExternalGeometry = -> [Pocket082]
  FullyConstrained = true
  MakeInternals = false
  MapMode = 5
  Placement = pos=(0,0,0) rot=(0.57735,0.57735,-0.57735;4.18879rad)
  sketch-geometry (4):
    g0: LineSegment StartX=22.25 StartY=-15.45 StartZ=0 EndX=22.25 EndY=0 EndZ=0
    g1: LineSegment StartX=22.25 StartY=0 StartZ=0 EndX=-7.75 EndY=0 EndZ=0
    g2: LineSegment StartX=-7.75 StartY=0 StartZ=0 EndX=-7.75 EndY=-15.45 EndZ=0
    g3: LineSegment StartX=-7.75 StartY=-15.45 StartZ=0 EndX=22.25 EndY=-15.45 EndZ=0
  constraints (10):
    c: Coincident(g0,g1)
    c: Coincident(g1,g2)
    c: Coincident(g2,g3)
    c: Coincident(g3,g0)
    c: Vertical(g0)
    c: Vertical(g2)
    c: Horizontal(g1)
    c: Coincident(g0,g-3)
    c: PointOnObject(g1,g-1)
    c: Coincident(g-3,g2)
FEATURE [PartDesign::Pad] Pad114
  BaseFeature = -> Pocket082
  Direction = (-1,0,0)
  Length = 4
  Length2 = 10
  Placement = pos=(0,0,0) rot=(1,1,1;2.0944rad)
  Profile = -> Sketch230
  ReferenceAxis = -> Sketch230 [N_Axis]
  Refine = true
  Suppressed = false
  Type = 0
FEATURE [PartDesign::Body] Body136  label="DrillMarker2"
  AllowCompound = false
  Group = -> [Sketch228,Pad113,Sketch229,Pocket082,Sketch230,Pad114]
  Origin = -> Origin1482
  Placement = pos=(-115,165.8,7) rot=(0,0,1;0rad)
  Tip = -> Pad114
FEATURE [PartDesign::ShapeBinder] CopyPad114
  Placement = pos=(85,-5.66e-14,2.83e-14) rot=(0,0,1;0rad)
  TraceSupport = false
FEATURE [Sketcher::SketchObject] Sketch231
  ArcFitTolerance = 1e-06
  AttachmentSupport = -> [CopyPad114]
  ExternalGeometry = -> [CopyPad114]
  FullyConstrained = true
  MakeInternals = false
  MapMode = 5
  Placement = pos=(85,-5.66e-14,2.83e-14) rot=(0.57735,0.57735,0.57735;2.0944rad)
  sketch-geometry (12):
    g0: LineSegment StartX=4.45 StartY=6.15 StartZ=0 EndX=2.45 EndY=6.15 EndZ=0
    g1: LineSegment StartX=2.45 StartY=6.15 StartZ=0 EndX=2.45 EndY=2.9 EndZ=0
    g2: LineSegment StartX=2.45 StartY=2.9 StartZ=0 EndX=12.05 EndY=2.9 EndZ=0
    g3: LineSegment StartX=12.05 StartY=2.9 StartZ=0 EndX=12.05 EndY=6.15 EndZ=0
    g4: LineSegment StartX=12.05 StartY=6.15 StartZ=0 EndX=10.05 EndY=6.15 EndZ=0
    g5: LineSegment StartX=14.5 StartY=7.15 StartZ=0 EndX=14.5 EndY=0 EndZ=0
    g6: LineSegment StartX=14.5 StartY=0 StartZ=0 EndX=0 EndY=0 EndZ=0
    g7: LineSegment StartX=0 StartY=0 StartZ=0 EndX=0 EndY=7.15 EndZ=0
    g8: LineSegment StartX=0 StartY=7.15 StartZ=0 EndX=4.45 EndY=7.15 EndZ=0
    g9: LineSegment StartX=4.45 StartY=7.15 StartZ=0 EndX=4.45 EndY=6.15 EndZ=0
    g10: LineSegment StartX=10.05 StartY=6.15 StartZ=0 EndX=10.05 EndY=7.15 EndZ=0
    g11: LineSegment StartX=10.05 StartY=7.15 StartZ=0 EndX=14.5 EndY=7.15 EndZ=0
  constraints (32):
    c: Horizontal(g0)
    c: Coincident(g0,g1)
    c: Vertical(g1)
    c: Coincident(g1,g2)
    c: Horizontal(g2)
    c: Coincident(g2,g3)
    c: Vertical(g3)
    c: Coincident(g3,g4)
    c: Horizontal(g4)
    c: Coincident(g5,g-4)
    c: Coincident(g5,g6)
    c: Coincident(g6,g-1)
    c: Coincident(g6,g7)
    c: Coincident(g7,g-5)
    c: Equal(g0,g4)
    c: Equal(g1,g3)
    c: DistanceX(g2,g2) = 9.6
    c: DistanceX(g0,g4) = 5.6
    c: Coincident(g7,g8)
    c: Horizontal(g8)
    c: Coincident(g8,g9)
    c: Coincident(g9,g0)
    c: Coincident(g4,g10)
    c: Coincident(g10,g11)
    c: Coincident(g11,g5)
    c: Horizontal(g11)
    c: Coincident(g-4,g5)
    c: Vertical(g10)
    c: Vertical(g9)
    c: Equal(g8,g11)
    c: Distance(g8,g2) = 4.25
    c: DistanceY(g9,g9) = 1
FEATURE [PartDesign::Pad] Pad115
  Direction = (1,0,0)
  Length = 15
  Length2 = 10
  Placement = pos=(85,-5.66e-14,2.83e-14) rot=(0,0,1;0rad)
  Profile = -> Sketch231
  ReferenceAxis = -> Sketch231 [N_Axis]
  Refine = true
  Suppressed = false
  Type = 0
FEATURE [PartDesign::ShapeBinder] CopyLinearPattern012
  TraceSupport = false
FEATURE [Sketcher::SketchObject] Sketch232
  ArcFitTolerance = 1e-06
  AttachmentSupport = -> [CopyLinearPattern012]
  ExternalGeometry = -> [CopyLinearPattern012]
  FullyConstrained = true
  MakeInternals = false
  MapMode = 5
  Placement = pos=(0,240,0) rot=(0,0.707107,0.707107;3.14159rad)
  sketch-geometry (10):
    g0: LineSegment StartX=10 StartY=3.1 StartZ=0 EndX=10 EndY=-3.1 EndZ=0
    g1: LineSegment StartX=10 StartY=3.1 StartZ=0 EndX=8 EndY=3.1 EndZ=0
    g2: LineSegment StartX=8 StartY=3.1 StartZ=0 EndX=8 EndY=5.5 EndZ=0
    g3: LineSegment StartX=8 StartY=5.5 StartZ=0 EndX=6.3 EndY=5.5 EndZ=0
    g4: LineSegment StartX=6.3 StartY=5.5 StartZ=0 EndX=3.9 EndY=3.1 EndZ=0
    g5: LineSegment StartX=3.9 StartY=3.1 StartZ=0 EndX=3.9 EndY=-3.1 EndZ=0
    g6: LineSegment StartX=3.9 StartY=-3.1 StartZ=0 EndX=6.3 EndY=-5.5 EndZ=0
    g7: LineSegment StartX=6.3 StartY=-5.5 StartZ=0 EndX=8 EndY=-5.5 EndZ=0
    g8: LineSegment StartX=8 StartY=-5.5 StartZ=0 EndX=8 EndY=-3.1 EndZ=0
    g9: LineSegment StartX=8 StartY=-3.1 StartZ=0 EndX=10 EndY=-3.1 EndZ=0
  constraints (21):
    c: Coincident(g0,g-3)
    c: Coincident(g0,g-11)
    c: Coincident(g0,g1)
    c: Coincident(g1,g-4)
    c: Coincident(g1,g2)
    c: Coincident(g2,g-5)
    c: Coincident(g2,g3)
    c: Coincident(g3,g-6)
    c: Coincident(g3,g4)
    c: Coincident(g4,g-7)
    c: Coincident(g4,g5)
    c: Coincident(g5,g-8)
    c: Coincident(g5,g6)
    c: Coincident(g6,g-9)
    c: Coincident(g6,g7)
    c: Horizontal(g7)
    c: Coincident(g7,g8)
    c: Coincident(g8,g-11)
    c: Vertical(g8)
    c: Coincident(g8,g9)
    c: Coincident(g9,g0)
FEATURE [PartDesign::Pad] Pad116
  Direction = (0,1,-2e-16)
  Length = 120
  Length2 = 10
  Profile = -> Sketch232
  ReferenceAxis = -> Sketch232 [N_Axis]
  Refine = true
  Suppressed = false
  Type = 0
FEATURE [Sketcher::SketchObject] Sketch233
  ArcFitTolerance = 1e-06
  AttachmentSupport = -> [Pad116]
  ExternalGeometry = -> [Pad116]
  FullyConstrained = true
  MakeInternals = false
  MapMode = 5
  Placement = pos=(0,240,0) rot=(1,0,0;1.5708rad)
  sketch-geometry (14):
    g0: LineSegment StartX=-8 StartY=5.1 StartZ=0 EndX=-8 EndY=5.5 EndZ=0
    g1: LineSegment StartX=-8 StartY=5.5 StartZ=0 EndX=-6.3 EndY=5.5 EndZ=0
    g2: LineSegment StartX=-6.3 StartY=5.5 StartZ=0 EndX=-3.9 EndY=3.1 EndZ=0
    g3: LineSegment StartX=-3.9 StartY=3.1 StartZ=0 EndX=-3.9 EndY=-3.1 EndZ=0
    g4: LineSegment StartX=-3.9 StartY=-3.1 StartZ=0 EndX=-6.3 EndY=-5.5 EndZ=0
    g5: LineSegment StartX=-6.3 StartY=-5.5 StartZ=0 EndX=-8 EndY=-5.5 EndZ=0
    g6: LineSegment StartX=-8 StartY=-5.5 StartZ=0 EndX=-8 EndY=-5.1 EndZ=0
    g7: LineSegment StartX=-8 StartY=-5.1 StartZ=0 EndX=-6.46569 EndY=-5.1 EndZ=0
    g8: LineSegment StartX=-6.46569 StartY=-5.1 StartZ=0 EndX=-4.3 EndY=-2.93431 EndZ=0
    g9: LineSegment StartX=-4.3 StartY=-2.93431 StartZ=0 EndX=-4.3 EndY=2.93431 EndZ=0
    g10: LineSegment StartX=-4.3 StartY=2.93431 StartZ=0 EndX=-6.46569 EndY=5.1 EndZ=0
    g11: LineSegment StartX=-6.46569 StartY=5.1 StartZ=0 EndX=-8 EndY=5.1 EndZ=0
    g12: LineSegment [constr] StartX=-5.38284 StartY=4.01716 StartZ=0 EndX=-5.1 EndY=4.3 EndZ=0
    g13: LineSegment [constr] StartX=-4.3 StartY=1e-15 StartZ=0 EndX=-3.9 EndY=1e-16 EndZ=0
  constraints (35):
    c: PointOnObject(g0,g-3)
    c: Coincident(g0,g-4)
    c: Coincident(g0,g1)
    c: Coincident(g1,g-5)
    c: Coincident(g1,g2)
    c: Coincident(g2,g-6)
    c: Coincident(g2,g3)
    c: Coincident(g3,g-7)
    c: Coincident(g3,g4)
    c: Coincident(g4,g-8)
    c: Coincident(g4,g5)
    c: Coincident(g5,g-9)
    c: Coincident(g5,g6)
    c: PointOnObject(g6,g-9)
    c: Coincident(g6,g7)
    c: Horizontal(g7)
    c: Coincident(g7,g8)
    c: Coincident(g8,g9)
    c: Vertical(g9)
    c: Coincident(g9,g10)
    c: Coincident(g10,g11)
    c: Coincident(g11,g0)
    c: Horizontal(g11)
    c: Equal(g11,g7)
    c: Equal(g8,g10)
    c: Angle(g8,g7) = 2.35619
    c: Equal(g6,g0)
    c: Distance(g0,g0) = 0.4
    c: PointOnObject(g12,g10)
    c: Symmetric(g2,g2,g12)
    c: Perpendicular(g2,g12)
    c: Symmetric(g9,g9,g13)
    c: Symmetric(g3,g3,g13)
    c: Equal(g13,g12)
    c: Equal(g12,g0)
FEATURE [PartDesign::Pocket] Pocket083
  BaseFeature = -> Pad116
  Direction = (0,1,-2e-16)
  Length = 5
  Length2 = 5
  Profile = -> Sketch233
  ReferenceAxis = -> Sketch233 [N_Axis]
  Refine = true
  Suppressed = false
  Type = 1
FEATURE [Sketcher::SketchObject] Sketch234
  ArcFitTolerance = 1e-06
  AttachmentSupport = -> [Pocket083]
  ExternalGeometry = -> [Pocket083]
  FullyConstrained = true
  MakeInternals = false
  MapMode = 5
  Placement = pos=(-10,0,0) rot=(0.57735,-0.57735,-0.57735;2.0944rad)
  sketch-geometry (4):
    g0: Circle CenterX=-267.3 CenterY=0 CenterZ=0 NormalX=0 NormalY=0 NormalZ=1 AngleXU=0 Radius=1.5
    g1: Circle CenterX=-292.3 CenterY=0 CenterZ=0 NormalX=0 NormalY=0 NormalZ=1 AngleXU=0 Radius=1.5
    g2: Circle CenterX=-327.3 CenterY=0 CenterZ=0 NormalX=0 NormalY=0 NormalZ=1 AngleXU=0 Radius=1.5
    g3: Circle CenterX=-352.3 CenterY=0 CenterZ=0 NormalX=0 NormalY=0 NormalZ=1 AngleXU=0 Radius=1.5
  constraints (12):
    c: Diameter(g0) = 3
    c: PointOnObject(g0,g-1)
    c: PointOnObject(g1,g-1)
    c: PointOnObject(g2,g-1)
    c: PointOnObject(g3,g-1)
    c: DistanceX(g3,g2) = 25
    c: DistanceX(g1,g0) = 25
    c: Distance(g0,g-3) = 25.8
    c: DistanceX(g2,g0) = 60
    c: Equal(g3,g2)
    c: Equal(g2,g1)
    c: Equal(g1,g0)
FEATURE [PartDesign::Hole] Hole043
  BaseFeature = -> Pocket083
  CustomThreadClearance = 0
  Depth = 25
  DepthType = 0
  Diameter = 4
  DrillForDepth = false
  DrillPoint = 1
  DrillPointAngle = 118
  HoleCutCountersinkAngle = 90
  HoleCutCustomValues = false
  HoleCutDepth = 0
  HoleCutDiameter = 6.1
  HoleCutType = 0
  ModelThread = false
  Profile = -> Sketch234
  Refine = true
  Suppressed = false
  Tapered = true
  TaperedAngle = 86
  ThreadClass = 0
  ThreadDepth = 25
  ThreadDepthType = 0
  ThreadDirection = 0
  ThreadFit = 0
  ThreadSize = 0
  ThreadType = 0
  Threaded = false
  UseCustomThreadClearance = false
FEATURE [Sketcher::SketchObject] Sketch235
  ArcFitTolerance = 1e-06
  AttachmentSupport = -> [Hole043]
  ExternalGeometry = -> [Hole043]
  FullyConstrained = true
  MakeInternals = false
  MapMode = 5
  Placement = pos=(0,240,0) rot=(1,0,0;1.5708rad)
  sketch-geometry (5):
    g0: LineSegment StartX=-10 StartY=7.5 StartZ=0 EndX=-10 EndY=-7.5 EndZ=0
    g1: LineSegment StartX=-10 StartY=-7.5 StartZ=0 EndX=-4.3 EndY=-7.5 EndZ=0
    g2: LineSegment StartX=-4.3 StartY=-7.5 StartZ=0 EndX=-4.3 EndY=7.5 EndZ=0
    g3: LineSegment StartX=-4.3 StartY=7.5 StartZ=0 EndX=-10 EndY=7.5 EndZ=0
    g4: GeomPoint X=-10 Y=0 Z=0
  constraints (13):
    c: Coincident(g0,g1)
    c: Coincident(g1,g2)
    c: Coincident(g2,g3)
    c: Coincident(g3,g0)
    c: Vertical(g0)
    c: Vertical(g2)
    c: Horizontal(g1)
    c: Horizontal(g3)
    c: PointOnObject(g-4,g2)
    c: PointOnObject(g-3,g0)
    c: Symmetric(g0,g0,g4)
    c: PointOnObject(g4,g-1)
    c: DistanceY(g0,g0) = 15
FEATURE [PartDesign::Pad] Pad117
  BaseFeature = -> Hole043
  Direction = (0,-1,2e-16)
  Length = 4
  Length2 = 10
  Profile = -> Sketch235
  ReferenceAxis = -> Sketch235 [N_Axis]
  Refine = true
  Suppressed = false
  Type = 0
FEATURE [PartDesign::Body] Body138  label="DrillMarker003"
  AllowCompound = false
  Group = -> [CopyLinearPattern012,Sketch232,Pad116,Sketch233,Pocket083,Sketch234,Hole043,Sketch235,Pad117]
  Origin = -> Origin1484
  Placement = pos=(-81,229,-133) rot=(0.57735,0.57735,0.57735;2.0944rad)
  Tip = -> Pad117
FEATURE [PartDesign::ShapeBinder] CopyLinearPattern013
  TraceSupport = false
FEATURE [Sketcher::SketchObject] Sketch236
  ArcFitTolerance = 1e-06
  AttachmentSupport = -> [CopyLinearPattern013]
  ExternalGeometry = -> [CopyLinearPattern013]
  FullyConstrained = true
  MakeInternals = false
  MapMode = 5
  Placement = pos=(0,240,0) rot=(0,0.707107,0.707107;3.14159rad)
  sketch-geometry (10):
    g0: LineSegment StartX=10 StartY=3.1 StartZ=0 EndX=10 EndY=-3.1 EndZ=0
    g1: LineSegment StartX=10 StartY=3.1 StartZ=0 EndX=8 EndY=3.1 EndZ=0
    g2: LineSegment StartX=8 StartY=3.1 StartZ=0 EndX=8 EndY=5.5 EndZ=0
    g3: LineSegment StartX=8 StartY=5.5 StartZ=0 EndX=6.3 EndY=5.5 EndZ=0
    g4: LineSegment StartX=6.3 StartY=5.5 StartZ=0 EndX=3.9 EndY=3.1 EndZ=0
    g5: LineSegment StartX=3.9 StartY=3.1 StartZ=0 EndX=3.9 EndY=-3.1 EndZ=0
    g6: LineSegment StartX=3.9 StartY=-3.1 StartZ=0 EndX=6.3 EndY=-5.5 EndZ=0
    g7: LineSegment StartX=6.3 StartY=-5.5 StartZ=0 EndX=8 EndY=-5.5 EndZ=0
    g8: LineSegment StartX=8 StartY=-5.5 StartZ=0 EndX=8 EndY=-3.1 EndZ=0
    g9: LineSegment StartX=8 StartY=-3.1 StartZ=0 EndX=10 EndY=-3.1 EndZ=0
  constraints (21):
    c: Coincident(g0,g-3)
    c: Coincident(g0,g-11)
    c: Coincident(g0,g1)
    c: Coincident(g1,g-4)
    c: Coincident(g1,g2)
    c: Coincident(g2,g-5)
    c: Coincident(g2,g3)
    c: Coincident(g3,g-6)
    c: Coincident(g3,g4)
    c: Coincident(g4,g-7)
    c: Coincident(g4,g5)
    c: Coincident(g5,g-8)
    c: Coincident(g5,g6)
    c: Coincident(g6,g-9)
    c: Coincident(g6,g7)
    c: Horizontal(g7)
    c: Coincident(g7,g8)
    c: Coincident(g8,g-11)
    c: Vertical(g8)
    c: Coincident(g8,g9)
    c: Coincident(g9,g0)
FEATURE [PartDesign::Pad] Pad118
  Direction = (0,1,-2e-16)
  Length = 90
  Length2 = 10
  Profile = -> Sketch236
  ReferenceAxis = -> Sketch236 [N_Axis]
  Refine = true
  Suppressed = false
  Type = 0
FEATURE [Sketcher::SketchObject] Sketch237
  ArcFitTolerance = 1e-06
  AttachmentSupport = -> [Pad118]
  ExternalGeometry = -> [Pad118]
  FullyConstrained = true
  MakeInternals = false
  MapMode = 5
  Placement = pos=(0,240,0) rot=(1,0,0;1.5708rad)
  sketch-geometry (14):
    g0: LineSegment StartX=-8 StartY=5.1 StartZ=0 EndX=-8 EndY=5.5 EndZ=0
    g1: LineSegment StartX=-8 StartY=5.5 StartZ=0 EndX=-6.3 EndY=5.5 EndZ=0
    g2: LineSegment StartX=-6.3 StartY=5.5 StartZ=0 EndX=-3.9 EndY=3.1 EndZ=0
    g3: LineSegment StartX=-3.9 StartY=3.1 StartZ=0 EndX=-3.9 EndY=-3.1 EndZ=0
    g4: LineSegment StartX=-3.9 StartY=-3.1 StartZ=0 EndX=-6.3 EndY=-5.5 EndZ=0
    g5: LineSegment StartX=-6.3 StartY=-5.5 StartZ=0 EndX=-8 EndY=-5.5 EndZ=0
    g6: LineSegment StartX=-8 StartY=-5.5 StartZ=0 EndX=-8 EndY=-5.1 EndZ=0
    g7: LineSegment StartX=-8 StartY=-5.1 StartZ=0 EndX=-6.46569 EndY=-5.1 EndZ=0
    g8: LineSegment StartX=-6.46569 StartY=-5.1 StartZ=0 EndX=-4.3 EndY=-2.93431 EndZ=0
    g9: LineSegment StartX=-4.3 StartY=-2.93431 StartZ=0 EndX=-4.3 EndY=2.93431 EndZ=0
    g10: LineSegment StartX=-4.3 StartY=2.93431 StartZ=0 EndX=-6.46569 EndY=5.1 EndZ=0
    g11: LineSegment StartX=-6.46569 StartY=5.1 StartZ=0 EndX=-8 EndY=5.1 EndZ=0
    g12: LineSegment [constr] StartX=-5.38284 StartY=4.01716 StartZ=0 EndX=-5.1 EndY=4.3 EndZ=0
    g13: LineSegment [constr] StartX=-4.3 StartY=1e-15 StartZ=0 EndX=-3.9 EndY=1e-16 EndZ=0
  constraints (35):
    c: PointOnObject(g0,g-3)
    c: Coincident(g0,g-4)
    c: Coincident(g0,g1)
    c: Coincident(g1,g-5)
    c: Coincident(g1,g2)
    c: Coincident(g2,g-6)
    c: Coincident(g2,g3)
    c: Coincident(g3,g-7)
    c: Coincident(g3,g4)
    c: Coincident(g4,g-8)
    c: Coincident(g4,g5)
    c: Coincident(g5,g-9)
    c: Coincident(g5,g6)
    c: PointOnObject(g6,g-9)
    c: Coincident(g6,g7)
    c: Horizontal(g7)
    c: Coincident(g7,g8)
    c: Coincident(g8,g9)
    c: Vertical(g9)
    c: Coincident(g9,g10)
    c: Coincident(g10,g11)
    c: Coincident(g11,g0)
    c: Horizontal(g11)
    c: Equal(g11,g7)
    c: Equal(g8,g10)
    c: Angle(g8,g7) = 2.35619
    c: Equal(g6,g0)
    c: Distance(g0,g0) = 0.4
    c: PointOnObject(g12,g10)
    c: Symmetric(g2,g2,g12)
    c: Perpendicular(g2,g12)
    c: Symmetric(g9,g9,g13)
    c: Symmetric(g3,g3,g13)
    c: Equal(g13,g12)
    c: Equal(g12,g0)
FEATURE [PartDesign::Pocket] Pocket084
  BaseFeature = -> Pad118
  Direction = (0,1,-2e-16)
  Length = 5
  Length2 = 5
  Profile = -> Sketch237
  ReferenceAxis = -> Sketch237 [N_Axis]
  Refine = true
  Suppressed = false
  Type = 1
FEATURE [Sketcher::SketchObject] Sketch238
  ArcFitTolerance = 1e-06
  AttachmentSupport = -> [Pocket084]
  ExternalGeometry = -> [Pocket084]
  FullyConstrained = true
  MakeInternals = false
  MapMode = 5
  Placement = pos=(-10,0,0) rot=(0.57735,-0.57735,-0.57735;2.0944rad)
  sketch-geometry (3):
    g0: Circle CenterX=-310 CenterY=0 CenterZ=0 NormalX=0 NormalY=0 NormalZ=1 AngleXU=0 Radius=2
    g1: Circle CenterX=-302 CenterY=0 CenterZ=0 NormalX=0 NormalY=0 NormalZ=1 AngleXU=0 Radius=2
    g2: Circle CenterX=-318 CenterY=0 CenterZ=0 NormalX=0 NormalY=0 NormalZ=1 AngleXU=0 Radius=2
  constraints (8):
    c: Diameter(g1) = 4
    c: PointOnObject(g1,g-1)
    c: Diameter(g2) = 4
    c: PointOnObject(g2,g-1)
    c: Equal(g0,g2)
    c: Symmetric(g2,g1,g0)
    c: DistanceX(g2,g1) = 16
    c: DistanceX(g1,g-1) = 302
FEATURE [PartDesign::Pocket] Pocket085
  BaseFeature = -> Pocket084
  Direction = (1,0,0)
  Length = 10
  Length2 = 5
  Profile = -> Sketch238
  ReferenceAxis = -> Sketch238 [N_Axis]
  Refine = true
  Suppressed = false
  TaperAngle = -5
  Type = 0
FEATURE [Sketcher::SketchObject] Sketch239
  ArcFitTolerance = 1e-06
  AttachmentSupport = -> [Pocket085]
  ExternalGeometry = -> [Pocket085]
  FullyConstrained = true
  MakeInternals = false
  MapMode = 5
  Placement = pos=(0,240,0) rot=(1,0,0;1.5708rad)
  sketch-geometry (5):
    g0: LineSegment StartX=-10 StartY=7.5 StartZ=0 EndX=-10 EndY=-7.5 EndZ=0
    g1: LineSegment StartX=-10 StartY=-7.5 StartZ=0 EndX=-4.3 EndY=-7.5 EndZ=0
    g2: LineSegment StartX=-4.3 StartY=-7.5 StartZ=0 EndX=-4.3 EndY=7.5 EndZ=0
    g3: LineSegment StartX=-4.3 StartY=7.5 StartZ=0 EndX=-10 EndY=7.5 EndZ=0
    g4: GeomPoint X=-10 Y=0 Z=0
  constraints (13):
    c: Coincident(g0,g1)
    c: Coincident(g1,g2)
    c: Coincident(g2,g3)
    c: Coincident(g3,g0)
    c: Vertical(g0)
    c: Vertical(g2)
    c: Horizontal(g1)
    c: Horizontal(g3)
    c: PointOnObject(g-4,g2)
    c: PointOnObject(g-3,g0)
    c: DistanceY(g0,g0) = 15
    c: Symmetric(g0,g0,g4)
    c: PointOnObject(g4,g-1)
FEATURE [PartDesign::Pad] Pad119
  BaseFeature = -> Pocket085
  Direction = (0,-1,2e-16)
  Length = 4
  Length2 = 10
  Profile = -> Sketch239
  ReferenceAxis = -> Sketch239 [N_Axis]
  Refine = true
  Suppressed = false
  Type = 0
FEATURE [PartDesign::Body] Body139  label="DrillMarker004"
  AllowCompound = false
  Group = -> [CopyLinearPattern013,Sketch236,Pad118,Sketch237,Pocket084,Sketch238,Pocket085,Sketch239,Pad119]
  Origin = -> Origin1485
  Placement = pos=(-41,229.5,-133) rot=(0,0.707107,0.707107;3.14159rad)
  Tip = -> Pad119
FEATURE [Sketcher::SketchObject] Sketch240
  ArcFitTolerance = 1e-06
  AttachmentSupport = -> [YZ_Plane1077]
  FullyConstrained = true
  MakeInternals = false
  MapMode = 5
  Placement = pos=(0,0,0) rot=(0.57735,0.57735,0.57735;2.0944rad)
  sketch-geometry (12):
    g0: LineSegment StartX=-5.25 StartY=11.45 StartZ=0 EndX=-5.25 EndY=15.45 EndZ=0
    g1: LineSegment StartX=-5.25 StartY=15.45 StartZ=0 EndX=19.75 EndY=15.45 EndZ=0
    g2: LineSegment StartX=19.75 StartY=15.45 StartZ=0 EndX=19.75 EndY=11.45 EndZ=0
    g3: LineSegment StartX=19.75 StartY=11.45 StartZ=0 EndX=11.25 EndY=11.45 EndZ=0
    g4: LineSegment StartX=11.25 StartY=11.45 StartZ=0 EndX=11.25 EndY=7.15 EndZ=0
    g5: LineSegment StartX=11.25 StartY=7.15 StartZ=0 EndX=14.5 EndY=7.15 EndZ=0
    g6: LineSegment StartX=14.5 StartY=7.15 StartZ=0 EndX=14.5 EndY=0 EndZ=0
    g7: LineSegment StartX=14.5 StartY=0 StartZ=0 EndX=0 EndY=0 EndZ=0
    g8: LineSegment StartX=0 StartY=0 StartZ=0 EndX=0 EndY=7.15 EndZ=0
    g9: LineSegment StartX=0 StartY=7.15 StartZ=0 EndX=3.25 EndY=7.15 EndZ=0
    g10: LineSegment StartX=3.25 StartY=7.15 StartZ=0 EndX=3.25 EndY=11.45 EndZ=0
    g11: LineSegment StartX=3.25 StartY=11.45 StartZ=0 EndX=-5.25 EndY=11.45 EndZ=0
  constraints (35):
    c: Coincident(g0,g1)
    c: Horizontal(g1)
    c: Coincident(g1,g2)
    c: Vertical(g2)
    c: Coincident(g2,g3)
    c: Horizontal(g3)
    c: Coincident(g3,g4)
    c: Vertical(g4)
    c: Coincident(g4,g5)
    c: Horizontal(g5)
    c: Coincident(g5,g6)
    c: Vertical(g6)
    c: Coincident(g6,g7)
    c: Horizontal(g7)
    c: Coincident(g7,g8)
    c: Vertical(g8)
    c: Coincident(g8,g9)
    c: Coincident(g9,g10)
    c: Vertical(g10)
    c: Coincident(g10,g11)
    c: Coincident(g11,g0)
    c: Horizontal(g11)
    c: Horizontal(g9)
    c: Vertical(g0)
    c: Equal(g0,g2)
    c: Equal(g3,g11)
    c: Equal(g10,g4)
    c: Equal(g5,g9)
    c: DistanceX(g10,g3) = 8
    c: Distance(g8,g8) = 7.15
    c: DistanceY(g10,g10) = 4.3
    c: Distance(g0,g0) = 4
    c: Coincident(g-1,g7)
    c: DistanceX(g7,g7) = 14.5
    c: DistanceX(g1,g1) = 25
FEATURE [PartDesign::Pad] Pad120
  Direction = (1,0,0)
  Length = 85
  Length2 = 10
  Placement = pos=(0,0,0) rot=(1,1,1;2.0944rad)
  Profile = -> Sketch240
  ReferenceAxis = -> Sketch240 [N_Axis]
  Refine = true
  Suppressed = false
  Type = 0
FEATURE [Sketcher::SketchObject] Sketch241
  ArcFitTolerance = 1e-06
  AttachmentSupport = -> [Pad120]
  ExternalGeometry = -> [Pad120]
  FullyConstrained = false
  MakeInternals = false
  MapMode = 5
  Placement = pos=(0,3.4e-15,15.45) rot=(0,0,-1;1.5708rad)
  sketch-geometry (13):
    g0: GeomPoint X=-17.25 Y=77.5 Z=0
    g1: GeomPoint X=2.75 Y=77.5 Z=0
    g2: GeomPoint X=-17.25 Y=52.5 Z=0
    g3: GeomPoint X=2.75 Y=52.5 Z=0
    g4: GeomPoint [constr] X=-7.25 Y=85 Z=0
    g5: GeomPoint [constr] X=-7.25 Y=77.5 Z=0
    g6: Circle [constr] CenterX=-17.25 CenterY=52.5 CenterZ=0 NormalX=0 NormalY=0 NormalZ=1 AngleXU=0 Radius=2.76539
    g7: GeomPoint [constr] X=-19.8387 Y=247.482 Z=0
    g8: GeomPoint [constr] X=-21.1928 Y=299.991 Z=0
    g9: Circle CenterX=-17.25 CenterY=77.5 CenterZ=0 NormalX=0 NormalY=0 NormalZ=1 AngleXU=0 Radius=1.5
    g10: Circle CenterX=-17.25 CenterY=52.5 CenterZ=0 NormalX=0 NormalY=0 NormalZ=1 AngleXU=0 Radius=1.5
    g11: Circle CenterX=2.75 CenterY=52.5 CenterZ=0 NormalX=0 NormalY=0 NormalZ=1 AngleXU=0 Radius=1.5
    g12: Circle CenterX=2.75 CenterY=77.5 CenterZ=0 NormalX=0 NormalY=0 NormalZ=1 AngleXU=0 Radius=1.5
  constraints (19):
    c: Vertical(g1,g3)
    c: Vertical(g0,g2)
    c: Horizontal(g0,g1)
    c: Horizontal(g2,g3)
    c: DistanceY(g3,g1) = 25
    c: DistanceX(g0,g1) = 20
    c: Symmetric(g-3,g-3,g4)
    c: Vertical(g4,g5)
    c: Symmetric(g0,g1,g5)
    c: Coincident(g6,g2)
    c: DistanceY(g-1,g2) = 52.5
    c: Coincident(g9,g0)
    c: Coincident(g10,g2)
    c: Coincident(g11,g3)
    c: Coincident(g12,g1)
    c: Equal(g12,g9)
    c: Equal(g9,g10)
    c: Equal(g10,g11)
    c: Diameter(g9) = 3
FEATURE [PartDesign::Pocket] Pocket086
  BaseFeature = -> Pad120
  Direction = (0,0,-1)
  Length = 5
  Length2 = 5
  Placement = pos=(0,0,0) rot=(1,1,1;2.0944rad)
  Profile = -> Sketch241
  ReferenceAxis = -> Sketch241 [N_Axis]
  Refine = true
  Suppressed = false
  Type = 1
FEATURE [Sketcher::SketchObject] Sketch242
  ArcFitTolerance = 1e-06
  AttachmentSupport = -> [Pocket086]
  ExternalGeometry = -> [Pocket086]
  FullyConstrained = true
  MakeInternals = false
  MapMode = 5
  Placement = pos=(0,0,0) rot=(0.57735,0.57735,-0.57735;4.18879rad)
  sketch-geometry (4):
    g0: LineSegment StartX=19.75 StartY=-15.45 StartZ=0 EndX=19.75 EndY=0 EndZ=0
    g1: LineSegment StartX=19.75 StartY=0 StartZ=0 EndX=-5.25 EndY=0 EndZ=0
    g2: LineSegment StartX=-5.25 StartY=0 StartZ=0 EndX=-5.25 EndY=-15.45 EndZ=0
    g3: LineSegment StartX=-5.25 StartY=-15.45 StartZ=0 EndX=19.75 EndY=-15.45 EndZ=0
  constraints (10):
    c: Coincident(g0,g1)
    c: Coincident(g1,g2)
    c: Coincident(g2,g3)
    c: Coincident(g3,g0)
    c: Vertical(g0)
    c: Vertical(g2)
    c: Horizontal(g1)
    c: Coincident(g0,g-3)
    c: PointOnObject(g1,g-1)
    c: Coincident(g-3,g2)
FEATURE [PartDesign::Pad] Pad121
  BaseFeature = -> Pocket086
  Direction = (-1,0,0)
  Length = 4
  Length2 = 10
  Placement = pos=(0,0,0) rot=(1,1,1;2.0944rad)
  Profile = -> Sketch242
  ReferenceAxis = -> Sketch242 [N_Axis]
  Refine = true
  Suppressed = false
  Type = 0
FEATURE [PartDesign::Body] Body140  label="DrillMarker005"
  AllowCompound = false
  Group = -> [Sketch240,Pad120,Sketch241,Pocket086,Sketch242,Pad121]
  Origin = -> Origin1486
  Placement = pos=(-115,122.3,7) rot=(0,0,1;0rad)
  Tip = -> Pad121
FEATURE [Sketcher::SketchObject] Sketch243
  ArcFitTolerance = 1e-06
  AttachmentSupport = -> [Fillet001]
  ExternalGeometry = -> [Fillet001]
  FullyConstrained = true
  MakeInternals = false
  MapMode = 5
  Placement = pos=(0,0,-53) rot=(1,0,0;3.14159rad)
  sketch-geometry (8):
    g0: LineSegment StartX=-44.8 StartY=-324 StartZ=0 EndX=-44.8 EndY=-348.25 EndZ=0
    g1: LineSegment StartX=-44.8 StartY=-348.25 StartZ=0 EndX=-42.3 EndY=-348.25 EndZ=0
    g2: LineSegment StartX=-42.3 StartY=-348.25 StartZ=0 EndX=-42.3 EndY=-324 EndZ=0
    g3: LineSegment StartX=-42.3 StartY=-324 StartZ=0 EndX=-44.8 EndY=-324 EndZ=0
    g4: LineSegment StartX=2.5 StartY=-324 StartZ=0 EndX=0 EndY=-324 EndZ=0
    g5: LineSegment StartX=0 StartY=-324 StartZ=0 EndX=0 EndY=-348.25 EndZ=0
    g6: LineSegment StartX=0 StartY=-348.25 StartZ=0 EndX=2.5 EndY=-348.25 EndZ=0
    g7: LineSegment StartX=2.5 StartY=-348.25 StartZ=0 EndX=2.5 EndY=-324 EndZ=0
  constraints (20):
    c: Coincident(g0,g1)
    c: Coincident(g1,g2)
    c: Coincident(g2,g3)
    c: Coincident(g3,g0)
    c: Vertical(g0)
    c: Vertical(g2)
    c: Horizontal(g1)
    c: Horizontal(g3)
    c: Coincident(g0,g-5)
    c: Symmetric(g-3,g-3,g1)
    c: Coincident(g4,g5)
    c: Coincident(g5,g6)
    c: Coincident(g6,g7)
    c: Coincident(g7,g4)
    c: Horizontal(g4)
    c: Horizontal(g6)
    c: Vertical(g5)
    c: Vertical(g7)
    c: Coincident(g4,g-6)
    c: Symmetric(g-4,g-4,g5)
FEATURE [PartDesign::Pad] Pad122
  BaseFeature = -> Fillet001
  Direction = (0,0,-1)
  Length = 15
  Length2 = 10
  Offset = 5
  Profile = -> Sketch243
  ReferenceAxis = -> Sketch243 [N_Axis]
  Refine = true
  Reversed = true
  Suppressed = false
  Type = 3
  UpToFace = -> Fillet001 [Face11]
FEATURE [PartDesign::Chamfer] Chamfer003
  Angle = 45
  Base = -> Pad122 [Edge88,Edge79]
  BaseFeature = -> Pad122
  ChamferType = 0
  FlipDirection = false
  Refine = true
  Size = 2
  Size2 = 1
  SupportTransform = false
  Suppressed = false
  UseAllEdges = false
FEATURE [PartDesign::Chamfer] Chamfer004
  Angle = 45
  Base = -> Chamfer003 [Edge65,Edge70]
  BaseFeature = -> Chamfer003
  ChamferType = 0
  FlipDirection = false
  Refine = true
  Size = 2
  Size2 = 1
  SupportTransform = false
  Suppressed = false
  UseAllEdges = false
FEATURE [PartDesign::Body] Body083  label="yMotorHolder"
  AllowCompound = false
  Group = -> [ShapeBinder,Sketch160,ShapeBinder001,Pad080,Sketch162,Pocket058,Sketch163,Pad081,Sketch164,Hole020,Chamfer001,Chamfer002,Fillet001,Sketch243,Pad122,Chamfer003,Chamfer004]
  Origin = -> Origin1256
  Placement = pos=(56.25,0,0) rot=(0,0,1;0rad)
  Tip = -> Chamfer004
FEATURE [Sketcher::SketchObject] Sketch244
  ArcFitTolerance = 1e-06
  AttachmentSupport = -> [Hole025]
  ExternalGeometry = -> [Hole025]
  FullyConstrained = true
  MakeInternals = false
  MapMode = 5
  Placement = pos=(0,0,0) rot=(1,0,0;1.5708rad)
  sketch-geometry (9):
    g0: LineSegment StartX=38.25 StartY=0 StartZ=0 EndX=38.25 EndY=-10 EndZ=0
    g1: LineSegment StartX=38.25 StartY=-10 StartZ=0 EndX=44.75 EndY=-10 EndZ=0
    g2: LineSegment StartX=44.75 StartY=-10 StartZ=0 EndX=44.75 EndY=-5.26 EndZ=0
    g3: ArcOfCircle CenterX=50 CenterY=-5.26 CenterZ=0 NormalX=0 NormalY=0 NormalZ=1 AngleXU=0 Radius=5.25 StartAngle=1e-16 EndAngle=3.14159
    g4: LineSegment StartX=55.25 StartY=-5.26 StartZ=0 EndX=55.25 EndY=-10 EndZ=0
    g5: LineSegment StartX=55.25 StartY=-10 StartZ=0 EndX=61.75 EndY=-10 EndZ=0
    g6: LineSegment StartX=61.75 StartY=-10 StartZ=0 EndX=61.75 EndY=0 EndZ=0
    g7: LineSegment StartX=61.75 StartY=0 StartZ=0 EndX=38.25 EndY=0 EndZ=0
    g8: GeomPoint X=50 Y=0 Z=0
  constraints (23):
    c: PointOnObject(g0,g-3)
    c: Vertical(g0)
    c: Coincident(g0,g1)
    c: Horizontal(g1)
    c: Coincident(g1,g2)
    c: Vertical(g2)
    c: Tangent(g2,g3) = 1.5708
    c: Tangent(g3,g4) = 1.5708
    c: Coincident(g4,g5)
    c: Horizontal(g5)
    c: Coincident(g5,g6)
    c: Vertical(g6)
    c: Coincident(g6,g7)
    c: Coincident(g7,g0)
    c: Vertical(g4)
    c: Radius(g3) = 5.25
    c: Equal(g1,g5)
    c: Distance(g3,g7) = 0.01
    c: DistanceY(g0,g0) = 10
    c: Horizontal(g4,g1)
    c: Symmetric(g-1,g-3,g8)
    c: Symmetric(g0,g6,g8)
    c: DistanceX(g5,g5) = 6.5
FEATURE [PartDesign::Pad] Pad123
  BaseFeature = -> Hole028
  Direction = (0,-1,2e-16)
  Length = 10
  Length2 = 10
  Profile = -> Sketch244
  ReferenceAxis = -> Sketch244 [N_Axis]
  Refine = true
  Suppressed = false
  Type = 3
  UpToFace = -> Hole028 [Face6]
FEATURE [Sketcher::SketchObject] Sketch245
  ArcFitTolerance = 1e-06
  AttachmentSupport = -> [Pad123]
  ExternalGeometry = -> [Pad123]
  FullyConstrained = true
  MakeInternals = false
  MapMode = 5
  Placement = pos=(0,50,0) rot=(0,0.707107,0.707107;3.14159rad)
  sketch-geometry (8):
    g0: Circle CenterX=-50 CenterY=2.75 CenterZ=0 NormalX=0 NormalY=0 NormalZ=1 AngleXU=0 Radius=1.95
    g1: Circle CenterX=-41.99 CenterY=-5.26 CenterZ=0 NormalX=0 NormalY=0 NormalZ=1 AngleXU=0 Radius=1.95
    g2: Circle CenterX=-58.01 CenterY=-5.26 CenterZ=0 NormalX=0 NormalY=0 NormalZ=1 AngleXU=0 Radius=1.95
    g3: LineSegment [constr] StartX=-50 StartY=-13.27 StartZ=0 EndX=-41.99 EndY=-5.26 EndZ=0
    g4: LineSegment [constr] StartX=-41.99 StartY=-5.26 StartZ=0 EndX=-50 EndY=2.75 EndZ=0
    g5: LineSegment [constr] StartX=-50 StartY=2.75 StartZ=0 EndX=-58.01 EndY=-5.26 EndZ=0
    g6: LineSegment [constr] StartX=-58.01 StartY=-5.26 StartZ=0 EndX=-50 EndY=-13.27 EndZ=0
    g7: GeomPoint [constr] X=-50 Y=-5.26 Z=0
  constraints (17):
    c: Coincident(g0,g-4)
    c: Coincident(g3,g4)
    c: Coincident(g4,g5)
    c: Coincident(g5,g6)
    c: Coincident(g6,g3)
    c: Symmetric(g5,g3,g7)
    c: Coincident(g7,g-8)
    c: Equal(g5,g6)
    c: Equal(g6,g3)
    c: Equal(g3,g4)
    c: Coincident(g4,g0)
    c: Coincident(g5,g2)
    c: Coincident(g1,g3)
    c: Equal(g0,g2)
    c: Equal(g2,g1)
    c: Diameter(g1) = 3.9
    c: Perpendicular(g5,g6)
FEATURE [PartDesign::Pocket] Pocket087
  BaseFeature = -> Pad123
  Direction = (0,-1,2e-16)
  Length = 7
  Length2 = 5
  Profile = -> Sketch245
  ReferenceAxis = -> Sketch245 [N_Axis]
  Refine = true
  Suppressed = false
  Type = 0
FEATURE [PartDesign::Body] Body102  label="AdapterPlate"
  AllowCompound = false
  Group = -> [Sketch173,Pad089,Sketch174,Hole024,Sketch175,Hole025,Sketch184,Hole028,Sketch244,Pad123,Sketch245,Pocket087]
  Origin = -> Origin1363
  Placement = pos=(-20,-35.55,11) rot=(0,0,1;0rad)
  Tip = -> Pocket087
FEATURE [App::Part] Part019  label="SpindleMount"
  Group = -> [Body100,Body099,Part018,Body102,Body104]
  Origin = -> Origin1361
  Placement = pos=(-101,209.5,202) rot=(1,0,0;1.5708rad)
FEATURE [PartDesign::Pocket] Pocket088
  BaseFeature = -> Hole027
  Direction = (0,0,1)
  Length = 5
  Length2 = 5
  Profile = -> Hole027 [Face29,Face28]
  Refine = true
  Suppressed = false
  Type = 0
FEATURE [PartDesign::Body] Body107  label="ZmotorHolder"
  AllowCompound = false
  Group = -> [Sketch178,Pad090,Sketch179,Hole026,Pad091,Sketch180,Pad092,Sketch181,Pocket064,Sketch182,Pocket065,Sketch183,Hole027,Pocket088]
  Origin = -> Origin1373
  Placement = pos=(-31,194.5,287) rot=(0,0,1;0rad)
  Tip = -> Pocket088
FEATURE [Sketcher::SketchObject] Sketch246
  ArcFitTolerance = 1e-06
  AttachmentSupport = -> [XY_Plane1078]
  FullyConstrained = true
  MakeInternals = false
  MapMode = 5
  sketch-geometry (2):
    g0: Circle CenterX=0 CenterY=0 CenterZ=0 NormalX=0 NormalY=0 NormalZ=1 AngleXU=0 Radius=4
    g1: Circle CenterX=0 CenterY=0 CenterZ=0 NormalX=0 NormalY=0 NormalZ=1 AngleXU=0 Radius=3
  constraints (4):
    c: Diameter(g0) = 8
    c: Coincident(g0,g-1)
    c: Diameter(g1) = 6
    c: Coincident(g1,g0)
FEATURE [PartDesign::Pad] Pad124
  Direction = (0,0,1)
  Length = 4.5
  Length2 = 10
  Profile = -> Sketch246
  ReferenceAxis = -> Sketch246 [N_Axis]
  Refine = true
  Suppressed = false
  Type = 0
FEATURE [PartDesign::Body] Body141  label="M6 Spacer"
  AllowCompound = false
  Group = -> [Sketch246,Pad124]
  Origin = -> Origin1487
  Tip = -> Pad124
FEATURE [App::Part] Part017  label="zAxis"
  Group = -> [Body094,Body097,Body101,Body103,Body105,Body106,Part019,Body107,Body110,Part020,Body130,Body129,Body141]
  Origin = -> Origin1279
FEATURE [App::Part] Part016  label="xAxis"
  Group = -> [Body084,Body086,Body089,Body090,Body091,Part017,Body109,Body108,Body111,Body112,Body113,Part022]
  Origin = -> Origin1270
FEATURE [App::Part] Part013  label="Frame"
  Group = -> [Body063,Body064,Body065,Body066,Body079,Body078,Body083,Part016,Part001,Body115,Body116,Body117,Body118,Body119,Body120,Body121,Body122,Body124,Body125,Body126,Body127,Part023]
  Origin = -> Origin1206
  Placement = pos=(0,5,0) rot=(0,0,1;0rad)
FEATURE [Sketcher::SketchObject] Sketch247
  ArcFitTolerance = 1e-06
  AttachmentSupport = -> [XY_Plane1079]
  FullyConstrained = true
  MakeInternals = false
  MapMode = 5
  sketch-geometry (14):
    g0: Circle [constr] CenterX=0 CenterY=0 CenterZ=0 NormalX=0 NormalY=0 NormalZ=1 AngleXU=0 Radius=12
    g1: LineSegment StartX=-3.45 StartY=2 StartZ=0 EndX=-3.45 EndY=18.25 EndZ=0
    g2: LineSegment StartX=-3.45 StartY=18.25 StartZ=0 EndX=3.45 EndY=18.25 EndZ=0
    g3: LineSegment StartX=3.45 StartY=18.25 StartZ=0 EndX=3.45 EndY=2 EndZ=0
    g4: LineSegment StartX=3.45 StartY=2 StartZ=0 EndX=9.95 EndY=2 EndZ=0
    g5: LineSegment StartX=9.95 StartY=2 StartZ=0 EndX=9.95 EndY=-2 EndZ=0
    g6: LineSegment StartX=9.95 StartY=-2 StartZ=0 EndX=3.45 EndY=-2 EndZ=0
    g7: LineSegment StartX=3.45 StartY=-2 StartZ=0 EndX=3.45 EndY=-18.25 EndZ=0
    g8: LineSegment StartX=3.45 StartY=-18.25 StartZ=0 EndX=-3.45 EndY=-18.25 EndZ=0
    g9: LineSegment StartX=-3.45 StartY=-18.25 StartZ=0 EndX=-3.45 EndY=-2 EndZ=0
    g10: LineSegment StartX=-3.45 StartY=-2 StartZ=0 EndX=-9.95 EndY=-2 EndZ=0
    g11: LineSegment StartX=-9.95 StartY=-2 StartZ=0 EndX=-9.95 EndY=2 EndZ=0
    g12: LineSegment StartX=-9.95 StartY=2 StartZ=0 EndX=-3.45 EndY=2 EndZ=0
    g13: Circle [constr] CenterX=0 CenterY=0 CenterZ=0 NormalX=0 NormalY=0 NormalZ=1 AngleXU=0 Radius=12
  constraints (39):
    c: Diameter(g0) = 24
    c: Coincident(g0,g-1)
    c: Vertical(g1)
    c: Coincident(g1,g2)
    c: Coincident(g2,g3)
    c: Vertical(g3)
    c: Coincident(g3,g4)
    c: Horizontal(g4)
    c: Coincident(g4,g5)
    c: Vertical(g5)
    c: Coincident(g5,g6)
    c: Horizontal(g6)
    c: Coincident(g6,g7)
    c: Vertical(g7)
    c: Coincident(g7,g8)
    c: Coincident(g8,g9)
    c: Vertical(g9)
    c: Coincident(g9,g10)
    c: Horizontal(g10)
    c: Coincident(g10,g11)
    c: Vertical(g11)
    c: Coincident(g11,g12)
    c: Coincident(g12,g1)
    c: Horizontal(g12)
    c: Horizontal(g8)
    c: Horizontal(g2)
    c: Equal(g3,g1)
    c: Equal(g1,g9)
    c: Equal(g9,g7)
    c: Equal(g6,g4)
    c: Equal(g4,g12)
    c: Equal(g12,g10)
    c: Distance(g2,g2) = 6.9
    c: DistanceY(g5,g5) = 4
    c: DistanceY(g3,g3) = 16.25
    c: DistanceX(g4,g4) = 6.5
    c: Symmetric(g1,g6,g0)
    c: Coincident(g13,g0)
    c: Equal(g13,g0)
FEATURE [PartDesign::Pad] Pad125
  Direction = (0,0,1)
  Length = 4
  Length2 = 10
  Profile = -> Sketch247
  ReferenceAxis = -> Sketch247 [N_Axis]
  Refine = true
  Suppressed = false
  Type = 0
FEATURE [Sketcher::SketchObject] Sketch248
  ArcFitTolerance = 1e-06
  AttachmentSupport = -> [Pad125]
  FullyConstrained = true
  MakeInternals = false
  MapMode = 5
  Placement = pos=(0,0,4) rot=(0,0,1;0rad)
  sketch-geometry (1):
    g0: Circle CenterX=0 CenterY=0 CenterZ=0 NormalX=0 NormalY=0 NormalZ=1 AngleXU=0 Radius=12
  constraints (2):
    c: Diameter(g0) = 24
    c: Coincident(g0,g-1)
FEATURE [PartDesign::Pad] Pad126
  BaseFeature = -> Pad125
  Direction = (0,0,1)
  Length = 12
  Length2 = 10
  Profile = -> Sketch248
  ReferenceAxis = -> Sketch248 [N_Axis]
  Refine = true
  Suppressed = false
  Type = 0
FEATURE [PartDesign::Pocket] Pocket089
  BaseFeature = -> Pad126
  Direction = (0,0,1)
  Length = 8
  Length2 = 5
  Profile = -> Pad126 [Face4]
  Refine = true
  Suppressed = false
  Type = 0
FEATURE [Sketcher::SketchObject] Sketch249
  ArcFitTolerance = 1e-06
  AttachmentSupport = -> [Pocket089]
  FullyConstrained = true
  MakeInternals = false
  MapMode = 5
  Placement = pos=(0,0,16) rot=(0,0,1;0rad)
  sketch-geometry (1):
    g0: Circle CenterX=0 CenterY=0 CenterZ=0 NormalX=0 NormalY=0 NormalZ=1 AngleXU=0 Radius=3.1
  constraints (2):
    c: Diameter(g0) = 6.2
    c: Coincident(g0,g-1)
FEATURE [PartDesign::Pocket] Pocket090
  BaseFeature = -> Pocket089
  Direction = (0,0,-1)
  Length = 5
  Length2 = 5
  Profile = -> Sketch249
  ReferenceAxis = -> Sketch249 [N_Axis]
  Refine = true
  Suppressed = false
  Type = 1
FEATURE [Sketcher::SketchObject] Sketch250
  ArcFitTolerance = 1e-06
  AttachmentSupport = -> [XZ_Plane1079]
  ExternalGeometry = -> [Pocket090]
  FullyConstrained = true
  MakeInternals = false
  MapMode = 5
  Placement = pos=(0,0,0) rot=(1,0,0;1.5708rad)
  sketch-geometry (1):
    g0: Circle CenterX=1e-16 CenterY=12 CenterZ=0 NormalX=0 NormalY=0 NormalZ=1 AngleXU=0 Radius=2.35
  constraints (2):
    c: Diameter(g0) = 4.7
    c: Symmetric(g-4,g-3,g0)
FEATURE [PartDesign::Pocket] Pocket091
  BaseFeature = -> Pocket090
  Direction = (0,1,-2e-16)
  Length = 5
  Length2 = 5
  Profile = -> Sketch250
  ReferenceAxis = -> Sketch250 [N_Axis]
  Refine = true
  Suppressed = false
  Type = 1
FEATURE [Sketcher::SketchObject] Sketch251
  ArcFitTolerance = 1e-06
  AttachmentSupport = -> [Pocket091]
  ExternalGeometry = -> [Pocket091]
  FullyConstrained = false
  MakeInternals = false
  MapMode = 5
  Placement = pos=(0,0,16) rot=(0,0,1;0rad)
  sketch-geometry (4):
    g0: LineSegment StartX=-5 StartY=10.9087 StartZ=0 EndX=5 EndY=10.9087 EndZ=0
    g1: LineSegment StartX=5 StartY=10.9087 StartZ=0 EndX=5 EndY=16.9794 EndZ=0
    g2: LineSegment StartX=5 StartY=16.9794 StartZ=0 EndX=-5 EndY=16.9794 EndZ=0
    g3: LineSegment StartX=-5 StartY=16.9794 StartZ=0 EndX=-5 EndY=10.9087 EndZ=0
  constraints (11):
    c: Coincident(g0,g1)
    c: Coincident(g1,g2)
    c: Coincident(g2,g3)
    c: Coincident(g3,g0)
    c: Horizontal(g0)
    c: Horizontal(g2)
    c: Vertical(g1)
    c: Vertical(g3)
    c: PointOnObject(g0,g-3)
    c: PointOnObject(g0,g-3)
    c: Distance(g0,g0) = 10
FEATURE [PartDesign::Pocket] Pocket092
  BaseFeature = -> Pocket091
  Direction = (0,0,-1)
  Length = 5
  Length2 = 5
  Profile = -> Sketch251
  ReferenceAxis = -> Sketch251 [N_Axis]
  Refine = true
  Suppressed = false
  Type = 1
FEATURE [PartDesign::Body] Body142  label="Servo to pot"
  AllowCompound = false
  Group = -> [Sketch247,Pad125,Sketch248,Pad126,Pocket089,Sketch249,Pocket090,Sketch250,Pocket091,Sketch251,Pocket092]
  Origin = -> Origin1488
  Placement = pos=(0,-90,0) rot=(0,0,1;0rad)
  Tip = -> Pocket092
FEATURE [Sketcher::SketchObject] Sketch252
  ArcFitTolerance = 1e-06
  AttachmentSupport = -> [XY_Plane1080]
  FullyConstrained = true
  MakeInternals = false
  MapMode = 5
  sketch-geometry (8):
    g0: LineSegment StartX=-12.125 StartY=20 StartZ=0 EndX=-6.125 EndY=20 EndZ=0
    g1: LineSegment StartX=-6.125 StartY=20 StartZ=0 EndX=-6.125 EndY=0 EndZ=0
    g2: LineSegment StartX=-6.125 StartY=0 StartZ=0 EndX=6.125 EndY=0 EndZ=0
    g3: LineSegment StartX=6.125 StartY=0 StartZ=0 EndX=6.125 EndY=20 EndZ=0
    g4: LineSegment StartX=6.125 StartY=20 StartZ=0 EndX=12.125 EndY=20 EndZ=0
    g5: LineSegment StartX=12.125 StartY=20 StartZ=0 EndX=12.125 EndY=-8 EndZ=0
    g6: LineSegment StartX=12.125 StartY=-8 StartZ=0 EndX=-12.125 EndY=-8 EndZ=0
    g7: LineSegment StartX=-12.125 StartY=-8 StartZ=0 EndX=-12.125 EndY=20 EndZ=0
  constraints (23):
    c: Horizontal(g0)
    c: Coincident(g0,g1)
    c: PointOnObject(g1,g-1)
    c: Vertical(g1)
    c: Coincident(g1,g2)
    c: Coincident(g2,g3)
    c: Vertical(g3)
    c: Coincident(g3,g4)
    c: Horizontal(g4)
    c: Coincident(g4,g5)
    c: Vertical(g5)
    c: Coincident(g5,g6)
    c: Horizontal(g6)
    c: Coincident(g6,g7)
    c: Coincident(g7,g0)
    c: Vertical(g7)
    c: Equal(g1,g3)
    c: Equal(g0,g4)
    c: DistanceX(g2,g2) = 12.25
    c: DistanceX(g4,g4) = 6
    c: DistanceY(g3,g3) = 20
    c: Distance(g6,g2) = 8
    c: Symmetric(g2,g1,g-1)
FEATURE [PartDesign::Pad] Pad127
  Direction = (0,0,1)
  Length = 20
  Length2 = 10
  Profile = -> Sketch252
  ReferenceAxis = -> Sketch252 [N_Axis]
  Refine = true
  Suppressed = false
  Type = 0
FEATURE [Sketcher::SketchObject] Sketch253
  ArcFitTolerance = 1e-06
  AttachmentSupport = -> [Pad127]
  ExternalGeometry = -> [Pad127]
  FullyConstrained = true
  MakeInternals = false
  MapMode = 5
  Placement = pos=(0,0,20) rot=(0,0,1;0rad)
  sketch-geometry (10):
    g0: ArcOfCircle CenterX=0 CenterY=17.5 CenterZ=0 NormalX=0 NormalY=0 NormalZ=1 AngleXU=0 Radius=13.25 StartAngle=5.33948 EndAngle=10.3685
    g1: LineSegment StartX=-7.775 StartY=6.77098 StartZ=0 EndX=-7.775 EndY=2.77098 EndZ=0
    g2: LineSegment StartX=-7.775 StartY=2.77098 StartZ=0 EndX=7.775 EndY=2.77098 EndZ=0
    g3: LineSegment StartX=7.775 StartY=2.77098 StartZ=0 EndX=7.775 EndY=6.77098 EndZ=0
    g4: Circle CenterX=0 CenterY=17.5 CenterZ=0 NormalX=0 NormalY=0 NormalZ=1 AngleXU=0 Radius=17.25
    g5: LineSegment [constr] StartX=-6.125 StartY=0 StartZ=0 EndX=6.125 EndY=0 EndZ=0
    g6: LineSegment [constr] StartX=6.125 StartY=0 StartZ=0 EndX=6.125 EndY=23 EndZ=0
    g7: LineSegment [constr] StartX=6.125 StartY=23 StartZ=0 EndX=-6.125 EndY=23 EndZ=0
    g8: LineSegment [constr] StartX=-6.125 StartY=23 StartZ=0 EndX=-6.125 EndY=0 EndZ=0
    g9: GeomPoint [constr] X=0 Y=17.5 Z=0
  constraints (28):
    c: Coincident(g0,g1)
    c: Vertical(g1)
    c: Coincident(g1,g2)
    c: Horizontal(g2)
    c: Coincident(g2,g3)
    c: Coincident(g3,g0)
    c: Vertical(g3)
    c: Equal(g1,g3)
    c: DistanceX(g2,g2) = 15.55
    c: Radius(g0) = 13.25
    c: Distance(g3,g3) = 4
    c: Distance(g4,g0) = 4
    c: Coincident(g4,g0)
    c: Coincident(g5,g6)
    c: Coincident(g6,g7)
    c: Coincident(g7,g8)
    c: Coincident(g8,g5)
    c: Horizontal(g5)
    c: Horizontal(g7)
    c: Vertical(g6)
    c: Vertical(g8)
    c: Coincident(g5,g-4)
    c: PointOnObject(g-3,g6)
    c: DistanceY(g6,g6) = 23
    c: PointOnObject(g9,g-2)
    c: DistanceY(g5,g9) = 17.5
    c: DistanceY(g9,g6) = 5.5
    c: Coincident(g0,g9)
FEATURE [PartDesign::Pad] Pad128
  BaseFeature = -> Pad127
  Direction = (0,0,1)
  Length = 40
  Length2 = 10
  Profile = -> Sketch253
  ReferenceAxis = -> Sketch253 [N_Axis]
  Refine = true
  Suppressed = false
  Type = 0
FEATURE [PartDesign::Body] Body143  label="potHolder"
  AllowCompound = false
  Group = -> [Sketch252,Pad127,Sketch253,Pad128]
  Origin = -> Origin1489
  Tip = -> Pad128
FEATURE [Sketcher::SketchObject] Sketch254
  ArcFitTolerance = 1e-06
  AttachmentSupport = -> [Pad115]
  ExternalGeometry = -> [Pad115]
  FullyConstrained = true
  MakeInternals = false
  MapMode = 5
  Placement = pos=(85,-5.66e-14,2.9) rot=(0,0,1;0rad)
  sketch-geometry (6):
    g0: LineSegment StartX=3.5 StartY=10.05 StartZ=0 EndX=3.5 EndY=4.45 EndZ=0
    g1: LineSegment StartX=3.5 StartY=4.45 StartZ=0 EndX=11.5 EndY=4.45 EndZ=0
    g2: LineSegment StartX=11.5 StartY=4.45 StartZ=0 EndX=11.5 EndY=10.05 EndZ=0
    g3: LineSegment StartX=11.5 StartY=10.05 StartZ=0 EndX=3.5 EndY=10.05 EndZ=0
    g4: LineSegment [constr] StartX=0 StartY=4.45 StartZ=0 EndX=3.5 EndY=4.45 EndZ=0
    g5: LineSegment [constr] StartX=11.5 StartY=4.45 StartZ=0 EndX=15 EndY=4.45 EndZ=0
  constraints (16):
    c: Coincident(g0,g1)
    c: Coincident(g1,g2)
    c: Coincident(g2,g3)
    c: Coincident(g3,g0)
    c: Vertical(g0)
    c: Vertical(g2)
    c: Horizontal(g1)
    c: Horizontal(g3)
    c: PointOnObject(g0,g-3)
    c: PointOnObject(g1,g-4)
    c: Coincident(g4,g-4)
    c: Coincident(g4,g0)
    c: Coincident(g5,g1)
    c: Coincident(g5,g-4)
    c: Equal(g5,g4)
    c: DistanceX(g1,g1) = 8
FEATURE [PartDesign::Pocket] Pocket093
  BaseFeature = -> Pad115
  Direction = (0,0,-1)
  Length = 5
  Length2 = 5
  Placement = pos=(85,-5.66e-14,2.83e-14) rot=(0,0,1;0rad)
  Profile = -> Sketch254
  ReferenceAxis = -> Sketch254 [N_Axis]
  Refine = true
  Suppressed = false
  Type = 0
FEATURE [PartDesign::Body] Body137  label="2020to1515"
  AllowCompound = false
  Group = -> [CopyPad114,Sketch231,Pad115,Sketch254,Pocket093]
  Origin = -> Origin1483
  Tip = -> Pocket093
